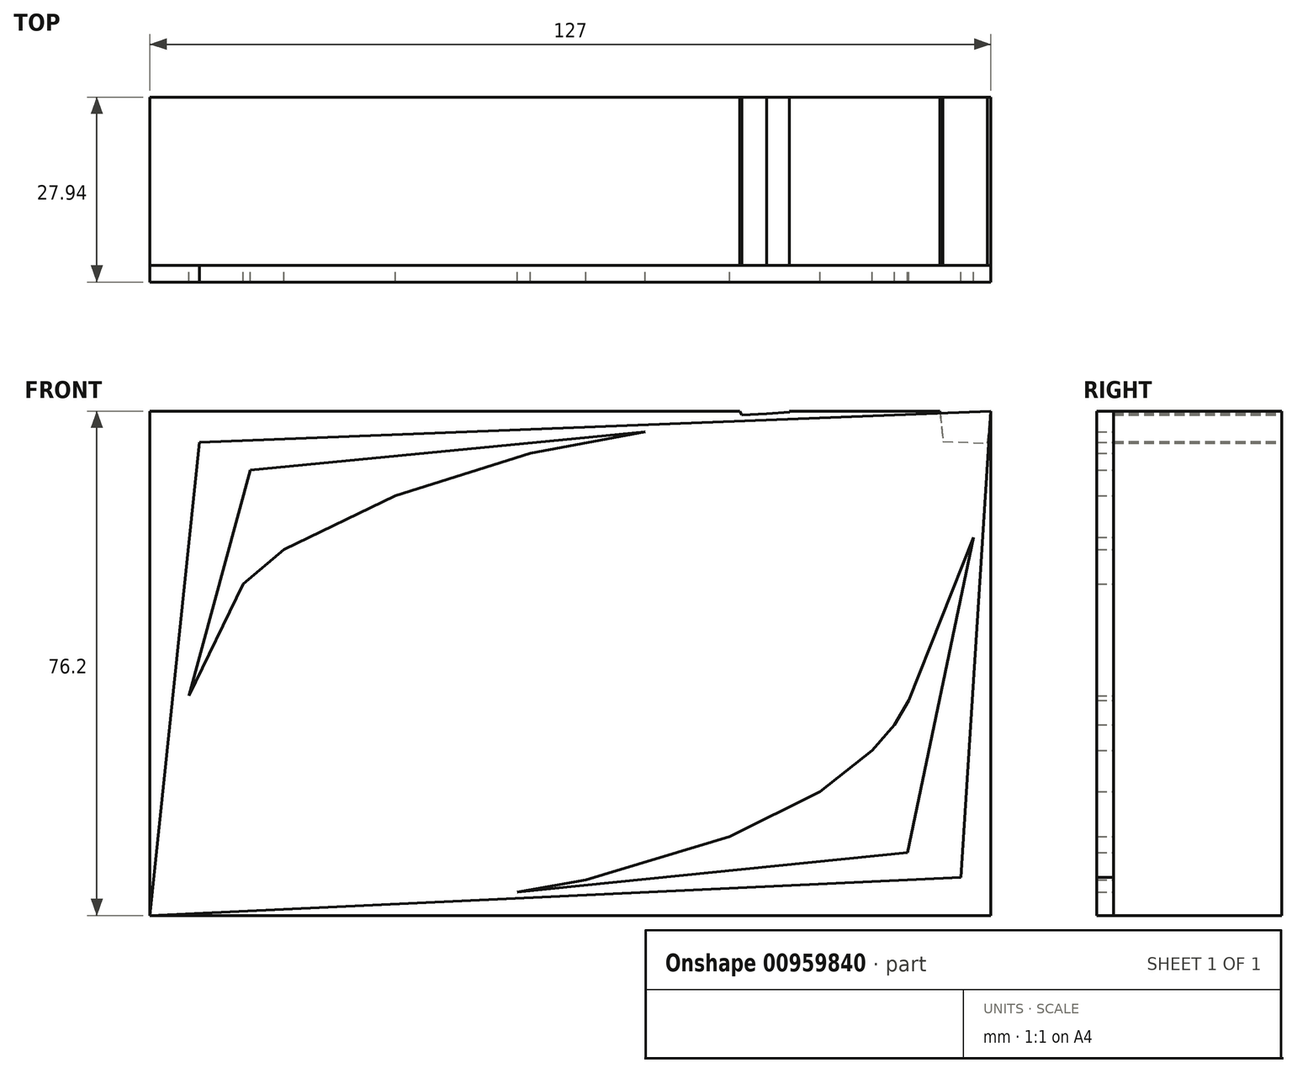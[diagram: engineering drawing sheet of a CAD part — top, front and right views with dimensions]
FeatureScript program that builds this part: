
annotation { "Feature Type Name" : "Feature", "Feature Type Description" : "" }
export const myFeature = defineFeature(function(context is Context, id is Id, definition is map)
    precondition{}
    {
        {
            var Q0;
            Q0=qCreatedBy(makeId("Front.planeOp"),FACE);
            var sketch = newSketch(context, id + "F0", { "sketchPlane" : qUnion([Q0])});
            skLineSegment(sketch, "E0.bottom", {"start": v(-63.5, -38.1) * mm, "end": v(63.5, -38.1) * mm});
            skLineSegment(sketch, "E0.top", {"start": v(-63.5, 38.1) * mm, "end": v(63.5, 38.1) * mm});
            skLineSegment(sketch, "E0.left", {"start": v(-63.5, -38.1) * mm, "end": v(-63.5, 38.1) * mm});
            skLineSegment(sketch, "E0.right", {"start": v(63.5, -38.1) * mm, "end": v(63.5, 38.1) * mm});
            skPoint(sketch, "E0.middle", {"position": v(0, 0) * mm});
            skLineSegment(sketch, "E1", {"start": v(-63.5, -38.1) * mm, "end": v(63.5, -30.09) * mm});
            skLineSegment(sketch, "E2", {"start": v(-48.57, -38.1) * mm, "end": v(63.5, -22.97) * mm});
            skLineSegment(sketch, "E3", {"start": v(-38.6, -38.1) * mm, "end": v(63.5, -16.2) * mm});
            skLineSegment(sketch, "E4", {"start": v(-28.65, -38.1) * mm, "end": v(63.5, -8.03) * mm});
            skLineSegment(sketch, "E5", {"start": v(-17.63, -38.1) * mm, "end": v(63.5, -2.7) * mm});
            skLineSegment(sketch, "E6", {"start": v(-6.25, -38.1) * mm, "end": v(63.5, 0) * mm});
            skLineSegment(sketch, "E7", {"start": v(4.78, -38.1) * mm, "end": v(63.5, 6.2) * mm});
            skLineSegment(sketch, "E8", {"start": v(14.74, -38.1) * mm, "end": v(63.5, 11.89) * mm});
            skLineSegment(sketch, "E9", {"start": v(22.91, -38.1) * mm, "end": v(63.5, 18.28) * mm});
            skLineSegment(sketch, "E10", {"start": v(28.6, -38.1) * mm, "end": v(63.5, 23.27) * mm});
            skLineSegment(sketch, "E11", {"start": v(33.59, -38.1) * mm, "end": v(63.5, 29.32) * mm});
            skLineSegment(sketch, "E12", {"start": v(42.12, -38.1) * mm, "end": v(63.5, 33.23) * mm});
            skLineSegment(sketch, "E13", {"start": v(49.59, -38.1) * mm, "end": v(63.5, 33.23) * mm});
            skLineSegment(sketch, "E14", {"start": v(55.63, -38.1) * mm, "end": v(63.5, 38.1) * mm});
            skLineSegment(sketch, "E15", {"start": v(63.5, -38.1) * mm, "end": v(-63.5, -29.2) * mm});
            skLineSegment(sketch, "E16", {"start": v(55.63, -38.1) * mm, "end": v(-63.5, -21.73) * mm});
            skLineSegment(sketch, "E17", {"start": v(42.12, -38.1) * mm, "end": v(-63.5, -15.34) * mm});
            skLineSegment(sketch, "E18", {"start": v(33.59, -38.1) * mm, "end": v(-63.5, -10.35) * mm});
            skLineSegment(sketch, "E19", {"start": v(22.91, -38.1) * mm, "end": v(-63.5, -4.3) * mm});
            skLineSegment(sketch, "E20", {"start": v(14.74, -38.1) * mm, "end": v(-63.5, 0) * mm});
            skLineSegment(sketch, "E21", {"start": v(4.78, -38.1) * mm, "end": v(-63.5, 4.94) * mm});
            skLineSegment(sketch, "E22", {"start": v(-6.25, -38.1) * mm, "end": v(-63.5, 9.2) * mm});
            skLineSegment(sketch, "E23", {"start": v(-17.63, -38.1) * mm, "end": v(-63.5, 14.2) * mm});
            skLineSegment(sketch, "E24", {"start": v(-28.65, -38.1) * mm, "end": v(-63.5, 22.38) * mm});
            skLineSegment(sketch, "E25", {"start": v(-38.6, -38.1) * mm, "end": v(-63.5, 29.84) * mm});
            skLineSegment(sketch, "E26", {"start": v(-48.57, -38.1) * mm, "end": v(-63.5, 33.39) * mm});
            skLineSegment(sketch, "E27", {"start": v(-57.13, -37.7) * mm, "end": v(-63.5, 38.1) * mm});
            skLineSegment(sketch, "E28", {"start": v(-63.5, 38.1) * mm, "end": v(63.5, 33.23) * mm});
            skLineSegment(sketch, "E29", {"start": v(-56.64, 37.84) * mm, "end": v(63.5, 29.32) * mm});
            skLineSegment(sketch, "E30", {"start": v(-49.83, 38.1) * mm, "end": v(63.5, 23.27) * mm});
            skLineSegment(sketch, "E31", {"start": v(-42, 38.1) * mm, "end": v(63.5, 18.28) * mm});
            skLineSegment(sketch, "E32", {"start": v(-33.47, 38.1) * mm, "end": v(63.5, 11.89) * mm});
            skLineSegment(sketch, "E33", {"start": v(-25.3, 38.1) * mm, "end": v(63.5, 6.2) * mm});
            skLineSegment(sketch, "E34", {"start": v(-17.11, 38.1) * mm, "end": v(63.5, 0) * mm});
            skLineSegment(sketch, "E35", {"start": v(-9.65, 38.1) * mm, "end": v(63.5, -2.7) * mm});
            skLineSegment(sketch, "E36", {"start": v(0, 38.1) * mm, "end": v(63.5, -8.03) * mm});
            skLineSegment(sketch, "E37", {"start": v(7.43, 38.1) * mm, "end": v(63.5, -16.2) * mm});
            skLineSegment(sketch, "E38", {"start": v(13.84, 38.1) * mm, "end": v(63.5, -22.97) * mm});
            skLineSegment(sketch, "E39", {"start": v(25.57, 38.1) * mm, "end": v(63.5, -30.09) * mm});
            skLineSegment(sketch, "E40", {"start": v(33.04, 38.1) * mm, "end": v(63.5, -33.99) * mm});
            skLineSegment(sketch, "E41", {"start": v(39.09, 38.1) * mm, "end": v(63.5, -30.09) * mm});
            skLineSegment(sketch, "E42", {"start": v(48.32, 38.1) * mm, "end": v(63.5, -33.99) * mm});
            skLineSegment(sketch, "E43", {"start": v(55.8, 38.1) * mm, "end": v(63.5, -38.1) * mm});
            skLineSegment(sketch, "E44", {"start": v(-63.5, -38.1) * mm, "end": v(-56.64, 37.84) * mm});
            skLineSegment(sketch, "E45", {"start": v(-63.5, -29.2) * mm, "end": v(-49.83, 38.1) * mm});
            skLineSegment(sketch, "E46", {"start": v(-63.5, -21.73) * mm, "end": v(-42, 38.1) * mm});
            skLineSegment(sketch, "E47", {"start": v(-63.5, -15.34) * mm, "end": v(-33.47, 38.1) * mm});
            skLineSegment(sketch, "E48", {"start": v(-63.5, -10.35) * mm, "end": v(-25.3, 38.1) * mm});
            skLineSegment(sketch, "E49", {"start": v(-63.5, -4.3) * mm, "end": v(-17.11, 38.1) * mm});
            skLineSegment(sketch, "E50", {"start": v(-63.5, 0) * mm, "end": v(-9.65, 38.1) * mm});
            skLineSegment(sketch, "E51", {"start": v(-63.5, 4.94) * mm, "end": v(0, 38.1) * mm});
            skLineSegment(sketch, "E52", {"start": v(-63.5, 9.2) * mm, "end": v(7.43, 38.1) * mm});
            skLineSegment(sketch, "E53", {"start": v(-63.5, 14.2) * mm, "end": v(13.84, 38.1) * mm});
            skLineSegment(sketch, "E54", {"start": v(-61.95, 19.7) * mm, "end": v(13.84, 38.1) * mm});
            skLineSegment(sketch, "E55", {"start": v(-63.5, 22.38) * mm, "end": v(25.57, 38.1) * mm});
            skLineSegment(sketch, "E56", {"start": v(-62.6, 27.38) * mm, "end": v(25.57, 38.1) * mm});
            skLineSegment(sketch, "E57", {"start": v(-63.5, 29.84) * mm, "end": v(34.8, 38.1) * mm});
            skLineSegment(sketch, "E58", {"start": v(-63.5, 33.39) * mm, "end": v(39.09, 38.1) * mm});
            skLineSegment(sketch, "E59", {"start": v(-63.5, 38.1) * mm, "end": v(59.36, 38.1) * mm});
            skSolve(sketch);
        }
        {
            var Q0;
            {var subQ0=sQuery(id+"F0.wireOp",EDGE,"E2");var subQ3=sQuery(id+"F0.wireOp",EDGE,"E25");var subQ5=makeQuery(id+"F0.imprint","INTERSECT",VERTEX,{"derivedFrom":[subQ0,subQ3]});Q0=makeQuery(id+"F0.imprint","IMPRINT",FACE,{"disambiguationData":[TD([[makeQuery(id+"F0.imprint","IMPRINT",EDGE,{"disambiguationData":[TD([[subQ5,1.0]])],"derivedFrom":subQ0}),-1.0]])]});}
            var Q1;
            {var subQ0=sQuery(id+"F0.wireOp",EDGE,"E3");var subQ3=sQuery(id+"F0.wireOp",EDGE,"E24");var subQ5=makeQuery(id+"F0.imprint","INTERSECT",VERTEX,{"derivedFrom":[subQ0,subQ3]});Q1=makeQuery(id+"F0.imprint","IMPRINT",FACE,{"disambiguationData":[TD([[makeQuery(id+"F0.imprint","IMPRINT",EDGE,{"disambiguationData":[TD([[subQ5,1.0]])],"derivedFrom":subQ0}),-1.0]])]});}
            var Q2;
            {var subQ0=sQuery(id+"F0.wireOp",EDGE,"E5");var subQ3=sQuery(id+"F0.wireOp",EDGE,"E22");var subQ5=makeQuery(id+"F0.imprint","INTERSECT",VERTEX,{"derivedFrom":[subQ0,subQ3]});Q2=makeQuery(id+"F0.imprint","IMPRINT",FACE,{"disambiguationData":[TD([[makeQuery(id+"F0.imprint","IMPRINT",EDGE,{"disambiguationData":[TD([[subQ5,1.0]])],"derivedFrom":subQ0}),-1.0]])]});}
            var Q3;
            {var subQ0=sQuery(id+"F0.wireOp",EDGE,"E6");var subQ3=sQuery(id+"F0.wireOp",EDGE,"E21");var subQ5=makeQuery(id+"F0.imprint","INTERSECT",VERTEX,{"derivedFrom":[subQ0,subQ3]});Q3=makeQuery(id+"F0.imprint","IMPRINT",FACE,{"disambiguationData":[TD([[makeQuery(id+"F0.imprint","IMPRINT",EDGE,{"disambiguationData":[TD([[subQ5,1.0]])],"derivedFrom":subQ0}),-1.0]])]});}
            var Q4;
            {var subQ0=sQuery(id+"F0.wireOp",EDGE,"E7");var subQ3=sQuery(id+"F0.wireOp",EDGE,"E20");var subQ5=makeQuery(id+"F0.imprint","INTERSECT",VERTEX,{"derivedFrom":[subQ0,subQ3]});Q4=makeQuery(id+"F0.imprint","IMPRINT",FACE,{"disambiguationData":[TD([[makeQuery(id+"F0.imprint","IMPRINT",EDGE,{"disambiguationData":[TD([[subQ5,1.0]])],"derivedFrom":subQ0}),-1.0]])]});}
            var Q5;
            {var subQ0=sQuery(id+"F0.wireOp",EDGE,"E8");var subQ3=sQuery(id+"F0.wireOp",EDGE,"E19");var subQ5=makeQuery(id+"F0.imprint","INTERSECT",VERTEX,{"derivedFrom":[subQ0,subQ3]});Q5=makeQuery(id+"F0.imprint","IMPRINT",FACE,{"disambiguationData":[TD([[makeQuery(id+"F0.imprint","IMPRINT",EDGE,{"disambiguationData":[TD([[subQ5,1.0]])],"derivedFrom":subQ0}),-1.0]])]});}
            var Q6;
            {var subQ0=sQuery(id+"F0.wireOp",EDGE,"E10");var subQ1=sQuery(id+"F0.wireOp",EDGE,"E0.bottom");var subQ2=makeQuery(id+"F0.imprint","INTERSECT",VERTEX,{"derivedFrom":[subQ1,subQ0]});Q6=makeQuery(id+"F0.imprint","IMPRINT",FACE,{"disambiguationData":[TD([[makeQuery(id+"F0.imprint","IMPRINT",EDGE,{"disambiguationData":[TD([[subQ2,-1.0]])],"derivedFrom":subQ0}),-1.0]])]});}
            var Q7;
            {var subQ0=sQuery(id+"F0.wireOp",EDGE,"E11");var subQ3=sQuery(id+"F0.wireOp",EDGE,"E17");var subQ5=makeQuery(id+"F0.imprint","INTERSECT",VERTEX,{"derivedFrom":[subQ0,subQ3]});Q7=makeQuery(id+"F0.imprint","IMPRINT",FACE,{"disambiguationData":[TD([[makeQuery(id+"F0.imprint","IMPRINT",EDGE,{"disambiguationData":[TD([[subQ5,1.0]])],"derivedFrom":subQ0}),-1.0]])]});}
            var Q8;
            {var subQ0=sQuery(id+"F0.wireOp",EDGE,"E13");var subQ1=sQuery(id+"F0.wireOp",EDGE,"E0.bottom");var subQ2=makeQuery(id+"F0.imprint","INTERSECT",VERTEX,{"derivedFrom":[subQ1,subQ0]});Q8=makeQuery(id+"F0.imprint","IMPRINT",FACE,{"disambiguationData":[TD([[makeQuery(id+"F0.imprint","IMPRINT",EDGE,{"disambiguationData":[TD([[subQ2,-1.0]])],"derivedFrom":subQ0}),-1.0]])]});}
            var Q9;
            {var subQ0=sQuery(id+"F0.wireOp",EDGE,"E15");var subQ3=sQuery(id+"F0.wireOp",EDGE,"E14");var subQ5=makeQuery(id+"F0.imprint","INTERSECT",VERTEX,{"derivedFrom":[subQ3,subQ0]});Q9=makeQuery(id+"F0.imprint","IMPRINT",FACE,{"disambiguationData":[TD([[makeQuery(id+"F0.imprint","IMPRINT",EDGE,{"disambiguationData":[TD([[subQ5,1.0]])],"derivedFrom":subQ3}),-1.0]])]});}
            var Q10;
            {var subQ0=sQuery(id+"F0.wireOp",EDGE,"E44");var subQ3=sQuery(id+"F0.wireOp",EDGE,"E15");var subQ5=makeQuery(id+"F0.imprint","INTERSECT",VERTEX,{"derivedFrom":[subQ3,subQ0]});Q10=makeQuery(id+"F0.imprint","IMPRINT",FACE,{"disambiguationData":[TD([[makeQuery(id+"F0.imprint","IMPRINT",EDGE,{"disambiguationData":[TD([[subQ5,-1.0]])],"derivedFrom":subQ3}),1.0]])]});}
            var Q11;
            {var subQ0=sQuery(id+"F0.wireOp",EDGE,"E47");var subQ3=sQuery(id+"F0.wireOp",EDGE,"E18");var subQ5=makeQuery(id+"F0.imprint","INTERSECT",VERTEX,{"derivedFrom":[subQ3,subQ0]});Q11=makeQuery(id+"F0.imprint","IMPRINT",FACE,{"disambiguationData":[TD([[makeQuery(id+"F0.imprint","IMPRINT",EDGE,{"disambiguationData":[TD([[subQ5,-1.0]])],"derivedFrom":subQ3}),1.0]])]});}
            var Q12;
            {var subQ0=sQuery(id+"F0.wireOp",EDGE,"E49");var subQ3=sQuery(id+"F0.wireOp",EDGE,"E20");var subQ5=makeQuery(id+"F0.imprint","INTERSECT",VERTEX,{"derivedFrom":[subQ3,subQ0]});Q12=makeQuery(id+"F0.imprint","IMPRINT",FACE,{"disambiguationData":[TD([[makeQuery(id+"F0.imprint","IMPRINT",EDGE,{"disambiguationData":[TD([[subQ5,-1.0]])],"derivedFrom":subQ3}),1.0]])]});}
            var Q13;
            {var subQ0=sQuery(id+"F0.wireOp",EDGE,"E27");var subQ3=sQuery(id+"F0.wireOp",EDGE,"E58");var subQ5=makeQuery(id+"F0.imprint","INTERSECT",VERTEX,{"derivedFrom":[subQ0,subQ3]});Q13=makeQuery(id+"F0.imprint","IMPRINT",FACE,{"disambiguationData":[TD([[makeQuery(id+"F0.imprint","IMPRINT",EDGE,{"disambiguationData":[TD([[subQ5,1.0]])],"derivedFrom":subQ3}),1.0]])]});}
            var Q14;
            {var subQ0=sQuery(id+"F0.wireOp",EDGE,"E43");var subQ3=sQuery(id+"F0.wireOp",EDGE,"E40");var subQ5=makeQuery(id+"F0.imprint","INTERSECT",VERTEX,{"derivedFrom":[subQ3,subQ0]});Q14=makeQuery(id+"F0.imprint","IMPRINT",FACE,{"disambiguationData":[TD([[makeQuery(id+"F0.imprint","IMPRINT",EDGE,{"disambiguationData":[TD([[subQ5,-1.0]])],"derivedFrom":subQ3}),-1.0]])]});}
            var Q15;
            {var subQ0=sQuery(id+"F0.wireOp",EDGE,"E35");var subQ3=sQuery(id+"F0.wireOp",EDGE,"E6");var subQ5=makeQuery(id+"F0.imprint","INTERSECT",VERTEX,{"derivedFrom":[subQ3,subQ0]});Q15=makeQuery(id+"F0.imprint","IMPRINT",FACE,{"disambiguationData":[TD([[makeQuery(id+"F0.imprint","IMPRINT",EDGE,{"disambiguationData":[TD([[subQ5,-1.0]])],"derivedFrom":subQ3}),-1.0]])]});}
            var Q16;
            {var subQ0=sQuery(id+"F0.wireOp",EDGE,"E29");var subQ3=sQuery(id+"F0.wireOp",EDGE,"E13");var subQ5=makeQuery(id+"F0.imprint","INTERSECT",VERTEX,{"derivedFrom":[subQ3,subQ0]});Q16=makeQuery(id+"F0.imprint","IMPRINT",FACE,{"disambiguationData":[TD([[makeQuery(id+"F0.imprint","IMPRINT",EDGE,{"disambiguationData":[TD([[subQ5,-1.0]])],"derivedFrom":subQ0}),1.0]])]});}
            var Q17;
            {var subQ0=sQuery(id+"F0.wireOp",EDGE,"E14");var subQ3=sQuery(id+"F0.wireOp",EDGE,"E28");var subQ5=makeQuery(id+"F0.imprint","INTERSECT",VERTEX,{"derivedFrom":[subQ0,subQ3]});Q17=makeQuery(id+"F0.imprint","IMPRINT",FACE,{"disambiguationData":[TD([[makeQuery(id+"F0.imprint","IMPRINT",EDGE,{"disambiguationData":[TD([[subQ5,-1.0]])],"derivedFrom":subQ0}),-1.0]])]});}
            var Q18;
            {var subQ1=sQuery(id+"F0.wireOp",EDGE,"E37");var subQ3=sQuery(id+"F0.wireOp",EDGE,"E54");var subQ4=makeQuery(id+"F0.imprint","INTERSECT",VERTEX,{"derivedFrom":[subQ1,subQ3]});Q18=makeQuery(id+"F0.imprint","IMPRINT",FACE,{"disambiguationData":[TD([[makeQuery(id+"F0.imprint","IMPRINT",EDGE,{"disambiguationData":[TD([[subQ4,1.0]])],"derivedFrom":subQ1}),1.0]])]});}
            var Q19;
            {var subQ0=sQuery(id+"F0.wireOp",EDGE,"E59");var subQ1=sQuery(id+"F0.wireOp",EDGE,"E40");var subQ2=makeQuery(id+"F0.imprint","INTERSECT",VERTEX,{"derivedFrom":[subQ1,subQ0]});Q19=makeQuery(id+"F0.imprint","IMPRINT",FACE,{"disambiguationData":[TD([[makeQuery(id+"F0.imprint","IMPRINT",EDGE,{"disambiguationData":[TD([[subQ2,-1.0]])],"derivedFrom":subQ1}),1.0]])]});}
            var Q20;
            {var subQ0=sQuery(id+"F0.wireOp",EDGE,"E1");var subQ5=makeQuery(id+"F0.imprint","INTERSECT",VERTEX,{"derivedFrom":[subQ0,sQuery(id+"F0.wireOp",EDGE,"E27")]});Q20=makeQuery(id+"F0.imprint","IMPRINT",FACE,{"disambiguationData":[TD([[makeQuery(id+"F0.imprint","IMPRINT",EDGE,{"disambiguationData":[TD([[subQ5,-1.0]])],"derivedFrom":subQ0}),-1.0]])]});}
            var Q21;
            {var subQ0=sQuery(id+"F0.wireOp",EDGE,"E4");var subQ5=sQuery(id+"F0.wireOp",EDGE,"E1");var subQ6=makeQuery(id+"F0.imprint","INTERSECT",VERTEX,{"derivedFrom":[subQ5,subQ0]});Q21=makeQuery(id+"F0.imprint","IMPRINT",FACE,{"disambiguationData":[TD([[makeQuery(id+"F0.imprint","IMPRINT",EDGE,{"disambiguationData":[TD([[subQ6,-1.0]])],"derivedFrom":subQ5}),-1.0]])]});}
            var Q22;
            {var subQ1=sQuery(id+"F0.wireOp",EDGE,"E0.bottom");var subQ3=sQuery(id+"F0.wireOp",EDGE,"E10");var subQ4=makeQuery(id+"F0.imprint","INTERSECT",VERTEX,{"derivedFrom":[subQ1,subQ3]});Q22=makeQuery(id+"F0.imprint","IMPRINT",FACE,{"disambiguationData":[TD([[makeQuery(id+"F0.imprint","IMPRINT",EDGE,{"disambiguationData":[TD([[subQ4,-1.0]])],"derivedFrom":subQ3}),1.0]])]});}
            var Q23;
            {var subQ7=sQuery(id+"F0.wireOp",EDGE,"E0.top");Q23=makeQuery(id+"F0.imprint","IMPRINT",FACE,{"disambiguationData":[TD([[makeQuery(id+"F0.imprint","IMPRINT",EDGE,{"derivedFrom":subQ7}),-1.0]])]});}
            var Q24;
            {var subQ3=sQuery(id+"F0.wireOp",EDGE,"E16");var subQ5=sQuery(id+"F0.wireOp",EDGE,"E44");var subQ6=makeQuery(id+"F0.imprint","INTERSECT",VERTEX,{"derivedFrom":[subQ3,subQ5]});Q24=makeQuery(id+"F0.imprint","IMPRINT",FACE,{"disambiguationData":[TD([[makeQuery(id+"F0.imprint","IMPRINT",EDGE,{"disambiguationData":[TD([[subQ6,1.0]])],"derivedFrom":subQ5}),1.0]])]});}
            var Q25;
            {var subQ3=sQuery(id+"F0.wireOp",EDGE,"E17");var subQ5=sQuery(id+"F0.wireOp",EDGE,"E44");var subQ6=makeQuery(id+"F0.imprint","INTERSECT",VERTEX,{"derivedFrom":[subQ3,subQ5]});Q25=makeQuery(id+"F0.imprint","IMPRINT",FACE,{"disambiguationData":[TD([[makeQuery(id+"F0.imprint","IMPRINT",EDGE,{"disambiguationData":[TD([[subQ6,1.0]])],"derivedFrom":subQ5}),1.0]])]});}
            var Q26;
            {var subQ3=sQuery(id+"F0.wireOp",EDGE,"E19");var subQ5=sQuery(id+"F0.wireOp",EDGE,"E44");var subQ6=makeQuery(id+"F0.imprint","INTERSECT",VERTEX,{"derivedFrom":[subQ3,subQ5]});Q26=makeQuery(id+"F0.imprint","IMPRINT",FACE,{"disambiguationData":[TD([[makeQuery(id+"F0.imprint","IMPRINT",EDGE,{"disambiguationData":[TD([[subQ6,1.0]])],"derivedFrom":subQ5}),1.0]])]});}
            var Q27;
            {var subQ3=sQuery(id+"F0.wireOp",EDGE,"E21");var subQ5=sQuery(id+"F0.wireOp",EDGE,"E27");var subQ6=makeQuery(id+"F0.imprint","INTERSECT",VERTEX,{"derivedFrom":[subQ3,subQ5]});Q27=makeQuery(id+"F0.imprint","IMPRINT",FACE,{"disambiguationData":[TD([[makeQuery(id+"F0.imprint","IMPRINT",EDGE,{"disambiguationData":[TD([[subQ6,1.0]])],"derivedFrom":subQ5}),1.0]])]});}
            var Q28;
            {var subQ3=sQuery(id+"F0.wireOp",EDGE,"E22");var subQ5=sQuery(id+"F0.wireOp",EDGE,"E27");var subQ6=makeQuery(id+"F0.imprint","INTERSECT",VERTEX,{"derivedFrom":[subQ3,subQ5]});Q28=makeQuery(id+"F0.imprint","IMPRINT",FACE,{"disambiguationData":[TD([[makeQuery(id+"F0.imprint","IMPRINT",EDGE,{"disambiguationData":[TD([[subQ6,1.0]])],"derivedFrom":subQ5}),1.0]])]});}
            var Q29;
            {var subQ3=sQuery(id+"F0.wireOp",EDGE,"E23");var subQ5=sQuery(id+"F0.wireOp",EDGE,"E27");var subQ6=makeQuery(id+"F0.imprint","INTERSECT",VERTEX,{"derivedFrom":[subQ3,subQ5]});Q29=makeQuery(id+"F0.imprint","IMPRINT",FACE,{"disambiguationData":[TD([[makeQuery(id+"F0.imprint","IMPRINT",EDGE,{"disambiguationData":[TD([[subQ6,1.0]])],"derivedFrom":subQ5}),1.0]])]});}
            var Q30;
            {var subQ0=sQuery(id+"F0.wireOp",EDGE,"E53");var subQ5=sQuery(id+"F0.wireOp",EDGE,"E27");var subQ7=makeQuery(id+"F0.imprint","INTERSECT",VERTEX,{"derivedFrom":[subQ5,subQ0]});Q30=makeQuery(id+"F0.imprint","IMPRINT",FACE,{"disambiguationData":[TD([[makeQuery(id+"F0.imprint","IMPRINT",EDGE,{"disambiguationData":[TD([[subQ7,-1.0]])],"derivedFrom":subQ5}),1.0]])]});}
            var Q31;
            {var subQ0=sQuery(id+"F0.wireOp",EDGE,"E55");var subQ5=sQuery(id+"F0.wireOp",EDGE,"E27");var subQ7=makeQuery(id+"F0.imprint","INTERSECT",VERTEX,{"derivedFrom":[subQ5,subQ0]});Q31=makeQuery(id+"F0.imprint","IMPRINT",FACE,{"disambiguationData":[TD([[makeQuery(id+"F0.imprint","IMPRINT",EDGE,{"disambiguationData":[TD([[subQ7,-1.0]])],"derivedFrom":subQ5}),1.0]])]});}
            var Q32;
            {var subQ3=sQuery(id+"F0.wireOp",EDGE,"E26");var subQ5=sQuery(id+"F0.wireOp",EDGE,"E27");var subQ6=makeQuery(id+"F0.imprint","INTERSECT",VERTEX,{"derivedFrom":[subQ3,subQ5]});Q32=makeQuery(id+"F0.imprint","IMPRINT",FACE,{"disambiguationData":[TD([[makeQuery(id+"F0.imprint","IMPRINT",EDGE,{"disambiguationData":[TD([[subQ6,1.0]])],"derivedFrom":subQ5}),1.0]])]});}
            var Q33;
            {var subQ0=sQuery(id+"F0.wireOp",EDGE,"E1");var subQ5=sQuery(id+"F0.wireOp",EDGE,"E43");var subQ6=makeQuery(id+"F0.imprint","INTERSECT",VERTEX,{"derivedFrom":[subQ0,subQ5]});Q33=makeQuery(id+"F0.imprint","IMPRINT",FACE,{"disambiguationData":[TD([[makeQuery(id+"F0.imprint","IMPRINT",EDGE,{"disambiguationData":[TD([[subQ6,-1.0]])],"derivedFrom":subQ5}),1.0]])]});}
            var Q34;
            {var subQ3=sQuery(id+"F0.wireOp",EDGE,"E2");var subQ5=sQuery(id+"F0.wireOp",EDGE,"E43");var subQ6=makeQuery(id+"F0.imprint","INTERSECT",VERTEX,{"derivedFrom":[subQ3,subQ5]});Q34=makeQuery(id+"F0.imprint","IMPRINT",FACE,{"disambiguationData":[TD([[makeQuery(id+"F0.imprint","IMPRINT",EDGE,{"disambiguationData":[TD([[subQ6,-1.0]])],"derivedFrom":subQ5}),1.0]])]});}
            var Q35;
            {var subQ3=sQuery(id+"F0.wireOp",EDGE,"E3");var subQ5=sQuery(id+"F0.wireOp",EDGE,"E43");var subQ6=makeQuery(id+"F0.imprint","INTERSECT",VERTEX,{"derivedFrom":[subQ3,subQ5]});Q35=makeQuery(id+"F0.imprint","IMPRINT",FACE,{"disambiguationData":[TD([[makeQuery(id+"F0.imprint","IMPRINT",EDGE,{"disambiguationData":[TD([[subQ6,-1.0]])],"derivedFrom":subQ5}),1.0]])]});}
            var Q36;
            {var subQ3=sQuery(id+"F0.wireOp",EDGE,"E4");var subQ5=sQuery(id+"F0.wireOp",EDGE,"E43");var subQ6=makeQuery(id+"F0.imprint","INTERSECT",VERTEX,{"derivedFrom":[subQ3,subQ5]});Q36=makeQuery(id+"F0.imprint","IMPRINT",FACE,{"disambiguationData":[TD([[makeQuery(id+"F0.imprint","IMPRINT",EDGE,{"disambiguationData":[TD([[subQ6,-1.0]])],"derivedFrom":subQ5}),1.0]])]});}
            var Q37;
            {var subQ3=sQuery(id+"F0.wireOp",EDGE,"E5");var subQ5=sQuery(id+"F0.wireOp",EDGE,"E43");var subQ6=makeQuery(id+"F0.imprint","INTERSECT",VERTEX,{"derivedFrom":[subQ3,subQ5]});Q37=makeQuery(id+"F0.imprint","IMPRINT",FACE,{"disambiguationData":[TD([[makeQuery(id+"F0.imprint","IMPRINT",EDGE,{"disambiguationData":[TD([[subQ6,-1.0]])],"derivedFrom":subQ5}),1.0]])]});}
            var Q38;
            {var subQ3=sQuery(id+"F0.wireOp",EDGE,"E7");var subQ5=sQuery(id+"F0.wireOp",EDGE,"E14");var subQ6=makeQuery(id+"F0.imprint","INTERSECT",VERTEX,{"derivedFrom":[subQ3,subQ5]});Q38=makeQuery(id+"F0.imprint","IMPRINT",FACE,{"disambiguationData":[TD([[makeQuery(id+"F0.imprint","IMPRINT",EDGE,{"disambiguationData":[TD([[subQ6,1.0]])],"derivedFrom":subQ5}),-1.0]])]});}
            var Q39;
            {var subQ3=sQuery(id+"F0.wireOp",EDGE,"E8");var subQ5=sQuery(id+"F0.wireOp",EDGE,"E14");var subQ6=makeQuery(id+"F0.imprint","INTERSECT",VERTEX,{"derivedFrom":[subQ3,subQ5]});Q39=makeQuery(id+"F0.imprint","IMPRINT",FACE,{"disambiguationData":[TD([[makeQuery(id+"F0.imprint","IMPRINT",EDGE,{"disambiguationData":[TD([[subQ6,1.0]])],"derivedFrom":subQ5}),-1.0]])]});}
            var Q40;
            {var subQ3=sQuery(id+"F0.wireOp",EDGE,"E9");var subQ5=sQuery(id+"F0.wireOp",EDGE,"E14");var subQ6=makeQuery(id+"F0.imprint","INTERSECT",VERTEX,{"derivedFrom":[subQ3,subQ5]});Q40=makeQuery(id+"F0.imprint","IMPRINT",FACE,{"disambiguationData":[TD([[makeQuery(id+"F0.imprint","IMPRINT",EDGE,{"disambiguationData":[TD([[subQ6,1.0]])],"derivedFrom":subQ5}),-1.0]])]});}
            var Q41;
            {var subQ3=sQuery(id+"F0.wireOp",EDGE,"E10");var subQ5=sQuery(id+"F0.wireOp",EDGE,"E14");var subQ6=makeQuery(id+"F0.imprint","INTERSECT",VERTEX,{"derivedFrom":[subQ3,subQ5]});Q41=makeQuery(id+"F0.imprint","IMPRINT",FACE,{"disambiguationData":[TD([[makeQuery(id+"F0.imprint","IMPRINT",EDGE,{"disambiguationData":[TD([[subQ6,1.0]])],"derivedFrom":subQ5}),-1.0]])]});}
            var Q42;
            {var subQ3=sQuery(id+"F0.wireOp",EDGE,"E11");var subQ5=sQuery(id+"F0.wireOp",EDGE,"E14");var subQ6=makeQuery(id+"F0.imprint","INTERSECT",VERTEX,{"derivedFrom":[subQ3,subQ5]});Q42=makeQuery(id+"F0.imprint","IMPRINT",FACE,{"disambiguationData":[TD([[makeQuery(id+"F0.imprint","IMPRINT",EDGE,{"disambiguationData":[TD([[subQ6,1.0]])],"derivedFrom":subQ5}),-1.0]])]});}
            var Q43;
            {var subQ1=sQuery(id+"F0.wireOp",EDGE,"E1");var subQ3=sQuery(id+"F0.wireOp",EDGE,"E43");var subQ4=makeQuery(id+"F0.imprint","INTERSECT",VERTEX,{"derivedFrom":[subQ1,subQ3]});Q43=makeQuery(id+"F0.imprint","IMPRINT",FACE,{"disambiguationData":[TD([[makeQuery(id+"F0.imprint","IMPRINT",EDGE,{"disambiguationData":[TD([[subQ4,1.0]])],"derivedFrom":subQ3}),1.0]])]});}
            var Q44;
            {var subQ1=sQuery(id+"F0.wireOp",EDGE,"E2");var subQ3=sQuery(id+"F0.wireOp",EDGE,"E43");var subQ4=makeQuery(id+"F0.imprint","INTERSECT",VERTEX,{"derivedFrom":[subQ1,subQ3]});Q44=makeQuery(id+"F0.imprint","IMPRINT",FACE,{"disambiguationData":[TD([[makeQuery(id+"F0.imprint","IMPRINT",EDGE,{"disambiguationData":[TD([[subQ4,1.0]])],"derivedFrom":subQ3}),1.0]])]});}
            var Q45;
            {var subQ1=sQuery(id+"F0.wireOp",EDGE,"E3");var subQ3=sQuery(id+"F0.wireOp",EDGE,"E43");var subQ4=makeQuery(id+"F0.imprint","INTERSECT",VERTEX,{"derivedFrom":[subQ1,subQ3]});Q45=makeQuery(id+"F0.imprint","IMPRINT",FACE,{"disambiguationData":[TD([[makeQuery(id+"F0.imprint","IMPRINT",EDGE,{"disambiguationData":[TD([[subQ4,1.0]])],"derivedFrom":subQ3}),1.0]])]});}
            var Q46;
            {var subQ1=sQuery(id+"F0.wireOp",EDGE,"E4");var subQ3=sQuery(id+"F0.wireOp",EDGE,"E43");var subQ4=makeQuery(id+"F0.imprint","INTERSECT",VERTEX,{"derivedFrom":[subQ1,subQ3]});Q46=makeQuery(id+"F0.imprint","IMPRINT",FACE,{"disambiguationData":[TD([[makeQuery(id+"F0.imprint","IMPRINT",EDGE,{"disambiguationData":[TD([[subQ4,1.0]])],"derivedFrom":subQ3}),1.0]])]});}
            var Q47;
            {var subQ1=sQuery(id+"F0.wireOp",EDGE,"E7");var subQ3=sQuery(id+"F0.wireOp",EDGE,"E14");var subQ4=makeQuery(id+"F0.imprint","INTERSECT",VERTEX,{"derivedFrom":[subQ1,subQ3]});Q47=makeQuery(id+"F0.imprint","IMPRINT",FACE,{"disambiguationData":[TD([[makeQuery(id+"F0.imprint","IMPRINT",EDGE,{"disambiguationData":[TD([[subQ4,-1.0]])],"derivedFrom":subQ3}),-1.0]])]});}
            var Q48;
            {var subQ1=sQuery(id+"F0.wireOp",EDGE,"E8");var subQ3=sQuery(id+"F0.wireOp",EDGE,"E14");var subQ4=makeQuery(id+"F0.imprint","INTERSECT",VERTEX,{"derivedFrom":[subQ1,subQ3]});Q48=makeQuery(id+"F0.imprint","IMPRINT",FACE,{"disambiguationData":[TD([[makeQuery(id+"F0.imprint","IMPRINT",EDGE,{"disambiguationData":[TD([[subQ4,-1.0]])],"derivedFrom":subQ3}),-1.0]])]});}
            var Q49;
            {var subQ1=sQuery(id+"F0.wireOp",EDGE,"E9");var subQ3=sQuery(id+"F0.wireOp",EDGE,"E14");var subQ4=makeQuery(id+"F0.imprint","INTERSECT",VERTEX,{"derivedFrom":[subQ1,subQ3]});Q49=makeQuery(id+"F0.imprint","IMPRINT",FACE,{"disambiguationData":[TD([[makeQuery(id+"F0.imprint","IMPRINT",EDGE,{"disambiguationData":[TD([[subQ4,-1.0]])],"derivedFrom":subQ3}),-1.0]])]});}
            var Q50;
            {var subQ1=sQuery(id+"F0.wireOp",EDGE,"E10");var subQ3=sQuery(id+"F0.wireOp",EDGE,"E14");var subQ4=makeQuery(id+"F0.imprint","INTERSECT",VERTEX,{"derivedFrom":[subQ1,subQ3]});Q50=makeQuery(id+"F0.imprint","IMPRINT",FACE,{"disambiguationData":[TD([[makeQuery(id+"F0.imprint","IMPRINT",EDGE,{"disambiguationData":[TD([[subQ4,-1.0]])],"derivedFrom":subQ3}),-1.0]])]});}
            var Q51;
            {var subQ1=sQuery(id+"F0.wireOp",EDGE,"E12");var subQ3=sQuery(id+"F0.wireOp",EDGE,"E14");var subQ4=makeQuery(id+"F0.imprint","INTERSECT",VERTEX,{"derivedFrom":[subQ1,subQ3]});Q51=makeQuery(id+"F0.imprint","IMPRINT",FACE,{"disambiguationData":[TD([[makeQuery(id+"F0.imprint","IMPRINT",EDGE,{"disambiguationData":[TD([[subQ4,-1.0]])],"derivedFrom":subQ3}),-1.0]])]});}
            var Q52;
            {var subQ1=sQuery(id+"F0.wireOp",EDGE,"E15");var subQ3=sQuery(id+"F0.wireOp",EDGE,"E44");var subQ4=makeQuery(id+"F0.imprint","INTERSECT",VERTEX,{"derivedFrom":[subQ1,subQ3]});Q52=makeQuery(id+"F0.imprint","IMPRINT",FACE,{"disambiguationData":[TD([[makeQuery(id+"F0.imprint","IMPRINT",EDGE,{"disambiguationData":[TD([[subQ4,-1.0]])],"derivedFrom":subQ3}),1.0]])]});}
            var Q53;
            {var subQ1=sQuery(id+"F0.wireOp",EDGE,"E16");var subQ3=sQuery(id+"F0.wireOp",EDGE,"E44");var subQ4=makeQuery(id+"F0.imprint","INTERSECT",VERTEX,{"derivedFrom":[subQ1,subQ3]});Q53=makeQuery(id+"F0.imprint","IMPRINT",FACE,{"disambiguationData":[TD([[makeQuery(id+"F0.imprint","IMPRINT",EDGE,{"disambiguationData":[TD([[subQ4,-1.0]])],"derivedFrom":subQ3}),1.0]])]});}
            var Q54;
            {var subQ1=sQuery(id+"F0.wireOp",EDGE,"E21");var subQ3=sQuery(id+"F0.wireOp",EDGE,"E27");var subQ4=makeQuery(id+"F0.imprint","INTERSECT",VERTEX,{"derivedFrom":[subQ1,subQ3]});Q54=makeQuery(id+"F0.imprint","IMPRINT",FACE,{"disambiguationData":[TD([[makeQuery(id+"F0.imprint","IMPRINT",EDGE,{"disambiguationData":[TD([[subQ4,-1.0]])],"derivedFrom":subQ3}),1.0]])]});}
            var Q55;
            {var subQ1=sQuery(id+"F0.wireOp",EDGE,"E22");var subQ3=sQuery(id+"F0.wireOp",EDGE,"E27");var subQ4=makeQuery(id+"F0.imprint","INTERSECT",VERTEX,{"derivedFrom":[subQ1,subQ3]});Q55=makeQuery(id+"F0.imprint","IMPRINT",FACE,{"disambiguationData":[TD([[makeQuery(id+"F0.imprint","IMPRINT",EDGE,{"disambiguationData":[TD([[subQ4,-1.0]])],"derivedFrom":subQ3}),1.0]])]});}
            var Q56;
            {var subQ1=sQuery(id+"F0.wireOp",EDGE,"E23");var subQ3=sQuery(id+"F0.wireOp",EDGE,"E27");var subQ4=makeQuery(id+"F0.imprint","INTERSECT",VERTEX,{"derivedFrom":[subQ1,subQ3]});Q56=makeQuery(id+"F0.imprint","IMPRINT",FACE,{"disambiguationData":[TD([[makeQuery(id+"F0.imprint","IMPRINT",EDGE,{"disambiguationData":[TD([[subQ4,-1.0]])],"derivedFrom":subQ3}),1.0]])]});}
            var Q57;
            {var subQ0=sQuery(id+"F0.wireOp",EDGE,"E55");var subQ3=sQuery(id+"F0.wireOp",EDGE,"E27");var subQ5=makeQuery(id+"F0.imprint","INTERSECT",VERTEX,{"derivedFrom":[subQ3,subQ0]});Q57=makeQuery(id+"F0.imprint","IMPRINT",FACE,{"disambiguationData":[TD([[makeQuery(id+"F0.imprint","IMPRINT",EDGE,{"disambiguationData":[TD([[subQ5,1.0]])],"derivedFrom":subQ3}),1.0]])]});}
            var Q58;
            {var subQ0=sQuery(id+"F0.wireOp",EDGE,"E57");var subQ3=sQuery(id+"F0.wireOp",EDGE,"E27");var subQ5=makeQuery(id+"F0.imprint","INTERSECT",VERTEX,{"derivedFrom":[subQ3,subQ0]});Q58=makeQuery(id+"F0.imprint","IMPRINT",FACE,{"disambiguationData":[TD([[makeQuery(id+"F0.imprint","IMPRINT",EDGE,{"disambiguationData":[TD([[subQ5,1.0]])],"derivedFrom":subQ3}),1.0]])]});}
            var Q59;
            {var subQ1=sQuery(id+"F0.wireOp",EDGE,"E26");var subQ3=sQuery(id+"F0.wireOp",EDGE,"E27");var subQ4=makeQuery(id+"F0.imprint","INTERSECT",VERTEX,{"derivedFrom":[subQ1,subQ3]});Q59=makeQuery(id+"F0.imprint","IMPRINT",FACE,{"disambiguationData":[TD([[makeQuery(id+"F0.imprint","IMPRINT",EDGE,{"disambiguationData":[TD([[subQ4,-1.0]])],"derivedFrom":subQ3}),1.0]])]});}
            var Q60;
            {var subQ1=sQuery(id+"F0.wireOp",EDGE,"E28");var subQ4=sQuery(id+"F0.wireOp",EDGE,"E45");var subQ5=makeQuery(id+"F0.imprint","INTERSECT",VERTEX,{"derivedFrom":[subQ1,subQ4]});Q60=makeQuery(id+"F0.imprint","IMPRINT",FACE,{"disambiguationData":[TD([[makeQuery(id+"F0.imprint","IMPRINT",EDGE,{"disambiguationData":[TD([[subQ5,1.0]])],"derivedFrom":subQ1}),1.0]])]});}
            var Q61;
            {var subQ0=sQuery(id+"F0.wireOp",EDGE,"E45");var subQ1=sQuery(id+"F0.wireOp",EDGE,"E28");var subQ2=makeQuery(id+"F0.imprint","INTERSECT",VERTEX,{"derivedFrom":[subQ1,subQ0]});Q61=makeQuery(id+"F0.imprint","IMPRINT",FACE,{"disambiguationData":[TD([[makeQuery(id+"F0.imprint","IMPRINT",EDGE,{"disambiguationData":[TD([[subQ2,-1.0]])],"derivedFrom":subQ1}),1.0]])]});}
            var Q62;
            {var subQ0=sQuery(id+"F0.wireOp",EDGE,"E30");var subQ1=sQuery(id+"F0.wireOp",EDGE,"E28");var subQ2=makeQuery(id+"F0.imprint","INTERSECT",VERTEX,{"derivedFrom":[subQ1,subQ0]});Q62=makeQuery(id+"F0.imprint","IMPRINT",FACE,{"disambiguationData":[TD([[makeQuery(id+"F0.imprint","IMPRINT",EDGE,{"disambiguationData":[TD([[subQ2,-1.0]])],"derivedFrom":subQ1}),1.0]])]});}
            var Q63;
            {var subQ0=sQuery(id+"F0.wireOp",EDGE,"E46");var subQ1=sQuery(id+"F0.wireOp",EDGE,"E28");var subQ2=makeQuery(id+"F0.imprint","INTERSECT",VERTEX,{"derivedFrom":[subQ1,subQ0]});Q63=makeQuery(id+"F0.imprint","IMPRINT",FACE,{"disambiguationData":[TD([[makeQuery(id+"F0.imprint","IMPRINT",EDGE,{"disambiguationData":[TD([[subQ2,-1.0]])],"derivedFrom":subQ1}),1.0]])]});}
            var Q64;
            {var subQ0=sQuery(id+"F0.wireOp",EDGE,"E31");var subQ1=sQuery(id+"F0.wireOp",EDGE,"E28");var subQ2=makeQuery(id+"F0.imprint","INTERSECT",VERTEX,{"derivedFrom":[subQ1,subQ0]});Q64=makeQuery(id+"F0.imprint","IMPRINT",FACE,{"disambiguationData":[TD([[makeQuery(id+"F0.imprint","IMPRINT",EDGE,{"disambiguationData":[TD([[subQ2,-1.0]])],"derivedFrom":subQ1}),1.0]])]});}
            var Q65;
            {var subQ0=sQuery(id+"F0.wireOp",EDGE,"E47");var subQ1=sQuery(id+"F0.wireOp",EDGE,"E28");var subQ2=makeQuery(id+"F0.imprint","INTERSECT",VERTEX,{"derivedFrom":[subQ1,subQ0]});Q65=makeQuery(id+"F0.imprint","IMPRINT",FACE,{"disambiguationData":[TD([[makeQuery(id+"F0.imprint","IMPRINT",EDGE,{"disambiguationData":[TD([[subQ2,-1.0]])],"derivedFrom":subQ1}),1.0]])]});}
            var Q66;
            {var subQ0=sQuery(id+"F0.wireOp",EDGE,"E32");var subQ1=sQuery(id+"F0.wireOp",EDGE,"E28");var subQ2=makeQuery(id+"F0.imprint","INTERSECT",VERTEX,{"derivedFrom":[subQ1,subQ0]});Q66=makeQuery(id+"F0.imprint","IMPRINT",FACE,{"disambiguationData":[TD([[makeQuery(id+"F0.imprint","IMPRINT",EDGE,{"disambiguationData":[TD([[subQ2,-1.0]])],"derivedFrom":subQ1}),1.0]])]});}
            var Q67;
            {var subQ0=sQuery(id+"F0.wireOp",EDGE,"E48");var subQ1=sQuery(id+"F0.wireOp",EDGE,"E28");var subQ2=makeQuery(id+"F0.imprint","INTERSECT",VERTEX,{"derivedFrom":[subQ1,subQ0]});Q67=makeQuery(id+"F0.imprint","IMPRINT",FACE,{"disambiguationData":[TD([[makeQuery(id+"F0.imprint","IMPRINT",EDGE,{"disambiguationData":[TD([[subQ2,-1.0]])],"derivedFrom":subQ1}),1.0]])]});}
            var Q68;
            {var subQ0=sQuery(id+"F0.wireOp",EDGE,"E33");var subQ1=sQuery(id+"F0.wireOp",EDGE,"E28");var subQ2=makeQuery(id+"F0.imprint","INTERSECT",VERTEX,{"derivedFrom":[subQ1,subQ0]});Q68=makeQuery(id+"F0.imprint","IMPRINT",FACE,{"disambiguationData":[TD([[makeQuery(id+"F0.imprint","IMPRINT",EDGE,{"disambiguationData":[TD([[subQ2,-1.0]])],"derivedFrom":subQ1}),1.0]])]});}
            var Q69;
            {var subQ0=sQuery(id+"F0.wireOp",EDGE,"E49");var subQ1=sQuery(id+"F0.wireOp",EDGE,"E28");var subQ2=makeQuery(id+"F0.imprint","INTERSECT",VERTEX,{"derivedFrom":[subQ1,subQ0]});Q69=makeQuery(id+"F0.imprint","IMPRINT",FACE,{"disambiguationData":[TD([[makeQuery(id+"F0.imprint","IMPRINT",EDGE,{"disambiguationData":[TD([[subQ2,-1.0]])],"derivedFrom":subQ1}),1.0]])]});}
            var Q70;
            {var subQ0=sQuery(id+"F0.wireOp",EDGE,"E34");var subQ1=sQuery(id+"F0.wireOp",EDGE,"E28");var subQ2=makeQuery(id+"F0.imprint","INTERSECT",VERTEX,{"derivedFrom":[subQ1,subQ0]});Q70=makeQuery(id+"F0.imprint","IMPRINT",FACE,{"disambiguationData":[TD([[makeQuery(id+"F0.imprint","IMPRINT",EDGE,{"disambiguationData":[TD([[subQ2,-1.0]])],"derivedFrom":subQ1}),1.0]])]});}
            var Q71;
            {var subQ0=sQuery(id+"F0.wireOp",EDGE,"E41");var subQ1=sQuery(id+"F0.wireOp",EDGE,"E28");var subQ2=makeQuery(id+"F0.imprint","INTERSECT",VERTEX,{"derivedFrom":[subQ1,subQ0]});Q71=makeQuery(id+"F0.imprint","IMPRINT",FACE,{"disambiguationData":[TD([[makeQuery(id+"F0.imprint","IMPRINT",EDGE,{"disambiguationData":[TD([[subQ2,-1.0]])],"derivedFrom":subQ1}),1.0]])]});}
            var Q72;
            {var subQ0=sQuery(id+"F0.wireOp",EDGE,"E42");var subQ1=sQuery(id+"F0.wireOp",EDGE,"E28");var subQ2=makeQuery(id+"F0.imprint","INTERSECT",VERTEX,{"derivedFrom":[subQ1,subQ0]});Q72=makeQuery(id+"F0.imprint","IMPRINT",FACE,{"disambiguationData":[TD([[makeQuery(id+"F0.imprint","IMPRINT",EDGE,{"disambiguationData":[TD([[subQ2,-1.0]])],"derivedFrom":subQ1}),1.0]])]});}
            var Q73;
            {var subQ1=sQuery(id+"F0.wireOp",EDGE,"E35");var subQ3=sQuery(id+"F0.wireOp",EDGE,"E58");var subQ4=makeQuery(id+"F0.imprint","INTERSECT",VERTEX,{"derivedFrom":[subQ1,subQ3]});Q73=makeQuery(id+"F0.imprint","IMPRINT",FACE,{"disambiguationData":[TD([[makeQuery(id+"F0.imprint","IMPRINT",EDGE,{"disambiguationData":[TD([[subQ4,-1.0]])],"derivedFrom":subQ3}),1.0]])]});}
            var Q74;
            {var subQ1=sQuery(id+"F0.wireOp",EDGE,"E36");var subQ3=sQuery(id+"F0.wireOp",EDGE,"E58");var subQ4=makeQuery(id+"F0.imprint","INTERSECT",VERTEX,{"derivedFrom":[subQ1,subQ3]});Q74=makeQuery(id+"F0.imprint","IMPRINT",FACE,{"disambiguationData":[TD([[makeQuery(id+"F0.imprint","IMPRINT",EDGE,{"disambiguationData":[TD([[subQ4,1.0]])],"derivedFrom":subQ3}),1.0]])]});}
            var Q75;
            {var subQ1=sQuery(id+"F0.wireOp",EDGE,"E36");var subQ3=sQuery(id+"F0.wireOp",EDGE,"E58");var subQ4=makeQuery(id+"F0.imprint","INTERSECT",VERTEX,{"derivedFrom":[subQ1,subQ3]});Q75=makeQuery(id+"F0.imprint","IMPRINT",FACE,{"disambiguationData":[TD([[makeQuery(id+"F0.imprint","IMPRINT",EDGE,{"disambiguationData":[TD([[subQ4,-1.0]])],"derivedFrom":subQ3}),1.0]])]});}
            var Q76;
            {var subQ1=sQuery(id+"F0.wireOp",EDGE,"E38");var subQ3=sQuery(id+"F0.wireOp",EDGE,"E58");var subQ4=makeQuery(id+"F0.imprint","INTERSECT",VERTEX,{"derivedFrom":[subQ1,subQ3]});Q76=makeQuery(id+"F0.imprint","IMPRINT",FACE,{"disambiguationData":[TD([[makeQuery(id+"F0.imprint","IMPRINT",EDGE,{"disambiguationData":[TD([[subQ4,1.0]])],"derivedFrom":subQ3}),1.0]])]});}
            var Q77;
            {var subQ1=sQuery(id+"F0.wireOp",EDGE,"E38");var subQ3=sQuery(id+"F0.wireOp",EDGE,"E58");var subQ4=makeQuery(id+"F0.imprint","INTERSECT",VERTEX,{"derivedFrom":[subQ1,subQ3]});Q77=makeQuery(id+"F0.imprint","IMPRINT",FACE,{"disambiguationData":[TD([[makeQuery(id+"F0.imprint","IMPRINT",EDGE,{"disambiguationData":[TD([[subQ4,-1.0]])],"derivedFrom":subQ3}),1.0]])]});}
            var Q78;
            {var subQ1=sQuery(id+"F0.wireOp",EDGE,"E39");var subQ3=sQuery(id+"F0.wireOp",EDGE,"E58");var subQ4=makeQuery(id+"F0.imprint","INTERSECT",VERTEX,{"derivedFrom":[subQ1,subQ3]});Q78=makeQuery(id+"F0.imprint","IMPRINT",FACE,{"disambiguationData":[TD([[makeQuery(id+"F0.imprint","IMPRINT",EDGE,{"disambiguationData":[TD([[subQ4,1.0]])],"derivedFrom":subQ3}),1.0]])]});}
            var Q79;
            {var subQ1=sQuery(id+"F0.wireOp",EDGE,"E39");var subQ3=sQuery(id+"F0.wireOp",EDGE,"E43");var subQ4=makeQuery(id+"F0.imprint","INTERSECT",VERTEX,{"derivedFrom":[subQ1,subQ3]});Q79=makeQuery(id+"F0.imprint","IMPRINT",FACE,{"disambiguationData":[TD([[makeQuery(id+"F0.imprint","IMPRINT",EDGE,{"disambiguationData":[TD([[subQ4,1.0]])],"derivedFrom":subQ3}),1.0]])]});}
            var Q80;
            {var subQ0=sQuery(id+"F0.wireOp",EDGE,"E57");var subQ1=sQuery(id+"F0.wireOp",EDGE,"E40");var subQ2=makeQuery(id+"F0.imprint","INTERSECT",VERTEX,{"derivedFrom":[subQ1,subQ0]});Q80=makeQuery(id+"F0.imprint","IMPRINT",FACE,{"disambiguationData":[TD([[makeQuery(id+"F0.imprint","IMPRINT",EDGE,{"disambiguationData":[TD([[subQ2,-1.0]])],"derivedFrom":subQ1}),1.0]])]});}
            var Q81;
            {var subQ1=sQuery(id+"F0.wireOp",EDGE,"E40");var subQ3=sQuery(id+"F0.wireOp",EDGE,"E43");var subQ4=makeQuery(id+"F0.imprint","INTERSECT",VERTEX,{"derivedFrom":[subQ1,subQ3]});Q81=makeQuery(id+"F0.imprint","IMPRINT",FACE,{"disambiguationData":[TD([[makeQuery(id+"F0.imprint","IMPRINT",EDGE,{"disambiguationData":[TD([[subQ4,1.0]])],"derivedFrom":subQ3}),1.0]])]});}
            var Q82;
            {var subQ1=sQuery(id+"F0.wireOp",EDGE,"E55");var subQ3=sQuery(id+"F0.wireOp",EDGE,"E58");var subQ4=makeQuery(id+"F0.imprint","INTERSECT",VERTEX,{"derivedFrom":[subQ1,subQ3]});Q82=makeQuery(id+"F0.imprint","IMPRINT",FACE,{"disambiguationData":[TD([[makeQuery(id+"F0.imprint","IMPRINT",EDGE,{"disambiguationData":[TD([[subQ4,1.0]])],"derivedFrom":subQ3}),1.0]])]});}
            var Q83;
            {var subQ5=sQuery(id+"F0.wireOp",EDGE,"E13");var subQ6=sQuery(id+"F0.wireOp",EDGE,"E0.bottom");var subQ7=makeQuery(id+"F0.imprint","INTERSECT",VERTEX,{"derivedFrom":[subQ6,subQ5]});Q83=makeQuery(id+"F0.imprint","IMPRINT",FACE,{"disambiguationData":[TD([[makeQuery(id+"F0.imprint","IMPRINT",EDGE,{"disambiguationData":[TD([[subQ7,-1.0]])],"derivedFrom":subQ5}),1.0]])]});}
            var Q84;
            {var subQ3=sQuery(id+"F0.wireOp",EDGE,"E27");var subQ5=sQuery(id+"F0.wireOp",EDGE,"E15");var subQ7=makeQuery(id+"F0.imprint","INTERSECT",VERTEX,{"derivedFrom":[subQ5,subQ3]});Q84=makeQuery(id+"F0.imprint","IMPRINT",FACE,{"disambiguationData":[TD([[makeQuery(id+"F0.imprint","IMPRINT",EDGE,{"disambiguationData":[TD([[subQ7,-1.0]])],"derivedFrom":subQ5}),1.0]])]});}
            var Q85;
            {var subQ0=sQuery(id+"F0.wireOp",EDGE,"E26");var subQ1=sQuery(id+"F0.wireOp",EDGE,"E1");var subQ2=makeQuery(id+"F0.imprint","INTERSECT",VERTEX,{"derivedFrom":[subQ1,subQ0]});Q85=makeQuery(id+"F0.imprint","IMPRINT",FACE,{"disambiguationData":[TD([[makeQuery(id+"F0.imprint","IMPRINT",EDGE,{"disambiguationData":[TD([[subQ2,-1.0]])],"derivedFrom":subQ1}),-1.0]])]});}
            var Q86;
            {var subQ0=sQuery(id+"F0.wireOp",EDGE,"E3");var subQ1=sQuery(id+"F0.wireOp",EDGE,"E1");var subQ2=makeQuery(id+"F0.imprint","INTERSECT",VERTEX,{"derivedFrom":[subQ1,subQ0]});Q86=makeQuery(id+"F0.imprint","IMPRINT",FACE,{"disambiguationData":[TD([[makeQuery(id+"F0.imprint","IMPRINT",EDGE,{"disambiguationData":[TD([[subQ2,-1.0]])],"derivedFrom":subQ1}),-1.0]])]});}
            var Q87;
            {var subQ0=sQuery(id+"F0.wireOp",EDGE,"E23");var subQ1=sQuery(id+"F0.wireOp",EDGE,"E1");var subQ2=makeQuery(id+"F0.imprint","INTERSECT",VERTEX,{"derivedFrom":[subQ1,subQ0]});Q87=makeQuery(id+"F0.imprint","IMPRINT",FACE,{"disambiguationData":[TD([[makeQuery(id+"F0.imprint","IMPRINT",EDGE,{"disambiguationData":[TD([[subQ2,-1.0]])],"derivedFrom":subQ1}),-1.0]])]});}
            var Q88;
            {var subQ3=sQuery(id+"F0.wireOp",EDGE,"E43");var subQ5=sQuery(id+"F0.wireOp",EDGE,"E6");var subQ6=makeQuery(id+"F0.imprint","INTERSECT",VERTEX,{"derivedFrom":[subQ5,subQ3]});Q88=makeQuery(id+"F0.imprint","IMPRINT",FACE,{"disambiguationData":[TD([[makeQuery(id+"F0.imprint","IMPRINT",EDGE,{"disambiguationData":[TD([[subQ6,-1.0]])],"derivedFrom":subQ5}),-1.0]])]});}
            var Q89;
            {var subQ0=sQuery(id+"F0.wireOp",EDGE,"E17");var subQ1=sQuery(id+"F0.wireOp",EDGE,"E11");var subQ2=makeQuery(id+"F0.imprint","INTERSECT",VERTEX,{"derivedFrom":[subQ1,subQ0]});Q89=makeQuery(id+"F0.imprint","IMPRINT",FACE,{"disambiguationData":[TD([[makeQuery(id+"F0.imprint","IMPRINT",EDGE,{"disambiguationData":[TD([[subQ2,-1.0]])],"derivedFrom":subQ1}),-1.0]])]});}
            var Q90;
            {var subQ3=sQuery(id+"F0.wireOp",EDGE,"E14");var subQ5=sQuery(id+"F0.wireOp",EDGE,"E13");var subQ6=makeQuery(id+"F0.imprint","INTERSECT",VERTEX,{"derivedFrom":[subQ5,subQ3]});Q90=makeQuery(id+"F0.imprint","IMPRINT",FACE,{"disambiguationData":[TD([[makeQuery(id+"F0.imprint","IMPRINT",EDGE,{"disambiguationData":[TD([[subQ6,-1.0]])],"derivedFrom":subQ5}),-1.0]])]});}
            var Q91;
            {var subQ1=sQuery(id+"F0.wireOp",EDGE,"E12");var subQ3=sQuery(id+"F0.wireOp",EDGE,"E14");var subQ4=makeQuery(id+"F0.imprint","INTERSECT",VERTEX,{"derivedFrom":[subQ1,subQ3]});Q91=makeQuery(id+"F0.imprint","IMPRINT",FACE,{"disambiguationData":[TD([[makeQuery(id+"F0.imprint","IMPRINT",EDGE,{"disambiguationData":[TD([[subQ4,1.0]])],"derivedFrom":subQ3}),-1.0]])]});}
            var Q92;
            {var subQ0=sQuery(id+"F0.wireOp",EDGE,"E16");var subQ1=sQuery(id+"F0.wireOp",EDGE,"E13");var subQ2=makeQuery(id+"F0.imprint","INTERSECT",VERTEX,{"derivedFrom":[subQ1,subQ0]});Q92=makeQuery(id+"F0.imprint","IMPRINT",FACE,{"disambiguationData":[TD([[makeQuery(id+"F0.imprint","IMPRINT",EDGE,{"disambiguationData":[TD([[subQ2,-1.0]])],"derivedFrom":subQ1}),-1.0]])]});}
            var Q93;
            {var subQ3=sQuery(id+"F0.wireOp",EDGE,"E44");var subQ5=sQuery(id+"F0.wireOp",EDGE,"E18");var subQ6=makeQuery(id+"F0.imprint","INTERSECT",VERTEX,{"derivedFrom":[subQ5,subQ3]});Q93=makeQuery(id+"F0.imprint","IMPRINT",FACE,{"disambiguationData":[TD([[makeQuery(id+"F0.imprint","IMPRINT",EDGE,{"disambiguationData":[TD([[subQ6,-1.0]])],"derivedFrom":subQ5}),1.0]])]});}
            var Q94;
            {var subQ3=sQuery(id+"F0.wireOp",EDGE,"E47");var subQ5=sQuery(id+"F0.wireOp",EDGE,"E44");var subQ6=makeQuery(id+"F0.imprint","INTERSECT",VERTEX,{"derivedFrom":[subQ5,subQ3]});Q94=makeQuery(id+"F0.imprint","IMPRINT",FACE,{"disambiguationData":[TD([[makeQuery(id+"F0.imprint","IMPRINT",EDGE,{"disambiguationData":[TD([[subQ6,-1.0]])],"derivedFrom":subQ5}),1.0]])]});}
            var Q95;
            {var subQ3=sQuery(id+"F0.wireOp",EDGE,"E44");var subQ5=sQuery(id+"F0.wireOp",EDGE,"E20");var subQ6=makeQuery(id+"F0.imprint","INTERSECT",VERTEX,{"derivedFrom":[subQ5,subQ3]});Q95=makeQuery(id+"F0.imprint","IMPRINT",FACE,{"disambiguationData":[TD([[makeQuery(id+"F0.imprint","IMPRINT",EDGE,{"disambiguationData":[TD([[subQ6,-1.0]])],"derivedFrom":subQ5}),1.0]])]});}
            var Q96;
            {var subQ3=sQuery(id+"F0.wireOp",EDGE,"E49");var subQ5=sQuery(id+"F0.wireOp",EDGE,"E27");var subQ6=makeQuery(id+"F0.imprint","INTERSECT",VERTEX,{"derivedFrom":[subQ5,subQ3]});Q96=makeQuery(id+"F0.imprint","IMPRINT",FACE,{"disambiguationData":[TD([[makeQuery(id+"F0.imprint","IMPRINT",EDGE,{"disambiguationData":[TD([[subQ6,-1.0]])],"derivedFrom":subQ5}),1.0]])]});}
            var Q97;
            {var subQ1=sQuery(id+"F0.wireOp",EDGE,"E27");var subQ3=sQuery(id+"F0.wireOp",EDGE,"E58");var subQ4=makeQuery(id+"F0.imprint","INTERSECT",VERTEX,{"derivedFrom":[subQ1,subQ3]});Q97=makeQuery(id+"F0.imprint","IMPRINT",FACE,{"disambiguationData":[TD([[makeQuery(id+"F0.imprint","IMPRINT",EDGE,{"disambiguationData":[TD([[subQ4,-1.0]])],"derivedFrom":subQ3}),1.0]])]});}
            var Q98;
            {var subQ0=sQuery(id+"F0.wireOp",EDGE,"E50");var subQ1=sQuery(id+"F0.wireOp",EDGE,"E28");var subQ2=makeQuery(id+"F0.imprint","INTERSECT",VERTEX,{"derivedFrom":[subQ1,subQ0]});Q98=makeQuery(id+"F0.imprint","IMPRINT",FACE,{"disambiguationData":[TD([[makeQuery(id+"F0.imprint","IMPRINT",EDGE,{"disambiguationData":[TD([[subQ2,-1.0]])],"derivedFrom":subQ1}),1.0]])]});}
            var Q99;
            {var subQ0=sQuery(id+"F0.wireOp",EDGE,"E40");var subQ1=sQuery(id+"F0.wireOp",EDGE,"E28");var subQ2=makeQuery(id+"F0.imprint","INTERSECT",VERTEX,{"derivedFrom":[subQ1,subQ0]});Q99=makeQuery(id+"F0.imprint","IMPRINT",FACE,{"disambiguationData":[TD([[makeQuery(id+"F0.imprint","IMPRINT",EDGE,{"disambiguationData":[TD([[subQ2,-1.0]])],"derivedFrom":subQ1}),1.0]])]});}
            var Q100;
            {var subQ1=sQuery(id+"F0.wireOp",EDGE,"E37");var subQ3=sQuery(id+"F0.wireOp",EDGE,"E54");var subQ4=makeQuery(id+"F0.imprint","INTERSECT",VERTEX,{"derivedFrom":[subQ1,subQ3]});Q100=makeQuery(id+"F0.imprint","IMPRINT",FACE,{"disambiguationData":[TD([[makeQuery(id+"F0.imprint","IMPRINT",EDGE,{"disambiguationData":[TD([[subQ4,1.0]])],"derivedFrom":subQ3}),1.0]])]});}
            var Q101;
            {var subQ0=sQuery(id+"F0.wireOp",EDGE,"E54");var subQ1=sQuery(id+"F0.wireOp",EDGE,"E37");var subQ2=makeQuery(id+"F0.imprint","INTERSECT",VERTEX,{"derivedFrom":[subQ1,subQ0]});Q101=makeQuery(id+"F0.imprint","IMPRINT",FACE,{"disambiguationData":[TD([[makeQuery(id+"F0.imprint","IMPRINT",EDGE,{"disambiguationData":[TD([[subQ2,-1.0]])],"derivedFrom":subQ1}),1.0]])]});}
            var Q102;
            {var subQ1=sQuery(id+"F0.wireOp",EDGE,"E40");var subQ7=sQuery(id+"F0.wireOp",EDGE,"E59");var subQ8=makeQuery(id+"F0.imprint","INTERSECT",VERTEX,{"derivedFrom":[subQ1,subQ7]});Q102=makeQuery(id+"F0.imprint","IMPRINT",FACE,{"disambiguationData":[TD([[makeQuery(id+"F0.imprint","IMPRINT",EDGE,{"disambiguationData":[TD([[subQ8,-1.0]])],"derivedFrom":subQ1}),-1.0]])]});}
            var Q103;
            {var subQ5=sQuery(id+"F0.wireOp",EDGE,"E2");var subQ6=sQuery(id+"F0.wireOp",EDGE,"E1");var subQ7=makeQuery(id+"F0.imprint","INTERSECT",VERTEX,{"derivedFrom":[subQ6,subQ5]});Q103=makeQuery(id+"F0.imprint","IMPRINT",FACE,{"disambiguationData":[TD([[makeQuery(id+"F0.imprint","IMPRINT",EDGE,{"disambiguationData":[TD([[subQ7,-1.0]])],"derivedFrom":subQ6}),-1.0]])]});}
            var Q104;
            {var subQ1=sQuery(id+"F0.wireOp",EDGE,"E1");var subQ5=sQuery(id+"F0.wireOp",EDGE,"E5");var subQ6=makeQuery(id+"F0.imprint","INTERSECT",VERTEX,{"derivedFrom":[subQ1,subQ5]});Q104=makeQuery(id+"F0.imprint","IMPRINT",FACE,{"disambiguationData":[TD([[makeQuery(id+"F0.imprint","IMPRINT",EDGE,{"disambiguationData":[TD([[subQ6,-1.0]])],"derivedFrom":subQ1}),-1.0]])]});}
            var Q105;
            {var subQ1=sQuery(id+"F0.wireOp",EDGE,"E1");var subQ7=sQuery(id+"F0.wireOp",EDGE,"E14");var subQ9=makeQuery(id+"F0.imprint","INTERSECT",VERTEX,{"derivedFrom":[subQ1,subQ7]});Q105=makeQuery(id+"F0.imprint","IMPRINT",FACE,{"disambiguationData":[TD([[makeQuery(id+"F0.imprint","IMPRINT",EDGE,{"disambiguationData":[TD([[subQ9,-1.0]])],"derivedFrom":subQ1}),-1.0]])]});}
            var Q106;
            {var subQ3=sQuery(id+"F0.wireOp",EDGE,"E14");var subQ5=sQuery(id+"F0.wireOp",EDGE,"E43");var subQ6=makeQuery(id+"F0.imprint","INTERSECT",VERTEX,{"derivedFrom":[subQ3,subQ5]});Q106=makeQuery(id+"F0.imprint","IMPRINT",FACE,{"disambiguationData":[TD([[makeQuery(id+"F0.imprint","IMPRINT",EDGE,{"disambiguationData":[TD([[subQ6,-1.0]])],"derivedFrom":subQ3}),-1.0]])]});}
            var Q107;
            {var subQ5=sQuery(id+"F0.wireOp",EDGE,"E7");var subQ7=sQuery(id+"F0.wireOp",EDGE,"E20");var subQ8=makeQuery(id+"F0.imprint","INTERSECT",VERTEX,{"derivedFrom":[subQ5,subQ7]});Q107=makeQuery(id+"F0.imprint","IMPRINT",FACE,{"disambiguationData":[TD([[makeQuery(id+"F0.imprint","IMPRINT",EDGE,{"disambiguationData":[TD([[subQ8,-1.0]])],"derivedFrom":subQ5}),-1.0]])]});}
            var Q108;
            {var subQ5=sQuery(id+"F0.wireOp",EDGE,"E19");var subQ6=sQuery(id+"F0.wireOp",EDGE,"E8");var subQ7=makeQuery(id+"F0.imprint","INTERSECT",VERTEX,{"derivedFrom":[subQ6,subQ5]});Q108=makeQuery(id+"F0.imprint","IMPRINT",FACE,{"disambiguationData":[TD([[makeQuery(id+"F0.imprint","IMPRINT",EDGE,{"disambiguationData":[TD([[subQ7,-1.0]])],"derivedFrom":subQ6}),-1.0]])]});}
            var Q109;
            {var subQ5=sQuery(id+"F0.wireOp",EDGE,"E18");var subQ6=sQuery(id+"F0.wireOp",EDGE,"E10");var subQ7=makeQuery(id+"F0.imprint","INTERSECT",VERTEX,{"derivedFrom":[subQ6,subQ5]});Q109=makeQuery(id+"F0.imprint","IMPRINT",FACE,{"disambiguationData":[TD([[makeQuery(id+"F0.imprint","IMPRINT",EDGE,{"disambiguationData":[TD([[subQ7,-1.0]])],"derivedFrom":subQ6}),-1.0]])]});}
            var Q110;
            {var subQ6=sQuery(id+"F0.wireOp",EDGE,"E1");var subQ9=sQuery(id+"F0.wireOp",EDGE,"E6");var subQ10=makeQuery(id+"F0.imprint","INTERSECT",VERTEX,{"derivedFrom":[subQ6,subQ9]});Q110=makeQuery(id+"F0.imprint","IMPRINT",FACE,{"disambiguationData":[TD([[makeQuery(id+"F0.imprint","IMPRINT",EDGE,{"disambiguationData":[TD([[subQ10,-1.0]])],"derivedFrom":subQ6}),-1.0]])]});}
            var Q111;
            {var subQ1=sQuery(id+"F0.wireOp",EDGE,"E1");var subQ7=sQuery(id+"F0.wireOp",EDGE,"E17");var subQ9=makeQuery(id+"F0.imprint","INTERSECT",VERTEX,{"derivedFrom":[subQ1,subQ7]});Q111=makeQuery(id+"F0.imprint","IMPRINT",FACE,{"disambiguationData":[TD([[makeQuery(id+"F0.imprint","IMPRINT",EDGE,{"disambiguationData":[TD([[subQ9,-1.0]])],"derivedFrom":subQ1}),1.0]])]});}
            var Q112;
            {var subQ0=sQuery(id+"F0.wireOp",EDGE,"E40");var subQ1=sQuery(id+"F0.wireOp",EDGE,"E33");var subQ2=makeQuery(id+"F0.imprint","INTERSECT",VERTEX,{"derivedFrom":[subQ1,subQ0]});Q112=makeQuery(id+"F0.imprint","IMPRINT",FACE,{"disambiguationData":[TD([[makeQuery(id+"F0.imprint","IMPRINT",EDGE,{"disambiguationData":[TD([[subQ2,-1.0]])],"derivedFrom":subQ1}),-1.0]])]});}
            var Q113;
            {var subQ0=sQuery(id+"F0.wireOp",EDGE,"E50");var subQ1=sQuery(id+"F0.wireOp",EDGE,"E29");var subQ2=makeQuery(id+"F0.imprint","INTERSECT",VERTEX,{"derivedFrom":[subQ1,subQ0]});Q113=makeQuery(id+"F0.imprint","IMPRINT",FACE,{"disambiguationData":[TD([[makeQuery(id+"F0.imprint","IMPRINT",EDGE,{"disambiguationData":[TD([[subQ2,-1.0]])],"derivedFrom":subQ1}),1.0]])]});}
            var Q114;
            {var subQ0=sQuery(id+"F0.wireOp",EDGE,"E39");var subQ1=sQuery(id+"F0.wireOp",EDGE,"E35");var subQ2=makeQuery(id+"F0.imprint","INTERSECT",VERTEX,{"derivedFrom":[subQ1,subQ0]});Q114=makeQuery(id+"F0.imprint","IMPRINT",FACE,{"disambiguationData":[TD([[makeQuery(id+"F0.imprint","IMPRINT",EDGE,{"disambiguationData":[TD([[subQ2,-1.0]])],"derivedFrom":subQ1}),-1.0]])]});}
            var Q115;
            {var subQ0=sQuery(id+"F0.wireOp",EDGE,"E55");var subQ1=sQuery(id+"F0.wireOp",EDGE,"E48");var subQ2=makeQuery(id+"F0.imprint","INTERSECT",VERTEX,{"derivedFrom":[subQ1,subQ0]});Q115=makeQuery(id+"F0.imprint","IMPRINT",FACE,{"disambiguationData":[TD([[makeQuery(id+"F0.imprint","IMPRINT",EDGE,{"disambiguationData":[TD([[subQ2,-1.0]])],"derivedFrom":subQ1}),-1.0]])]});}
            var Q116;
            {var subQ0=sQuery(id+"F0.wireOp",EDGE,"E42");var subQ1=sQuery(id+"F0.wireOp",EDGE,"E7");var subQ2=makeQuery(id+"F0.imprint","INTERSECT",VERTEX,{"derivedFrom":[subQ1,subQ0]});Q116=makeQuery(id+"F0.imprint","IMPRINT",FACE,{"disambiguationData":[TD([[makeQuery(id+"F0.imprint","IMPRINT",EDGE,{"disambiguationData":[TD([[subQ2,-1.0]])],"derivedFrom":subQ1}),-1.0]])]});}
            var Q117;
            {var subQ0=sQuery(id+"F0.wireOp",EDGE,"E39");var subQ1=sQuery(id+"F0.wireOp",EDGE,"E2");var subQ2=makeQuery(id+"F0.imprint","INTERSECT",VERTEX,{"derivedFrom":[subQ1,subQ0]});Q117=makeQuery(id+"F0.imprint","IMPRINT",FACE,{"disambiguationData":[TD([[makeQuery(id+"F0.imprint","IMPRINT",EDGE,{"disambiguationData":[TD([[subQ2,-1.0]])],"derivedFrom":subQ1}),-1.0]])]});}
            var Q118;
            {var subQ0=sQuery(id+"F0.wireOp",EDGE,"E12");var subQ1=sQuery(id+"F0.wireOp",EDGE,"E1");var subQ2=makeQuery(id+"F0.imprint","INTERSECT",VERTEX,{"derivedFrom":[subQ1,subQ0]});Q118=makeQuery(id+"F0.imprint","IMPRINT",FACE,{"disambiguationData":[TD([[makeQuery(id+"F0.imprint","IMPRINT",EDGE,{"disambiguationData":[TD([[subQ2,-1.0]])],"derivedFrom":subQ1}),1.0]])]});}
            var Q119;
            {var subQ0=sQuery(id+"F0.wireOp",EDGE,"E54");var subQ1=sQuery(id+"F0.wireOp",EDGE,"E50");var subQ2=makeQuery(id+"F0.imprint","INTERSECT",VERTEX,{"derivedFrom":[subQ1,subQ0]});Q119=makeQuery(id+"F0.imprint","IMPRINT",FACE,{"disambiguationData":[TD([[makeQuery(id+"F0.imprint","IMPRINT",EDGE,{"disambiguationData":[TD([[subQ2,-1.0]])],"derivedFrom":subQ1}),-1.0]])]});}
            var Q120;
            {var subQ0=sQuery(id+"F0.wireOp",EDGE,"E56");var subQ1=sQuery(id+"F0.wireOp",EDGE,"E48");var subQ2=makeQuery(id+"F0.imprint","INTERSECT",VERTEX,{"derivedFrom":[subQ1,subQ0]});Q120=makeQuery(id+"F0.imprint","IMPRINT",FACE,{"disambiguationData":[TD([[makeQuery(id+"F0.imprint","IMPRINT",EDGE,{"disambiguationData":[TD([[subQ2,-1.0]])],"derivedFrom":subQ1}),-1.0]])]});}
            var Q121;
            {var subQ1=sQuery(id+"F0.wireOp",EDGE,"E22");var subQ5=sQuery(id+"F0.wireOp",EDGE,"E24");var subQ6=makeQuery(id+"F0.imprint","INTERSECT",VERTEX,{"derivedFrom":[subQ1,subQ5]});Q121=makeQuery(id+"F0.imprint","IMPRINT",FACE,{"disambiguationData":[TD([[makeQuery(id+"F0.imprint","IMPRINT",EDGE,{"disambiguationData":[TD([[subQ6,-1.0]])],"derivedFrom":subQ1}),-1.0]])]});}
            var Q122;
            {var subQ1=sQuery(id+"F0.wireOp",EDGE,"E4");var subQ5=sQuery(id+"F0.wireOp",EDGE,"E42");var subQ6=makeQuery(id+"F0.imprint","INTERSECT",VERTEX,{"derivedFrom":[subQ1,subQ5]});Q122=makeQuery(id+"F0.imprint","IMPRINT",FACE,{"disambiguationData":[TD([[makeQuery(id+"F0.imprint","IMPRINT",EDGE,{"disambiguationData":[TD([[subQ6,-1.0]])],"derivedFrom":subQ1}),1.0]])]});}
            var Q123;
            {var subQ0=sQuery(id+"F0.wireOp",EDGE,"E35");var subQ1=sQuery(id+"F0.wireOp",EDGE,"E30");var subQ2=makeQuery(id+"F0.imprint","INTERSECT",VERTEX,{"derivedFrom":[subQ1,subQ0]});Q123=makeQuery(id+"F0.imprint","IMPRINT",FACE,{"disambiguationData":[TD([[makeQuery(id+"F0.imprint","IMPRINT",EDGE,{"disambiguationData":[TD([[subQ2,-1.0]])],"derivedFrom":subQ1}),-1.0]])]});}
            var Q124;
            {var subQ0=sQuery(id+"F0.wireOp",EDGE,"E19");var subQ1=sQuery(id+"F0.wireOp",EDGE,"E18");var subQ2=makeQuery(id+"F0.imprint","INTERSECT",VERTEX,{"derivedFrom":[subQ1,subQ0]});Q124=makeQuery(id+"F0.imprint","IMPRINT",FACE,{"disambiguationData":[TD([[makeQuery(id+"F0.imprint","IMPRINT",EDGE,{"disambiguationData":[TD([[subQ2,-1.0]])],"derivedFrom":subQ1}),-1.0]])]});}
            var Q125;
            {var subQ0=sQuery(id+"F0.wireOp",EDGE,"E21");var subQ1=sQuery(id+"F0.wireOp",EDGE,"E4");var subQ2=makeQuery(id+"F0.imprint","INTERSECT",VERTEX,{"derivedFrom":[subQ1,subQ0]});Q125=makeQuery(id+"F0.imprint","IMPRINT",FACE,{"disambiguationData":[TD([[makeQuery(id+"F0.imprint","IMPRINT",EDGE,{"disambiguationData":[TD([[subQ2,-1.0]])],"derivedFrom":subQ1}),1.0]])]});}
            var Q126;
            {var subQ0=sQuery(id+"F0.wireOp",EDGE,"E15");var subQ1=sQuery(id+"F0.wireOp",EDGE,"E5");var subQ2=makeQuery(id+"F0.imprint","INTERSECT",VERTEX,{"derivedFrom":[subQ1,subQ0]});Q126=makeQuery(id+"F0.imprint","IMPRINT",FACE,{"disambiguationData":[TD([[makeQuery(id+"F0.imprint","IMPRINT",EDGE,{"disambiguationData":[TD([[subQ2,-1.0]])],"derivedFrom":subQ1}),-1.0]])]});}
            var Q127;
            {var subQ1=sQuery(id+"F0.wireOp",EDGE,"E1");var subQ7=sQuery(id+"F0.wireOp",EDGE,"E20");var subQ9=makeQuery(id+"F0.imprint","INTERSECT",VERTEX,{"derivedFrom":[subQ1,subQ7]});Q127=makeQuery(id+"F0.imprint","IMPRINT",FACE,{"disambiguationData":[TD([[makeQuery(id+"F0.imprint","IMPRINT",EDGE,{"disambiguationData":[TD([[subQ9,-1.0]])],"derivedFrom":subQ1}),-1.0]])]});}
            var Q128;
            {var subQ0=sQuery(id+"F0.wireOp",EDGE,"E21");var subQ1=sQuery(id+"F0.wireOp",EDGE,"E19");var subQ2=makeQuery(id+"F0.imprint","INTERSECT",VERTEX,{"derivedFrom":[subQ1,subQ0]});Q128=makeQuery(id+"F0.imprint","IMPRINT",FACE,{"disambiguationData":[TD([[makeQuery(id+"F0.imprint","IMPRINT",EDGE,{"disambiguationData":[TD([[subQ2,-1.0]])],"derivedFrom":subQ1}),-1.0]])]});}
            var Q129;
            {var subQ0=sQuery(id+"F0.wireOp",EDGE,"E8");var subQ1=sQuery(id+"F0.wireOp",EDGE,"E1");var subQ2=makeQuery(id+"F0.imprint","INTERSECT",VERTEX,{"derivedFrom":[subQ1,subQ0]});Q129=makeQuery(id+"F0.imprint","IMPRINT",FACE,{"disambiguationData":[TD([[makeQuery(id+"F0.imprint","IMPRINT",EDGE,{"disambiguationData":[TD([[subQ2,-1.0]])],"derivedFrom":subQ1}),-1.0]])]});}
            var Q130;
            {var subQ0=sQuery(id+"F0.wireOp",EDGE,"E39");var subQ1=sQuery(id+"F0.wireOp",EDGE,"E4");var subQ2=makeQuery(id+"F0.imprint","INTERSECT",VERTEX,{"derivedFrom":[subQ1,subQ0]});Q130=makeQuery(id+"F0.imprint","IMPRINT",FACE,{"disambiguationData":[TD([[makeQuery(id+"F0.imprint","IMPRINT",EDGE,{"disambiguationData":[TD([[subQ2,-1.0]])],"derivedFrom":subQ1}),-1.0]])]});}
            var Q131;
            {var subQ0=sQuery(id+"F0.wireOp",EDGE,"E40");var subQ1=sQuery(id+"F0.wireOp",EDGE,"E3");var subQ2=makeQuery(id+"F0.imprint","INTERSECT",VERTEX,{"derivedFrom":[subQ1,subQ0]});Q131=makeQuery(id+"F0.imprint","IMPRINT",FACE,{"disambiguationData":[TD([[makeQuery(id+"F0.imprint","IMPRINT",EDGE,{"disambiguationData":[TD([[subQ2,-1.0]])],"derivedFrom":subQ1}),-1.0]])]});}
            var Q132;
            {var subQ0=sQuery(id+"F0.wireOp",EDGE,"E12");var subQ1=sQuery(id+"F0.wireOp",EDGE,"E4");var subQ2=makeQuery(id+"F0.imprint","INTERSECT",VERTEX,{"derivedFrom":[subQ1,subQ0]});Q132=makeQuery(id+"F0.imprint","IMPRINT",FACE,{"disambiguationData":[TD([[makeQuery(id+"F0.imprint","IMPRINT",EDGE,{"disambiguationData":[TD([[subQ2,-1.0]])],"derivedFrom":subQ1}),1.0]])]});}
            var Q133;
            {var subQ0=sQuery(id+"F0.wireOp",EDGE,"E4");var subQ1=sQuery(id+"F0.wireOp",EDGE,"E2");var subQ2=makeQuery(id+"F0.imprint","INTERSECT",VERTEX,{"derivedFrom":[subQ1,subQ0]});Q133=makeQuery(id+"F0.imprint","IMPRINT",FACE,{"disambiguationData":[TD([[makeQuery(id+"F0.imprint","IMPRINT",EDGE,{"disambiguationData":[TD([[subQ2,-1.0]])],"derivedFrom":subQ1}),1.0]])]});}
            var Q134;
            {var subQ1=sQuery(id+"F0.wireOp",EDGE,"E34");var subQ7=sQuery(id+"F0.wireOp",EDGE,"E30");var subQ9=makeQuery(id+"F0.imprint","INTERSECT",VERTEX,{"derivedFrom":[subQ7,subQ1]});Q134=makeQuery(id+"F0.imprint","IMPRINT",FACE,{"disambiguationData":[TD([[makeQuery(id+"F0.imprint","IMPRINT",EDGE,{"disambiguationData":[TD([[subQ9,-1.0]])],"derivedFrom":subQ7}),1.0]])]});}
            var Q135;
            {var subQ0=sQuery(id+"F0.wireOp",EDGE,"E38");var subQ1=sQuery(id+"F0.wireOp",EDGE,"E33");var subQ2=makeQuery(id+"F0.imprint","INTERSECT",VERTEX,{"derivedFrom":[subQ1,subQ0]});Q135=makeQuery(id+"F0.imprint","IMPRINT",FACE,{"disambiguationData":[TD([[makeQuery(id+"F0.imprint","IMPRINT",EDGE,{"disambiguationData":[TD([[subQ2,-1.0]])],"derivedFrom":subQ1}),-1.0]])]});}
            var Q136;
            {var subQ5=sQuery(id+"F0.wireOp",EDGE,"E16");var subQ6=sQuery(id+"F0.wireOp",EDGE,"E4");var subQ7=makeQuery(id+"F0.imprint","INTERSECT",VERTEX,{"derivedFrom":[subQ6,subQ5]});Q136=makeQuery(id+"F0.imprint","IMPRINT",FACE,{"disambiguationData":[TD([[makeQuery(id+"F0.imprint","IMPRINT",EDGE,{"disambiguationData":[TD([[subQ7,-1.0]])],"derivedFrom":subQ6}),1.0]])]});}
            var Q137;
            {var subQ0=sQuery(id+"F0.wireOp",EDGE,"E25");var subQ1=sQuery(id+"F0.wireOp",EDGE,"E17");var subQ2=makeQuery(id+"F0.imprint","INTERSECT",VERTEX,{"derivedFrom":[subQ1,subQ0]});Q137=makeQuery(id+"F0.imprint","IMPRINT",FACE,{"disambiguationData":[TD([[makeQuery(id+"F0.imprint","IMPRINT",EDGE,{"disambiguationData":[TD([[subQ2,-1.0]])],"derivedFrom":subQ1}),-1.0]])]});}
            var Q138;
            {var subQ0=sQuery(id+"F0.wireOp",EDGE,"E14");var subQ1=sQuery(id+"F0.wireOp",EDGE,"E5");var subQ2=makeQuery(id+"F0.imprint","INTERSECT",VERTEX,{"derivedFrom":[subQ1,subQ0]});Q138=makeQuery(id+"F0.imprint","IMPRINT",FACE,{"disambiguationData":[TD([[makeQuery(id+"F0.imprint","IMPRINT",EDGE,{"disambiguationData":[TD([[subQ2,-1.0]])],"derivedFrom":subQ1}),-1.0]])]});}
            var Q139;
            {var subQ0=sQuery(id+"F0.wireOp",EDGE,"E10");var subQ1=sQuery(id+"F0.wireOp",EDGE,"E3");var subQ2=makeQuery(id+"F0.imprint","INTERSECT",VERTEX,{"derivedFrom":[subQ1,subQ0]});Q139=makeQuery(id+"F0.imprint","IMPRINT",FACE,{"disambiguationData":[TD([[makeQuery(id+"F0.imprint","IMPRINT",EDGE,{"disambiguationData":[TD([[subQ2,-1.0]])],"derivedFrom":subQ1}),1.0]])]});}
            var Q140;
            {var subQ0=sQuery(id+"F0.wireOp",EDGE,"E15");var subQ1=sQuery(id+"F0.wireOp",EDGE,"E1");var subQ2=makeQuery(id+"F0.imprint","INTERSECT",VERTEX,{"derivedFrom":[subQ1,subQ0]});Q140=makeQuery(id+"F0.imprint","IMPRINT",FACE,{"disambiguationData":[TD([[makeQuery(id+"F0.imprint","IMPRINT",EDGE,{"disambiguationData":[TD([[subQ2,-1.0]])],"derivedFrom":subQ1}),1.0]])]});}
            var Q141;
            {var subQ0=sQuery(id+"F0.wireOp",EDGE,"E20");var subQ1=sQuery(id+"F0.wireOp",EDGE,"E1");var subQ2=makeQuery(id+"F0.imprint","INTERSECT",VERTEX,{"derivedFrom":[subQ1,subQ0]});Q141=makeQuery(id+"F0.imprint","IMPRINT",FACE,{"disambiguationData":[TD([[makeQuery(id+"F0.imprint","IMPRINT",EDGE,{"disambiguationData":[TD([[subQ2,-1.0]])],"derivedFrom":subQ1}),1.0]])]});}
            var Q142;
            {var subQ0=sQuery(id+"F0.wireOp",EDGE,"E17");var subQ1=sQuery(id+"F0.wireOp",EDGE,"E1");var subQ2=makeQuery(id+"F0.imprint","INTERSECT",VERTEX,{"derivedFrom":[subQ1,subQ0]});Q142=makeQuery(id+"F0.imprint","IMPRINT",FACE,{"disambiguationData":[TD([[makeQuery(id+"F0.imprint","IMPRINT",EDGE,{"disambiguationData":[TD([[subQ2,-1.0]])],"derivedFrom":subQ1}),-1.0]])]});}
            var Q143;
            {var subQ0=sQuery(id+"F0.wireOp",EDGE,"E21");var subQ1=sQuery(id+"F0.wireOp",EDGE,"E20");var subQ2=makeQuery(id+"F0.imprint","INTERSECT",VERTEX,{"derivedFrom":[subQ1,subQ0]});Q143=makeQuery(id+"F0.imprint","IMPRINT",FACE,{"disambiguationData":[TD([[makeQuery(id+"F0.imprint","IMPRINT",EDGE,{"disambiguationData":[TD([[subQ2,-1.0]])],"derivedFrom":subQ1}),-1.0]])]});}
            var Q144;
            {var subQ0=sQuery(id+"F0.wireOp",EDGE,"E9");var subQ1=sQuery(id+"F0.wireOp",EDGE,"E1");var subQ2=makeQuery(id+"F0.imprint","INTERSECT",VERTEX,{"derivedFrom":[subQ1,subQ0]});Q144=makeQuery(id+"F0.imprint","IMPRINT",FACE,{"disambiguationData":[TD([[makeQuery(id+"F0.imprint","IMPRINT",EDGE,{"disambiguationData":[TD([[subQ2,-1.0]])],"derivedFrom":subQ1}),1.0]])]});}
            var Q145;
            {var subQ5=sQuery(id+"F0.wireOp",EDGE,"E31");var subQ7=sQuery(id+"F0.wireOp",EDGE,"E56");var subQ8=makeQuery(id+"F0.imprint","INTERSECT",VERTEX,{"derivedFrom":[subQ5,subQ7]});Q145=makeQuery(id+"F0.imprint","IMPRINT",FACE,{"disambiguationData":[TD([[makeQuery(id+"F0.imprint","IMPRINT",EDGE,{"disambiguationData":[TD([[subQ8,-1.0]])],"derivedFrom":subQ5}),-1.0]])]});}
            var Q146;
            {var subQ0=sQuery(id+"F0.wireOp",EDGE,"E11");var subQ1=sQuery(id+"F0.wireOp",EDGE,"E4");var subQ2=makeQuery(id+"F0.imprint","INTERSECT",VERTEX,{"derivedFrom":[subQ1,subQ0]});Q146=makeQuery(id+"F0.imprint","IMPRINT",FACE,{"disambiguationData":[TD([[makeQuery(id+"F0.imprint","IMPRINT",EDGE,{"disambiguationData":[TD([[subQ2,-1.0]])],"derivedFrom":subQ1}),1.0]])]});}
            var Q147;
            {var subQ0=sQuery(id+"F0.wireOp",EDGE,"E55");var subQ1=sQuery(id+"F0.wireOp",EDGE,"E51");var subQ2=makeQuery(id+"F0.imprint","INTERSECT",VERTEX,{"derivedFrom":[subQ1,subQ0]});Q147=makeQuery(id+"F0.imprint","IMPRINT",FACE,{"disambiguationData":[TD([[makeQuery(id+"F0.imprint","IMPRINT",EDGE,{"disambiguationData":[TD([[subQ2,-1.0]])],"derivedFrom":subQ1}),1.0]])]});}
            var Q148;
            {var subQ0=sQuery(id+"F0.wireOp",EDGE,"E23");var subQ1=sQuery(id+"F0.wireOp",EDGE,"E16");var subQ2=makeQuery(id+"F0.imprint","INTERSECT",VERTEX,{"derivedFrom":[subQ1,subQ0]});Q148=makeQuery(id+"F0.imprint","IMPRINT",FACE,{"disambiguationData":[TD([[makeQuery(id+"F0.imprint","IMPRINT",EDGE,{"disambiguationData":[TD([[subQ2,-1.0]])],"derivedFrom":subQ1}),-1.0]])]});}
            var Q149;
            {var subQ0=sQuery(id+"F0.wireOp",EDGE,"E35");var subQ1=sQuery(id+"F0.wireOp",EDGE,"E31");var subQ2=makeQuery(id+"F0.imprint","INTERSECT",VERTEX,{"derivedFrom":[subQ1,subQ0]});Q149=makeQuery(id+"F0.imprint","IMPRINT",FACE,{"disambiguationData":[TD([[makeQuery(id+"F0.imprint","IMPRINT",EDGE,{"disambiguationData":[TD([[subQ2,-1.0]])],"derivedFrom":subQ1}),-1.0]])]});}
            var Q150;
            {var subQ1=sQuery(id+"F0.wireOp",EDGE,"E29");var subQ7=sQuery(id+"F0.wireOp",EDGE,"E55");var subQ9=makeQuery(id+"F0.imprint","INTERSECT",VERTEX,{"derivedFrom":[subQ1,subQ7]});Q150=makeQuery(id+"F0.imprint","IMPRINT",FACE,{"disambiguationData":[TD([[makeQuery(id+"F0.imprint","IMPRINT",EDGE,{"disambiguationData":[TD([[subQ9,-1.0]])],"derivedFrom":subQ1}),-1.0]])]});}
            var Q151;
            {var subQ0=sQuery(id+"F0.wireOp",EDGE,"E37");var subQ1=sQuery(id+"F0.wireOp",EDGE,"E6");var subQ2=makeQuery(id+"F0.imprint","INTERSECT",VERTEX,{"derivedFrom":[subQ1,subQ0]});Q151=makeQuery(id+"F0.imprint","IMPRINT",FACE,{"disambiguationData":[TD([[makeQuery(id+"F0.imprint","IMPRINT",EDGE,{"disambiguationData":[TD([[subQ2,-1.0]])],"derivedFrom":subQ1}),1.0]])]});}
            var Q152;
            {var subQ0=sQuery(id+"F0.wireOp",EDGE,"E52");var subQ1=sQuery(id+"F0.wireOp",EDGE,"E48");var subQ2=makeQuery(id+"F0.imprint","INTERSECT",VERTEX,{"derivedFrom":[subQ1,subQ0]});Q152=makeQuery(id+"F0.imprint","IMPRINT",FACE,{"disambiguationData":[TD([[makeQuery(id+"F0.imprint","IMPRINT",EDGE,{"disambiguationData":[TD([[subQ2,-1.0]])],"derivedFrom":subQ1}),-1.0]])]});}
            var Q153;
            {var subQ5=sQuery(id+"F0.wireOp",EDGE,"E4");var subQ9=sQuery(id+"F0.wireOp",EDGE,"E38");var subQ10=makeQuery(id+"F0.imprint","INTERSECT",VERTEX,{"derivedFrom":[subQ5,subQ9]});Q153=makeQuery(id+"F0.imprint","IMPRINT",FACE,{"disambiguationData":[TD([[makeQuery(id+"F0.imprint","IMPRINT",EDGE,{"disambiguationData":[TD([[subQ10,-1.0]])],"derivedFrom":subQ5}),1.0]])]});}
            var Q154;
            {var subQ0=sQuery(id+"F0.wireOp",EDGE,"E24");var subQ1=sQuery(id+"F0.wireOp",EDGE,"E20");var subQ2=makeQuery(id+"F0.imprint","INTERSECT",VERTEX,{"derivedFrom":[subQ1,subQ0]});Q154=makeQuery(id+"F0.imprint","IMPRINT",FACE,{"disambiguationData":[TD([[makeQuery(id+"F0.imprint","IMPRINT",EDGE,{"disambiguationData":[TD([[subQ2,-1.0]])],"derivedFrom":subQ1}),-1.0]])]});}
            var Q155;
            {var subQ0=sQuery(id+"F0.wireOp",EDGE,"E50");var subQ1=sQuery(id+"F0.wireOp",EDGE,"E47");var subQ2=makeQuery(id+"F0.imprint","INTERSECT",VERTEX,{"derivedFrom":[subQ1,subQ0]});Q155=makeQuery(id+"F0.imprint","IMPRINT",FACE,{"disambiguationData":[TD([[makeQuery(id+"F0.imprint","IMPRINT",EDGE,{"disambiguationData":[TD([[subQ2,-1.0]])],"derivedFrom":subQ1}),-1.0]])]});}
            var Q156;
            {var subQ0=sQuery(id+"F0.wireOp",EDGE,"E47");var subQ1=sQuery(id+"F0.wireOp",EDGE,"E30");var subQ2=makeQuery(id+"F0.imprint","INTERSECT",VERTEX,{"derivedFrom":[subQ1,subQ0]});Q156=makeQuery(id+"F0.imprint","IMPRINT",FACE,{"disambiguationData":[TD([[makeQuery(id+"F0.imprint","IMPRINT",EDGE,{"disambiguationData":[TD([[subQ2,-1.0]])],"derivedFrom":subQ1}),-1.0]])]});}
            var Q157;
            {var subQ0=sQuery(id+"F0.wireOp",EDGE,"E37");var subQ1=sQuery(id+"F0.wireOp",EDGE,"E4");var subQ2=makeQuery(id+"F0.imprint","INTERSECT",VERTEX,{"derivedFrom":[subQ1,subQ0]});Q157=makeQuery(id+"F0.imprint","IMPRINT",FACE,{"disambiguationData":[TD([[makeQuery(id+"F0.imprint","IMPRINT",EDGE,{"disambiguationData":[TD([[subQ2,-1.0]])],"derivedFrom":subQ1}),-1.0]])]});}
            var Q158;
            {var subQ0=sQuery(id+"F0.wireOp",EDGE,"E54");var subQ1=sQuery(id+"F0.wireOp",EDGE,"E48");var subQ2=makeQuery(id+"F0.imprint","INTERSECT",VERTEX,{"derivedFrom":[subQ1,subQ0]});Q158=makeQuery(id+"F0.imprint","IMPRINT",FACE,{"disambiguationData":[TD([[makeQuery(id+"F0.imprint","IMPRINT",EDGE,{"disambiguationData":[TD([[subQ2,-1.0]])],"derivedFrom":subQ1}),-1.0]])]});}
            var Q159;
            {var subQ6=sQuery(id+"F0.wireOp",EDGE,"E2");var subQ9=sQuery(id+"F0.wireOp",EDGE,"E21");var subQ11=makeQuery(id+"F0.imprint","INTERSECT",VERTEX,{"derivedFrom":[subQ6,subQ9]});Q159=makeQuery(id+"F0.imprint","IMPRINT",FACE,{"disambiguationData":[TD([[makeQuery(id+"F0.imprint","IMPRINT",EDGE,{"disambiguationData":[TD([[subQ11,-1.0]])],"derivedFrom":subQ6}),1.0]])]});}
            var Q160;
            {var subQ0=sQuery(id+"F0.wireOp",EDGE,"E52");var subQ1=sQuery(id+"F0.wireOp",EDGE,"E47");var subQ2=makeQuery(id+"F0.imprint","INTERSECT",VERTEX,{"derivedFrom":[subQ1,subQ0]});Q160=makeQuery(id+"F0.imprint","IMPRINT",FACE,{"disambiguationData":[TD([[makeQuery(id+"F0.imprint","IMPRINT",EDGE,{"disambiguationData":[TD([[subQ2,-1.0]])],"derivedFrom":subQ1}),-1.0]])]});}
            var Q161;
            {var subQ0=sQuery(id+"F0.wireOp",EDGE,"E40");var subQ1=sQuery(id+"F0.wireOp",EDGE,"E32");var subQ2=makeQuery(id+"F0.imprint","INTERSECT",VERTEX,{"derivedFrom":[subQ1,subQ0]});Q161=makeQuery(id+"F0.imprint","IMPRINT",FACE,{"disambiguationData":[TD([[makeQuery(id+"F0.imprint","IMPRINT",EDGE,{"disambiguationData":[TD([[subQ2,-1.0]])],"derivedFrom":subQ1}),-1.0]])]});}
            var Q162;
            {var subQ1=sQuery(id+"F0.wireOp",EDGE,"E2");var subQ5=sQuery(id+"F0.wireOp",EDGE,"E13");var subQ6=makeQuery(id+"F0.imprint","INTERSECT",VERTEX,{"derivedFrom":[subQ1,subQ5]});Q162=makeQuery(id+"F0.imprint","IMPRINT",FACE,{"disambiguationData":[TD([[makeQuery(id+"F0.imprint","IMPRINT",EDGE,{"disambiguationData":[TD([[subQ6,-1.0]])],"derivedFrom":subQ1}),1.0]])]});}
            var Q163;
            {var subQ0=sQuery(id+"F0.wireOp",EDGE,"E42");var subQ1=sQuery(id+"F0.wireOp",EDGE,"E10");var subQ2=makeQuery(id+"F0.imprint","INTERSECT",VERTEX,{"derivedFrom":[subQ1,subQ0]});Q163=makeQuery(id+"F0.imprint","IMPRINT",FACE,{"disambiguationData":[TD([[makeQuery(id+"F0.imprint","IMPRINT",EDGE,{"disambiguationData":[TD([[subQ2,-1.0]])],"derivedFrom":subQ1}),1.0]])]});}
            var Q164;
            {var subQ7=sQuery(id+"F0.wireOp",EDGE,"E5");var subQ8=sQuery(id+"F0.wireOp",EDGE,"E2");var subQ9=makeQuery(id+"F0.imprint","INTERSECT",VERTEX,{"derivedFrom":[subQ8,subQ7]});Q164=makeQuery(id+"F0.imprint","IMPRINT",FACE,{"disambiguationData":[TD([[makeQuery(id+"F0.imprint","IMPRINT",EDGE,{"disambiguationData":[TD([[subQ9,-1.0]])],"derivedFrom":subQ8}),-1.0]])]});}
            var Q165;
            {var subQ0=sQuery(id+"F0.wireOp",EDGE,"E22");var subQ1=sQuery(id+"F0.wireOp",EDGE,"E20");var subQ2=makeQuery(id+"F0.imprint","INTERSECT",VERTEX,{"derivedFrom":[subQ1,subQ0]});Q165=makeQuery(id+"F0.imprint","IMPRINT",FACE,{"disambiguationData":[TD([[makeQuery(id+"F0.imprint","IMPRINT",EDGE,{"disambiguationData":[TD([[subQ2,-1.0]])],"derivedFrom":subQ1}),-1.0]])]});}
            var Q166;
            {var subQ0=sQuery(id+"F0.wireOp",EDGE,"E10");var subQ1=sQuery(id+"F0.wireOp",EDGE,"E1");var subQ2=makeQuery(id+"F0.imprint","INTERSECT",VERTEX,{"derivedFrom":[subQ1,subQ0]});Q166=makeQuery(id+"F0.imprint","IMPRINT",FACE,{"disambiguationData":[TD([[makeQuery(id+"F0.imprint","IMPRINT",EDGE,{"disambiguationData":[TD([[subQ2,-1.0]])],"derivedFrom":subQ1}),1.0]])]});}
            var Q167;
            {var subQ0=sQuery(id+"F0.wireOp",EDGE,"E23");var subQ1=sQuery(id+"F0.wireOp",EDGE,"E22");var subQ2=makeQuery(id+"F0.imprint","INTERSECT",VERTEX,{"derivedFrom":[subQ1,subQ0]});Q167=makeQuery(id+"F0.imprint","IMPRINT",FACE,{"disambiguationData":[TD([[makeQuery(id+"F0.imprint","IMPRINT",EDGE,{"disambiguationData":[TD([[subQ2,-1.0]])],"derivedFrom":subQ1}),-1.0]])]});}
            var Q168;
            {var subQ0=sQuery(id+"F0.wireOp",EDGE,"E24");var subQ1=sQuery(id+"F0.wireOp",EDGE,"E21");var subQ2=makeQuery(id+"F0.imprint","INTERSECT",VERTEX,{"derivedFrom":[subQ1,subQ0]});Q168=makeQuery(id+"F0.imprint","IMPRINT",FACE,{"disambiguationData":[TD([[makeQuery(id+"F0.imprint","IMPRINT",EDGE,{"disambiguationData":[TD([[subQ2,-1.0]])],"derivedFrom":subQ1}),-1.0]])]});}
            var Q169;
            {var subQ7=sQuery(id+"F0.wireOp",EDGE,"E1");var subQ9=sQuery(id+"F0.wireOp",EDGE,"E7");var subQ10=makeQuery(id+"F0.imprint","INTERSECT",VERTEX,{"derivedFrom":[subQ7,subQ9]});Q169=makeQuery(id+"F0.imprint","IMPRINT",FACE,{"disambiguationData":[TD([[makeQuery(id+"F0.imprint","IMPRINT",EDGE,{"disambiguationData":[TD([[subQ10,-1.0]])],"derivedFrom":subQ7}),-1.0]])]});}
            var Q170;
            {var subQ0=sQuery(id+"F0.wireOp",EDGE,"E49");var subQ1=sQuery(id+"F0.wireOp",EDGE,"E31");var subQ2=makeQuery(id+"F0.imprint","INTERSECT",VERTEX,{"derivedFrom":[subQ1,subQ0]});Q170=makeQuery(id+"F0.imprint","IMPRINT",FACE,{"disambiguationData":[TD([[makeQuery(id+"F0.imprint","IMPRINT",EDGE,{"disambiguationData":[TD([[subQ2,-1.0]])],"derivedFrom":subQ1}),-1.0]])]});}
            var Q171;
            {var subQ0=sQuery(id+"F0.wireOp",EDGE,"E41");var subQ1=sQuery(id+"F0.wireOp",EDGE,"E9");var subQ2=makeQuery(id+"F0.imprint","INTERSECT",VERTEX,{"derivedFrom":[subQ1,subQ0]});Q171=makeQuery(id+"F0.imprint","IMPRINT",FACE,{"disambiguationData":[TD([[makeQuery(id+"F0.imprint","IMPRINT",EDGE,{"disambiguationData":[TD([[subQ2,-1.0]])],"derivedFrom":subQ1}),1.0]])]});}
            var Q172;
            {var subQ0=sQuery(id+"F0.wireOp",EDGE,"E12");var subQ1=sQuery(id+"F0.wireOp",EDGE,"E2");var subQ2=makeQuery(id+"F0.imprint","INTERSECT",VERTEX,{"derivedFrom":[subQ1,subQ0]});Q172=makeQuery(id+"F0.imprint","IMPRINT",FACE,{"disambiguationData":[TD([[makeQuery(id+"F0.imprint","IMPRINT",EDGE,{"disambiguationData":[TD([[subQ2,-1.0]])],"derivedFrom":subQ1}),1.0]])]});}
            var Q173;
            {var subQ0=sQuery(id+"F0.wireOp",EDGE,"E19");var subQ1=sQuery(id+"F0.wireOp",EDGE,"E8");var subQ2=makeQuery(id+"F0.imprint","INTERSECT",VERTEX,{"derivedFrom":[subQ1,subQ0]});Q173=makeQuery(id+"F0.imprint","IMPRINT",FACE,{"disambiguationData":[TD([[makeQuery(id+"F0.imprint","IMPRINT",EDGE,{"disambiguationData":[TD([[subQ2,-1.0]])],"derivedFrom":subQ1}),1.0]])]});}
            var Q174;
            {var subQ5=sQuery(id+"F0.wireOp",EDGE,"E3");var subQ7=sQuery(id+"F0.wireOp",EDGE,"E40");var subQ9=makeQuery(id+"F0.imprint","INTERSECT",VERTEX,{"derivedFrom":[subQ5,subQ7]});Q174=makeQuery(id+"F0.imprint","IMPRINT",FACE,{"disambiguationData":[TD([[makeQuery(id+"F0.imprint","IMPRINT",EDGE,{"disambiguationData":[TD([[subQ9,-1.0]])],"derivedFrom":subQ5}),1.0]])]});}
            var Q175;
            {var subQ0=sQuery(id+"F0.wireOp",EDGE,"E53");var subQ1=sQuery(id+"F0.wireOp",EDGE,"E48");var subQ2=makeQuery(id+"F0.imprint","INTERSECT",VERTEX,{"derivedFrom":[subQ1,subQ0]});Q175=makeQuery(id+"F0.imprint","IMPRINT",FACE,{"disambiguationData":[TD([[makeQuery(id+"F0.imprint","IMPRINT",EDGE,{"disambiguationData":[TD([[subQ2,-1.0]])],"derivedFrom":subQ1}),-1.0]])]});}
            var Q176;
            {var subQ0=sQuery(id+"F0.wireOp",EDGE,"E32");var subQ1=sQuery(id+"F0.wireOp",EDGE,"E10");var subQ2=makeQuery(id+"F0.imprint","INTERSECT",VERTEX,{"derivedFrom":[subQ1,subQ0]});Q176=makeQuery(id+"F0.imprint","IMPRINT",FACE,{"disambiguationData":[TD([[makeQuery(id+"F0.imprint","IMPRINT",EDGE,{"disambiguationData":[TD([[subQ2,-1.0]])],"derivedFrom":subQ1}),1.0]])]});}
            var Q177;
            {var subQ0=sQuery(id+"F0.wireOp",EDGE,"E24");var subQ1=sQuery(id+"F0.wireOp",EDGE,"E17");var subQ2=makeQuery(id+"F0.imprint","INTERSECT",VERTEX,{"derivedFrom":[subQ1,subQ0]});Q177=makeQuery(id+"F0.imprint","IMPRINT",FACE,{"disambiguationData":[TD([[makeQuery(id+"F0.imprint","IMPRINT",EDGE,{"disambiguationData":[TD([[subQ2,-1.0]])],"derivedFrom":subQ1}),-1.0]])]});}
            var Q178;
            {var subQ0=sQuery(id+"F0.wireOp",EDGE,"E14");var subQ1=sQuery(id+"F0.wireOp",EDGE,"E1");var subQ2=makeQuery(id+"F0.imprint","INTERSECT",VERTEX,{"derivedFrom":[subQ1,subQ0]});Q178=makeQuery(id+"F0.imprint","IMPRINT",FACE,{"disambiguationData":[TD([[makeQuery(id+"F0.imprint","IMPRINT",EDGE,{"disambiguationData":[TD([[subQ2,-1.0]])],"derivedFrom":subQ1}),1.0]])]});}
            var Q179;
            {var subQ1=sQuery(id+"F0.wireOp",EDGE,"E2");var subQ9=sQuery(id+"F0.wireOp",EDGE,"E19");var subQ11=makeQuery(id+"F0.imprint","INTERSECT",VERTEX,{"derivedFrom":[subQ1,subQ9]});Q179=makeQuery(id+"F0.imprint","IMPRINT",FACE,{"disambiguationData":[TD([[makeQuery(id+"F0.imprint","IMPRINT",EDGE,{"disambiguationData":[TD([[subQ11,-1.0]])],"derivedFrom":subQ1}),-1.0]])]});}
            var Q180;
            {var subQ0=sQuery(id+"F0.wireOp",EDGE,"E23");var subQ1=sQuery(id+"F0.wireOp",EDGE,"E20");var subQ2=makeQuery(id+"F0.imprint","INTERSECT",VERTEX,{"derivedFrom":[subQ1,subQ0]});Q180=makeQuery(id+"F0.imprint","IMPRINT",FACE,{"disambiguationData":[TD([[makeQuery(id+"F0.imprint","IMPRINT",EDGE,{"disambiguationData":[TD([[subQ2,-1.0]])],"derivedFrom":subQ1}),-1.0]])]});}
            var Q181;
            {var subQ0=sQuery(id+"F0.wireOp",EDGE,"E21");var subQ1=sQuery(id+"F0.wireOp",EDGE,"E17");var subQ2=makeQuery(id+"F0.imprint","INTERSECT",VERTEX,{"derivedFrom":[subQ1,subQ0]});Q181=makeQuery(id+"F0.imprint","IMPRINT",FACE,{"disambiguationData":[TD([[makeQuery(id+"F0.imprint","IMPRINT",EDGE,{"disambiguationData":[TD([[subQ2,-1.0]])],"derivedFrom":subQ1}),-1.0]])]});}
            var Q182;
            {var subQ0=sQuery(id+"F0.wireOp",EDGE,"E49");var subQ1=sQuery(id+"F0.wireOp",EDGE,"E48");var subQ2=makeQuery(id+"F0.imprint","INTERSECT",VERTEX,{"derivedFrom":[subQ1,subQ0]});Q182=makeQuery(id+"F0.imprint","IMPRINT",FACE,{"disambiguationData":[TD([[makeQuery(id+"F0.imprint","IMPRINT",EDGE,{"disambiguationData":[TD([[subQ2,-1.0]])],"derivedFrom":subQ1}),-1.0]])]});}
            var Q183;
            {var subQ5=sQuery(id+"F0.wireOp",EDGE,"E3");var subQ7=sQuery(id+"F0.wireOp",EDGE,"E41");var subQ8=makeQuery(id+"F0.imprint","INTERSECT",VERTEX,{"derivedFrom":[subQ5,subQ7]});Q183=makeQuery(id+"F0.imprint","IMPRINT",FACE,{"disambiguationData":[TD([[makeQuery(id+"F0.imprint","IMPRINT",EDGE,{"disambiguationData":[TD([[subQ8,-1.0]])],"derivedFrom":subQ5}),1.0]])]});}
            var Q184;
            {var subQ0=sQuery(id+"F0.wireOp",EDGE,"E52");var subQ1=sQuery(id+"F0.wireOp",EDGE,"E51");var subQ2=makeQuery(id+"F0.imprint","INTERSECT",VERTEX,{"derivedFrom":[subQ1,subQ0]});Q184=makeQuery(id+"F0.imprint","IMPRINT",FACE,{"disambiguationData":[TD([[makeQuery(id+"F0.imprint","IMPRINT",EDGE,{"disambiguationData":[TD([[subQ2,-1.0]])],"derivedFrom":subQ1}),-1.0]])]});}
            var Q185;
            {var subQ0=sQuery(id+"F0.wireOp",EDGE,"E10");var subQ1=sQuery(id+"F0.wireOp",EDGE,"E2");var subQ2=makeQuery(id+"F0.imprint","INTERSECT",VERTEX,{"derivedFrom":[subQ1,subQ0]});Q185=makeQuery(id+"F0.imprint","IMPRINT",FACE,{"disambiguationData":[TD([[makeQuery(id+"F0.imprint","IMPRINT",EDGE,{"disambiguationData":[TD([[subQ2,-1.0]])],"derivedFrom":subQ1}),1.0]])]});}
            var Q186;
            {var subQ0=sQuery(id+"F0.wireOp",EDGE,"E34");var subQ1=sQuery(id+"F0.wireOp",EDGE,"E9");var subQ2=makeQuery(id+"F0.imprint","INTERSECT",VERTEX,{"derivedFrom":[subQ1,subQ0]});Q186=makeQuery(id+"F0.imprint","IMPRINT",FACE,{"disambiguationData":[TD([[makeQuery(id+"F0.imprint","IMPRINT",EDGE,{"disambiguationData":[TD([[subQ2,-1.0]])],"derivedFrom":subQ1}),1.0]])]});}
            var Q187;
            {var subQ1=sQuery(id+"F0.wireOp",EDGE,"E30");var subQ7=sQuery(id+"F0.wireOp",EDGE,"E31");var subQ8=makeQuery(id+"F0.imprint","INTERSECT",VERTEX,{"derivedFrom":[subQ1,subQ7]});Q187=makeQuery(id+"F0.imprint","IMPRINT",FACE,{"disambiguationData":[TD([[makeQuery(id+"F0.imprint","IMPRINT",EDGE,{"disambiguationData":[TD([[subQ8,-1.0]])],"derivedFrom":subQ1}),1.0]])]});}
            var Q188;
            {var subQ0=sQuery(id+"F0.wireOp",EDGE,"E20");var subQ1=sQuery(id+"F0.wireOp",EDGE,"E18");var subQ2=makeQuery(id+"F0.imprint","INTERSECT",VERTEX,{"derivedFrom":[subQ1,subQ0]});Q188=makeQuery(id+"F0.imprint","IMPRINT",FACE,{"disambiguationData":[TD([[makeQuery(id+"F0.imprint","IMPRINT",EDGE,{"disambiguationData":[TD([[subQ2,-1.0]])],"derivedFrom":subQ1}),-1.0]])]});}
            var Q189;
            {var subQ0=sQuery(id+"F0.wireOp",EDGE,"E13");var subQ1=sQuery(id+"F0.wireOp",EDGE,"E1");var subQ2=makeQuery(id+"F0.imprint","INTERSECT",VERTEX,{"derivedFrom":[subQ1,subQ0]});Q189=makeQuery(id+"F0.imprint","IMPRINT",FACE,{"disambiguationData":[TD([[makeQuery(id+"F0.imprint","IMPRINT",EDGE,{"disambiguationData":[TD([[subQ2,-1.0]])],"derivedFrom":subQ1}),1.0]])]});}
            var Q190;
            {var subQ1=sQuery(id+"F0.wireOp",EDGE,"E3");var subQ7=sQuery(id+"F0.wireOp",EDGE,"E20");var subQ9=makeQuery(id+"F0.imprint","INTERSECT",VERTEX,{"derivedFrom":[subQ1,subQ7]});Q190=makeQuery(id+"F0.imprint","IMPRINT",FACE,{"disambiguationData":[TD([[makeQuery(id+"F0.imprint","IMPRINT",EDGE,{"disambiguationData":[TD([[subQ9,-1.0]])],"derivedFrom":subQ1}),-1.0]])]});}
            var Q191;
            {var subQ0=sQuery(id+"F0.wireOp",EDGE,"E34");var subQ1=sQuery(id+"F0.wireOp",EDGE,"E7");var subQ2=makeQuery(id+"F0.imprint","INTERSECT",VERTEX,{"derivedFrom":[subQ1,subQ0]});Q191=makeQuery(id+"F0.imprint","IMPRINT",FACE,{"disambiguationData":[TD([[makeQuery(id+"F0.imprint","IMPRINT",EDGE,{"disambiguationData":[TD([[subQ2,-1.0]])],"derivedFrom":subQ1}),1.0]])]});}
            var Q192;
            {var subQ0=sQuery(id+"F0.wireOp",EDGE,"E41");var subQ1=sQuery(id+"F0.wireOp",EDGE,"E32");var subQ2=makeQuery(id+"F0.imprint","INTERSECT",VERTEX,{"derivedFrom":[subQ1,subQ0]});Q192=makeQuery(id+"F0.imprint","IMPRINT",FACE,{"disambiguationData":[TD([[makeQuery(id+"F0.imprint","IMPRINT",EDGE,{"disambiguationData":[TD([[subQ2,-1.0]])],"derivedFrom":subQ1}),-1.0]])]});}
            var Q193;
            {var subQ0=sQuery(id+"F0.wireOp",EDGE,"E42");var subQ1=sQuery(id+"F0.wireOp",EDGE,"E9");var subQ2=makeQuery(id+"F0.imprint","INTERSECT",VERTEX,{"derivedFrom":[subQ1,subQ0]});Q193=makeQuery(id+"F0.imprint","IMPRINT",FACE,{"disambiguationData":[TD([[makeQuery(id+"F0.imprint","IMPRINT",EDGE,{"disambiguationData":[TD([[subQ2,-1.0]])],"derivedFrom":subQ1}),-1.0]])]});}
            var Q194;
            {var subQ0=sQuery(id+"F0.wireOp",EDGE,"E15");var subQ1=sQuery(id+"F0.wireOp",EDGE,"E11");var subQ2=makeQuery(id+"F0.imprint","INTERSECT",VERTEX,{"derivedFrom":[subQ1,subQ0]});Q194=makeQuery(id+"F0.imprint","IMPRINT",FACE,{"disambiguationData":[TD([[makeQuery(id+"F0.imprint","IMPRINT",EDGE,{"disambiguationData":[TD([[subQ2,-1.0]])],"derivedFrom":subQ1}),-1.0]])]});}
            var Q195;
            {var subQ0=sQuery(id+"F0.wireOp",EDGE,"E38");var subQ1=sQuery(id+"F0.wireOp",EDGE,"E32");var subQ2=makeQuery(id+"F0.imprint","INTERSECT",VERTEX,{"derivedFrom":[subQ1,subQ0]});Q195=makeQuery(id+"F0.imprint","IMPRINT",FACE,{"disambiguationData":[TD([[makeQuery(id+"F0.imprint","IMPRINT",EDGE,{"disambiguationData":[TD([[subQ2,-1.0]])],"derivedFrom":subQ1}),-1.0]])]});}
            var Q196;
            {var subQ0=sQuery(id+"F0.wireOp",EDGE,"E24");var subQ1=sQuery(id+"F0.wireOp",EDGE,"E18");var subQ2=makeQuery(id+"F0.imprint","INTERSECT",VERTEX,{"derivedFrom":[subQ1,subQ0]});Q196=makeQuery(id+"F0.imprint","IMPRINT",FACE,{"disambiguationData":[TD([[makeQuery(id+"F0.imprint","IMPRINT",EDGE,{"disambiguationData":[TD([[subQ2,-1.0]])],"derivedFrom":subQ1}),-1.0]])]});}
            var Q197;
            {var subQ0=sQuery(id+"F0.wireOp",EDGE,"E23");var subQ1=sQuery(id+"F0.wireOp",EDGE,"E17");var subQ2=makeQuery(id+"F0.imprint","INTERSECT",VERTEX,{"derivedFrom":[subQ1,subQ0]});Q197=makeQuery(id+"F0.imprint","IMPRINT",FACE,{"disambiguationData":[TD([[makeQuery(id+"F0.imprint","IMPRINT",EDGE,{"disambiguationData":[TD([[subQ2,-1.0]])],"derivedFrom":subQ1}),-1.0]])]});}
            var Q198;
            {var subQ0=sQuery(id+"F0.wireOp",EDGE,"E48");var subQ1=sQuery(id+"F0.wireOp",EDGE,"E24");var subQ2=makeQuery(id+"F0.imprint","INTERSECT",VERTEX,{"derivedFrom":[subQ1,subQ0]});Q198=makeQuery(id+"F0.imprint","IMPRINT",FACE,{"disambiguationData":[TD([[makeQuery(id+"F0.imprint","IMPRINT",EDGE,{"disambiguationData":[TD([[subQ2,-1.0]])],"derivedFrom":subQ1}),-1.0]])]});}
            var Q199;
            {var subQ0=sQuery(id+"F0.wireOp",EDGE,"E5");var subQ1=sQuery(id+"F0.wireOp",EDGE,"E1");var subQ2=makeQuery(id+"F0.imprint","INTERSECT",VERTEX,{"derivedFrom":[subQ1,subQ0]});Q199=makeQuery(id+"F0.imprint","IMPRINT",FACE,{"disambiguationData":[TD([[makeQuery(id+"F0.imprint","IMPRINT",EDGE,{"disambiguationData":[TD([[subQ2,-1.0]])],"derivedFrom":subQ1}),1.0]])]});}
            var Q200;
            {var subQ0=sQuery(id+"F0.wireOp",EDGE,"E36");var subQ1=sQuery(id+"F0.wireOp",EDGE,"E32");var subQ2=makeQuery(id+"F0.imprint","INTERSECT",VERTEX,{"derivedFrom":[subQ1,subQ0]});Q200=makeQuery(id+"F0.imprint","IMPRINT",FACE,{"disambiguationData":[TD([[makeQuery(id+"F0.imprint","IMPRINT",EDGE,{"disambiguationData":[TD([[subQ2,-1.0]])],"derivedFrom":subQ1}),-1.0]])]});}
            var Q201;
            {var subQ0=sQuery(id+"F0.wireOp",EDGE,"E58");var subQ1=sQuery(id+"F0.wireOp",EDGE,"E30");var subQ2=makeQuery(id+"F0.imprint","INTERSECT",VERTEX,{"derivedFrom":[subQ1,subQ0]});Q201=makeQuery(id+"F0.imprint","IMPRINT",FACE,{"disambiguationData":[TD([[makeQuery(id+"F0.imprint","IMPRINT",EDGE,{"disambiguationData":[TD([[subQ2,-1.0]])],"derivedFrom":subQ1}),1.0]])]});}
            var Q202;
            {var subQ0=sQuery(id+"F0.wireOp",EDGE,"E15");var subQ1=sQuery(id+"F0.wireOp",EDGE,"E3");var subQ2=makeQuery(id+"F0.imprint","INTERSECT",VERTEX,{"derivedFrom":[subQ1,subQ0]});Q202=makeQuery(id+"F0.imprint","IMPRINT",FACE,{"disambiguationData":[TD([[makeQuery(id+"F0.imprint","IMPRINT",EDGE,{"disambiguationData":[TD([[subQ2,-1.0]])],"derivedFrom":subQ1}),-1.0]])]});}
            var Q203;
            {var subQ0=sQuery(id+"F0.wireOp",EDGE,"E39");var subQ1=sQuery(id+"F0.wireOp",EDGE,"E32");var subQ2=makeQuery(id+"F0.imprint","INTERSECT",VERTEX,{"derivedFrom":[subQ1,subQ0]});Q203=makeQuery(id+"F0.imprint","IMPRINT",FACE,{"disambiguationData":[TD([[makeQuery(id+"F0.imprint","IMPRINT",EDGE,{"disambiguationData":[TD([[subQ2,-1.0]])],"derivedFrom":subQ1}),-1.0]])]});}
            var Q204;
            {var subQ0=sQuery(id+"F0.wireOp",EDGE,"E41");var subQ1=sQuery(id+"F0.wireOp",EDGE,"E2");var subQ2=makeQuery(id+"F0.imprint","INTERSECT",VERTEX,{"derivedFrom":[subQ1,subQ0]});Q204=makeQuery(id+"F0.imprint","IMPRINT",FACE,{"disambiguationData":[TD([[makeQuery(id+"F0.imprint","IMPRINT",EDGE,{"disambiguationData":[TD([[subQ2,-1.0]])],"derivedFrom":subQ1}),1.0]])]});}
            var Q205;
            {var subQ1=sQuery(id+"F0.wireOp",EDGE,"E3");var subQ7=sQuery(id+"F0.wireOp",EDGE,"E15");var subQ8=makeQuery(id+"F0.imprint","INTERSECT",VERTEX,{"derivedFrom":[subQ1,subQ7]});Q205=makeQuery(id+"F0.imprint","IMPRINT",FACE,{"disambiguationData":[TD([[makeQuery(id+"F0.imprint","IMPRINT",EDGE,{"disambiguationData":[TD([[subQ8,-1.0]])],"derivedFrom":subQ1}),1.0]])]});}
            var Q206;
            {var subQ1=sQuery(id+"F0.wireOp",EDGE,"E31");var subQ7=sQuery(id+"F0.wireOp",EDGE,"E57");var subQ9=makeQuery(id+"F0.imprint","INTERSECT",VERTEX,{"derivedFrom":[subQ1,subQ7]});Q206=makeQuery(id+"F0.imprint","IMPRINT",FACE,{"disambiguationData":[TD([[makeQuery(id+"F0.imprint","IMPRINT",EDGE,{"disambiguationData":[TD([[subQ9,-1.0]])],"derivedFrom":subQ1}),-1.0]])]});}
            var Q207;
            {var subQ0=sQuery(id+"F0.wireOp",EDGE,"E18");var subQ1=sQuery(id+"F0.wireOp",EDGE,"E2");var subQ2=makeQuery(id+"F0.imprint","INTERSECT",VERTEX,{"derivedFrom":[subQ1,subQ0]});Q207=makeQuery(id+"F0.imprint","IMPRINT",FACE,{"disambiguationData":[TD([[makeQuery(id+"F0.imprint","IMPRINT",EDGE,{"disambiguationData":[TD([[subQ2,-1.0]])],"derivedFrom":subQ1}),1.0]])]});}
            var Q208;
            {var subQ0=sQuery(id+"F0.wireOp",EDGE,"E21");var subQ1=sQuery(id+"F0.wireOp",EDGE,"E3");var subQ2=makeQuery(id+"F0.imprint","INTERSECT",VERTEX,{"derivedFrom":[subQ1,subQ0]});Q208=makeQuery(id+"F0.imprint","IMPRINT",FACE,{"disambiguationData":[TD([[makeQuery(id+"F0.imprint","IMPRINT",EDGE,{"disambiguationData":[TD([[subQ2,-1.0]])],"derivedFrom":subQ1}),1.0]])]});}
            var Q209;
            {var subQ0=sQuery(id+"F0.wireOp",EDGE,"E14");var subQ1=sQuery(id+"F0.wireOp",EDGE,"E6");var subQ2=makeQuery(id+"F0.imprint","INTERSECT",VERTEX,{"derivedFrom":[subQ1,subQ0]});Q209=makeQuery(id+"F0.imprint","IMPRINT",FACE,{"disambiguationData":[TD([[makeQuery(id+"F0.imprint","IMPRINT",EDGE,{"disambiguationData":[TD([[subQ2,-1.0]])],"derivedFrom":subQ1}),1.0]])]});}
            var Q210;
            {var subQ0=sQuery(id+"F0.wireOp",EDGE,"E52");var subQ1=sQuery(id+"F0.wireOp",EDGE,"E49");var subQ2=makeQuery(id+"F0.imprint","INTERSECT",VERTEX,{"derivedFrom":[subQ1,subQ0]});Q210=makeQuery(id+"F0.imprint","IMPRINT",FACE,{"disambiguationData":[TD([[makeQuery(id+"F0.imprint","IMPRINT",EDGE,{"disambiguationData":[TD([[subQ2,-1.0]])],"derivedFrom":subQ1}),-1.0]])]});}
            var Q211;
            {var subQ0=sQuery(id+"F0.wireOp",EDGE,"E51");var subQ1=sQuery(id+"F0.wireOp",EDGE,"E29");var subQ2=makeQuery(id+"F0.imprint","INTERSECT",VERTEX,{"derivedFrom":[subQ1,subQ0]});Q211=makeQuery(id+"F0.imprint","IMPRINT",FACE,{"disambiguationData":[TD([[makeQuery(id+"F0.imprint","IMPRINT",EDGE,{"disambiguationData":[TD([[subQ2,-1.0]])],"derivedFrom":subQ1}),-1.0]])]});}
            var Q212;
            {var subQ0=sQuery(id+"F0.wireOp",EDGE,"E54");var subQ1=sQuery(id+"F0.wireOp",EDGE,"E49");var subQ2=makeQuery(id+"F0.imprint","INTERSECT",VERTEX,{"derivedFrom":[subQ1,subQ0]});Q212=makeQuery(id+"F0.imprint","IMPRINT",FACE,{"disambiguationData":[TD([[makeQuery(id+"F0.imprint","IMPRINT",EDGE,{"disambiguationData":[TD([[subQ2,-1.0]])],"derivedFrom":subQ1}),-1.0]])]});}
            var Q213;
            {var subQ0=sQuery(id+"F0.wireOp",EDGE,"E23");var subQ1=sQuery(id+"F0.wireOp",EDGE,"E18");var subQ2=makeQuery(id+"F0.imprint","INTERSECT",VERTEX,{"derivedFrom":[subQ1,subQ0]});Q213=makeQuery(id+"F0.imprint","IMPRINT",FACE,{"disambiguationData":[TD([[makeQuery(id+"F0.imprint","IMPRINT",EDGE,{"disambiguationData":[TD([[subQ2,-1.0]])],"derivedFrom":subQ1}),-1.0]])]});}
            var Q214;
            {var subQ0=sQuery(id+"F0.wireOp",EDGE,"E7");var subQ1=sQuery(id+"F0.wireOp",EDGE,"E3");var subQ2=makeQuery(id+"F0.imprint","INTERSECT",VERTEX,{"derivedFrom":[subQ1,subQ0]});Q214=makeQuery(id+"F0.imprint","IMPRINT",FACE,{"disambiguationData":[TD([[makeQuery(id+"F0.imprint","IMPRINT",EDGE,{"disambiguationData":[TD([[subQ2,-1.0]])],"derivedFrom":subQ1}),1.0]])]});}
            var Q215;
            {var subQ1=sQuery(id+"F0.wireOp",EDGE,"E3");var subQ5=sQuery(id+"F0.wireOp",EDGE,"E12");var subQ6=makeQuery(id+"F0.imprint","INTERSECT",VERTEX,{"derivedFrom":[subQ1,subQ5]});Q215=makeQuery(id+"F0.imprint","IMPRINT",FACE,{"disambiguationData":[TD([[makeQuery(id+"F0.imprint","IMPRINT",EDGE,{"disambiguationData":[TD([[subQ6,-1.0]])],"derivedFrom":subQ1}),1.0]])]});}
            var Q216;
            {var subQ0=sQuery(id+"F0.wireOp",EDGE,"E34");var subQ1=sQuery(id+"F0.wireOp",EDGE,"E30");var subQ2=makeQuery(id+"F0.imprint","INTERSECT",VERTEX,{"derivedFrom":[subQ1,subQ0]});Q216=makeQuery(id+"F0.imprint","IMPRINT",FACE,{"disambiguationData":[TD([[makeQuery(id+"F0.imprint","IMPRINT",EDGE,{"disambiguationData":[TD([[subQ2,-1.0]])],"derivedFrom":subQ1}),-1.0]])]});}
            var Q217;
            {var subQ0=sQuery(id+"F0.wireOp",EDGE,"E40");var subQ1=sQuery(id+"F0.wireOp",EDGE,"E4");var subQ2=makeQuery(id+"F0.imprint","INTERSECT",VERTEX,{"derivedFrom":[subQ1,subQ0]});Q217=makeQuery(id+"F0.imprint","IMPRINT",FACE,{"disambiguationData":[TD([[makeQuery(id+"F0.imprint","IMPRINT",EDGE,{"disambiguationData":[TD([[subQ2,-1.0]])],"derivedFrom":subQ1}),-1.0]])]});}
            var Q218;
            {var subQ0=sQuery(id+"F0.wireOp",EDGE,"E8");var subQ1=sQuery(id+"F0.wireOp",EDGE,"E1");var subQ2=makeQuery(id+"F0.imprint","INTERSECT",VERTEX,{"derivedFrom":[subQ1,subQ0]});Q218=makeQuery(id+"F0.imprint","IMPRINT",FACE,{"disambiguationData":[TD([[makeQuery(id+"F0.imprint","IMPRINT",EDGE,{"disambiguationData":[TD([[subQ2,-1.0]])],"derivedFrom":subQ1}),1.0]])]});}
            var Q219;
            {var subQ0=sQuery(id+"F0.wireOp",EDGE,"E22");var subQ1=sQuery(id+"F0.wireOp",EDGE,"E3");var subQ2=makeQuery(id+"F0.imprint","INTERSECT",VERTEX,{"derivedFrom":[subQ1,subQ0]});Q219=makeQuery(id+"F0.imprint","IMPRINT",FACE,{"disambiguationData":[TD([[makeQuery(id+"F0.imprint","IMPRINT",EDGE,{"disambiguationData":[TD([[subQ2,-1.0]])],"derivedFrom":subQ1}),-1.0]])]});}
            var Q220;
            {var subQ0=sQuery(id+"F0.wireOp",EDGE,"E33");var subQ1=sQuery(id+"F0.wireOp",EDGE,"E11");var subQ2=makeQuery(id+"F0.imprint","INTERSECT",VERTEX,{"derivedFrom":[subQ1,subQ0]});Q220=makeQuery(id+"F0.imprint","IMPRINT",FACE,{"disambiguationData":[TD([[makeQuery(id+"F0.imprint","IMPRINT",EDGE,{"disambiguationData":[TD([[subQ2,-1.0]])],"derivedFrom":subQ1}),1.0]])]});}
            var Q221;
            {var subQ0=sQuery(id+"F0.wireOp",EDGE,"E34");var subQ1=sQuery(id+"F0.wireOp",EDGE,"E9");var subQ2=makeQuery(id+"F0.imprint","INTERSECT",VERTEX,{"derivedFrom":[subQ1,subQ0]});Q221=makeQuery(id+"F0.imprint","IMPRINT",FACE,{"disambiguationData":[TD([[makeQuery(id+"F0.imprint","IMPRINT",EDGE,{"disambiguationData":[TD([[subQ2,-1.0]])],"derivedFrom":subQ1}),-1.0]])]});}
            var Q222;
            {var subQ0=sQuery(id+"F0.wireOp",EDGE,"E53");var subQ1=sQuery(id+"F0.wireOp",EDGE,"E49");var subQ2=makeQuery(id+"F0.imprint","INTERSECT",VERTEX,{"derivedFrom":[subQ1,subQ0]});Q222=makeQuery(id+"F0.imprint","IMPRINT",FACE,{"disambiguationData":[TD([[makeQuery(id+"F0.imprint","IMPRINT",EDGE,{"disambiguationData":[TD([[subQ2,-1.0]])],"derivedFrom":subQ1}),-1.0]])]});}
            var Q223;
            {var subQ7=sQuery(id+"F0.wireOp",EDGE,"E36");var subQ8=sQuery(id+"F0.wireOp",EDGE,"E6");var subQ9=makeQuery(id+"F0.imprint","INTERSECT",VERTEX,{"derivedFrom":[subQ8,subQ7]});Q223=makeQuery(id+"F0.imprint","IMPRINT",FACE,{"disambiguationData":[TD([[makeQuery(id+"F0.imprint","IMPRINT",EDGE,{"disambiguationData":[TD([[subQ9,-1.0]])],"derivedFrom":subQ8}),1.0]])]});}
            var Q224;
            {var subQ0=sQuery(id+"F0.wireOp",EDGE,"E11");var subQ1=sQuery(id+"F0.wireOp",EDGE,"E2");var subQ2=makeQuery(id+"F0.imprint","INTERSECT",VERTEX,{"derivedFrom":[subQ1,subQ0]});Q224=makeQuery(id+"F0.imprint","IMPRINT",FACE,{"disambiguationData":[TD([[makeQuery(id+"F0.imprint","IMPRINT",EDGE,{"disambiguationData":[TD([[subQ2,-1.0]])],"derivedFrom":subQ1}),1.0]])]});}
            var Q225;
            {var subQ0=sQuery(id+"F0.wireOp",EDGE,"E54");var subQ1=sQuery(id+"F0.wireOp",EDGE,"E47");var subQ2=makeQuery(id+"F0.imprint","INTERSECT",VERTEX,{"derivedFrom":[subQ1,subQ0]});Q225=makeQuery(id+"F0.imprint","IMPRINT",FACE,{"disambiguationData":[TD([[makeQuery(id+"F0.imprint","IMPRINT",EDGE,{"disambiguationData":[TD([[subQ2,-1.0]])],"derivedFrom":subQ1}),-1.0]])]});}
            var Q226;
            {var subQ1=sQuery(id+"F0.wireOp",EDGE,"E6");var subQ7=sQuery(id+"F0.wireOp",EDGE,"E41");var subQ9=makeQuery(id+"F0.imprint","INTERSECT",VERTEX,{"derivedFrom":[subQ1,subQ7]});Q226=makeQuery(id+"F0.imprint","IMPRINT",FACE,{"disambiguationData":[TD([[makeQuery(id+"F0.imprint","IMPRINT",EDGE,{"disambiguationData":[TD([[subQ9,-1.0]])],"derivedFrom":subQ1}),1.0]])]});}
            var Q227;
            {var subQ39=sQuery(id+"F0.wireOp",EDGE,"E4");var subQ42=sQuery(id+"F0.wireOp",EDGE,"E18");var subQ43=makeQuery(id+"F0.imprint","INTERSECT",VERTEX,{"derivedFrom":[subQ39,subQ42]});Q227=makeQuery(id+"F0.imprint","IMPRINT",FACE,{"disambiguationData":[TD([[makeQuery(id+"F0.imprint","IMPRINT",EDGE,{"disambiguationData":[TD([[subQ43,-1.0]])],"derivedFrom":subQ39}),1.0]])]});}
            var Q228;
            {var subQ0=sQuery(id+"F0.wireOp",EDGE,"E22");var subQ1=sQuery(id+"F0.wireOp",EDGE,"E1");var subQ2=makeQuery(id+"F0.imprint","INTERSECT",VERTEX,{"derivedFrom":[subQ1,subQ0]});Q228=makeQuery(id+"F0.imprint","IMPRINT",FACE,{"disambiguationData":[TD([[makeQuery(id+"F0.imprint","IMPRINT",EDGE,{"disambiguationData":[TD([[subQ2,-1.0]])],"derivedFrom":subQ1}),-1.0]])]});}
            var Q229;
            {var subQ7=sQuery(id+"F0.wireOp",EDGE,"E36");var subQ9=sQuery(id+"F0.wireOp",EDGE,"E7");var subQ10=makeQuery(id+"F0.imprint","INTERSECT",VERTEX,{"derivedFrom":[subQ9,subQ7]});Q229=makeQuery(id+"F0.imprint","IMPRINT",FACE,{"disambiguationData":[TD([[makeQuery(id+"F0.imprint","IMPRINT",EDGE,{"disambiguationData":[TD([[subQ10,-1.0]])],"derivedFrom":subQ9}),1.0]])]});}
            var Q230;
            {var subQ0=sQuery(id+"F0.wireOp",EDGE,"E22");var subQ1=sQuery(id+"F0.wireOp",EDGE,"E21");var subQ2=makeQuery(id+"F0.imprint","INTERSECT",VERTEX,{"derivedFrom":[subQ1,subQ0]});Q230=makeQuery(id+"F0.imprint","IMPRINT",FACE,{"disambiguationData":[TD([[makeQuery(id+"F0.imprint","IMPRINT",EDGE,{"disambiguationData":[TD([[subQ2,-1.0]])],"derivedFrom":subQ1}),-1.0]])]});}
            var Q231;
            {var subQ0=sQuery(id+"F0.wireOp",EDGE,"E33");var subQ1=sQuery(id+"F0.wireOp",EDGE,"E10");var subQ2=makeQuery(id+"F0.imprint","INTERSECT",VERTEX,{"derivedFrom":[subQ1,subQ0]});Q231=makeQuery(id+"F0.imprint","IMPRINT",FACE,{"disambiguationData":[TD([[makeQuery(id+"F0.imprint","IMPRINT",EDGE,{"disambiguationData":[TD([[subQ2,-1.0]])],"derivedFrom":subQ1}),-1.0]])]});}
            var Q232;
            {var subQ5=sQuery(id+"F0.wireOp",EDGE,"E22");var subQ7=sQuery(id+"F0.wireOp",EDGE,"E3");var subQ9=makeQuery(id+"F0.imprint","INTERSECT",VERTEX,{"derivedFrom":[subQ7,subQ5]});Q232=makeQuery(id+"F0.imprint","IMPRINT",FACE,{"disambiguationData":[TD([[makeQuery(id+"F0.imprint","IMPRINT",EDGE,{"disambiguationData":[TD([[subQ9,-1.0]])],"derivedFrom":subQ7}),1.0]])]});}
            var Q233;
            {var subQ0=sQuery(id+"F0.wireOp",EDGE,"E22");var subQ1=sQuery(id+"F0.wireOp",EDGE,"E16");var subQ2=makeQuery(id+"F0.imprint","INTERSECT",VERTEX,{"derivedFrom":[subQ1,subQ0]});Q233=makeQuery(id+"F0.imprint","IMPRINT",FACE,{"disambiguationData":[TD([[makeQuery(id+"F0.imprint","IMPRINT",EDGE,{"disambiguationData":[TD([[subQ2,-1.0]])],"derivedFrom":subQ1}),-1.0]])]});}
            var Q234;
            {var subQ0=sQuery(id+"F0.wireOp",EDGE,"E7");var subQ1=sQuery(id+"F0.wireOp",EDGE,"E2");var subQ2=makeQuery(id+"F0.imprint","INTERSECT",VERTEX,{"derivedFrom":[subQ1,subQ0]});Q234=makeQuery(id+"F0.imprint","IMPRINT",FACE,{"disambiguationData":[TD([[makeQuery(id+"F0.imprint","IMPRINT",EDGE,{"disambiguationData":[TD([[subQ2,-1.0]])],"derivedFrom":subQ1}),1.0]])]});}
            var Q235;
            {var subQ0=sQuery(id+"F0.wireOp",EDGE,"E25");var subQ1=sQuery(id+"F0.wireOp",EDGE,"E18");var subQ2=makeQuery(id+"F0.imprint","INTERSECT",VERTEX,{"derivedFrom":[subQ1,subQ0]});Q235=makeQuery(id+"F0.imprint","IMPRINT",FACE,{"disambiguationData":[TD([[makeQuery(id+"F0.imprint","IMPRINT",EDGE,{"disambiguationData":[TD([[subQ2,-1.0]])],"derivedFrom":subQ1}),-1.0]])]});}
            var Q236;
            {var subQ0=sQuery(id+"F0.wireOp",EDGE,"E50");var subQ1=sQuery(id+"F0.wireOp",EDGE,"E49");var subQ2=makeQuery(id+"F0.imprint","INTERSECT",VERTEX,{"derivedFrom":[subQ1,subQ0]});Q236=makeQuery(id+"F0.imprint","IMPRINT",FACE,{"disambiguationData":[TD([[makeQuery(id+"F0.imprint","IMPRINT",EDGE,{"disambiguationData":[TD([[subQ2,-1.0]])],"derivedFrom":subQ1}),-1.0]])]});}
            var Q237;
            {var subQ0=sQuery(id+"F0.wireOp",EDGE,"E22");var subQ1=sQuery(id+"F0.wireOp",EDGE,"E18");var subQ2=makeQuery(id+"F0.imprint","INTERSECT",VERTEX,{"derivedFrom":[subQ1,subQ0]});Q237=makeQuery(id+"F0.imprint","IMPRINT",FACE,{"disambiguationData":[TD([[makeQuery(id+"F0.imprint","IMPRINT",EDGE,{"disambiguationData":[TD([[subQ2,-1.0]])],"derivedFrom":subQ1}),-1.0]])]});}
            var Q238;
            {var subQ0=sQuery(id+"F0.wireOp",EDGE,"E21");var subQ1=sQuery(id+"F0.wireOp",EDGE,"E16");var subQ2=makeQuery(id+"F0.imprint","INTERSECT",VERTEX,{"derivedFrom":[subQ1,subQ0]});Q238=makeQuery(id+"F0.imprint","IMPRINT",FACE,{"disambiguationData":[TD([[makeQuery(id+"F0.imprint","IMPRINT",EDGE,{"disambiguationData":[TD([[subQ2,-1.0]])],"derivedFrom":subQ1}),-1.0]])]});}
            var Q239;
            {var subQ0=sQuery(id+"F0.wireOp",EDGE,"E32");var subQ1=sQuery(id+"F0.wireOp",EDGE,"E9");var subQ2=makeQuery(id+"F0.imprint","INTERSECT",VERTEX,{"derivedFrom":[subQ1,subQ0]});Q239=makeQuery(id+"F0.imprint","IMPRINT",FACE,{"disambiguationData":[TD([[makeQuery(id+"F0.imprint","IMPRINT",EDGE,{"disambiguationData":[TD([[subQ2,-1.0]])],"derivedFrom":subQ1}),-1.0]])]});}
            var Q240;
            {var subQ0=sQuery(id+"F0.wireOp",EDGE,"E19");var subQ1=sQuery(id+"F0.wireOp",EDGE,"E2");var subQ2=makeQuery(id+"F0.imprint","INTERSECT",VERTEX,{"derivedFrom":[subQ1,subQ0]});Q240=makeQuery(id+"F0.imprint","IMPRINT",FACE,{"disambiguationData":[TD([[makeQuery(id+"F0.imprint","IMPRINT",EDGE,{"disambiguationData":[TD([[subQ2,-1.0]])],"derivedFrom":subQ1}),1.0]])]});}
            var Q241;
            {var subQ0=sQuery(id+"F0.wireOp",EDGE,"E9");var subQ1=sQuery(id+"F0.wireOp",EDGE,"E4");var subQ2=makeQuery(id+"F0.imprint","INTERSECT",VERTEX,{"derivedFrom":[subQ1,subQ0]});Q241=makeQuery(id+"F0.imprint","IMPRINT",FACE,{"disambiguationData":[TD([[makeQuery(id+"F0.imprint","IMPRINT",EDGE,{"disambiguationData":[TD([[subQ2,-1.0]])],"derivedFrom":subQ1}),1.0]])]});}
            var Q242;
            {var subQ0=sQuery(id+"F0.wireOp",EDGE,"E35");var subQ1=sQuery(id+"F0.wireOp",EDGE,"E28");var subQ2=makeQuery(id+"F0.imprint","INTERSECT",VERTEX,{"derivedFrom":[subQ1,subQ0]});Q242=makeQuery(id+"F0.imprint","IMPRINT",FACE,{"disambiguationData":[TD([[makeQuery(id+"F0.imprint","IMPRINT",EDGE,{"disambiguationData":[TD([[subQ2,-1.0]])],"derivedFrom":subQ1}),1.0]])]});}
            var Q243;
            {var subQ0=sQuery(id+"F0.wireOp",EDGE,"E8");var subQ1=sQuery(id+"F0.wireOp",EDGE,"E3");var subQ2=makeQuery(id+"F0.imprint","INTERSECT",VERTEX,{"derivedFrom":[subQ1,subQ0]});Q243=makeQuery(id+"F0.imprint","IMPRINT",FACE,{"disambiguationData":[TD([[makeQuery(id+"F0.imprint","IMPRINT",EDGE,{"disambiguationData":[TD([[subQ2,-1.0]])],"derivedFrom":subQ1}),1.0]])]});}
            var Q244;
            {var subQ0=sQuery(id+"F0.wireOp",EDGE,"E15");var subQ1=sQuery(id+"F0.wireOp",EDGE,"E1");var subQ2=makeQuery(id+"F0.imprint","INTERSECT",VERTEX,{"derivedFrom":[subQ1,subQ0]});Q244=makeQuery(id+"F0.imprint","IMPRINT",FACE,{"disambiguationData":[TD([[makeQuery(id+"F0.imprint","IMPRINT",EDGE,{"disambiguationData":[TD([[subQ2,-1.0]])],"derivedFrom":subQ1}),-1.0]])]});}
            var Q245;
            {var subQ0=sQuery(id+"F0.wireOp",EDGE,"E55");var subQ1=sQuery(id+"F0.wireOp",EDGE,"E47");var subQ2=makeQuery(id+"F0.imprint","INTERSECT",VERTEX,{"derivedFrom":[subQ1,subQ0]});Q245=makeQuery(id+"F0.imprint","IMPRINT",FACE,{"disambiguationData":[TD([[makeQuery(id+"F0.imprint","IMPRINT",EDGE,{"disambiguationData":[TD([[subQ2,-1.0]])],"derivedFrom":subQ1}),-1.0]])]});}
            var Q246;
            {var subQ1=sQuery(id+"F0.wireOp",EDGE,"E14");var subQ7=sQuery(id+"F0.wireOp",EDGE,"E4");var subQ8=makeQuery(id+"F0.imprint","INTERSECT",VERTEX,{"derivedFrom":[subQ7,subQ1]});Q246=makeQuery(id+"F0.imprint","IMPRINT",FACE,{"disambiguationData":[TD([[makeQuery(id+"F0.imprint","IMPRINT",EDGE,{"disambiguationData":[TD([[subQ8,-1.0]])],"derivedFrom":subQ7}),-1.0]])]});}
            var Q247;
            {var subQ0=sQuery(id+"F0.wireOp",EDGE,"E51");var subQ1=sQuery(id+"F0.wireOp",EDGE,"E47");var subQ2=makeQuery(id+"F0.imprint","INTERSECT",VERTEX,{"derivedFrom":[subQ1,subQ0]});Q247=makeQuery(id+"F0.imprint","IMPRINT",FACE,{"disambiguationData":[TD([[makeQuery(id+"F0.imprint","IMPRINT",EDGE,{"disambiguationData":[TD([[subQ2,-1.0]])],"derivedFrom":subQ1}),-1.0]])]});}
            var Q248;
            {var subQ0=sQuery(id+"F0.wireOp",EDGE,"E47");var subQ1=sQuery(id+"F0.wireOp",EDGE,"E29");var subQ2=makeQuery(id+"F0.imprint","INTERSECT",VERTEX,{"derivedFrom":[subQ1,subQ0]});Q248=makeQuery(id+"F0.imprint","IMPRINT",FACE,{"disambiguationData":[TD([[makeQuery(id+"F0.imprint","IMPRINT",EDGE,{"disambiguationData":[TD([[subQ2,-1.0]])],"derivedFrom":subQ1}),-1.0]])]});}
            var Q249;
            {var subQ0=sQuery(id+"F0.wireOp",EDGE,"E51");var subQ1=sQuery(id+"F0.wireOp",EDGE,"E50");var subQ2=makeQuery(id+"F0.imprint","INTERSECT",VERTEX,{"derivedFrom":[subQ1,subQ0]});Q249=makeQuery(id+"F0.imprint","IMPRINT",FACE,{"disambiguationData":[TD([[makeQuery(id+"F0.imprint","IMPRINT",EDGE,{"disambiguationData":[TD([[subQ2,-1.0]])],"derivedFrom":subQ1}),-1.0]])]});}
            var Q250;
            {var subQ0=sQuery(id+"F0.wireOp",EDGE,"E24");var subQ1=sQuery(id+"F0.wireOp",EDGE,"E16");var subQ2=makeQuery(id+"F0.imprint","INTERSECT",VERTEX,{"derivedFrom":[subQ1,subQ0]});Q250=makeQuery(id+"F0.imprint","IMPRINT",FACE,{"disambiguationData":[TD([[makeQuery(id+"F0.imprint","IMPRINT",EDGE,{"disambiguationData":[TD([[subQ2,-1.0]])],"derivedFrom":subQ1}),-1.0]])]});}
            var Q251;
            {var subQ1=sQuery(id+"F0.wireOp",EDGE,"E29");var subQ7=sQuery(id+"F0.wireOp",EDGE,"E56");var subQ9=makeQuery(id+"F0.imprint","INTERSECT",VERTEX,{"derivedFrom":[subQ1,subQ7]});Q251=makeQuery(id+"F0.imprint","IMPRINT",FACE,{"disambiguationData":[TD([[makeQuery(id+"F0.imprint","IMPRINT",EDGE,{"disambiguationData":[TD([[subQ9,-1.0]])],"derivedFrom":subQ1}),-1.0]])]});}
            var Q252;
            {var subQ0=sQuery(id+"F0.wireOp",EDGE,"E21");var subQ1=sQuery(id+"F0.wireOp",EDGE,"E18");var subQ2=makeQuery(id+"F0.imprint","INTERSECT",VERTEX,{"derivedFrom":[subQ1,subQ0]});Q252=makeQuery(id+"F0.imprint","IMPRINT",FACE,{"disambiguationData":[TD([[makeQuery(id+"F0.imprint","IMPRINT",EDGE,{"disambiguationData":[TD([[subQ2,-1.0]])],"derivedFrom":subQ1}),-1.0]])]});}
            var Q253;
            {var subQ0=sQuery(id+"F0.wireOp",EDGE,"E51");var subQ1=sQuery(id+"F0.wireOp",EDGE,"E48");var subQ2=makeQuery(id+"F0.imprint","INTERSECT",VERTEX,{"derivedFrom":[subQ1,subQ0]});Q253=makeQuery(id+"F0.imprint","IMPRINT",FACE,{"disambiguationData":[TD([[makeQuery(id+"F0.imprint","IMPRINT",EDGE,{"disambiguationData":[TD([[subQ2,-1.0]])],"derivedFrom":subQ1}),-1.0]])]});}
            var Q254;
            {var subQ0=sQuery(id+"F0.wireOp",EDGE,"E22");var subQ1=sQuery(id+"F0.wireOp",EDGE,"E17");var subQ2=makeQuery(id+"F0.imprint","INTERSECT",VERTEX,{"derivedFrom":[subQ1,subQ0]});Q254=makeQuery(id+"F0.imprint","IMPRINT",FACE,{"disambiguationData":[TD([[makeQuery(id+"F0.imprint","IMPRINT",EDGE,{"disambiguationData":[TD([[subQ2,-1.0]])],"derivedFrom":subQ1}),-1.0]])]});}
            var Q255;
            {var subQ0=sQuery(id+"F0.wireOp",EDGE,"E42");var subQ1=sQuery(id+"F0.wireOp",EDGE,"E5");var subQ2=makeQuery(id+"F0.imprint","INTERSECT",VERTEX,{"derivedFrom":[subQ1,subQ0]});Q255=makeQuery(id+"F0.imprint","IMPRINT",FACE,{"disambiguationData":[TD([[makeQuery(id+"F0.imprint","IMPRINT",EDGE,{"disambiguationData":[TD([[subQ2,-1.0]])],"derivedFrom":subQ1}),1.0]])]});}
            var Q256;
            {var subQ0=sQuery(id+"F0.wireOp",EDGE,"E53");var subQ1=sQuery(id+"F0.wireOp",EDGE,"E50");var subQ2=makeQuery(id+"F0.imprint","INTERSECT",VERTEX,{"derivedFrom":[subQ1,subQ0]});Q256=makeQuery(id+"F0.imprint","IMPRINT",FACE,{"disambiguationData":[TD([[makeQuery(id+"F0.imprint","IMPRINT",EDGE,{"disambiguationData":[TD([[subQ2,-1.0]])],"derivedFrom":subQ1}),-1.0]])]});}
            var Q257;
            {var subQ0=sQuery(id+"F0.wireOp",EDGE,"E22");var subQ1=sQuery(id+"F0.wireOp",EDGE,"E2");var subQ2=makeQuery(id+"F0.imprint","INTERSECT",VERTEX,{"derivedFrom":[subQ1,subQ0]});Q257=makeQuery(id+"F0.imprint","IMPRINT",FACE,{"disambiguationData":[TD([[makeQuery(id+"F0.imprint","IMPRINT",EDGE,{"disambiguationData":[TD([[subQ2,-1.0]])],"derivedFrom":subQ1}),1.0]])]});}
            var Q258;
            {var subQ0=sQuery(id+"F0.wireOp",EDGE,"E42");var subQ1=sQuery(id+"F0.wireOp",EDGE,"E2");var subQ2=makeQuery(id+"F0.imprint","INTERSECT",VERTEX,{"derivedFrom":[subQ1,subQ0]});Q258=makeQuery(id+"F0.imprint","IMPRINT",FACE,{"disambiguationData":[TD([[makeQuery(id+"F0.imprint","IMPRINT",EDGE,{"disambiguationData":[TD([[subQ2,-1.0]])],"derivedFrom":subQ1}),1.0]])]});}
            var Q259;
            {var subQ0=sQuery(id+"F0.wireOp",EDGE,"E11");var subQ1=sQuery(id+"F0.wireOp",EDGE,"E6");var subQ2=makeQuery(id+"F0.imprint","INTERSECT",VERTEX,{"derivedFrom":[subQ1,subQ0]});Q259=makeQuery(id+"F0.imprint","IMPRINT",FACE,{"disambiguationData":[TD([[makeQuery(id+"F0.imprint","IMPRINT",EDGE,{"disambiguationData":[TD([[subQ2,-1.0]])],"derivedFrom":subQ1}),1.0]])]});}
            var Q260;
            {var subQ0=sQuery(id+"F0.wireOp",EDGE,"E18");var subQ1=sQuery(id+"F0.wireOp",EDGE,"E6");var subQ2=makeQuery(id+"F0.imprint","INTERSECT",VERTEX,{"derivedFrom":[subQ1,subQ0]});Q260=makeQuery(id+"F0.imprint","IMPRINT",FACE,{"disambiguationData":[TD([[makeQuery(id+"F0.imprint","IMPRINT",EDGE,{"disambiguationData":[TD([[subQ2,-1.0]])],"derivedFrom":subQ1}),-1.0]])]});}
            var Q261;
            {var subQ0=sQuery(id+"F0.wireOp",EDGE,"E15");var subQ1=sQuery(id+"F0.wireOp",EDGE,"E8");var subQ2=makeQuery(id+"F0.imprint","INTERSECT",VERTEX,{"derivedFrom":[subQ1,subQ0]});Q261=makeQuery(id+"F0.imprint","IMPRINT",FACE,{"disambiguationData":[TD([[makeQuery(id+"F0.imprint","IMPRINT",EDGE,{"disambiguationData":[TD([[subQ2,-1.0]])],"derivedFrom":subQ1}),-1.0]])]});}
            var Q262;
            {var subQ0=sQuery(id+"F0.wireOp",EDGE,"E13");var subQ1=sQuery(id+"F0.wireOp",EDGE,"E4");var subQ2=makeQuery(id+"F0.imprint","INTERSECT",VERTEX,{"derivedFrom":[subQ1,subQ0]});Q262=makeQuery(id+"F0.imprint","IMPRINT",FACE,{"disambiguationData":[TD([[makeQuery(id+"F0.imprint","IMPRINT",EDGE,{"disambiguationData":[TD([[subQ2,-1.0]])],"derivedFrom":subQ1}),1.0]])]});}
            var Q263;
            {var subQ0=sQuery(id+"F0.wireOp",EDGE,"E52");var subQ1=sQuery(id+"F0.wireOp",EDGE,"E29");var subQ2=makeQuery(id+"F0.imprint","INTERSECT",VERTEX,{"derivedFrom":[subQ1,subQ0]});Q263=makeQuery(id+"F0.imprint","IMPRINT",FACE,{"disambiguationData":[TD([[makeQuery(id+"F0.imprint","IMPRINT",EDGE,{"disambiguationData":[TD([[subQ2,-1.0]])],"derivedFrom":subQ1}),-1.0]])]});}
            var Q264;
            {var subQ0=sQuery(id+"F0.wireOp",EDGE,"E36");var subQ1=sQuery(id+"F0.wireOp",EDGE,"E8");var subQ2=makeQuery(id+"F0.imprint","INTERSECT",VERTEX,{"derivedFrom":[subQ1,subQ0]});Q264=makeQuery(id+"F0.imprint","IMPRINT",FACE,{"disambiguationData":[TD([[makeQuery(id+"F0.imprint","IMPRINT",EDGE,{"disambiguationData":[TD([[subQ2,-1.0]])],"derivedFrom":subQ1}),1.0]])]});}
            var Q265;
            {var subQ0=sQuery(id+"F0.wireOp",EDGE,"E13");var subQ1=sQuery(id+"F0.wireOp",EDGE,"E3");var subQ2=makeQuery(id+"F0.imprint","INTERSECT",VERTEX,{"derivedFrom":[subQ1,subQ0]});Q265=makeQuery(id+"F0.imprint","IMPRINT",FACE,{"disambiguationData":[TD([[makeQuery(id+"F0.imprint","IMPRINT",EDGE,{"disambiguationData":[TD([[subQ2,-1.0]])],"derivedFrom":subQ1}),1.0]])]});}
            var Q266;
            {var subQ0=sQuery(id+"F0.wireOp",EDGE,"E33");var subQ1=sQuery(id+"F0.wireOp",EDGE,"E29");var subQ2=makeQuery(id+"F0.imprint","INTERSECT",VERTEX,{"derivedFrom":[subQ1,subQ0]});Q266=makeQuery(id+"F0.imprint","IMPRINT",FACE,{"disambiguationData":[TD([[makeQuery(id+"F0.imprint","IMPRINT",EDGE,{"disambiguationData":[TD([[subQ2,-1.0]])],"derivedFrom":subQ1}),1.0]])]});}
            var Q267;
            {var subQ1=sQuery(id+"F0.wireOp",EDGE,"E3");var subQ7=sQuery(id+"F0.wireOp",EDGE,"E18");var subQ9=makeQuery(id+"F0.imprint","INTERSECT",VERTEX,{"derivedFrom":[subQ1,subQ7]});Q267=makeQuery(id+"F0.imprint","IMPRINT",FACE,{"disambiguationData":[TD([[makeQuery(id+"F0.imprint","IMPRINT",EDGE,{"disambiguationData":[TD([[subQ9,-1.0]])],"derivedFrom":subQ1}),1.0]])]});}
            var Q268;
            {var subQ0=sQuery(id+"F0.wireOp",EDGE,"E33");var subQ1=sQuery(id+"F0.wireOp",EDGE,"E9");var subQ2=makeQuery(id+"F0.imprint","INTERSECT",VERTEX,{"derivedFrom":[subQ1,subQ0]});Q268=makeQuery(id+"F0.imprint","IMPRINT",FACE,{"disambiguationData":[TD([[makeQuery(id+"F0.imprint","IMPRINT",EDGE,{"disambiguationData":[TD([[subQ2,-1.0]])],"derivedFrom":subQ1}),-1.0]])]});}
            var Q269;
            {var subQ0=sQuery(id+"F0.wireOp",EDGE,"E40");var subQ1=sQuery(id+"F0.wireOp",EDGE,"E1");var subQ2=makeQuery(id+"F0.imprint","INTERSECT",VERTEX,{"derivedFrom":[subQ1,subQ0]});Q269=makeQuery(id+"F0.imprint","IMPRINT",FACE,{"disambiguationData":[TD([[makeQuery(id+"F0.imprint","IMPRINT",EDGE,{"disambiguationData":[TD([[subQ2,-1.0]])],"derivedFrom":subQ1}),1.0]])]});}
            var Q270;
            {var subQ0=sQuery(id+"F0.wireOp",EDGE,"E20");var subQ1=sQuery(id+"F0.wireOp",EDGE,"E2");var subQ2=makeQuery(id+"F0.imprint","INTERSECT",VERTEX,{"derivedFrom":[subQ1,subQ0]});Q270=makeQuery(id+"F0.imprint","IMPRINT",FACE,{"disambiguationData":[TD([[makeQuery(id+"F0.imprint","IMPRINT",EDGE,{"disambiguationData":[TD([[subQ2,-1.0]])],"derivedFrom":subQ1}),1.0]])]});}
            var Q271;
            {var subQ0=sQuery(id+"F0.wireOp",EDGE,"E9");var subQ1=sQuery(id+"F0.wireOp",EDGE,"E1");var subQ2=makeQuery(id+"F0.imprint","INTERSECT",VERTEX,{"derivedFrom":[subQ1,subQ0]});Q271=makeQuery(id+"F0.imprint","IMPRINT",FACE,{"disambiguationData":[TD([[makeQuery(id+"F0.imprint","IMPRINT",EDGE,{"disambiguationData":[TD([[subQ2,-1.0]])],"derivedFrom":subQ1}),-1.0]])]});}
            var Q272;
            {var subQ0=sQuery(id+"F0.wireOp",EDGE,"E49");var subQ1=sQuery(id+"F0.wireOp",EDGE,"E47");var subQ2=makeQuery(id+"F0.imprint","INTERSECT",VERTEX,{"derivedFrom":[subQ1,subQ0]});Q272=makeQuery(id+"F0.imprint","IMPRINT",FACE,{"disambiguationData":[TD([[makeQuery(id+"F0.imprint","IMPRINT",EDGE,{"disambiguationData":[TD([[subQ2,-1.0]])],"derivedFrom":subQ1}),-1.0]])]});}
            var Q273;
            {var subQ0=sQuery(id+"F0.wireOp",EDGE,"E30");var subQ1=sQuery(id+"F0.wireOp",EDGE,"E29");var subQ2=makeQuery(id+"F0.imprint","INTERSECT",VERTEX,{"derivedFrom":[subQ1,subQ0]});Q273=makeQuery(id+"F0.imprint","IMPRINT",FACE,{"disambiguationData":[TD([[makeQuery(id+"F0.imprint","IMPRINT",EDGE,{"disambiguationData":[TD([[subQ2,-1.0]])],"derivedFrom":subQ1}),-1.0]])]});}
            var Q274;
            {var subQ0=sQuery(id+"F0.wireOp",EDGE,"E56");var subQ1=sQuery(id+"F0.wireOp",EDGE,"E47");var subQ2=makeQuery(id+"F0.imprint","INTERSECT",VERTEX,{"derivedFrom":[subQ1,subQ0]});Q274=makeQuery(id+"F0.imprint","IMPRINT",FACE,{"disambiguationData":[TD([[makeQuery(id+"F0.imprint","IMPRINT",EDGE,{"disambiguationData":[TD([[subQ2,-1.0]])],"derivedFrom":subQ1}),-1.0]])]});}
            var Q275;
            {var subQ0=sQuery(id+"F0.wireOp",EDGE,"E36");var subQ1=sQuery(id+"F0.wireOp",EDGE,"E7");var subQ2=makeQuery(id+"F0.imprint","INTERSECT",VERTEX,{"derivedFrom":[subQ1,subQ0]});Q275=makeQuery(id+"F0.imprint","IMPRINT",FACE,{"disambiguationData":[TD([[makeQuery(id+"F0.imprint","IMPRINT",EDGE,{"disambiguationData":[TD([[subQ2,-1.0]])],"derivedFrom":subQ1}),-1.0]])]});}
            var Q276;
            {var subQ0=sQuery(id+"F0.wireOp",EDGE,"E6");var subQ1=sQuery(id+"F0.wireOp",EDGE,"E3");var subQ2=makeQuery(id+"F0.imprint","INTERSECT",VERTEX,{"derivedFrom":[subQ1,subQ0]});Q276=makeQuery(id+"F0.imprint","IMPRINT",FACE,{"disambiguationData":[TD([[makeQuery(id+"F0.imprint","IMPRINT",EDGE,{"disambiguationData":[TD([[subQ2,-1.0]])],"derivedFrom":subQ1}),1.0]])]});}
            var Q277;
            {var subQ0=sQuery(id+"F0.wireOp",EDGE,"E9");var subQ1=sQuery(id+"F0.wireOp",EDGE,"E2");var subQ2=makeQuery(id+"F0.imprint","INTERSECT",VERTEX,{"derivedFrom":[subQ1,subQ0]});Q277=makeQuery(id+"F0.imprint","IMPRINT",FACE,{"disambiguationData":[TD([[makeQuery(id+"F0.imprint","IMPRINT",EDGE,{"disambiguationData":[TD([[subQ2,-1.0]])],"derivedFrom":subQ1}),1.0]])]});}
            var Q278;
            {var subQ0=sQuery(id+"F0.wireOp",EDGE,"E37");var subQ1=sQuery(id+"F0.wireOp",EDGE,"E32");var subQ2=makeQuery(id+"F0.imprint","INTERSECT",VERTEX,{"derivedFrom":[subQ1,subQ0]});Q278=makeQuery(id+"F0.imprint","IMPRINT",FACE,{"disambiguationData":[TD([[makeQuery(id+"F0.imprint","IMPRINT",EDGE,{"disambiguationData":[TD([[subQ2,-1.0]])],"derivedFrom":subQ1}),-1.0]])]});}
            var Q279;
            {var subQ0=sQuery(id+"F0.wireOp",EDGE,"E38");var subQ1=sQuery(id+"F0.wireOp",EDGE,"E5");var subQ2=makeQuery(id+"F0.imprint","INTERSECT",VERTEX,{"derivedFrom":[subQ1,subQ0]});Q279=makeQuery(id+"F0.imprint","IMPRINT",FACE,{"disambiguationData":[TD([[makeQuery(id+"F0.imprint","IMPRINT",EDGE,{"disambiguationData":[TD([[subQ2,-1.0]])],"derivedFrom":subQ1}),-1.0]])]});}
            var Q280;
            {var subQ0=sQuery(id+"F0.wireOp",EDGE,"E57");var subQ1=sQuery(id+"F0.wireOp",EDGE,"E33");var subQ2=makeQuery(id+"F0.imprint","INTERSECT",VERTEX,{"derivedFrom":[subQ1,subQ0]});Q280=makeQuery(id+"F0.imprint","IMPRINT",FACE,{"disambiguationData":[TD([[makeQuery(id+"F0.imprint","IMPRINT",EDGE,{"disambiguationData":[TD([[subQ2,-1.0]])],"derivedFrom":subQ1}),1.0]])]});}
            var Q281;
            {var subQ0=sQuery(id+"F0.wireOp",EDGE,"E37");var subQ1=sQuery(id+"F0.wireOp",EDGE,"E5");var subQ2=makeQuery(id+"F0.imprint","INTERSECT",VERTEX,{"derivedFrom":[subQ1,subQ0]});Q281=makeQuery(id+"F0.imprint","IMPRINT",FACE,{"disambiguationData":[TD([[makeQuery(id+"F0.imprint","IMPRINT",EDGE,{"disambiguationData":[TD([[subQ2,-1.0]])],"derivedFrom":subQ1}),-1.0]])]});}
            var Q282;
            {var subQ0=sQuery(id+"F0.wireOp",EDGE,"E20");var subQ1=sQuery(id+"F0.wireOp",EDGE,"E3");var subQ2=makeQuery(id+"F0.imprint","INTERSECT",VERTEX,{"derivedFrom":[subQ1,subQ0]});Q282=makeQuery(id+"F0.imprint","IMPRINT",FACE,{"disambiguationData":[TD([[makeQuery(id+"F0.imprint","IMPRINT",EDGE,{"disambiguationData":[TD([[subQ2,-1.0]])],"derivedFrom":subQ1}),1.0]])]});}
            var Q283;
            {var subQ0=sQuery(id+"F0.wireOp",EDGE,"E52");var subQ1=sQuery(id+"F0.wireOp",EDGE,"E50");var subQ2=makeQuery(id+"F0.imprint","INTERSECT",VERTEX,{"derivedFrom":[subQ1,subQ0]});Q283=makeQuery(id+"F0.imprint","IMPRINT",FACE,{"disambiguationData":[TD([[makeQuery(id+"F0.imprint","IMPRINT",EDGE,{"disambiguationData":[TD([[subQ2,-1.0]])],"derivedFrom":subQ1}),-1.0]])]});}
            var Q284;
            {var subQ0=sQuery(id+"F0.wireOp",EDGE,"E16");var subQ1=sQuery(id+"F0.wireOp",EDGE,"E2");var subQ2=makeQuery(id+"F0.imprint","INTERSECT",VERTEX,{"derivedFrom":[subQ1,subQ0]});Q284=makeQuery(id+"F0.imprint","IMPRINT",FACE,{"disambiguationData":[TD([[makeQuery(id+"F0.imprint","IMPRINT",EDGE,{"disambiguationData":[TD([[subQ2,-1.0]])],"derivedFrom":subQ1}),1.0]])]});}
            var Q285;
            {var subQ0=sQuery(id+"F0.wireOp",EDGE,"E11");var subQ1=sQuery(id+"F0.wireOp",EDGE,"E3");var subQ2=makeQuery(id+"F0.imprint","INTERSECT",VERTEX,{"derivedFrom":[subQ1,subQ0]});Q285=makeQuery(id+"F0.imprint","IMPRINT",FACE,{"disambiguationData":[TD([[makeQuery(id+"F0.imprint","IMPRINT",EDGE,{"disambiguationData":[TD([[subQ2,-1.0]])],"derivedFrom":subQ1}),1.0]])]});}
            var Q286;
            {var subQ0=sQuery(id+"F0.wireOp",EDGE,"E23");var subQ1=sQuery(id+"F0.wireOp",EDGE,"E19");var subQ2=makeQuery(id+"F0.imprint","INTERSECT",VERTEX,{"derivedFrom":[subQ1,subQ0]});Q286=makeQuery(id+"F0.imprint","IMPRINT",FACE,{"disambiguationData":[TD([[makeQuery(id+"F0.imprint","IMPRINT",EDGE,{"disambiguationData":[TD([[subQ2,-1.0]])],"derivedFrom":subQ1}),-1.0]])]});}
            var Q287;
            {var subQ0=sQuery(id+"F0.wireOp",EDGE,"E13");var subQ1=sQuery(id+"F0.wireOp",EDGE,"E1");var subQ2=makeQuery(id+"F0.imprint","INTERSECT",VERTEX,{"derivedFrom":[subQ1,subQ0]});Q287=makeQuery(id+"F0.imprint","IMPRINT",FACE,{"disambiguationData":[TD([[makeQuery(id+"F0.imprint","IMPRINT",EDGE,{"disambiguationData":[TD([[subQ2,-1.0]])],"derivedFrom":subQ1}),-1.0]])]});}
            var Q288;
            {var subQ0=sQuery(id+"F0.wireOp",EDGE,"E14");var subQ1=sQuery(id+"F0.wireOp",EDGE,"E4");var subQ2=makeQuery(id+"F0.imprint","INTERSECT",VERTEX,{"derivedFrom":[subQ1,subQ0]});Q288=makeQuery(id+"F0.imprint","IMPRINT",FACE,{"disambiguationData":[TD([[makeQuery(id+"F0.imprint","IMPRINT",EDGE,{"disambiguationData":[TD([[subQ2,-1.0]])],"derivedFrom":subQ1}),1.0]])]});}
            var Q289;
            {var subQ0=sQuery(id+"F0.wireOp",EDGE,"E20");var subQ1=sQuery(id+"F0.wireOp",EDGE,"E17");var subQ2=makeQuery(id+"F0.imprint","INTERSECT",VERTEX,{"derivedFrom":[subQ1,subQ0]});Q289=makeQuery(id+"F0.imprint","IMPRINT",FACE,{"disambiguationData":[TD([[makeQuery(id+"F0.imprint","IMPRINT",EDGE,{"disambiguationData":[TD([[subQ2,-1.0]])],"derivedFrom":subQ1}),-1.0]])]});}
            var Q290;
            {var subQ0=sQuery(id+"F0.wireOp",EDGE,"E17");var subQ1=sQuery(id+"F0.wireOp",EDGE,"E2");var subQ2=makeQuery(id+"F0.imprint","INTERSECT",VERTEX,{"derivedFrom":[subQ1,subQ0]});Q290=makeQuery(id+"F0.imprint","IMPRINT",FACE,{"disambiguationData":[TD([[makeQuery(id+"F0.imprint","IMPRINT",EDGE,{"disambiguationData":[TD([[subQ2,-1.0]])],"derivedFrom":subQ1}),1.0]])]});}
            var Q291;
            {var subQ0=sQuery(id+"F0.wireOp",EDGE,"E31");var subQ1=sQuery(id+"F0.wireOp",EDGE,"E28");var subQ2=makeQuery(id+"F0.imprint","INTERSECT",VERTEX,{"derivedFrom":[subQ1,subQ0]});Q291=makeQuery(id+"F0.imprint","IMPRINT",FACE,{"disambiguationData":[TD([[makeQuery(id+"F0.imprint","IMPRINT",EDGE,{"disambiguationData":[TD([[subQ2,-1.0]])],"derivedFrom":subQ1}),-1.0]])]});}
            var Q292;
            {var subQ0=sQuery(id+"F0.wireOp",EDGE,"E21");var subQ1=sQuery(id+"F0.wireOp",EDGE,"E1");var subQ2=makeQuery(id+"F0.imprint","INTERSECT",VERTEX,{"derivedFrom":[subQ1,subQ0]});Q292=makeQuery(id+"F0.imprint","IMPRINT",FACE,{"disambiguationData":[TD([[makeQuery(id+"F0.imprint","IMPRINT",EDGE,{"disambiguationData":[TD([[subQ2,-1.0]])],"derivedFrom":subQ1}),1.0]])]});}
            var Q293;
            {var subQ0=sQuery(id+"F0.wireOp",EDGE,"E5");var subQ1=sQuery(id+"F0.wireOp",EDGE,"E4");var subQ2=makeQuery(id+"F0.imprint","INTERSECT",VERTEX,{"derivedFrom":[subQ1,subQ0]});Q293=makeQuery(id+"F0.imprint","IMPRINT",FACE,{"disambiguationData":[TD([[makeQuery(id+"F0.imprint","IMPRINT",EDGE,{"disambiguationData":[TD([[subQ2,-1.0]])],"derivedFrom":subQ1}),1.0]])]});}
            var Q294;
            {var subQ1=sQuery(id+"F0.wireOp",EDGE,"E29");var subQ5=sQuery(id+"F0.wireOp",EDGE,"E50");var subQ6=makeQuery(id+"F0.imprint","INTERSECT",VERTEX,{"derivedFrom":[subQ1,subQ5]});Q294=makeQuery(id+"F0.imprint","IMPRINT",FACE,{"disambiguationData":[TD([[makeQuery(id+"F0.imprint","IMPRINT",EDGE,{"disambiguationData":[TD([[subQ6,-1.0]])],"derivedFrom":subQ1}),-1.0]])]});}
            var Q295;
            {var subQ0=sQuery(id+"F0.wireOp",EDGE,"E5");var subQ1=sQuery(id+"F0.wireOp",EDGE,"E2");var subQ2=makeQuery(id+"F0.imprint","INTERSECT",VERTEX,{"derivedFrom":[subQ1,subQ0]});Q295=makeQuery(id+"F0.imprint","IMPRINT",FACE,{"disambiguationData":[TD([[makeQuery(id+"F0.imprint","IMPRINT",EDGE,{"disambiguationData":[TD([[subQ2,-1.0]])],"derivedFrom":subQ1}),1.0]])]});}
            var Q296;
            {var subQ0=sQuery(id+"F0.wireOp",EDGE,"E16");var subQ1=sQuery(id+"F0.wireOp",EDGE,"E6");var subQ2=makeQuery(id+"F0.imprint","INTERSECT",VERTEX,{"derivedFrom":[subQ1,subQ0]});Q296=makeQuery(id+"F0.imprint","IMPRINT",FACE,{"disambiguationData":[TD([[makeQuery(id+"F0.imprint","IMPRINT",EDGE,{"disambiguationData":[TD([[subQ2,-1.0]])],"derivedFrom":subQ1}),-1.0]])]});}
            var Q297;
            {var subQ0=sQuery(id+"F0.wireOp",EDGE,"E8");var subQ1=sQuery(id+"F0.wireOp",EDGE,"E7");var subQ2=makeQuery(id+"F0.imprint","INTERSECT",VERTEX,{"derivedFrom":[subQ1,subQ0]});Q297=makeQuery(id+"F0.imprint","IMPRINT",FACE,{"disambiguationData":[TD([[makeQuery(id+"F0.imprint","IMPRINT",EDGE,{"disambiguationData":[TD([[subQ2,-1.0]])],"derivedFrom":subQ1}),1.0]])]});}
            var Q298;
            {var subQ0=sQuery(id+"F0.wireOp",EDGE,"E40");var subQ1=sQuery(id+"F0.wireOp",EDGE,"E7");var subQ2=makeQuery(id+"F0.imprint","INTERSECT",VERTEX,{"derivedFrom":[subQ1,subQ0]});Q298=makeQuery(id+"F0.imprint","IMPRINT",FACE,{"disambiguationData":[TD([[makeQuery(id+"F0.imprint","IMPRINT",EDGE,{"disambiguationData":[TD([[subQ2,-1.0]])],"derivedFrom":subQ1}),-1.0]])]});}
            var Q299;
            {var subQ0=sQuery(id+"F0.wireOp",EDGE,"E15");var subQ1=sQuery(id+"F0.wireOp",EDGE,"E7");var subQ2=makeQuery(id+"F0.imprint","INTERSECT",VERTEX,{"derivedFrom":[subQ1,subQ0]});Q299=makeQuery(id+"F0.imprint","IMPRINT",FACE,{"disambiguationData":[TD([[makeQuery(id+"F0.imprint","IMPRINT",EDGE,{"disambiguationData":[TD([[subQ2,-1.0]])],"derivedFrom":subQ1}),-1.0]])]});}
            var Q300;
            {var subQ0=sQuery(id+"F0.wireOp",EDGE,"E9");var subQ1=sQuery(id+"F0.wireOp",EDGE,"E3");var subQ2=makeQuery(id+"F0.imprint","INTERSECT",VERTEX,{"derivedFrom":[subQ1,subQ0]});Q300=makeQuery(id+"F0.imprint","IMPRINT",FACE,{"disambiguationData":[TD([[makeQuery(id+"F0.imprint","IMPRINT",EDGE,{"disambiguationData":[TD([[subQ2,-1.0]])],"derivedFrom":subQ1}),1.0]])]});}
            var Q301;
            {var subQ0=sQuery(id+"F0.wireOp",EDGE,"E38");var subQ1=sQuery(id+"F0.wireOp",EDGE,"E36");var subQ2=makeQuery(id+"F0.imprint","INTERSECT",VERTEX,{"derivedFrom":[subQ1,subQ0]});Q301=makeQuery(id+"F0.imprint","IMPRINT",FACE,{"disambiguationData":[TD([[makeQuery(id+"F0.imprint","IMPRINT",EDGE,{"disambiguationData":[TD([[subQ2,-1.0]])],"derivedFrom":subQ1}),-1.0]])]});}
            var Q302;
            {var subQ0=sQuery(id+"F0.wireOp",EDGE,"E55");var subQ1=sQuery(id+"F0.wireOp",EDGE,"E49");var subQ2=makeQuery(id+"F0.imprint","INTERSECT",VERTEX,{"derivedFrom":[subQ1,subQ0]});Q302=makeQuery(id+"F0.imprint","IMPRINT",FACE,{"disambiguationData":[TD([[makeQuery(id+"F0.imprint","IMPRINT",EDGE,{"disambiguationData":[TD([[subQ2,-1.0]])],"derivedFrom":subQ1}),-1.0]])]});}
            var Q303;
            {var subQ0=sQuery(id+"F0.wireOp",EDGE,"E41");var subQ1=sQuery(id+"F0.wireOp",EDGE,"E4");var subQ2=makeQuery(id+"F0.imprint","INTERSECT",VERTEX,{"derivedFrom":[subQ1,subQ0]});Q303=makeQuery(id+"F0.imprint","IMPRINT",FACE,{"disambiguationData":[TD([[makeQuery(id+"F0.imprint","IMPRINT",EDGE,{"disambiguationData":[TD([[subQ2,-1.0]])],"derivedFrom":subQ1}),-1.0]])]});}
            var Q304;
            {var subQ0=sQuery(id+"F0.wireOp",EDGE,"E38");var subQ1=sQuery(id+"F0.wireOp",EDGE,"E3");var subQ2=makeQuery(id+"F0.imprint","INTERSECT",VERTEX,{"derivedFrom":[subQ1,subQ0]});Q304=makeQuery(id+"F0.imprint","IMPRINT",FACE,{"disambiguationData":[TD([[makeQuery(id+"F0.imprint","IMPRINT",EDGE,{"disambiguationData":[TD([[subQ2,-1.0]])],"derivedFrom":subQ1}),1.0]])]});}
            var Q305;
            {var subQ0=sQuery(id+"F0.wireOp",EDGE,"E40");var subQ1=sQuery(id+"F0.wireOp",EDGE,"E9");var subQ2=makeQuery(id+"F0.imprint","INTERSECT",VERTEX,{"derivedFrom":[subQ1,subQ0]});Q305=makeQuery(id+"F0.imprint","IMPRINT",FACE,{"disambiguationData":[TD([[makeQuery(id+"F0.imprint","IMPRINT",EDGE,{"disambiguationData":[TD([[subQ2,-1.0]])],"derivedFrom":subQ1}),1.0]])]});}
            var Q306;
            {var subQ0=sQuery(id+"F0.wireOp",EDGE,"E11");var subQ1=sQuery(id+"F0.wireOp",EDGE,"E1");var subQ2=makeQuery(id+"F0.imprint","INTERSECT",VERTEX,{"derivedFrom":[subQ1,subQ0]});Q306=makeQuery(id+"F0.imprint","IMPRINT",FACE,{"disambiguationData":[TD([[makeQuery(id+"F0.imprint","IMPRINT",EDGE,{"disambiguationData":[TD([[subQ2,-1.0]])],"derivedFrom":subQ1}),-1.0]])]});}
            var Q307;
            {var subQ5=sQuery(id+"F0.wireOp",EDGE,"E1");var subQ7=sQuery(id+"F0.wireOp",EDGE,"E19");var subQ9=makeQuery(id+"F0.imprint","INTERSECT",VERTEX,{"derivedFrom":[subQ5,subQ7]});Q307=makeQuery(id+"F0.imprint","IMPRINT",FACE,{"disambiguationData":[TD([[makeQuery(id+"F0.imprint","IMPRINT",EDGE,{"disambiguationData":[TD([[subQ9,-1.0]])],"derivedFrom":subQ5}),1.0]])]});}
            var Q308;
            {var subQ0=sQuery(id+"F0.wireOp",EDGE,"E11");var subQ1=sQuery(id+"F0.wireOp",EDGE,"E8");var subQ2=makeQuery(id+"F0.imprint","INTERSECT",VERTEX,{"derivedFrom":[subQ1,subQ0]});Q308=makeQuery(id+"F0.imprint","IMPRINT",FACE,{"disambiguationData":[TD([[makeQuery(id+"F0.imprint","IMPRINT",EDGE,{"disambiguationData":[TD([[subQ2,-1.0]])],"derivedFrom":subQ1}),1.0]])]});}
            var Q309;
            {var subQ0=sQuery(id+"F0.wireOp",EDGE,"E34");var subQ1=sQuery(id+"F0.wireOp",EDGE,"E10");var subQ2=makeQuery(id+"F0.imprint","INTERSECT",VERTEX,{"derivedFrom":[subQ1,subQ0]});Q309=makeQuery(id+"F0.imprint","IMPRINT",FACE,{"disambiguationData":[TD([[makeQuery(id+"F0.imprint","IMPRINT",EDGE,{"disambiguationData":[TD([[subQ2,-1.0]])],"derivedFrom":subQ1}),1.0]])]});}
            var Q310;
            {var subQ0=sQuery(id+"F0.wireOp",EDGE,"E52");var subQ1=sQuery(id+"F0.wireOp",EDGE,"E32");var subQ2=makeQuery(id+"F0.imprint","INTERSECT",VERTEX,{"derivedFrom":[subQ1,subQ0]});Q310=makeQuery(id+"F0.imprint","IMPRINT",FACE,{"disambiguationData":[TD([[makeQuery(id+"F0.imprint","IMPRINT",EDGE,{"disambiguationData":[TD([[subQ2,-1.0]])],"derivedFrom":subQ1}),-1.0]])]});}
            var Q311;
            {var subQ0=sQuery(id+"F0.wireOp",EDGE,"E57");var subQ1=sQuery(id+"F0.wireOp",EDGE,"E47");var subQ2=makeQuery(id+"F0.imprint","INTERSECT",VERTEX,{"derivedFrom":[subQ1,subQ0]});Q311=makeQuery(id+"F0.imprint","IMPRINT",FACE,{"disambiguationData":[TD([[makeQuery(id+"F0.imprint","IMPRINT",EDGE,{"disambiguationData":[TD([[subQ2,-1.0]])],"derivedFrom":subQ1}),-1.0]])]});}
            var Q312;
            {var subQ0=sQuery(id+"F0.wireOp",EDGE,"E36");var subQ1=sQuery(id+"F0.wireOp",EDGE,"E10");var subQ2=makeQuery(id+"F0.imprint","INTERSECT",VERTEX,{"derivedFrom":[subQ1,subQ0]});Q312=makeQuery(id+"F0.imprint","IMPRINT",FACE,{"disambiguationData":[TD([[makeQuery(id+"F0.imprint","IMPRINT",EDGE,{"disambiguationData":[TD([[subQ2,-1.0]])],"derivedFrom":subQ1}),1.0]])]});}
            var Q313;
            {var subQ5=sQuery(id+"F0.wireOp",EDGE,"E1");var subQ7=sQuery(id+"F0.wireOp",EDGE,"E12");var subQ8=makeQuery(id+"F0.imprint","INTERSECT",VERTEX,{"derivedFrom":[subQ5,subQ7]});Q313=makeQuery(id+"F0.imprint","IMPRINT",FACE,{"disambiguationData":[TD([[makeQuery(id+"F0.imprint","IMPRINT",EDGE,{"disambiguationData":[TD([[subQ8,-1.0]])],"derivedFrom":subQ5}),-1.0]])]});}
            var Q314;
            {var subQ0=sQuery(id+"F0.wireOp",EDGE,"E38");var subQ1=sQuery(id+"F0.wireOp",EDGE,"E9");var subQ2=makeQuery(id+"F0.imprint","INTERSECT",VERTEX,{"derivedFrom":[subQ1,subQ0]});Q314=makeQuery(id+"F0.imprint","IMPRINT",FACE,{"disambiguationData":[TD([[makeQuery(id+"F0.imprint","IMPRINT",EDGE,{"disambiguationData":[TD([[subQ2,-1.0]])],"derivedFrom":subQ1}),1.0]])]});}
            var Q315;
            {var subQ1=sQuery(id+"F0.wireOp",EDGE,"E32");var subQ7=sQuery(id+"F0.wireOp",EDGE,"E55");var subQ9=makeQuery(id+"F0.imprint","INTERSECT",VERTEX,{"derivedFrom":[subQ1,subQ7]});Q315=makeQuery(id+"F0.imprint","IMPRINT",FACE,{"disambiguationData":[TD([[makeQuery(id+"F0.imprint","IMPRINT",EDGE,{"disambiguationData":[TD([[subQ9,-1.0]])],"derivedFrom":subQ1}),-1.0]])]});}
            var Q316;
            {var subQ6=sQuery(id+"F0.wireOp",EDGE,"E6");var subQ9=sQuery(id+"F0.wireOp",EDGE,"E39");var subQ11=makeQuery(id+"F0.imprint","INTERSECT",VERTEX,{"derivedFrom":[subQ6,subQ9]});Q316=makeQuery(id+"F0.imprint","IMPRINT",FACE,{"disambiguationData":[TD([[makeQuery(id+"F0.imprint","IMPRINT",EDGE,{"disambiguationData":[TD([[subQ11,-1.0]])],"derivedFrom":subQ6}),1.0]])]});}
            var Q317;
            {var subQ0=sQuery(id+"F0.wireOp",EDGE,"E7");var subQ1=sQuery(id+"F0.wireOp",EDGE,"E1");var subQ2=makeQuery(id+"F0.imprint","INTERSECT",VERTEX,{"derivedFrom":[subQ1,subQ0]});Q317=makeQuery(id+"F0.imprint","IMPRINT",FACE,{"disambiguationData":[TD([[makeQuery(id+"F0.imprint","IMPRINT",EDGE,{"disambiguationData":[TD([[subQ2,-1.0]])],"derivedFrom":subQ1}),1.0]])]});}
            var Q318;
            {var subQ0=sQuery(id+"F0.wireOp",EDGE,"E42");var subQ1=sQuery(id+"F0.wireOp",EDGE,"E3");var subQ2=makeQuery(id+"F0.imprint","INTERSECT",VERTEX,{"derivedFrom":[subQ1,subQ0]});Q318=makeQuery(id+"F0.imprint","IMPRINT",FACE,{"disambiguationData":[TD([[makeQuery(id+"F0.imprint","IMPRINT",EDGE,{"disambiguationData":[TD([[subQ2,-1.0]])],"derivedFrom":subQ1}),1.0]])]});}
            var Q319;
            {var subQ0=sQuery(id+"F0.wireOp",EDGE,"E11");var subQ1=sQuery(id+"F0.wireOp",EDGE,"E1");var subQ2=makeQuery(id+"F0.imprint","INTERSECT",VERTEX,{"derivedFrom":[subQ1,subQ0]});Q319=makeQuery(id+"F0.imprint","IMPRINT",FACE,{"disambiguationData":[TD([[makeQuery(id+"F0.imprint","IMPRINT",EDGE,{"disambiguationData":[TD([[subQ2,-1.0]])],"derivedFrom":subQ1}),1.0]])]});}
            var Q320;
            {var subQ0=sQuery(id+"F0.wireOp",EDGE,"E19");var subQ1=sQuery(id+"F0.wireOp",EDGE,"E17");var subQ2=makeQuery(id+"F0.imprint","INTERSECT",VERTEX,{"derivedFrom":[subQ1,subQ0]});Q320=makeQuery(id+"F0.imprint","IMPRINT",FACE,{"disambiguationData":[TD([[makeQuery(id+"F0.imprint","IMPRINT",EDGE,{"disambiguationData":[TD([[subQ2,-1.0]])],"derivedFrom":subQ1}),-1.0]])]});}
            var Q321;
            {var subQ0=sQuery(id+"F0.wireOp",EDGE,"E41");var subQ1=sQuery(id+"F0.wireOp",EDGE,"E5");var subQ2=makeQuery(id+"F0.imprint","INTERSECT",VERTEX,{"derivedFrom":[subQ1,subQ0]});Q321=makeQuery(id+"F0.imprint","IMPRINT",FACE,{"disambiguationData":[TD([[makeQuery(id+"F0.imprint","IMPRINT",EDGE,{"disambiguationData":[TD([[subQ2,-1.0]])],"derivedFrom":subQ1}),1.0]])]});}
            var Q322;
            {var subQ0=sQuery(id+"F0.wireOp",EDGE,"E20");var subQ1=sQuery(id+"F0.wireOp",EDGE,"E4");var subQ2=makeQuery(id+"F0.imprint","INTERSECT",VERTEX,{"derivedFrom":[subQ1,subQ0]});Q322=makeQuery(id+"F0.imprint","IMPRINT",FACE,{"disambiguationData":[TD([[makeQuery(id+"F0.imprint","IMPRINT",EDGE,{"disambiguationData":[TD([[subQ2,-1.0]])],"derivedFrom":subQ1}),1.0]])]});}
            var Q323;
            {var subQ0=sQuery(id+"F0.wireOp",EDGE,"E37");var subQ1=sQuery(id+"F0.wireOp",EDGE,"E9");var subQ2=makeQuery(id+"F0.imprint","INTERSECT",VERTEX,{"derivedFrom":[subQ1,subQ0]});Q323=makeQuery(id+"F0.imprint","IMPRINT",FACE,{"disambiguationData":[TD([[makeQuery(id+"F0.imprint","IMPRINT",EDGE,{"disambiguationData":[TD([[subQ2,-1.0]])],"derivedFrom":subQ1}),1.0]])]});}
            var Q324;
            {var subQ1=sQuery(id+"F0.wireOp",EDGE,"E7");var subQ5=sQuery(id+"F0.wireOp",EDGE,"E43");var subQ6=makeQuery(id+"F0.imprint","INTERSECT",VERTEX,{"derivedFrom":[subQ1,subQ5]});Q324=makeQuery(id+"F0.imprint","IMPRINT",FACE,{"disambiguationData":[TD([[makeQuery(id+"F0.imprint","IMPRINT",EDGE,{"disambiguationData":[TD([[subQ6,-1.0]])],"derivedFrom":subQ1}),1.0]])]});}
            var Q325;
            {var subQ0=sQuery(id+"F0.wireOp",EDGE,"E34");var subQ1=sQuery(id+"F0.wireOp",EDGE,"E31");var subQ2=makeQuery(id+"F0.imprint","INTERSECT",VERTEX,{"derivedFrom":[subQ1,subQ0]});Q325=makeQuery(id+"F0.imprint","IMPRINT",FACE,{"disambiguationData":[TD([[makeQuery(id+"F0.imprint","IMPRINT",EDGE,{"disambiguationData":[TD([[subQ2,-1.0]])],"derivedFrom":subQ1}),-1.0]])]});}
            var Q326;
            {var subQ0=sQuery(id+"F0.wireOp",EDGE,"E10");var subQ1=sQuery(id+"F0.wireOp",EDGE,"E1");var subQ2=makeQuery(id+"F0.imprint","INTERSECT",VERTEX,{"derivedFrom":[subQ1,subQ0]});Q326=makeQuery(id+"F0.imprint","IMPRINT",FACE,{"disambiguationData":[TD([[makeQuery(id+"F0.imprint","IMPRINT",EDGE,{"disambiguationData":[TD([[subQ2,-1.0]])],"derivedFrom":subQ1}),-1.0]])]});}
            var Q327;
            {var subQ0=sQuery(id+"F0.wireOp",EDGE,"E36");var subQ1=sQuery(id+"F0.wireOp",EDGE,"E30");var subQ2=makeQuery(id+"F0.imprint","INTERSECT",VERTEX,{"derivedFrom":[subQ1,subQ0]});Q327=makeQuery(id+"F0.imprint","IMPRINT",FACE,{"disambiguationData":[TD([[makeQuery(id+"F0.imprint","IMPRINT",EDGE,{"disambiguationData":[TD([[subQ2,-1.0]])],"derivedFrom":subQ1}),-1.0]])]});}
            var Q328;
            {var subQ0=sQuery(id+"F0.wireOp",EDGE,"E36");var subQ1=sQuery(id+"F0.wireOp",EDGE,"E31");var subQ2=makeQuery(id+"F0.imprint","INTERSECT",VERTEX,{"derivedFrom":[subQ1,subQ0]});Q328=makeQuery(id+"F0.imprint","IMPRINT",FACE,{"disambiguationData":[TD([[makeQuery(id+"F0.imprint","IMPRINT",EDGE,{"disambiguationData":[TD([[subQ2,-1.0]])],"derivedFrom":subQ1}),-1.0]])]});}
            var Q329;
            {var subQ0=sQuery(id+"F0.wireOp",EDGE,"E18");var subQ1=sQuery(id+"F0.wireOp",EDGE,"E9");var subQ2=makeQuery(id+"F0.imprint","INTERSECT",VERTEX,{"derivedFrom":[subQ1,subQ0]});Q329=makeQuery(id+"F0.imprint","IMPRINT",FACE,{"disambiguationData":[TD([[makeQuery(id+"F0.imprint","IMPRINT",EDGE,{"disambiguationData":[TD([[subQ2,-1.0]])],"derivedFrom":subQ1}),-1.0]])]});}
            var Q330;
            {var subQ0=sQuery(id+"F0.wireOp",EDGE,"E15");var subQ1=sQuery(id+"F0.wireOp",EDGE,"E10");var subQ2=makeQuery(id+"F0.imprint","INTERSECT",VERTEX,{"derivedFrom":[subQ1,subQ0]});Q330=makeQuery(id+"F0.imprint","IMPRINT",FACE,{"disambiguationData":[TD([[makeQuery(id+"F0.imprint","IMPRINT",EDGE,{"disambiguationData":[TD([[subQ2,-1.0]])],"derivedFrom":subQ1}),-1.0]])]});}
            var Q331;
            {var subQ3=sQuery(id+"F0.wireOp",EDGE,"E18");var subQ7=sQuery(id+"F0.wireOp",EDGE,"E8");var subQ9=makeQuery(id+"F0.imprint","INTERSECT",VERTEX,{"derivedFrom":[subQ7,subQ3]});Q331=makeQuery(id+"F0.imprint","IMPRINT",FACE,{"disambiguationData":[TD([[makeQuery(id+"F0.imprint","IMPRINT",EDGE,{"disambiguationData":[TD([[subQ9,-1.0]])],"derivedFrom":subQ7}),-1.0]])]});}
            var Q332;
            {var subQ7=sQuery(id+"F0.wireOp",EDGE,"E58");var subQ9=sQuery(id+"F0.wireOp",EDGE,"E30");var subQ11=makeQuery(id+"F0.imprint","INTERSECT",VERTEX,{"derivedFrom":[subQ9,subQ7]});Q332=makeQuery(id+"F0.imprint","IMPRINT",FACE,{"disambiguationData":[TD([[makeQuery(id+"F0.imprint","IMPRINT",EDGE,{"disambiguationData":[TD([[subQ11,-1.0]])],"derivedFrom":subQ9}),-1.0]])]});}
            var Q333;
            {var subQ0=sQuery(id+"F0.wireOp",EDGE,"E43");var subQ1=sQuery(id+"F0.wireOp",EDGE,"E9");var subQ2=makeQuery(id+"F0.imprint","INTERSECT",VERTEX,{"derivedFrom":[subQ1,subQ0]});Q333=makeQuery(id+"F0.imprint","IMPRINT",FACE,{"disambiguationData":[TD([[makeQuery(id+"F0.imprint","IMPRINT",EDGE,{"disambiguationData":[TD([[subQ2,-1.0]])],"derivedFrom":subQ1}),-1.0]])]});}
            var Q334;
            {var subQ0=sQuery(id+"F0.wireOp",EDGE,"E8");var subQ1=sQuery(id+"F0.wireOp",EDGE,"E4");var subQ2=makeQuery(id+"F0.imprint","INTERSECT",VERTEX,{"derivedFrom":[subQ1,subQ0]});Q334=makeQuery(id+"F0.imprint","IMPRINT",FACE,{"disambiguationData":[TD([[makeQuery(id+"F0.imprint","IMPRINT",EDGE,{"disambiguationData":[TD([[subQ2,-1.0]])],"derivedFrom":subQ1}),1.0]])]});}
            var Q335;
            {var subQ0=sQuery(id+"F0.wireOp",EDGE,"E8");var subQ1=sQuery(id+"F0.wireOp",EDGE,"E2");var subQ2=makeQuery(id+"F0.imprint","INTERSECT",VERTEX,{"derivedFrom":[subQ1,subQ0]});Q335=makeQuery(id+"F0.imprint","IMPRINT",FACE,{"disambiguationData":[TD([[makeQuery(id+"F0.imprint","IMPRINT",EDGE,{"disambiguationData":[TD([[subQ2,-1.0]])],"derivedFrom":subQ1}),1.0]])]});}
            var Q336;
            {var subQ0=sQuery(id+"F0.wireOp",EDGE,"E53");var subQ1=sQuery(id+"F0.wireOp",EDGE,"E47");var subQ2=makeQuery(id+"F0.imprint","INTERSECT",VERTEX,{"derivedFrom":[subQ1,subQ0]});Q336=makeQuery(id+"F0.imprint","IMPRINT",FACE,{"disambiguationData":[TD([[makeQuery(id+"F0.imprint","IMPRINT",EDGE,{"disambiguationData":[TD([[subQ2,-1.0]])],"derivedFrom":subQ1}),-1.0]])]});}
            var Q337;
            {var subQ0=sQuery(id+"F0.wireOp",EDGE,"E38");var subQ1=sQuery(id+"F0.wireOp",EDGE,"E31");var subQ2=makeQuery(id+"F0.imprint","INTERSECT",VERTEX,{"derivedFrom":[subQ1,subQ0]});Q337=makeQuery(id+"F0.imprint","IMPRINT",FACE,{"disambiguationData":[TD([[makeQuery(id+"F0.imprint","IMPRINT",EDGE,{"disambiguationData":[TD([[subQ2,-1.0]])],"derivedFrom":subQ1}),-1.0]])]});}
            var Q338;
            {var subQ3=sQuery(id+"F0.wireOp",EDGE,"E39");var subQ5=sQuery(id+"F0.wireOp",EDGE,"E2");var subQ6=makeQuery(id+"F0.imprint","INTERSECT",VERTEX,{"derivedFrom":[subQ5,subQ3]});Q338=makeQuery(id+"F0.imprint","IMPRINT",FACE,{"disambiguationData":[TD([[makeQuery(id+"F0.imprint","IMPRINT",EDGE,{"disambiguationData":[TD([[subQ6,-1.0]])],"derivedFrom":subQ5}),1.0]])]});}
            var Q339;
            {var subQ5=sQuery(id+"F0.wireOp",EDGE,"E2");var subQ7=sQuery(id+"F0.wireOp",EDGE,"E20");var subQ8=makeQuery(id+"F0.imprint","INTERSECT",VERTEX,{"derivedFrom":[subQ5,subQ7]});Q339=makeQuery(id+"F0.imprint","IMPRINT",FACE,{"disambiguationData":[TD([[makeQuery(id+"F0.imprint","IMPRINT",EDGE,{"disambiguationData":[TD([[subQ8,-1.0]])],"derivedFrom":subQ5}),-1.0]])]});}
            var Q340;
            {var subQ0=sQuery(id+"F0.wireOp",EDGE,"E24");var subQ1=sQuery(id+"F0.wireOp",EDGE,"E19");var subQ2=makeQuery(id+"F0.imprint","INTERSECT",VERTEX,{"derivedFrom":[subQ1,subQ0]});Q340=makeQuery(id+"F0.imprint","IMPRINT",FACE,{"disambiguationData":[TD([[makeQuery(id+"F0.imprint","IMPRINT",EDGE,{"disambiguationData":[TD([[subQ2,-1.0]])],"derivedFrom":subQ1}),-1.0]])]});}
            var Q341;
            {var subQ0=sQuery(id+"F0.wireOp",EDGE,"E15");var subQ1=sQuery(id+"F0.wireOp",EDGE,"E2");var subQ2=makeQuery(id+"F0.imprint","INTERSECT",VERTEX,{"derivedFrom":[subQ1,subQ0]});Q341=makeQuery(id+"F0.imprint","IMPRINT",FACE,{"disambiguationData":[TD([[makeQuery(id+"F0.imprint","IMPRINT",EDGE,{"disambiguationData":[TD([[subQ2,-1.0]])],"derivedFrom":subQ1}),-1.0]])]});}
            var Q342;
            {var subQ0=sQuery(id+"F0.wireOp",EDGE,"E53");var subQ1=sQuery(id+"F0.wireOp",EDGE,"E29");var subQ2=makeQuery(id+"F0.imprint","INTERSECT",VERTEX,{"derivedFrom":[subQ1,subQ0]});Q342=makeQuery(id+"F0.imprint","IMPRINT",FACE,{"disambiguationData":[TD([[makeQuery(id+"F0.imprint","IMPRINT",EDGE,{"disambiguationData":[TD([[subQ2,-1.0]])],"derivedFrom":subQ1}),-1.0]])]});}
            var Q343;
            {var subQ0=sQuery(id+"F0.wireOp",EDGE,"E10");var subQ1=sQuery(id+"F0.wireOp",EDGE,"E4");var subQ2=makeQuery(id+"F0.imprint","INTERSECT",VERTEX,{"derivedFrom":[subQ1,subQ0]});Q343=makeQuery(id+"F0.imprint","IMPRINT",FACE,{"disambiguationData":[TD([[makeQuery(id+"F0.imprint","IMPRINT",EDGE,{"disambiguationData":[TD([[subQ2,-1.0]])],"derivedFrom":subQ1}),1.0]])]});}
            var Q344;
            {var subQ0=sQuery(id+"F0.wireOp",EDGE,"E18");var subQ1=sQuery(id+"F0.wireOp",EDGE,"E4");var subQ2=makeQuery(id+"F0.imprint","INTERSECT",VERTEX,{"derivedFrom":[subQ1,subQ0]});Q344=makeQuery(id+"F0.imprint","IMPRINT",FACE,{"disambiguationData":[TD([[makeQuery(id+"F0.imprint","IMPRINT",EDGE,{"disambiguationData":[TD([[subQ2,-1.0]])],"derivedFrom":subQ1}),-1.0]])]});}
            var Q345;
            {var subQ0=sQuery(id+"F0.wireOp",EDGE,"E6");var subQ1=sQuery(id+"F0.wireOp",EDGE,"E2");var subQ2=makeQuery(id+"F0.imprint","INTERSECT",VERTEX,{"derivedFrom":[subQ1,subQ0]});Q345=makeQuery(id+"F0.imprint","IMPRINT",FACE,{"disambiguationData":[TD([[makeQuery(id+"F0.imprint","IMPRINT",EDGE,{"disambiguationData":[TD([[subQ2,-1.0]])],"derivedFrom":subQ1}),1.0]])]});}
            var Q346;
            {var subQ0=sQuery(id+"F0.wireOp",EDGE,"E22");var subQ1=sQuery(id+"F0.wireOp",EDGE,"E19");var subQ2=makeQuery(id+"F0.imprint","INTERSECT",VERTEX,{"derivedFrom":[subQ1,subQ0]});Q346=makeQuery(id+"F0.imprint","IMPRINT",FACE,{"disambiguationData":[TD([[makeQuery(id+"F0.imprint","IMPRINT",EDGE,{"disambiguationData":[TD([[subQ2,-1.0]])],"derivedFrom":subQ1}),-1.0]])]});}
            var Q347;
            {var subQ0=sQuery(id+"F0.wireOp",EDGE,"E39");var subQ1=sQuery(id+"F0.wireOp",EDGE,"E3");var subQ2=makeQuery(id+"F0.imprint","INTERSECT",VERTEX,{"derivedFrom":[subQ1,subQ0]});Q347=makeQuery(id+"F0.imprint","IMPRINT",FACE,{"disambiguationData":[TD([[makeQuery(id+"F0.imprint","IMPRINT",EDGE,{"disambiguationData":[TD([[subQ2,-1.0]])],"derivedFrom":subQ1}),1.0]])]});}
            var Q348;
            {var subQ0=sQuery(id+"F0.wireOp",EDGE,"E35");var subQ1=sQuery(id+"F0.wireOp",EDGE,"E9");var subQ2=makeQuery(id+"F0.imprint","INTERSECT",VERTEX,{"derivedFrom":[subQ1,subQ0]});Q348=makeQuery(id+"F0.imprint","IMPRINT",FACE,{"disambiguationData":[TD([[makeQuery(id+"F0.imprint","IMPRINT",EDGE,{"disambiguationData":[TD([[subQ2,-1.0]])],"derivedFrom":subQ1}),-1.0]])]});}
            var Q349;
            {var subQ0=sQuery(id+"F0.wireOp",EDGE,"E20");var subQ1=sQuery(id+"F0.wireOp",EDGE,"E19");var subQ2=makeQuery(id+"F0.imprint","INTERSECT",VERTEX,{"derivedFrom":[subQ1,subQ0]});Q349=makeQuery(id+"F0.imprint","IMPRINT",FACE,{"disambiguationData":[TD([[makeQuery(id+"F0.imprint","IMPRINT",EDGE,{"disambiguationData":[TD([[subQ2,-1.0]])],"derivedFrom":subQ1}),-1.0]])]});}
            var Q350;
            {var subQ0=sQuery(id+"F0.wireOp",EDGE,"E40");var subQ1=sQuery(id+"F0.wireOp",EDGE,"E2");var subQ2=makeQuery(id+"F0.imprint","INTERSECT",VERTEX,{"derivedFrom":[subQ1,subQ0]});Q350=makeQuery(id+"F0.imprint","IMPRINT",FACE,{"disambiguationData":[TD([[makeQuery(id+"F0.imprint","IMPRINT",EDGE,{"disambiguationData":[TD([[subQ2,-1.0]])],"derivedFrom":subQ1}),1.0]])]});}
            var Q351;
            {var subQ3=sQuery(id+"F0.wireOp",EDGE,"E34");var subQ7=sQuery(id+"F0.wireOp",EDGE,"E11");var subQ8=makeQuery(id+"F0.imprint","INTERSECT",VERTEX,{"derivedFrom":[subQ7,subQ3]});Q351=makeQuery(id+"F0.imprint","IMPRINT",FACE,{"disambiguationData":[TD([[makeQuery(id+"F0.imprint","IMPRINT",EDGE,{"disambiguationData":[TD([[subQ8,-1.0]])],"derivedFrom":subQ7}),1.0]])]});}
            var Q352;
            {var subQ0=sQuery(id+"F0.wireOp",EDGE,"E37");var subQ1=sQuery(id+"F0.wireOp",EDGE,"E9");var subQ2=makeQuery(id+"F0.imprint","INTERSECT",VERTEX,{"derivedFrom":[subQ1,subQ0]});Q352=makeQuery(id+"F0.imprint","IMPRINT",FACE,{"disambiguationData":[TD([[makeQuery(id+"F0.imprint","IMPRINT",EDGE,{"disambiguationData":[TD([[subQ2,-1.0]])],"derivedFrom":subQ1}),-1.0]])]});}
            var Q353;
            {var subQ0=sQuery(id+"F0.wireOp",EDGE,"E15");var subQ1=sQuery(id+"F0.wireOp",EDGE,"E2");var subQ2=makeQuery(id+"F0.imprint","INTERSECT",VERTEX,{"derivedFrom":[subQ1,subQ0]});Q353=makeQuery(id+"F0.imprint","IMPRINT",FACE,{"disambiguationData":[TD([[makeQuery(id+"F0.imprint","IMPRINT",EDGE,{"disambiguationData":[TD([[subQ2,-1.0]])],"derivedFrom":subQ1}),1.0]])]});}
            var Q354;
            {var subQ0=sQuery(id+"F0.wireOp",EDGE,"E37");var subQ1=sQuery(id+"F0.wireOp",EDGE,"E31");var subQ2=makeQuery(id+"F0.imprint","INTERSECT",VERTEX,{"derivedFrom":[subQ1,subQ0]});Q354=makeQuery(id+"F0.imprint","IMPRINT",FACE,{"disambiguationData":[TD([[makeQuery(id+"F0.imprint","IMPRINT",EDGE,{"disambiguationData":[TD([[subQ2,-1.0]])],"derivedFrom":subQ1}),-1.0]])]});}
            var Q355;
            {var subQ0=sQuery(id+"F0.wireOp",EDGE,"E37");var subQ1=sQuery(id+"F0.wireOp",EDGE,"E4");var subQ2=makeQuery(id+"F0.imprint","INTERSECT",VERTEX,{"derivedFrom":[subQ1,subQ0]});Q355=makeQuery(id+"F0.imprint","IMPRINT",FACE,{"disambiguationData":[TD([[makeQuery(id+"F0.imprint","IMPRINT",EDGE,{"disambiguationData":[TD([[subQ2,-1.0]])],"derivedFrom":subQ1}),1.0]])]});}
            var Q356;
            {var subQ0=sQuery(id+"F0.wireOp",EDGE,"E17");var subQ1=sQuery(id+"F0.wireOp",EDGE,"E9");var subQ2=makeQuery(id+"F0.imprint","INTERSECT",VERTEX,{"derivedFrom":[subQ1,subQ0]});Q356=makeQuery(id+"F0.imprint","IMPRINT",FACE,{"disambiguationData":[TD([[makeQuery(id+"F0.imprint","IMPRINT",EDGE,{"disambiguationData":[TD([[subQ2,-1.0]])],"derivedFrom":subQ1}),-1.0]])]});}
            var Q357;
            {var subQ0=sQuery(id+"F0.wireOp",EDGE,"E24");var subQ1=sQuery(id+"F0.wireOp",EDGE,"E23");var subQ2=makeQuery(id+"F0.imprint","INTERSECT",VERTEX,{"derivedFrom":[subQ1,subQ0]});Q357=makeQuery(id+"F0.imprint","IMPRINT",FACE,{"disambiguationData":[TD([[makeQuery(id+"F0.imprint","IMPRINT",EDGE,{"disambiguationData":[TD([[subQ2,-1.0]])],"derivedFrom":subQ1}),-1.0]])]});}
            var Q358;
            {var subQ0=sQuery(id+"F0.wireOp",EDGE,"E39");var subQ1=sQuery(id+"F0.wireOp",EDGE,"E33");var subQ2=makeQuery(id+"F0.imprint","INTERSECT",VERTEX,{"derivedFrom":[subQ1,subQ0]});Q358=makeQuery(id+"F0.imprint","IMPRINT",FACE,{"disambiguationData":[TD([[makeQuery(id+"F0.imprint","IMPRINT",EDGE,{"disambiguationData":[TD([[subQ2,-1.0]])],"derivedFrom":subQ1}),-1.0]])]});}
            var Q359;
            {var subQ1=sQuery(id+"F0.wireOp",EDGE,"E13");var subQ5=sQuery(id+"F0.wireOp",EDGE,"E4");var subQ6=makeQuery(id+"F0.imprint","INTERSECT",VERTEX,{"derivedFrom":[subQ5,subQ1]});Q359=makeQuery(id+"F0.imprint","IMPRINT",FACE,{"disambiguationData":[TD([[makeQuery(id+"F0.imprint","IMPRINT",EDGE,{"disambiguationData":[TD([[subQ6,-1.0]])],"derivedFrom":subQ5}),-1.0]])]});}
            var Q360;
            {var subQ0=sQuery(id+"F0.wireOp",EDGE,"E40");var subQ1=sQuery(id+"F0.wireOp",EDGE,"E14");var subQ2=makeQuery(id+"F0.imprint","INTERSECT",VERTEX,{"derivedFrom":[subQ1,subQ0]});Q360=makeQuery(id+"F0.imprint","IMPRINT",FACE,{"disambiguationData":[TD([[makeQuery(id+"F0.imprint","IMPRINT",EDGE,{"disambiguationData":[TD([[subQ2,-1.0]])],"derivedFrom":subQ1}),1.0]])]});}
            var Q361;
            {var subQ0=sQuery(id+"F0.wireOp",EDGE,"E34");var subQ1=sQuery(id+"F0.wireOp",EDGE,"E33");var subQ2=makeQuery(id+"F0.imprint","INTERSECT",VERTEX,{"derivedFrom":[subQ1,subQ0]});Q361=makeQuery(id+"F0.imprint","IMPRINT",FACE,{"disambiguationData":[TD([[makeQuery(id+"F0.imprint","IMPRINT",EDGE,{"disambiguationData":[TD([[subQ2,-1.0]])],"derivedFrom":subQ1}),-1.0]])]});}
            var Q362;
            {var subQ0=sQuery(id+"F0.wireOp",EDGE,"E12");var subQ1=sQuery(id+"F0.wireOp",EDGE,"E5");var subQ2=makeQuery(id+"F0.imprint","INTERSECT",VERTEX,{"derivedFrom":[subQ1,subQ0]});Q362=makeQuery(id+"F0.imprint","IMPRINT",FACE,{"disambiguationData":[TD([[makeQuery(id+"F0.imprint","IMPRINT",EDGE,{"disambiguationData":[TD([[subQ2,-1.0]])],"derivedFrom":subQ1}),1.0]])]});}
            var Q363;
            {var subQ0=sQuery(id+"F0.wireOp",EDGE,"E21");var subQ1=sQuery(id+"F0.wireOp",EDGE,"E1");var subQ2=makeQuery(id+"F0.imprint","INTERSECT",VERTEX,{"derivedFrom":[subQ1,subQ0]});Q363=makeQuery(id+"F0.imprint","IMPRINT",FACE,{"disambiguationData":[TD([[makeQuery(id+"F0.imprint","IMPRINT",EDGE,{"disambiguationData":[TD([[subQ2,-1.0]])],"derivedFrom":subQ1}),-1.0]])]});}
            var Q364;
            {var subQ0=sQuery(id+"F0.wireOp",EDGE,"E56");var subQ1=sQuery(id+"F0.wireOp",EDGE,"E29");var subQ2=makeQuery(id+"F0.imprint","INTERSECT",VERTEX,{"derivedFrom":[subQ1,subQ0]});Q364=makeQuery(id+"F0.imprint","IMPRINT",FACE,{"disambiguationData":[TD([[makeQuery(id+"F0.imprint","IMPRINT",EDGE,{"disambiguationData":[TD([[subQ2,-1.0]])],"derivedFrom":subQ1}),1.0]])]});}
            var Q365;
            {var subQ0=sQuery(id+"F0.wireOp",EDGE,"E15");var subQ1=sQuery(id+"F0.wireOp",EDGE,"E9");var subQ2=makeQuery(id+"F0.imprint","INTERSECT",VERTEX,{"derivedFrom":[subQ1,subQ0]});Q365=makeQuery(id+"F0.imprint","IMPRINT",FACE,{"disambiguationData":[TD([[makeQuery(id+"F0.imprint","IMPRINT",EDGE,{"disambiguationData":[TD([[subQ2,-1.0]])],"derivedFrom":subQ1}),-1.0]])]});}
            var Q366;
            {var subQ0=sQuery(id+"F0.wireOp",EDGE,"E37");var subQ1=sQuery(id+"F0.wireOp",EDGE,"E13");var subQ2=makeQuery(id+"F0.imprint","INTERSECT",VERTEX,{"derivedFrom":[subQ1,subQ0]});Q366=makeQuery(id+"F0.imprint","IMPRINT",FACE,{"disambiguationData":[TD([[makeQuery(id+"F0.imprint","IMPRINT",EDGE,{"disambiguationData":[TD([[subQ2,-1.0]])],"derivedFrom":subQ1}),-1.0]])]});}
            var Q367;
            {var subQ0=sQuery(id+"F0.wireOp",EDGE,"E35");var subQ1=sQuery(id+"F0.wireOp",EDGE,"E33");var subQ2=makeQuery(id+"F0.imprint","INTERSECT",VERTEX,{"derivedFrom":[subQ1,subQ0]});Q367=makeQuery(id+"F0.imprint","IMPRINT",FACE,{"disambiguationData":[TD([[makeQuery(id+"F0.imprint","IMPRINT",EDGE,{"disambiguationData":[TD([[subQ2,-1.0]])],"derivedFrom":subQ1}),-1.0]])]});}
            var Q368;
            {var subQ0=sQuery(id+"F0.wireOp",EDGE,"E50");var subQ1=sQuery(id+"F0.wireOp",EDGE,"E31");var subQ2=makeQuery(id+"F0.imprint","INTERSECT",VERTEX,{"derivedFrom":[subQ1,subQ0]});Q368=makeQuery(id+"F0.imprint","IMPRINT",FACE,{"disambiguationData":[TD([[makeQuery(id+"F0.imprint","IMPRINT",EDGE,{"disambiguationData":[TD([[subQ2,-1.0]])],"derivedFrom":subQ1}),-1.0]])]});}
            var Q369;
            {var subQ0=sQuery(id+"F0.wireOp",EDGE,"E54");var subQ1=sQuery(id+"F0.wireOp",EDGE,"E29");var subQ2=makeQuery(id+"F0.imprint","INTERSECT",VERTEX,{"derivedFrom":[subQ1,subQ0]});Q369=makeQuery(id+"F0.imprint","IMPRINT",FACE,{"disambiguationData":[TD([[makeQuery(id+"F0.imprint","IMPRINT",EDGE,{"disambiguationData":[TD([[subQ2,-1.0]])],"derivedFrom":subQ1}),-1.0]])]});}
            var Q370;
            {var subQ1=sQuery(id+"F0.wireOp",EDGE,"E7");var subQ9=sQuery(id+"F0.wireOp",EDGE,"E13");var subQ10=makeQuery(id+"F0.imprint","INTERSECT",VERTEX,{"derivedFrom":[subQ1,subQ9]});Q370=makeQuery(id+"F0.imprint","IMPRINT",FACE,{"disambiguationData":[TD([[makeQuery(id+"F0.imprint","IMPRINT",EDGE,{"disambiguationData":[TD([[subQ10,-1.0]])],"derivedFrom":subQ1}),-1.0]])]});}
            var Q371;
            {var subQ0=sQuery(id+"F0.wireOp",EDGE,"E39");var subQ1=sQuery(id+"F0.wireOp",EDGE,"E9");var subQ2=makeQuery(id+"F0.imprint","INTERSECT",VERTEX,{"derivedFrom":[subQ1,subQ0]});Q371=makeQuery(id+"F0.imprint","IMPRINT",FACE,{"disambiguationData":[TD([[makeQuery(id+"F0.imprint","IMPRINT",EDGE,{"disambiguationData":[TD([[subQ2,-1.0]])],"derivedFrom":subQ1}),1.0]])]});}
            var Q372;
            {var subQ0=sQuery(id+"F0.wireOp",EDGE,"E14");var subQ1=sQuery(id+"F0.wireOp",EDGE,"E2");var subQ2=makeQuery(id+"F0.imprint","INTERSECT",VERTEX,{"derivedFrom":[subQ1,subQ0]});Q372=makeQuery(id+"F0.imprint","IMPRINT",FACE,{"disambiguationData":[TD([[makeQuery(id+"F0.imprint","IMPRINT",EDGE,{"disambiguationData":[TD([[subQ2,-1.0]])],"derivedFrom":subQ1}),1.0]])]});}
            var Q373;
            {var subQ0=sQuery(id+"F0.wireOp",EDGE,"E34");var subQ1=sQuery(id+"F0.wireOp",EDGE,"E12");var subQ2=makeQuery(id+"F0.imprint","INTERSECT",VERTEX,{"derivedFrom":[subQ1,subQ0]});Q373=makeQuery(id+"F0.imprint","IMPRINT",FACE,{"disambiguationData":[TD([[makeQuery(id+"F0.imprint","IMPRINT",EDGE,{"disambiguationData":[TD([[subQ2,-1.0]])],"derivedFrom":subQ1}),-1.0]])]});}
            var Q374;
            {var subQ7=sQuery(id+"F0.wireOp",EDGE,"E7");var subQ9=sQuery(id+"F0.wireOp",EDGE,"E35");var subQ10=makeQuery(id+"F0.imprint","INTERSECT",VERTEX,{"derivedFrom":[subQ7,subQ9]});Q374=makeQuery(id+"F0.imprint","IMPRINT",FACE,{"disambiguationData":[TD([[makeQuery(id+"F0.imprint","IMPRINT",EDGE,{"disambiguationData":[TD([[subQ10,-1.0]])],"derivedFrom":subQ7}),1.0]])]});}
            var Q375;
            {var subQ3=sQuery(id+"F0.wireOp",EDGE,"E37");var subQ7=sQuery(id+"F0.wireOp",EDGE,"E33");var subQ8=makeQuery(id+"F0.imprint","INTERSECT",VERTEX,{"derivedFrom":[subQ7,subQ3]});Q375=makeQuery(id+"F0.imprint","IMPRINT",FACE,{"disambiguationData":[TD([[makeQuery(id+"F0.imprint","IMPRINT",EDGE,{"disambiguationData":[TD([[subQ8,-1.0]])],"derivedFrom":subQ7}),-1.0]])]});}
            var Q376;
            {var subQ0=sQuery(id+"F0.wireOp",EDGE,"E42");var subQ1=sQuery(id+"F0.wireOp",EDGE,"E11");var subQ2=makeQuery(id+"F0.imprint","INTERSECT",VERTEX,{"derivedFrom":[subQ1,subQ0]});Q376=makeQuery(id+"F0.imprint","IMPRINT",FACE,{"disambiguationData":[TD([[makeQuery(id+"F0.imprint","IMPRINT",EDGE,{"disambiguationData":[TD([[subQ2,-1.0]])],"derivedFrom":subQ1}),1.0]])]});}
            var Q377;
            {var subQ0=sQuery(id+"F0.wireOp",EDGE,"E52");var subQ1=sQuery(id+"F0.wireOp",EDGE,"E31");var subQ2=makeQuery(id+"F0.imprint","INTERSECT",VERTEX,{"derivedFrom":[subQ1,subQ0]});Q377=makeQuery(id+"F0.imprint","IMPRINT",FACE,{"disambiguationData":[TD([[makeQuery(id+"F0.imprint","IMPRINT",EDGE,{"disambiguationData":[TD([[subQ2,-1.0]])],"derivedFrom":subQ1}),-1.0]])]});}
            var Q378;
            {var subQ0=sQuery(id+"F0.wireOp",EDGE,"E6");var subQ1=sQuery(id+"F0.wireOp",EDGE,"E2");var subQ2=makeQuery(id+"F0.imprint","INTERSECT",VERTEX,{"derivedFrom":[subQ1,subQ0]});Q378=makeQuery(id+"F0.imprint","IMPRINT",FACE,{"disambiguationData":[TD([[makeQuery(id+"F0.imprint","IMPRINT",EDGE,{"disambiguationData":[TD([[subQ2,-1.0]])],"derivedFrom":subQ1}),-1.0]])]});}
            var Q379;
            {var subQ0=sQuery(id+"F0.wireOp",EDGE,"E36");var subQ1=sQuery(id+"F0.wireOp",EDGE,"E13");var subQ2=makeQuery(id+"F0.imprint","INTERSECT",VERTEX,{"derivedFrom":[subQ1,subQ0]});Q379=makeQuery(id+"F0.imprint","IMPRINT",FACE,{"disambiguationData":[TD([[makeQuery(id+"F0.imprint","IMPRINT",EDGE,{"disambiguationData":[TD([[subQ2,-1.0]])],"derivedFrom":subQ1}),-1.0]])]});}
            var Q380;
            {var subQ0=sQuery(id+"F0.wireOp",EDGE,"E50");var subQ1=sQuery(id+"F0.wireOp",EDGE,"E30");var subQ2=makeQuery(id+"F0.imprint","INTERSECT",VERTEX,{"derivedFrom":[subQ1,subQ0]});Q380=makeQuery(id+"F0.imprint","IMPRINT",FACE,{"disambiguationData":[TD([[makeQuery(id+"F0.imprint","IMPRINT",EDGE,{"disambiguationData":[TD([[subQ2,-1.0]])],"derivedFrom":subQ1}),-1.0]])]});}
            var Q381;
            {var subQ0=sQuery(id+"F0.wireOp",EDGE,"E35");var subQ1=sQuery(id+"F0.wireOp",EDGE,"E34");var subQ2=makeQuery(id+"F0.imprint","INTERSECT",VERTEX,{"derivedFrom":[subQ1,subQ0]});Q381=makeQuery(id+"F0.imprint","IMPRINT",FACE,{"disambiguationData":[TD([[makeQuery(id+"F0.imprint","IMPRINT",EDGE,{"disambiguationData":[TD([[subQ2,-1.0]])],"derivedFrom":subQ1}),-1.0]])]});}
            var Q382;
            {var subQ0=sQuery(id+"F0.wireOp",EDGE,"E16");var subQ1=sQuery(id+"F0.wireOp",EDGE,"E2");var subQ2=makeQuery(id+"F0.imprint","INTERSECT",VERTEX,{"derivedFrom":[subQ1,subQ0]});Q382=makeQuery(id+"F0.imprint","IMPRINT",FACE,{"disambiguationData":[TD([[makeQuery(id+"F0.imprint","IMPRINT",EDGE,{"disambiguationData":[TD([[subQ2,-1.0]])],"derivedFrom":subQ1}),-1.0]])]});}
            var Q383;
            {var subQ0=sQuery(id+"F0.wireOp",EDGE,"E41");var subQ1=sQuery(id+"F0.wireOp",EDGE,"E4");var subQ2=makeQuery(id+"F0.imprint","INTERSECT",VERTEX,{"derivedFrom":[subQ1,subQ0]});Q383=makeQuery(id+"F0.imprint","IMPRINT",FACE,{"disambiguationData":[TD([[makeQuery(id+"F0.imprint","IMPRINT",EDGE,{"disambiguationData":[TD([[subQ2,-1.0]])],"derivedFrom":subQ1}),1.0]])]});}
            var Q384;
            {var subQ0=sQuery(id+"F0.wireOp",EDGE,"E5");var subQ1=sQuery(id+"F0.wireOp",EDGE,"E3");var subQ2=makeQuery(id+"F0.imprint","INTERSECT",VERTEX,{"derivedFrom":[subQ1,subQ0]});Q384=makeQuery(id+"F0.imprint","IMPRINT",FACE,{"disambiguationData":[TD([[makeQuery(id+"F0.imprint","IMPRINT",EDGE,{"disambiguationData":[TD([[subQ2,-1.0]])],"derivedFrom":subQ1}),1.0]])]});}
            var Q385;
            {var subQ1=sQuery(id+"F0.wireOp",EDGE,"E7");var subQ7=sQuery(id+"F0.wireOp",EDGE,"E39");var subQ9=makeQuery(id+"F0.imprint","INTERSECT",VERTEX,{"derivedFrom":[subQ1,subQ7]});Q385=makeQuery(id+"F0.imprint","IMPRINT",FACE,{"disambiguationData":[TD([[makeQuery(id+"F0.imprint","IMPRINT",EDGE,{"disambiguationData":[TD([[subQ9,-1.0]])],"derivedFrom":subQ1}),1.0]])]});}
            var Q386;
            {var subQ0=sQuery(id+"F0.wireOp",EDGE,"E35");var subQ1=sQuery(id+"F0.wireOp",EDGE,"E32");var subQ2=makeQuery(id+"F0.imprint","INTERSECT",VERTEX,{"derivedFrom":[subQ1,subQ0]});Q386=makeQuery(id+"F0.imprint","IMPRINT",FACE,{"disambiguationData":[TD([[makeQuery(id+"F0.imprint","IMPRINT",EDGE,{"disambiguationData":[TD([[subQ2,-1.0]])],"derivedFrom":subQ1}),-1.0]])]});}
            var Q387;
            {var subQ0=sQuery(id+"F0.wireOp",EDGE,"E9");var subQ1=sQuery(id+"F0.wireOp",EDGE,"E5");var subQ2=makeQuery(id+"F0.imprint","INTERSECT",VERTEX,{"derivedFrom":[subQ1,subQ0]});Q387=makeQuery(id+"F0.imprint","IMPRINT",FACE,{"disambiguationData":[TD([[makeQuery(id+"F0.imprint","IMPRINT",EDGE,{"disambiguationData":[TD([[subQ2,-1.0]])],"derivedFrom":subQ1}),1.0]])]});}
            var Q388;
            {var subQ0=sQuery(id+"F0.wireOp",EDGE,"E35");var subQ1=sQuery(id+"F0.wireOp",EDGE,"E8");var subQ2=makeQuery(id+"F0.imprint","INTERSECT",VERTEX,{"derivedFrom":[subQ1,subQ0]});Q388=makeQuery(id+"F0.imprint","IMPRINT",FACE,{"disambiguationData":[TD([[makeQuery(id+"F0.imprint","IMPRINT",EDGE,{"disambiguationData":[TD([[subQ2,-1.0]])],"derivedFrom":subQ1}),-1.0]])]});}
            var Q389;
            {var subQ0=sQuery(id+"F0.wireOp",EDGE,"E14");var subQ1=sQuery(id+"F0.wireOp",EDGE,"E3");var subQ2=makeQuery(id+"F0.imprint","INTERSECT",VERTEX,{"derivedFrom":[subQ1,subQ0]});Q389=makeQuery(id+"F0.imprint","IMPRINT",FACE,{"disambiguationData":[TD([[makeQuery(id+"F0.imprint","IMPRINT",EDGE,{"disambiguationData":[TD([[subQ2,-1.0]])],"derivedFrom":subQ1}),1.0]])]});}
            var Q390;
            {var subQ0=sQuery(id+"F0.wireOp",EDGE,"E39");var subQ1=sQuery(id+"F0.wireOp",EDGE,"E8");var subQ2=makeQuery(id+"F0.imprint","INTERSECT",VERTEX,{"derivedFrom":[subQ1,subQ0]});Q390=makeQuery(id+"F0.imprint","IMPRINT",FACE,{"disambiguationData":[TD([[makeQuery(id+"F0.imprint","IMPRINT",EDGE,{"disambiguationData":[TD([[subQ2,-1.0]])],"derivedFrom":subQ1}),-1.0]])]});}
            var Q391;
            {var subQ3=sQuery(id+"F0.wireOp",EDGE,"E48");var subQ6=sQuery(id+"F0.wireOp",EDGE,"E28");var subQ10=makeQuery(id+"F0.imprint","INTERSECT",VERTEX,{"derivedFrom":[subQ6,subQ3]});Q391=makeQuery(id+"F0.imprint","IMPRINT",FACE,{"disambiguationData":[TD([[makeQuery(id+"F0.imprint","IMPRINT",EDGE,{"disambiguationData":[TD([[subQ10,-1.0]])],"derivedFrom":subQ6}),-1.0]])]});}
            var Q392;
            {var subQ0=sQuery(id+"F0.wireOp",EDGE,"E17");var subQ1=sQuery(id+"F0.wireOp",EDGE,"E4");var subQ2=makeQuery(id+"F0.imprint","INTERSECT",VERTEX,{"derivedFrom":[subQ1,subQ0]});Q392=makeQuery(id+"F0.imprint","IMPRINT",FACE,{"disambiguationData":[TD([[makeQuery(id+"F0.imprint","IMPRINT",EDGE,{"disambiguationData":[TD([[subQ2,-1.0]])],"derivedFrom":subQ1}),1.0]])]});}
            var Q393;
            {var subQ0=sQuery(id+"F0.wireOp",EDGE,"E21");var subQ1=sQuery(id+"F0.wireOp",EDGE,"E2");var subQ2=makeQuery(id+"F0.imprint","INTERSECT",VERTEX,{"derivedFrom":[subQ1,subQ0]});Q393=makeQuery(id+"F0.imprint","IMPRINT",FACE,{"disambiguationData":[TD([[makeQuery(id+"F0.imprint","IMPRINT",EDGE,{"disambiguationData":[TD([[subQ2,-1.0]])],"derivedFrom":subQ1}),-1.0]])]});}
            var Q394;
            {var subQ0=sQuery(id+"F0.wireOp",EDGE,"E53");var subQ1=sQuery(id+"F0.wireOp",EDGE,"E30");var subQ2=makeQuery(id+"F0.imprint","INTERSECT",VERTEX,{"derivedFrom":[subQ1,subQ0]});Q394=makeQuery(id+"F0.imprint","IMPRINT",FACE,{"disambiguationData":[TD([[makeQuery(id+"F0.imprint","IMPRINT",EDGE,{"disambiguationData":[TD([[subQ2,-1.0]])],"derivedFrom":subQ1}),1.0]])]});}
            var Q395;
            {var subQ1=sQuery(id+"F0.wireOp",EDGE,"E10");var subQ7=sQuery(id+"F0.wireOp",EDGE,"E17");var subQ9=makeQuery(id+"F0.imprint","INTERSECT",VERTEX,{"derivedFrom":[subQ1,subQ7]});Q395=makeQuery(id+"F0.imprint","IMPRINT",FACE,{"disambiguationData":[TD([[makeQuery(id+"F0.imprint","IMPRINT",EDGE,{"disambiguationData":[TD([[subQ9,-1.0]])],"derivedFrom":subQ1}),-1.0]])]});}
            var Q396;
            {var subQ0=sQuery(id+"F0.wireOp",EDGE,"E37");var subQ1=sQuery(id+"F0.wireOp",EDGE,"E10");var subQ2=makeQuery(id+"F0.imprint","INTERSECT",VERTEX,{"derivedFrom":[subQ1,subQ0]});Q396=makeQuery(id+"F0.imprint","IMPRINT",FACE,{"disambiguationData":[TD([[makeQuery(id+"F0.imprint","IMPRINT",EDGE,{"disambiguationData":[TD([[subQ2,-1.0]])],"derivedFrom":subQ1}),-1.0]])]});}
            var Q397;
            {var subQ0=sQuery(id+"F0.wireOp",EDGE,"E6");var subQ1=sQuery(id+"F0.wireOp",EDGE,"E4");var subQ2=makeQuery(id+"F0.imprint","INTERSECT",VERTEX,{"derivedFrom":[subQ1,subQ0]});Q397=makeQuery(id+"F0.imprint","IMPRINT",FACE,{"disambiguationData":[TD([[makeQuery(id+"F0.imprint","IMPRINT",EDGE,{"disambiguationData":[TD([[subQ2,-1.0]])],"derivedFrom":subQ1}),1.0]])]});}
            var Q398;
            {var subQ0=sQuery(id+"F0.wireOp",EDGE,"E38");var subQ1=sQuery(id+"F0.wireOp",EDGE,"E4");var subQ2=makeQuery(id+"F0.imprint","INTERSECT",VERTEX,{"derivedFrom":[subQ1,subQ0]});Q398=makeQuery(id+"F0.imprint","IMPRINT",FACE,{"disambiguationData":[TD([[makeQuery(id+"F0.imprint","IMPRINT",EDGE,{"disambiguationData":[TD([[subQ2,-1.0]])],"derivedFrom":subQ1}),-1.0]])]});}
            var Q399;
            {var subQ0=sQuery(id+"F0.wireOp",EDGE,"E39");var subQ1=sQuery(id+"F0.wireOp",EDGE,"E4");var subQ2=makeQuery(id+"F0.imprint","INTERSECT",VERTEX,{"derivedFrom":[subQ1,subQ0]});Q399=makeQuery(id+"F0.imprint","IMPRINT",FACE,{"disambiguationData":[TD([[makeQuery(id+"F0.imprint","IMPRINT",EDGE,{"disambiguationData":[TD([[subQ2,-1.0]])],"derivedFrom":subQ1}),1.0]])]});}
            var Q400;
            {var subQ0=sQuery(id+"F0.wireOp",EDGE,"E42");var subQ1=sQuery(id+"F0.wireOp",EDGE,"E39");var subQ2=makeQuery(id+"F0.imprint","INTERSECT",VERTEX,{"derivedFrom":[subQ1,subQ0]});Q400=makeQuery(id+"F0.imprint","IMPRINT",FACE,{"disambiguationData":[TD([[makeQuery(id+"F0.imprint","IMPRINT",EDGE,{"disambiguationData":[TD([[subQ2,-1.0]])],"derivedFrom":subQ1}),1.0]])]});}
            var Q401;
            {var subQ0=sQuery(id+"F0.wireOp",EDGE,"E10");var subQ1=sQuery(id+"F0.wireOp",EDGE,"E6");var subQ2=makeQuery(id+"F0.imprint","INTERSECT",VERTEX,{"derivedFrom":[subQ1,subQ0]});Q401=makeQuery(id+"F0.imprint","IMPRINT",FACE,{"disambiguationData":[TD([[makeQuery(id+"F0.imprint","IMPRINT",EDGE,{"disambiguationData":[TD([[subQ2,-1.0]])],"derivedFrom":subQ1}),1.0]])]});}
            var Q402;
            {var subQ0=sQuery(id+"F0.wireOp",EDGE,"E48");var subQ1=sQuery(id+"F0.wireOp",EDGE,"E30");var subQ2=makeQuery(id+"F0.imprint","INTERSECT",VERTEX,{"derivedFrom":[subQ1,subQ0]});Q402=makeQuery(id+"F0.imprint","IMPRINT",FACE,{"disambiguationData":[TD([[makeQuery(id+"F0.imprint","IMPRINT",EDGE,{"disambiguationData":[TD([[subQ2,-1.0]])],"derivedFrom":subQ1}),1.0]])]});}
            var Q403;
            {var subQ0=sQuery(id+"F0.wireOp",EDGE,"E7");var subQ1=sQuery(id+"F0.wireOp",EDGE,"E5");var subQ2=makeQuery(id+"F0.imprint","INTERSECT",VERTEX,{"derivedFrom":[subQ1,subQ0]});Q403=makeQuery(id+"F0.imprint","IMPRINT",FACE,{"disambiguationData":[TD([[makeQuery(id+"F0.imprint","IMPRINT",EDGE,{"disambiguationData":[TD([[subQ2,-1.0]])],"derivedFrom":subQ1}),1.0]])]});}
            var Q404;
            {var subQ0=sQuery(id+"F0.wireOp",EDGE,"E20");var subQ1=sQuery(id+"F0.wireOp",EDGE,"E5");var subQ2=makeQuery(id+"F0.imprint","INTERSECT",VERTEX,{"derivedFrom":[subQ1,subQ0]});Q404=makeQuery(id+"F0.imprint","IMPRINT",FACE,{"disambiguationData":[TD([[makeQuery(id+"F0.imprint","IMPRINT",EDGE,{"disambiguationData":[TD([[subQ2,-1.0]])],"derivedFrom":subQ1}),1.0]])]});}
            var Q405;
            {var subQ0=sQuery(id+"F0.wireOp",EDGE,"E34");var subQ1=sQuery(id+"F0.wireOp",EDGE,"E32");var subQ2=makeQuery(id+"F0.imprint","INTERSECT",VERTEX,{"derivedFrom":[subQ1,subQ0]});Q405=makeQuery(id+"F0.imprint","IMPRINT",FACE,{"disambiguationData":[TD([[makeQuery(id+"F0.imprint","IMPRINT",EDGE,{"disambiguationData":[TD([[subQ2,-1.0]])],"derivedFrom":subQ1}),-1.0]])]});}
            var Q406;
            {var subQ0=sQuery(id+"F0.wireOp",EDGE,"E33");var subQ1=sQuery(id+"F0.wireOp",EDGE,"E29");var subQ2=makeQuery(id+"F0.imprint","INTERSECT",VERTEX,{"derivedFrom":[subQ1,subQ0]});Q406=makeQuery(id+"F0.imprint","IMPRINT",FACE,{"disambiguationData":[TD([[makeQuery(id+"F0.imprint","IMPRINT",EDGE,{"disambiguationData":[TD([[subQ2,-1.0]])],"derivedFrom":subQ1}),-1.0]])]});}
            var Q407;
            {var subQ0=sQuery(id+"F0.wireOp",EDGE,"E48");var subQ1=sQuery(id+"F0.wireOp",EDGE,"E30");var subQ2=makeQuery(id+"F0.imprint","INTERSECT",VERTEX,{"derivedFrom":[subQ1,subQ0]});Q407=makeQuery(id+"F0.imprint","IMPRINT",FACE,{"disambiguationData":[TD([[makeQuery(id+"F0.imprint","IMPRINT",EDGE,{"disambiguationData":[TD([[subQ2,-1.0]])],"derivedFrom":subQ1}),-1.0]])]});}
            var Q408;
            {var subQ0=sQuery(id+"F0.wireOp",EDGE,"E13");var subQ1=sQuery(id+"F0.wireOp",EDGE,"E8");var subQ2=makeQuery(id+"F0.imprint","INTERSECT",VERTEX,{"derivedFrom":[subQ1,subQ0]});Q408=makeQuery(id+"F0.imprint","IMPRINT",FACE,{"disambiguationData":[TD([[makeQuery(id+"F0.imprint","IMPRINT",EDGE,{"disambiguationData":[TD([[subQ2,-1.0]])],"derivedFrom":subQ1}),1.0]])]});}
            var Q409;
            {var subQ0=sQuery(id+"F0.wireOp",EDGE,"E54");var subQ1=sQuery(id+"F0.wireOp",EDGE,"E32");var subQ2=makeQuery(id+"F0.imprint","INTERSECT",VERTEX,{"derivedFrom":[subQ1,subQ0]});Q409=makeQuery(id+"F0.imprint","IMPRINT",FACE,{"disambiguationData":[TD([[makeQuery(id+"F0.imprint","IMPRINT",EDGE,{"disambiguationData":[TD([[subQ2,-1.0]])],"derivedFrom":subQ1}),-1.0]])]});}
            var Q410;
            {var subQ0=sQuery(id+"F0.wireOp",EDGE,"E31");var subQ1=sQuery(id+"F0.wireOp",EDGE,"E30");var subQ2=makeQuery(id+"F0.imprint","INTERSECT",VERTEX,{"derivedFrom":[subQ1,subQ0]});Q410=makeQuery(id+"F0.imprint","IMPRINT",FACE,{"disambiguationData":[TD([[makeQuery(id+"F0.imprint","IMPRINT",EDGE,{"disambiguationData":[TD([[subQ2,-1.0]])],"derivedFrom":subQ1}),-1.0]])]});}
            var Q411;
            {var subQ3=sQuery(id+"F0.wireOp",EDGE,"E56");var subQ8=sQuery(id+"F0.wireOp",EDGE,"E30");var subQ11=makeQuery(id+"F0.imprint","INTERSECT",VERTEX,{"derivedFrom":[subQ8,subQ3]});Q411=makeQuery(id+"F0.imprint","IMPRINT",FACE,{"disambiguationData":[TD([[makeQuery(id+"F0.imprint","IMPRINT",EDGE,{"disambiguationData":[TD([[subQ11,-1.0]])],"derivedFrom":subQ8}),-1.0]])]});}
            var Q412;
            {var subQ0=sQuery(id+"F0.wireOp",EDGE,"E16");var subQ1=sQuery(id+"F0.wireOp",EDGE,"E3");var subQ2=makeQuery(id+"F0.imprint","INTERSECT",VERTEX,{"derivedFrom":[subQ1,subQ0]});Q412=makeQuery(id+"F0.imprint","IMPRINT",FACE,{"disambiguationData":[TD([[makeQuery(id+"F0.imprint","IMPRINT",EDGE,{"disambiguationData":[TD([[subQ2,-1.0]])],"derivedFrom":subQ1}),1.0]])]});}
            var Q413;
            {var subQ0=sQuery(id+"F0.wireOp",EDGE,"E48");var subQ1=sQuery(id+"F0.wireOp",EDGE,"E23");var subQ2=makeQuery(id+"F0.imprint","INTERSECT",VERTEX,{"derivedFrom":[subQ1,subQ0]});Q413=makeQuery(id+"F0.imprint","IMPRINT",FACE,{"disambiguationData":[TD([[makeQuery(id+"F0.imprint","IMPRINT",EDGE,{"disambiguationData":[TD([[subQ2,-1.0]])],"derivedFrom":subQ1}),-1.0]])]});}
            var Q414;
            {var subQ0=sQuery(id+"F0.wireOp",EDGE,"E51");var subQ1=sQuery(id+"F0.wireOp",EDGE,"E49");var subQ2=makeQuery(id+"F0.imprint","INTERSECT",VERTEX,{"derivedFrom":[subQ1,subQ0]});Q414=makeQuery(id+"F0.imprint","IMPRINT",FACE,{"disambiguationData":[TD([[makeQuery(id+"F0.imprint","IMPRINT",EDGE,{"disambiguationData":[TD([[subQ2,-1.0]])],"derivedFrom":subQ1}),-1.0]])]});}
            var Q415;
            {var subQ0=sQuery(id+"F0.wireOp",EDGE,"E7");var subQ1=sQuery(id+"F0.wireOp",EDGE,"E4");var subQ2=makeQuery(id+"F0.imprint","INTERSECT",VERTEX,{"derivedFrom":[subQ1,subQ0]});Q415=makeQuery(id+"F0.imprint","IMPRINT",FACE,{"disambiguationData":[TD([[makeQuery(id+"F0.imprint","IMPRINT",EDGE,{"disambiguationData":[TD([[subQ2,-1.0]])],"derivedFrom":subQ1}),1.0]])]});}
            var Q416;
            {var subQ0=sQuery(id+"F0.wireOp",EDGE,"E53");var subQ1=sQuery(id+"F0.wireOp",EDGE,"E35");var subQ2=makeQuery(id+"F0.imprint","INTERSECT",VERTEX,{"derivedFrom":[subQ1,subQ0]});Q416=makeQuery(id+"F0.imprint","IMPRINT",FACE,{"disambiguationData":[TD([[makeQuery(id+"F0.imprint","IMPRINT",EDGE,{"disambiguationData":[TD([[subQ2,-1.0]])],"derivedFrom":subQ1}),-1.0]])]});}
            var Q417;
            {var subQ0=sQuery(id+"F0.wireOp",EDGE,"E19");var subQ1=sQuery(id+"F0.wireOp",EDGE,"E3");var subQ2=makeQuery(id+"F0.imprint","INTERSECT",VERTEX,{"derivedFrom":[subQ1,subQ0]});Q417=makeQuery(id+"F0.imprint","IMPRINT",FACE,{"disambiguationData":[TD([[makeQuery(id+"F0.imprint","IMPRINT",EDGE,{"disambiguationData":[TD([[subQ2,-1.0]])],"derivedFrom":subQ1}),-1.0]])]});}
            var Q418;
            {var subQ0=sQuery(id+"F0.wireOp",EDGE,"E33");var subQ1=sQuery(id+"F0.wireOp",EDGE,"E31");var subQ2=makeQuery(id+"F0.imprint","INTERSECT",VERTEX,{"derivedFrom":[subQ1,subQ0]});Q418=makeQuery(id+"F0.imprint","IMPRINT",FACE,{"disambiguationData":[TD([[makeQuery(id+"F0.imprint","IMPRINT",EDGE,{"disambiguationData":[TD([[subQ2,-1.0]])],"derivedFrom":subQ1}),-1.0]])]});}
            var Q419;
            {var subQ0=sQuery(id+"F0.wireOp",EDGE,"E9");var subQ1=sQuery(id+"F0.wireOp",EDGE,"E7");var subQ2=makeQuery(id+"F0.imprint","INTERSECT",VERTEX,{"derivedFrom":[subQ1,subQ0]});Q419=makeQuery(id+"F0.imprint","IMPRINT",FACE,{"disambiguationData":[TD([[makeQuery(id+"F0.imprint","IMPRINT",EDGE,{"disambiguationData":[TD([[subQ2,-1.0]])],"derivedFrom":subQ1}),1.0]])]});}
            var Q420;
            {var subQ0=sQuery(id+"F0.wireOp",EDGE,"E55");var subQ1=sQuery(id+"F0.wireOp",EDGE,"E34");var subQ2=makeQuery(id+"F0.imprint","INTERSECT",VERTEX,{"derivedFrom":[subQ1,subQ0]});Q420=makeQuery(id+"F0.imprint","IMPRINT",FACE,{"disambiguationData":[TD([[makeQuery(id+"F0.imprint","IMPRINT",EDGE,{"disambiguationData":[TD([[subQ2,-1.0]])],"derivedFrom":subQ1}),1.0]])]});}
            var Q421;
            {var subQ0=sQuery(id+"F0.wireOp",EDGE,"E42");var subQ1=sQuery(id+"F0.wireOp",EDGE,"E7");var subQ2=makeQuery(id+"F0.imprint","INTERSECT",VERTEX,{"derivedFrom":[subQ1,subQ0]});Q421=makeQuery(id+"F0.imprint","IMPRINT",FACE,{"disambiguationData":[TD([[makeQuery(id+"F0.imprint","IMPRINT",EDGE,{"disambiguationData":[TD([[subQ2,-1.0]])],"derivedFrom":subQ1}),1.0]])]});}
            var Q422;
            {var subQ0=sQuery(id+"F0.wireOp",EDGE,"E48");var subQ1=sQuery(id+"F0.wireOp",EDGE,"E23");var subQ2=makeQuery(id+"F0.imprint","INTERSECT",VERTEX,{"derivedFrom":[subQ1,subQ0]});Q422=makeQuery(id+"F0.imprint","IMPRINT",FACE,{"disambiguationData":[TD([[makeQuery(id+"F0.imprint","IMPRINT",EDGE,{"disambiguationData":[TD([[subQ2,-1.0]])],"derivedFrom":subQ1}),1.0]])]});}
            var Q423;
            {var subQ0=sQuery(id+"F0.wireOp",EDGE,"E37");var subQ1=sQuery(id+"F0.wireOp",EDGE,"E7");var subQ2=makeQuery(id+"F0.imprint","INTERSECT",VERTEX,{"derivedFrom":[subQ1,subQ0]});Q423=makeQuery(id+"F0.imprint","IMPRINT",FACE,{"disambiguationData":[TD([[makeQuery(id+"F0.imprint","IMPRINT",EDGE,{"disambiguationData":[TD([[subQ2,-1.0]])],"derivedFrom":subQ1}),1.0]])]});}
            var Q424;
            {var subQ0=sQuery(id+"F0.wireOp",EDGE,"E40");var subQ1=sQuery(id+"F0.wireOp",EDGE,"E5");var subQ2=makeQuery(id+"F0.imprint","INTERSECT",VERTEX,{"derivedFrom":[subQ1,subQ0]});Q424=makeQuery(id+"F0.imprint","IMPRINT",FACE,{"disambiguationData":[TD([[makeQuery(id+"F0.imprint","IMPRINT",EDGE,{"disambiguationData":[TD([[subQ2,-1.0]])],"derivedFrom":subQ1}),1.0]])]});}
            var Q425;
            {var subQ0=sQuery(id+"F0.wireOp",EDGE,"E16");var subQ1=sQuery(id+"F0.wireOp",EDGE,"E7");var subQ2=makeQuery(id+"F0.imprint","INTERSECT",VERTEX,{"derivedFrom":[subQ1,subQ0]});Q425=makeQuery(id+"F0.imprint","IMPRINT",FACE,{"disambiguationData":[TD([[makeQuery(id+"F0.imprint","IMPRINT",EDGE,{"disambiguationData":[TD([[subQ2,-1.0]])],"derivedFrom":subQ1}),-1.0]])]});}
            var Q426;
            {var subQ0=sQuery(id+"F0.wireOp",EDGE,"E37");var subQ1=sQuery(id+"F0.wireOp",EDGE,"E34");var subQ2=makeQuery(id+"F0.imprint","INTERSECT",VERTEX,{"derivedFrom":[subQ1,subQ0]});Q426=makeQuery(id+"F0.imprint","IMPRINT",FACE,{"disambiguationData":[TD([[makeQuery(id+"F0.imprint","IMPRINT",EDGE,{"disambiguationData":[TD([[subQ2,-1.0]])],"derivedFrom":subQ1}),1.0]])]});}
            var Q427;
            {var subQ1=sQuery(id+"F0.wireOp",EDGE,"E30");var subQ5=sQuery(id+"F0.wireOp",EDGE,"E49");var subQ9=makeQuery(id+"F0.imprint","INTERSECT",VERTEX,{"derivedFrom":[subQ1,subQ5]});Q427=makeQuery(id+"F0.imprint","IMPRINT",FACE,{"disambiguationData":[TD([[makeQuery(id+"F0.imprint","IMPRINT",EDGE,{"disambiguationData":[TD([[subQ9,-1.0]])],"derivedFrom":subQ1}),-1.0]])]});}
            var Q428;
            {var subQ1=sQuery(id+"F0.wireOp",EDGE,"E30");var subQ5=sQuery(id+"F0.wireOp",EDGE,"E33");var subQ6=makeQuery(id+"F0.imprint","INTERSECT",VERTEX,{"derivedFrom":[subQ1,subQ5]});Q428=makeQuery(id+"F0.imprint","IMPRINT",FACE,{"disambiguationData":[TD([[makeQuery(id+"F0.imprint","IMPRINT",EDGE,{"disambiguationData":[TD([[subQ6,-1.0]])],"derivedFrom":subQ1}),1.0]])]});}
            var Q429;
            {var subQ0=sQuery(id+"F0.wireOp",EDGE,"E7");var subQ1=sQuery(id+"F0.wireOp",EDGE,"E5");var subQ2=makeQuery(id+"F0.imprint","INTERSECT",VERTEX,{"derivedFrom":[subQ1,subQ0]});Q429=makeQuery(id+"F0.imprint","IMPRINT",FACE,{"disambiguationData":[TD([[makeQuery(id+"F0.imprint","IMPRINT",EDGE,{"disambiguationData":[TD([[subQ2,-1.0]])],"derivedFrom":subQ1}),-1.0]])]});}
            var Q430;
            {var subQ0=sQuery(id+"F0.wireOp",EDGE,"E36");var subQ1=sQuery(id+"F0.wireOp",EDGE,"E5");var subQ2=makeQuery(id+"F0.imprint","INTERSECT",VERTEX,{"derivedFrom":[subQ1,subQ0]});Q430=makeQuery(id+"F0.imprint","IMPRINT",FACE,{"disambiguationData":[TD([[makeQuery(id+"F0.imprint","IMPRINT",EDGE,{"disambiguationData":[TD([[subQ2,-1.0]])],"derivedFrom":subQ1}),-1.0]])]});}
            var Q431;
            {var subQ7=sQuery(id+"F0.wireOp",EDGE,"E33");var subQ9=sQuery(id+"F0.wireOp",EDGE,"E9");var subQ10=makeQuery(id+"F0.imprint","INTERSECT",VERTEX,{"derivedFrom":[subQ9,subQ7]});Q431=makeQuery(id+"F0.imprint","IMPRINT",FACE,{"disambiguationData":[TD([[makeQuery(id+"F0.imprint","IMPRINT",EDGE,{"disambiguationData":[TD([[subQ10,-1.0]])],"derivedFrom":subQ9}),1.0]])]});}
            var Q432;
            {var subQ0=sQuery(id+"F0.wireOp",EDGE,"E19");var subQ1=sQuery(id+"F0.wireOp",EDGE,"E6");var subQ2=makeQuery(id+"F0.imprint","INTERSECT",VERTEX,{"derivedFrom":[subQ1,subQ0]});Q432=makeQuery(id+"F0.imprint","IMPRINT",FACE,{"disambiguationData":[TD([[makeQuery(id+"F0.imprint","IMPRINT",EDGE,{"disambiguationData":[TD([[subQ2,-1.0]])],"derivedFrom":subQ1}),1.0]])]});}
            var Q433;
            {var subQ0=sQuery(id+"F0.wireOp",EDGE,"E36");var subQ1=sQuery(id+"F0.wireOp",EDGE,"E9");var subQ2=makeQuery(id+"F0.imprint","INTERSECT",VERTEX,{"derivedFrom":[subQ1,subQ0]});Q433=makeQuery(id+"F0.imprint","IMPRINT",FACE,{"disambiguationData":[TD([[makeQuery(id+"F0.imprint","IMPRINT",EDGE,{"disambiguationData":[TD([[subQ2,-1.0]])],"derivedFrom":subQ1}),1.0]])]});}
            var Q434;
            {var subQ0=sQuery(id+"F0.wireOp",EDGE,"E12");var subQ1=sQuery(id+"F0.wireOp",EDGE,"E9");var subQ2=makeQuery(id+"F0.imprint","INTERSECT",VERTEX,{"derivedFrom":[subQ1,subQ0]});Q434=makeQuery(id+"F0.imprint","IMPRINT",FACE,{"disambiguationData":[TD([[makeQuery(id+"F0.imprint","IMPRINT",EDGE,{"disambiguationData":[TD([[subQ2,-1.0]])],"derivedFrom":subQ1}),1.0]])]});}
            var Q435;
            {var subQ0=sQuery(id+"F0.wireOp",EDGE,"E34");var subQ1=sQuery(id+"F0.wireOp",EDGE,"E8");var subQ2=makeQuery(id+"F0.imprint","INTERSECT",VERTEX,{"derivedFrom":[subQ1,subQ0]});Q435=makeQuery(id+"F0.imprint","IMPRINT",FACE,{"disambiguationData":[TD([[makeQuery(id+"F0.imprint","IMPRINT",EDGE,{"disambiguationData":[TD([[subQ2,-1.0]])],"derivedFrom":subQ1}),-1.0]])]});}
            var Q436;
            {var subQ0=sQuery(id+"F0.wireOp",EDGE,"E6");var subQ1=sQuery(id+"F0.wireOp",EDGE,"E1");var subQ2=makeQuery(id+"F0.imprint","INTERSECT",VERTEX,{"derivedFrom":[subQ1,subQ0]});Q436=makeQuery(id+"F0.imprint","IMPRINT",FACE,{"disambiguationData":[TD([[makeQuery(id+"F0.imprint","IMPRINT",EDGE,{"disambiguationData":[TD([[subQ2,-1.0]])],"derivedFrom":subQ1}),1.0]])]});}
            var Q437;
            {var subQ0=sQuery(id+"F0.wireOp",EDGE,"E13");var subQ1=sQuery(id+"F0.wireOp",EDGE,"E7");var subQ2=makeQuery(id+"F0.imprint","INTERSECT",VERTEX,{"derivedFrom":[subQ1,subQ0]});Q437=makeQuery(id+"F0.imprint","IMPRINT",FACE,{"disambiguationData":[TD([[makeQuery(id+"F0.imprint","IMPRINT",EDGE,{"disambiguationData":[TD([[subQ2,-1.0]])],"derivedFrom":subQ1}),1.0]])]});}
            var Q438;
            {var subQ0=sQuery(id+"F0.wireOp",EDGE,"E33");var subQ1=sQuery(id+"F0.wireOp",EDGE,"E32");var subQ2=makeQuery(id+"F0.imprint","INTERSECT",VERTEX,{"derivedFrom":[subQ1,subQ0]});Q438=makeQuery(id+"F0.imprint","IMPRINT",FACE,{"disambiguationData":[TD([[makeQuery(id+"F0.imprint","IMPRINT",EDGE,{"disambiguationData":[TD([[subQ2,-1.0]])],"derivedFrom":subQ1}),-1.0]])]});}
            var Q439;
            {var subQ5=sQuery(id+"F0.wireOp",EDGE,"E35");var subQ7=sQuery(id+"F0.wireOp",EDGE,"E8");var subQ8=makeQuery(id+"F0.imprint","INTERSECT",VERTEX,{"derivedFrom":[subQ7,subQ5]});Q439=makeQuery(id+"F0.imprint","IMPRINT",FACE,{"disambiguationData":[TD([[makeQuery(id+"F0.imprint","IMPRINT",EDGE,{"disambiguationData":[TD([[subQ8,-1.0]])],"derivedFrom":subQ7}),1.0]])]});}
            var Q440;
            {var subQ0=sQuery(id+"F0.wireOp",EDGE,"E19");var subQ1=sQuery(id+"F0.wireOp",EDGE,"E3");var subQ2=makeQuery(id+"F0.imprint","INTERSECT",VERTEX,{"derivedFrom":[subQ1,subQ0]});Q440=makeQuery(id+"F0.imprint","IMPRINT",FACE,{"disambiguationData":[TD([[makeQuery(id+"F0.imprint","IMPRINT",EDGE,{"disambiguationData":[TD([[subQ2,-1.0]])],"derivedFrom":subQ1}),1.0]])]});}
            var Q441;
            {var subQ0=sQuery(id+"F0.wireOp",EDGE,"E50");var subQ1=sQuery(id+"F0.wireOp",EDGE,"E48");var subQ2=makeQuery(id+"F0.imprint","INTERSECT",VERTEX,{"derivedFrom":[subQ1,subQ0]});Q441=makeQuery(id+"F0.imprint","IMPRINT",FACE,{"disambiguationData":[TD([[makeQuery(id+"F0.imprint","IMPRINT",EDGE,{"disambiguationData":[TD([[subQ2,-1.0]])],"derivedFrom":subQ1}),-1.0]])]});}
            var Q442;
            {var subQ0=sQuery(id+"F0.wireOp",EDGE,"E17");var subQ1=sQuery(id+"F0.wireOp",EDGE,"E8");var subQ2=makeQuery(id+"F0.imprint","INTERSECT",VERTEX,{"derivedFrom":[subQ1,subQ0]});Q442=makeQuery(id+"F0.imprint","IMPRINT",FACE,{"disambiguationData":[TD([[makeQuery(id+"F0.imprint","IMPRINT",EDGE,{"disambiguationData":[TD([[subQ2,-1.0]])],"derivedFrom":subQ1}),-1.0]])]});}
            var Q443;
            {var subQ1=sQuery(id+"F0.wireOp",EDGE,"E8");var subQ11=sQuery(id+"F0.wireOp",EDGE,"E34");var subQ12=makeQuery(id+"F0.imprint","INTERSECT",VERTEX,{"derivedFrom":[subQ1,subQ11]});Q443=makeQuery(id+"F0.imprint","IMPRINT",FACE,{"disambiguationData":[TD([[makeQuery(id+"F0.imprint","IMPRINT",EDGE,{"disambiguationData":[TD([[subQ12,-1.0]])],"derivedFrom":subQ1}),1.0]])]});}
            var Q444;
            {var subQ3=sQuery(id+"F0.wireOp",EDGE,"E40");var subQ6=sQuery(id+"F0.wireOp",EDGE,"E8");var subQ9=makeQuery(id+"F0.imprint","INTERSECT",VERTEX,{"derivedFrom":[subQ6,subQ3]});Q444=makeQuery(id+"F0.imprint","IMPRINT",FACE,{"disambiguationData":[TD([[makeQuery(id+"F0.imprint","IMPRINT",EDGE,{"disambiguationData":[TD([[subQ9,-1.0]])],"derivedFrom":subQ6}),1.0]])]});}
            var Q445;
            {var subQ0=sQuery(id+"F0.wireOp",EDGE,"E23");var subQ1=sQuery(id+"F0.wireOp",EDGE,"E21");var subQ2=makeQuery(id+"F0.imprint","INTERSECT",VERTEX,{"derivedFrom":[subQ1,subQ0]});Q445=makeQuery(id+"F0.imprint","IMPRINT",FACE,{"disambiguationData":[TD([[makeQuery(id+"F0.imprint","IMPRINT",EDGE,{"disambiguationData":[TD([[subQ2,-1.0]])],"derivedFrom":subQ1}),-1.0]])]});}
            var Q446;
            {var subQ0=sQuery(id+"F0.wireOp",EDGE,"E19");var subQ1=sQuery(id+"F0.wireOp",EDGE,"E1");var subQ2=makeQuery(id+"F0.imprint","INTERSECT",VERTEX,{"derivedFrom":[subQ1,subQ0]});Q446=makeQuery(id+"F0.imprint","IMPRINT",FACE,{"disambiguationData":[TD([[makeQuery(id+"F0.imprint","IMPRINT",EDGE,{"disambiguationData":[TD([[subQ2,-1.0]])],"derivedFrom":subQ1}),-1.0]])]});}
            var Q447;
            {var subQ0=sQuery(id+"F0.wireOp",EDGE,"E32");var subQ1=sQuery(id+"F0.wireOp",EDGE,"E10");var subQ2=makeQuery(id+"F0.imprint","INTERSECT",VERTEX,{"derivedFrom":[subQ1,subQ0]});Q447=makeQuery(id+"F0.imprint","IMPRINT",FACE,{"disambiguationData":[TD([[makeQuery(id+"F0.imprint","IMPRINT",EDGE,{"disambiguationData":[TD([[subQ2,-1.0]])],"derivedFrom":subQ1}),-1.0]])]});}
            var Q448;
            {var subQ0=sQuery(id+"F0.wireOp",EDGE,"E38");var subQ1=sQuery(id+"F0.wireOp",EDGE,"E35");var subQ2=makeQuery(id+"F0.imprint","INTERSECT",VERTEX,{"derivedFrom":[subQ1,subQ0]});Q448=makeQuery(id+"F0.imprint","IMPRINT",FACE,{"disambiguationData":[TD([[makeQuery(id+"F0.imprint","IMPRINT",EDGE,{"disambiguationData":[TD([[subQ2,-1.0]])],"derivedFrom":subQ1}),-1.0]])]});}
            var Q449;
            {var subQ5=sQuery(id+"F0.wireOp",EDGE,"E40");var subQ8=sQuery(id+"F0.wireOp",EDGE,"E7");var subQ11=makeQuery(id+"F0.imprint","INTERSECT",VERTEX,{"derivedFrom":[subQ8,subQ5]});Q449=makeQuery(id+"F0.imprint","IMPRINT",FACE,{"disambiguationData":[TD([[makeQuery(id+"F0.imprint","IMPRINT",EDGE,{"disambiguationData":[TD([[subQ11,-1.0]])],"derivedFrom":subQ8}),1.0]])]});}
            var Q450;
            {var subQ0=sQuery(id+"F0.wireOp",EDGE,"E15");var subQ1=sQuery(id+"F0.wireOp",EDGE,"E12");var subQ2=makeQuery(id+"F0.imprint","INTERSECT",VERTEX,{"derivedFrom":[subQ1,subQ0]});Q450=makeQuery(id+"F0.imprint","IMPRINT",FACE,{"disambiguationData":[TD([[makeQuery(id+"F0.imprint","IMPRINT",EDGE,{"disambiguationData":[TD([[subQ2,-1.0]])],"derivedFrom":subQ1}),-1.0]])]});}
            var Q451;
            {var subQ0=sQuery(id+"F0.wireOp",EDGE,"E8");var subQ1=sQuery(id+"F0.wireOp",EDGE,"E5");var subQ2=makeQuery(id+"F0.imprint","INTERSECT",VERTEX,{"derivedFrom":[subQ1,subQ0]});Q451=makeQuery(id+"F0.imprint","IMPRINT",FACE,{"disambiguationData":[TD([[makeQuery(id+"F0.imprint","IMPRINT",EDGE,{"disambiguationData":[TD([[subQ2,-1.0]])],"derivedFrom":subQ1}),1.0]])]});}
            var Q452;
            {var subQ0=sQuery(id+"F0.wireOp",EDGE,"E37");var subQ1=sQuery(id+"F0.wireOp",EDGE,"E5");var subQ2=makeQuery(id+"F0.imprint","INTERSECT",VERTEX,{"derivedFrom":[subQ1,subQ0]});Q452=makeQuery(id+"F0.imprint","IMPRINT",FACE,{"disambiguationData":[TD([[makeQuery(id+"F0.imprint","IMPRINT",EDGE,{"disambiguationData":[TD([[subQ2,-1.0]])],"derivedFrom":subQ1}),1.0]])]});}
            var Q453;
            {var subQ0=sQuery(id+"F0.wireOp",EDGE,"E56");var subQ1=sQuery(id+"F0.wireOp",EDGE,"E31");var subQ2=makeQuery(id+"F0.imprint","INTERSECT",VERTEX,{"derivedFrom":[subQ1,subQ0]});Q453=makeQuery(id+"F0.imprint","IMPRINT",FACE,{"disambiguationData":[TD([[makeQuery(id+"F0.imprint","IMPRINT",EDGE,{"disambiguationData":[TD([[subQ2,-1.0]])],"derivedFrom":subQ1}),1.0]])]});}
            var Q454;
            {var subQ0=sQuery(id+"F0.wireOp",EDGE,"E41");var subQ1=sQuery(id+"F0.wireOp",EDGE,"E3");var subQ2=makeQuery(id+"F0.imprint","INTERSECT",VERTEX,{"derivedFrom":[subQ1,subQ0]});Q454=makeQuery(id+"F0.imprint","IMPRINT",FACE,{"disambiguationData":[TD([[makeQuery(id+"F0.imprint","IMPRINT",EDGE,{"disambiguationData":[TD([[subQ2,-1.0]])],"derivedFrom":subQ1}),-1.0]])]});}
            var Q455;
            {var subQ5=sQuery(id+"F0.wireOp",EDGE,"E1");var subQ7=sQuery(id+"F0.wireOp",EDGE,"E18");var subQ9=makeQuery(id+"F0.imprint","INTERSECT",VERTEX,{"derivedFrom":[subQ5,subQ7]});Q455=makeQuery(id+"F0.imprint","IMPRINT",FACE,{"disambiguationData":[TD([[makeQuery(id+"F0.imprint","IMPRINT",EDGE,{"disambiguationData":[TD([[subQ9,-1.0]])],"derivedFrom":subQ5}),-1.0]])]});}
            var Q456;
            {var subQ0=sQuery(id+"F0.wireOp",EDGE,"E54");var subQ1=sQuery(id+"F0.wireOp",EDGE,"E31");var subQ2=makeQuery(id+"F0.imprint","INTERSECT",VERTEX,{"derivedFrom":[subQ1,subQ0]});Q456=makeQuery(id+"F0.imprint","IMPRINT",FACE,{"disambiguationData":[TD([[makeQuery(id+"F0.imprint","IMPRINT",EDGE,{"disambiguationData":[TD([[subQ2,-1.0]])],"derivedFrom":subQ1}),-1.0]])]});}
            var Q457;
            {var subQ0=sQuery(id+"F0.wireOp",EDGE,"E43");var subQ1=sQuery(id+"F0.wireOp",EDGE,"E9");var subQ2=makeQuery(id+"F0.imprint","INTERSECT",VERTEX,{"derivedFrom":[subQ1,subQ0]});Q457=makeQuery(id+"F0.imprint","IMPRINT",FACE,{"disambiguationData":[TD([[makeQuery(id+"F0.imprint","IMPRINT",EDGE,{"disambiguationData":[TD([[subQ2,-1.0]])],"derivedFrom":subQ1}),1.0]])]});}
            var Q458;
            {var subQ0=sQuery(id+"F0.wireOp",EDGE,"E16");var subQ1=sQuery(id+"F0.wireOp",EDGE,"E13");var subQ2=makeQuery(id+"F0.imprint","INTERSECT",VERTEX,{"derivedFrom":[subQ1,subQ0]});Q458=makeQuery(id+"F0.imprint","IMPRINT",FACE,{"disambiguationData":[TD([[makeQuery(id+"F0.imprint","IMPRINT",EDGE,{"disambiguationData":[TD([[subQ2,-1.0]])],"derivedFrom":subQ1}),1.0]])]});}
            var Q459;
            {var subQ0=sQuery(id+"F0.wireOp",EDGE,"E13");var subQ1=sQuery(id+"F0.wireOp",EDGE,"E5");var subQ2=makeQuery(id+"F0.imprint","INTERSECT",VERTEX,{"derivedFrom":[subQ1,subQ0]});Q459=makeQuery(id+"F0.imprint","IMPRINT",FACE,{"disambiguationData":[TD([[makeQuery(id+"F0.imprint","IMPRINT",EDGE,{"disambiguationData":[TD([[subQ2,-1.0]])],"derivedFrom":subQ1}),1.0]])]});}
            var Q460;
            {var subQ0=sQuery(id+"F0.wireOp",EDGE,"E52");var subQ1=sQuery(id+"F0.wireOp",EDGE,"E29");var subQ2=makeQuery(id+"F0.imprint","INTERSECT",VERTEX,{"derivedFrom":[subQ1,subQ0]});Q460=makeQuery(id+"F0.imprint","IMPRINT",FACE,{"disambiguationData":[TD([[makeQuery(id+"F0.imprint","IMPRINT",EDGE,{"disambiguationData":[TD([[subQ2,-1.0]])],"derivedFrom":subQ1}),1.0]])]});}
            var Q461;
            {var subQ0=sQuery(id+"F0.wireOp",EDGE,"E50");var subQ1=sQuery(id+"F0.wireOp",EDGE,"E31");var subQ2=makeQuery(id+"F0.imprint","INTERSECT",VERTEX,{"derivedFrom":[subQ1,subQ0]});Q461=makeQuery(id+"F0.imprint","IMPRINT",FACE,{"disambiguationData":[TD([[makeQuery(id+"F0.imprint","IMPRINT",EDGE,{"disambiguationData":[TD([[subQ2,-1.0]])],"derivedFrom":subQ1}),1.0]])]});}
            var Q462;
            {var subQ0=sQuery(id+"F0.wireOp",EDGE,"E56");var subQ1=sQuery(id+"F0.wireOp",EDGE,"E34");var subQ2=makeQuery(id+"F0.imprint","INTERSECT",VERTEX,{"derivedFrom":[subQ1,subQ0]});Q462=makeQuery(id+"F0.imprint","IMPRINT",FACE,{"disambiguationData":[TD([[makeQuery(id+"F0.imprint","IMPRINT",EDGE,{"disambiguationData":[TD([[subQ2,-1.0]])],"derivedFrom":subQ1}),1.0]])]});}
            var Q463;
            {var subQ0=sQuery(id+"F0.wireOp",EDGE,"E17");var subQ1=sQuery(id+"F0.wireOp",EDGE,"E2");var subQ2=makeQuery(id+"F0.imprint","INTERSECT",VERTEX,{"derivedFrom":[subQ1,subQ0]});Q463=makeQuery(id+"F0.imprint","IMPRINT",FACE,{"disambiguationData":[TD([[makeQuery(id+"F0.imprint","IMPRINT",EDGE,{"disambiguationData":[TD([[subQ2,-1.0]])],"derivedFrom":subQ1}),-1.0]])]});}
            var Q464;
            {var subQ0=sQuery(id+"F0.wireOp",EDGE,"E39");var subQ1=sQuery(id+"F0.wireOp",EDGE,"E6");var subQ2=makeQuery(id+"F0.imprint","INTERSECT",VERTEX,{"derivedFrom":[subQ1,subQ0]});Q464=makeQuery(id+"F0.imprint","IMPRINT",FACE,{"disambiguationData":[TD([[makeQuery(id+"F0.imprint","IMPRINT",EDGE,{"disambiguationData":[TD([[subQ2,-1.0]])],"derivedFrom":subQ1}),-1.0]])]});}
            var Q465;
            {var subQ0=sQuery(id+"F0.wireOp",EDGE,"E51");var subQ1=sQuery(id+"F0.wireOp",EDGE,"E31");var subQ2=makeQuery(id+"F0.imprint","INTERSECT",VERTEX,{"derivedFrom":[subQ1,subQ0]});Q465=makeQuery(id+"F0.imprint","IMPRINT",FACE,{"disambiguationData":[TD([[makeQuery(id+"F0.imprint","IMPRINT",EDGE,{"disambiguationData":[TD([[subQ2,-1.0]])],"derivedFrom":subQ1}),-1.0]])]});}
            var Q466;
            {var subQ0=sQuery(id+"F0.wireOp",EDGE,"E58");var subQ1=sQuery(id+"F0.wireOp",EDGE,"E29");var subQ2=makeQuery(id+"F0.imprint","INTERSECT",VERTEX,{"derivedFrom":[subQ1,subQ0]});Q466=makeQuery(id+"F0.imprint","IMPRINT",FACE,{"disambiguationData":[TD([[makeQuery(id+"F0.imprint","IMPRINT",EDGE,{"disambiguationData":[TD([[subQ2,-1.0]])],"derivedFrom":subQ1}),-1.0]])]});}
            var Q467;
            {var subQ0=sQuery(id+"F0.wireOp",EDGE,"E58");var subQ1=sQuery(id+"F0.wireOp",EDGE,"E29");var subQ2=makeQuery(id+"F0.imprint","INTERSECT",VERTEX,{"derivedFrom":[subQ1,subQ0]});Q467=makeQuery(id+"F0.imprint","IMPRINT",FACE,{"disambiguationData":[TD([[makeQuery(id+"F0.imprint","IMPRINT",EDGE,{"disambiguationData":[TD([[subQ2,-1.0]])],"derivedFrom":subQ1}),1.0]])]});}
            var Q468;
            {var subQ0=sQuery(id+"F0.wireOp",EDGE,"E58");var subQ1=sQuery(id+"F0.wireOp",EDGE,"E28");var subQ2=makeQuery(id+"F0.imprint","INTERSECT",VERTEX,{"derivedFrom":[subQ1,subQ0]});Q468=makeQuery(id+"F0.imprint","IMPRINT",FACE,{"disambiguationData":[TD([[makeQuery(id+"F0.imprint","IMPRINT",EDGE,{"disambiguationData":[TD([[subQ2,-1.0]])],"derivedFrom":subQ1}),1.0]])]});}
            var Q469;
            {var subQ0=sQuery(id+"F0.wireOp",EDGE,"E51");var subQ1=sQuery(id+"F0.wireOp",EDGE,"E30");var subQ2=makeQuery(id+"F0.imprint","INTERSECT",VERTEX,{"derivedFrom":[subQ1,subQ0]});Q469=makeQuery(id+"F0.imprint","IMPRINT",FACE,{"disambiguationData":[TD([[makeQuery(id+"F0.imprint","IMPRINT",EDGE,{"disambiguationData":[TD([[subQ2,-1.0]])],"derivedFrom":subQ1}),1.0]])]});}
            var Q470;
            {var subQ5=sQuery(id+"F0.wireOp",EDGE,"E34");var subQ7=sQuery(id+"F0.wireOp",EDGE,"E37");var subQ8=makeQuery(id+"F0.imprint","INTERSECT",VERTEX,{"derivedFrom":[subQ5,subQ7]});Q470=makeQuery(id+"F0.imprint","IMPRINT",FACE,{"disambiguationData":[TD([[makeQuery(id+"F0.imprint","IMPRINT",EDGE,{"disambiguationData":[TD([[subQ8,-1.0]])],"derivedFrom":subQ5}),-1.0]])]});}
            var Q471;
            {var subQ0=sQuery(id+"F0.wireOp",EDGE,"E40");var subQ1=sQuery(id+"F0.wireOp",EDGE,"E12");var subQ2=makeQuery(id+"F0.imprint","INTERSECT",VERTEX,{"derivedFrom":[subQ1,subQ0]});Q471=makeQuery(id+"F0.imprint","IMPRINT",FACE,{"disambiguationData":[TD([[makeQuery(id+"F0.imprint","IMPRINT",EDGE,{"disambiguationData":[TD([[subQ2,-1.0]])],"derivedFrom":subQ1}),1.0]])]});}
            var Q472;
            {var subQ0=sQuery(id+"F0.wireOp",EDGE,"E9");var subQ1=sQuery(id+"F0.wireOp",EDGE,"E6");var subQ2=makeQuery(id+"F0.imprint","INTERSECT",VERTEX,{"derivedFrom":[subQ1,subQ0]});Q472=makeQuery(id+"F0.imprint","IMPRINT",FACE,{"disambiguationData":[TD([[makeQuery(id+"F0.imprint","IMPRINT",EDGE,{"disambiguationData":[TD([[subQ2,-1.0]])],"derivedFrom":subQ1}),1.0]])]});}
            var Q473;
            {var subQ0=sQuery(id+"F0.wireOp",EDGE,"E49");var subQ1=sQuery(id+"F0.wireOp",EDGE,"E28");var subQ2=makeQuery(id+"F0.imprint","INTERSECT",VERTEX,{"derivedFrom":[subQ1,subQ0]});Q473=makeQuery(id+"F0.imprint","IMPRINT",FACE,{"disambiguationData":[TD([[makeQuery(id+"F0.imprint","IMPRINT",EDGE,{"disambiguationData":[TD([[subQ2,-1.0]])],"derivedFrom":subQ1}),-1.0]])]});}
            var Q474;
            {var subQ0=sQuery(id+"F0.wireOp",EDGE,"E35");var subQ1=sQuery(id+"F0.wireOp",EDGE,"E14");var subQ2=makeQuery(id+"F0.imprint","INTERSECT",VERTEX,{"derivedFrom":[subQ1,subQ0]});Q474=makeQuery(id+"F0.imprint","IMPRINT",FACE,{"disambiguationData":[TD([[makeQuery(id+"F0.imprint","IMPRINT",EDGE,{"disambiguationData":[TD([[subQ2,-1.0]])],"derivedFrom":subQ1}),-1.0]])]});}
            var Q475;
            {var subQ0=sQuery(id+"F0.wireOp",EDGE,"E13");var subQ1=sQuery(id+"F0.wireOp",EDGE,"E6");var subQ2=makeQuery(id+"F0.imprint","INTERSECT",VERTEX,{"derivedFrom":[subQ1,subQ0]});Q475=makeQuery(id+"F0.imprint","IMPRINT",FACE,{"disambiguationData":[TD([[makeQuery(id+"F0.imprint","IMPRINT",EDGE,{"disambiguationData":[TD([[subQ2,-1.0]])],"derivedFrom":subQ1}),1.0]])]});}
            var Q476;
            {var subQ0=sQuery(id+"F0.wireOp",EDGE,"E40");var subQ1=sQuery(id+"F0.wireOp",EDGE,"E34");var subQ2=makeQuery(id+"F0.imprint","INTERSECT",VERTEX,{"derivedFrom":[subQ1,subQ0]});Q476=makeQuery(id+"F0.imprint","IMPRINT",FACE,{"disambiguationData":[TD([[makeQuery(id+"F0.imprint","IMPRINT",EDGE,{"disambiguationData":[TD([[subQ2,-1.0]])],"derivedFrom":subQ1}),-1.0]])]});}
            var Q477;
            {var subQ0=sQuery(id+"F0.wireOp",EDGE,"E43");var subQ1=sQuery(id+"F0.wireOp",EDGE,"E7");var subQ2=makeQuery(id+"F0.imprint","INTERSECT",VERTEX,{"derivedFrom":[subQ1,subQ0]});Q477=makeQuery(id+"F0.imprint","IMPRINT",FACE,{"disambiguationData":[TD([[makeQuery(id+"F0.imprint","IMPRINT",EDGE,{"disambiguationData":[TD([[subQ2,-1.0]])],"derivedFrom":subQ1}),-1.0]])]});}
            var Q478;
            {var subQ1=sQuery(id+"F0.wireOp",EDGE,"E9");var subQ7=sQuery(id+"F0.wireOp",EDGE,"E42");var subQ9=makeQuery(id+"F0.imprint","INTERSECT",VERTEX,{"derivedFrom":[subQ1,subQ7]});Q478=makeQuery(id+"F0.imprint","IMPRINT",FACE,{"disambiguationData":[TD([[makeQuery(id+"F0.imprint","IMPRINT",EDGE,{"disambiguationData":[TD([[subQ9,-1.0]])],"derivedFrom":subQ1}),1.0]])]});}
            var Q479;
            {var subQ0=sQuery(id+"F0.wireOp",EDGE,"E32");var subQ1=sQuery(id+"F0.wireOp",EDGE,"E31");var subQ2=makeQuery(id+"F0.imprint","INTERSECT",VERTEX,{"derivedFrom":[subQ1,subQ0]});Q479=makeQuery(id+"F0.imprint","IMPRINT",FACE,{"disambiguationData":[TD([[makeQuery(id+"F0.imprint","IMPRINT",EDGE,{"disambiguationData":[TD([[subQ2,-1.0]])],"derivedFrom":subQ1}),-1.0]])]});}
            var Q480;
            {var subQ0=sQuery(id+"F0.wireOp",EDGE,"E35");var subQ1=sQuery(id+"F0.wireOp",EDGE,"E11");var subQ2=makeQuery(id+"F0.imprint","INTERSECT",VERTEX,{"derivedFrom":[subQ1,subQ0]});Q480=makeQuery(id+"F0.imprint","IMPRINT",FACE,{"disambiguationData":[TD([[makeQuery(id+"F0.imprint","IMPRINT",EDGE,{"disambiguationData":[TD([[subQ2,-1.0]])],"derivedFrom":subQ1}),1.0]])]});}
            var Q481;
            {var subQ5=sQuery(id+"F0.wireOp",EDGE,"E10");var subQ7=sQuery(id+"F0.wireOp",EDGE,"E33");var subQ9=makeQuery(id+"F0.imprint","INTERSECT",VERTEX,{"derivedFrom":[subQ5,subQ7]});Q481=makeQuery(id+"F0.imprint","IMPRINT",FACE,{"disambiguationData":[TD([[makeQuery(id+"F0.imprint","IMPRINT",EDGE,{"disambiguationData":[TD([[subQ9,-1.0]])],"derivedFrom":subQ5}),1.0]])]});}
            var Q482;
            {var subQ0=sQuery(id+"F0.wireOp",EDGE,"E39");var subQ1=sQuery(id+"F0.wireOp",EDGE,"E3");var subQ2=makeQuery(id+"F0.imprint","INTERSECT",VERTEX,{"derivedFrom":[subQ1,subQ0]});Q482=makeQuery(id+"F0.imprint","IMPRINT",FACE,{"disambiguationData":[TD([[makeQuery(id+"F0.imprint","IMPRINT",EDGE,{"disambiguationData":[TD([[subQ2,-1.0]])],"derivedFrom":subQ1}),-1.0]])]});}
            var Q483;
            {var subQ5=sQuery(id+"F0.wireOp",EDGE,"E1");var subQ7=sQuery(id+"F0.wireOp",EDGE,"E22");var subQ9=makeQuery(id+"F0.imprint","INTERSECT",VERTEX,{"derivedFrom":[subQ5,subQ7]});Q483=makeQuery(id+"F0.imprint","IMPRINT",FACE,{"disambiguationData":[TD([[makeQuery(id+"F0.imprint","IMPRINT",EDGE,{"disambiguationData":[TD([[subQ9,-1.0]])],"derivedFrom":subQ5}),1.0]])]});}
            var Q484;
            {var subQ0=sQuery(id+"F0.wireOp",EDGE,"E20");var subQ1=sQuery(id+"F0.wireOp",EDGE,"E7");var subQ2=makeQuery(id+"F0.imprint","INTERSECT",VERTEX,{"derivedFrom":[subQ1,subQ0]});Q484=makeQuery(id+"F0.imprint","IMPRINT",FACE,{"disambiguationData":[TD([[makeQuery(id+"F0.imprint","IMPRINT",EDGE,{"disambiguationData":[TD([[subQ2,-1.0]])],"derivedFrom":subQ1}),1.0]])]});}
            var Q485;
            {var subQ0=sQuery(id+"F0.wireOp",EDGE,"E33");var subQ1=sQuery(id+"F0.wireOp",EDGE,"E13");var subQ2=makeQuery(id+"F0.imprint","INTERSECT",VERTEX,{"derivedFrom":[subQ1,subQ0]});Q485=makeQuery(id+"F0.imprint","IMPRINT",FACE,{"disambiguationData":[TD([[makeQuery(id+"F0.imprint","IMPRINT",EDGE,{"disambiguationData":[TD([[subQ2,-1.0]])],"derivedFrom":subQ1}),-1.0]])]});}
            var Q486;
            {var subQ0=sQuery(id+"F0.wireOp",EDGE,"E14");var subQ1=sQuery(id+"F0.wireOp",EDGE,"E5");var subQ2=makeQuery(id+"F0.imprint","INTERSECT",VERTEX,{"derivedFrom":[subQ1,subQ0]});Q486=makeQuery(id+"F0.imprint","IMPRINT",FACE,{"disambiguationData":[TD([[makeQuery(id+"F0.imprint","IMPRINT",EDGE,{"disambiguationData":[TD([[subQ2,-1.0]])],"derivedFrom":subQ1}),1.0]])]});}
            var Q487;
            {var subQ0=sQuery(id+"F0.wireOp",EDGE,"E42");var subQ1=sQuery(id+"F0.wireOp",EDGE,"E3");var subQ2=makeQuery(id+"F0.imprint","INTERSECT",VERTEX,{"derivedFrom":[subQ1,subQ0]});Q487=makeQuery(id+"F0.imprint","IMPRINT",FACE,{"disambiguationData":[TD([[makeQuery(id+"F0.imprint","IMPRINT",EDGE,{"disambiguationData":[TD([[subQ2,-1.0]])],"derivedFrom":subQ1}),-1.0]])]});}
            var Q488;
            {var subQ0=sQuery(id+"F0.wireOp",EDGE,"E9");var subQ1=sQuery(id+"F0.wireOp",EDGE,"E8");var subQ2=makeQuery(id+"F0.imprint","INTERSECT",VERTEX,{"derivedFrom":[subQ1,subQ0]});Q488=makeQuery(id+"F0.imprint","IMPRINT",FACE,{"disambiguationData":[TD([[makeQuery(id+"F0.imprint","IMPRINT",EDGE,{"disambiguationData":[TD([[subQ2,-1.0]])],"derivedFrom":subQ1}),1.0]])]});}
            var Q489;
            {var subQ0=sQuery(id+"F0.wireOp",EDGE,"E38");var subQ1=sQuery(id+"F0.wireOp",EDGE,"E6");var subQ2=makeQuery(id+"F0.imprint","INTERSECT",VERTEX,{"derivedFrom":[subQ1,subQ0]});Q489=makeQuery(id+"F0.imprint","IMPRINT",FACE,{"disambiguationData":[TD([[makeQuery(id+"F0.imprint","IMPRINT",EDGE,{"disambiguationData":[TD([[subQ2,-1.0]])],"derivedFrom":subQ1}),1.0]])]});}
            var Q490;
            {var subQ0=sQuery(id+"F0.wireOp",EDGE,"E35");var subQ1=sQuery(id+"F0.wireOp",EDGE,"E10");var subQ2=makeQuery(id+"F0.imprint","INTERSECT",VERTEX,{"derivedFrom":[subQ1,subQ0]});Q490=makeQuery(id+"F0.imprint","IMPRINT",FACE,{"disambiguationData":[TD([[makeQuery(id+"F0.imprint","IMPRINT",EDGE,{"disambiguationData":[TD([[subQ2,-1.0]])],"derivedFrom":subQ1}),1.0]])]});}
            var Q491;
            {var subQ0=sQuery(id+"F0.wireOp",EDGE,"E55");var subQ1=sQuery(id+"F0.wireOp",EDGE,"E30");var subQ2=makeQuery(id+"F0.imprint","INTERSECT",VERTEX,{"derivedFrom":[subQ1,subQ0]});Q491=makeQuery(id+"F0.imprint","IMPRINT",FACE,{"disambiguationData":[TD([[makeQuery(id+"F0.imprint","IMPRINT",EDGE,{"disambiguationData":[TD([[subQ2,-1.0]])],"derivedFrom":subQ1}),-1.0]])]});}
            var Q492;
            {var subQ1=sQuery(id+"F0.wireOp",EDGE,"E29");var subQ8=sQuery(id+"F0.wireOp",EDGE,"E49");var subQ10=makeQuery(id+"F0.imprint","INTERSECT",VERTEX,{"derivedFrom":[subQ1,subQ8]});Q492=makeQuery(id+"F0.imprint","IMPRINT",FACE,{"disambiguationData":[TD([[makeQuery(id+"F0.imprint","IMPRINT",EDGE,{"disambiguationData":[TD([[subQ10,-1.0]])],"derivedFrom":subQ1}),-1.0]])]});}
            var Q493;
            {var subQ1=sQuery(id+"F0.wireOp",EDGE,"E8");var subQ5=sQuery(id+"F0.wireOp",EDGE,"E33");var subQ6=makeQuery(id+"F0.imprint","INTERSECT",VERTEX,{"derivedFrom":[subQ1,subQ5]});Q493=makeQuery(id+"F0.imprint","IMPRINT",FACE,{"disambiguationData":[TD([[makeQuery(id+"F0.imprint","IMPRINT",EDGE,{"disambiguationData":[TD([[subQ6,-1.0]])],"derivedFrom":subQ1}),1.0]])]});}
            var Q494;
            {var subQ0=sQuery(id+"F0.wireOp",EDGE,"E53");var subQ1=sQuery(id+"F0.wireOp",EDGE,"E31");var subQ2=makeQuery(id+"F0.imprint","INTERSECT",VERTEX,{"derivedFrom":[subQ1,subQ0]});Q494=makeQuery(id+"F0.imprint","IMPRINT",FACE,{"disambiguationData":[TD([[makeQuery(id+"F0.imprint","IMPRINT",EDGE,{"disambiguationData":[TD([[subQ2,-1.0]])],"derivedFrom":subQ1}),-1.0]])]});}
            var Q495;
            {var subQ0=sQuery(id+"F0.wireOp",EDGE,"E38");var subQ1=sQuery(id+"F0.wireOp",EDGE,"E7");var subQ2=makeQuery(id+"F0.imprint","INTERSECT",VERTEX,{"derivedFrom":[subQ1,subQ0]});Q495=makeQuery(id+"F0.imprint","IMPRINT",FACE,{"disambiguationData":[TD([[makeQuery(id+"F0.imprint","IMPRINT",EDGE,{"disambiguationData":[TD([[subQ2,-1.0]])],"derivedFrom":subQ1}),1.0]])]});}
            var Q496;
            {var subQ0=sQuery(id+"F0.wireOp",EDGE,"E51");var subQ1=sQuery(id+"F0.wireOp",EDGE,"E29");var subQ2=makeQuery(id+"F0.imprint","INTERSECT",VERTEX,{"derivedFrom":[subQ1,subQ0]});Q496=makeQuery(id+"F0.imprint","IMPRINT",FACE,{"disambiguationData":[TD([[makeQuery(id+"F0.imprint","IMPRINT",EDGE,{"disambiguationData":[TD([[subQ2,-1.0]])],"derivedFrom":subQ1}),1.0]])]});}
            var Q497;
            {var subQ0=sQuery(id+"F0.wireOp",EDGE,"E50");var subQ1=sQuery(id+"F0.wireOp",EDGE,"E30");var subQ2=makeQuery(id+"F0.imprint","INTERSECT",VERTEX,{"derivedFrom":[subQ1,subQ0]});Q497=makeQuery(id+"F0.imprint","IMPRINT",FACE,{"disambiguationData":[TD([[makeQuery(id+"F0.imprint","IMPRINT",EDGE,{"disambiguationData":[TD([[subQ2,-1.0]])],"derivedFrom":subQ1}),1.0]])]});}
            var Q498;
            {var subQ0=sQuery(id+"F0.wireOp",EDGE,"E41");var subQ1=sQuery(id+"F0.wireOp",EDGE,"E8");var subQ2=makeQuery(id+"F0.imprint","INTERSECT",VERTEX,{"derivedFrom":[subQ1,subQ0]});Q498=makeQuery(id+"F0.imprint","IMPRINT",FACE,{"disambiguationData":[TD([[makeQuery(id+"F0.imprint","IMPRINT",EDGE,{"disambiguationData":[TD([[subQ2,-1.0]])],"derivedFrom":subQ1}),-1.0]])]});}
            var Q499;
            {var subQ0=sQuery(id+"F0.wireOp",EDGE,"E4");var subQ1=sQuery(id+"F0.wireOp",EDGE,"E3");var subQ2=makeQuery(id+"F0.imprint","INTERSECT",VERTEX,{"derivedFrom":[subQ1,subQ0]});Q499=makeQuery(id+"F0.imprint","IMPRINT",FACE,{"disambiguationData":[TD([[makeQuery(id+"F0.imprint","IMPRINT",EDGE,{"disambiguationData":[TD([[subQ2,-1.0]])],"derivedFrom":subQ1}),1.0]])]});}
            var Q500;
            {var subQ1=sQuery(id+"F0.wireOp",EDGE,"E30");var subQ7=sQuery(id+"F0.wireOp",EDGE,"E53");var subQ9=makeQuery(id+"F0.imprint","INTERSECT",VERTEX,{"derivedFrom":[subQ1,subQ7]});Q500=makeQuery(id+"F0.imprint","IMPRINT",FACE,{"disambiguationData":[TD([[makeQuery(id+"F0.imprint","IMPRINT",EDGE,{"disambiguationData":[TD([[subQ9,-1.0]])],"derivedFrom":subQ1}),-1.0]])]});}
            var Q501;
            {var subQ0=sQuery(id+"F0.wireOp",EDGE,"E10");var subQ1=sQuery(id+"F0.wireOp",EDGE,"E5");var subQ2=makeQuery(id+"F0.imprint","INTERSECT",VERTEX,{"derivedFrom":[subQ1,subQ0]});Q501=makeQuery(id+"F0.imprint","IMPRINT",FACE,{"disambiguationData":[TD([[makeQuery(id+"F0.imprint","IMPRINT",EDGE,{"disambiguationData":[TD([[subQ2,-1.0]])],"derivedFrom":subQ1}),1.0]])]});}
            var Q502;
            {var subQ0=sQuery(id+"F0.wireOp",EDGE,"E37");var subQ1=sQuery(id+"F0.wireOp",EDGE,"E14");var subQ2=makeQuery(id+"F0.imprint","INTERSECT",VERTEX,{"derivedFrom":[subQ1,subQ0]});Q502=makeQuery(id+"F0.imprint","IMPRINT",FACE,{"disambiguationData":[TD([[makeQuery(id+"F0.imprint","IMPRINT",EDGE,{"disambiguationData":[TD([[subQ2,-1.0]])],"derivedFrom":subQ1}),-1.0]])]});}
            var Q503;
            {var subQ0=sQuery(id+"F0.wireOp",EDGE,"E38");var subQ1=sQuery(id+"F0.wireOp",EDGE,"E34");var subQ2=makeQuery(id+"F0.imprint","INTERSECT",VERTEX,{"derivedFrom":[subQ1,subQ0]});Q503=makeQuery(id+"F0.imprint","IMPRINT",FACE,{"disambiguationData":[TD([[makeQuery(id+"F0.imprint","IMPRINT",EDGE,{"disambiguationData":[TD([[subQ2,-1.0]])],"derivedFrom":subQ1}),-1.0]])]});}
            var Q504;
            {var subQ0=sQuery(id+"F0.wireOp",EDGE,"E17");var subQ1=sQuery(id+"F0.wireOp",EDGE,"E8");var subQ2=makeQuery(id+"F0.imprint","INTERSECT",VERTEX,{"derivedFrom":[subQ1,subQ0]});Q504=makeQuery(id+"F0.imprint","IMPRINT",FACE,{"disambiguationData":[TD([[makeQuery(id+"F0.imprint","IMPRINT",EDGE,{"disambiguationData":[TD([[subQ2,-1.0]])],"derivedFrom":subQ1}),1.0]])]});}
            var Q505;
            {var subQ0=sQuery(id+"F0.wireOp",EDGE,"E31");var subQ1=sQuery(id+"F0.wireOp",EDGE,"E29");var subQ2=makeQuery(id+"F0.imprint","INTERSECT",VERTEX,{"derivedFrom":[subQ1,subQ0]});Q505=makeQuery(id+"F0.imprint","IMPRINT",FACE,{"disambiguationData":[TD([[makeQuery(id+"F0.imprint","IMPRINT",EDGE,{"disambiguationData":[TD([[subQ2,-1.0]])],"derivedFrom":subQ1}),-1.0]])]});}
            var Q506;
            {var subQ0=sQuery(id+"F0.wireOp",EDGE,"E35");var subQ1=sQuery(id+"F0.wireOp",EDGE,"E9");var subQ2=makeQuery(id+"F0.imprint","INTERSECT",VERTEX,{"derivedFrom":[subQ1,subQ0]});Q506=makeQuery(id+"F0.imprint","IMPRINT",FACE,{"disambiguationData":[TD([[makeQuery(id+"F0.imprint","IMPRINT",EDGE,{"disambiguationData":[TD([[subQ2,-1.0]])],"derivedFrom":subQ1}),1.0]])]});}
            var Q507;
            {var subQ0=sQuery(id+"F0.wireOp",EDGE,"E36");var subQ1=sQuery(id+"F0.wireOp",EDGE,"E33");var subQ2=makeQuery(id+"F0.imprint","INTERSECT",VERTEX,{"derivedFrom":[subQ1,subQ0]});Q507=makeQuery(id+"F0.imprint","IMPRINT",FACE,{"disambiguationData":[TD([[makeQuery(id+"F0.imprint","IMPRINT",EDGE,{"disambiguationData":[TD([[subQ2,-1.0]])],"derivedFrom":subQ1}),-1.0]])]});}
            var Q508;
            {var subQ1=sQuery(id+"F0.wireOp",EDGE,"E28");var subQ10=sQuery(id+"F0.wireOp",EDGE,"E58");var subQ12=makeQuery(id+"F0.imprint","INTERSECT",VERTEX,{"derivedFrom":[subQ1,subQ10]});Q508=makeQuery(id+"F0.imprint","IMPRINT",FACE,{"disambiguationData":[TD([[makeQuery(id+"F0.imprint","IMPRINT",EDGE,{"disambiguationData":[TD([[subQ12,-1.0]])],"derivedFrom":subQ1}),-1.0]])]});}
            var Q509;
            {var subQ0=sQuery(id+"F0.wireOp",EDGE,"E6");var subQ1=sQuery(id+"F0.wireOp",EDGE,"E5");var subQ2=makeQuery(id+"F0.imprint","INTERSECT",VERTEX,{"derivedFrom":[subQ1,subQ0]});Q509=makeQuery(id+"F0.imprint","IMPRINT",FACE,{"disambiguationData":[TD([[makeQuery(id+"F0.imprint","IMPRINT",EDGE,{"disambiguationData":[TD([[subQ2,-1.0]])],"derivedFrom":subQ1}),1.0]])]});}
            var Q510;
            {var subQ0=sQuery(id+"F0.wireOp",EDGE,"E39");var subQ1=sQuery(id+"F0.wireOp",EDGE,"E34");var subQ2=makeQuery(id+"F0.imprint","INTERSECT",VERTEX,{"derivedFrom":[subQ1,subQ0]});Q510=makeQuery(id+"F0.imprint","IMPRINT",FACE,{"disambiguationData":[TD([[makeQuery(id+"F0.imprint","IMPRINT",EDGE,{"disambiguationData":[TD([[subQ2,-1.0]])],"derivedFrom":subQ1}),-1.0]])]});}
            var Q511;
            {var subQ1=sQuery(id+"F0.wireOp",EDGE,"E5");var subQ5=sQuery(id+"F0.wireOp",EDGE,"E11");var subQ6=makeQuery(id+"F0.imprint","INTERSECT",VERTEX,{"derivedFrom":[subQ1,subQ5]});Q511=makeQuery(id+"F0.imprint","IMPRINT",FACE,{"disambiguationData":[TD([[makeQuery(id+"F0.imprint","IMPRINT",EDGE,{"disambiguationData":[TD([[subQ6,-1.0]])],"derivedFrom":subQ1}),1.0]])]});}
            var Q512;
            {var subQ0=sQuery(id+"F0.wireOp",EDGE,"E12");var subQ1=sQuery(id+"F0.wireOp",EDGE,"E7");var subQ2=makeQuery(id+"F0.imprint","INTERSECT",VERTEX,{"derivedFrom":[subQ1,subQ0]});Q512=makeQuery(id+"F0.imprint","IMPRINT",FACE,{"disambiguationData":[TD([[makeQuery(id+"F0.imprint","IMPRINT",EDGE,{"disambiguationData":[TD([[subQ2,-1.0]])],"derivedFrom":subQ1}),1.0]])]});}
            var Q513;
            {var subQ0=sQuery(id+"F0.wireOp",EDGE,"E18");var subQ1=sQuery(id+"F0.wireOp",EDGE,"E1");var subQ2=makeQuery(id+"F0.imprint","INTERSECT",VERTEX,{"derivedFrom":[subQ1,subQ0]});Q513=makeQuery(id+"F0.imprint","IMPRINT",FACE,{"disambiguationData":[TD([[makeQuery(id+"F0.imprint","IMPRINT",EDGE,{"disambiguationData":[TD([[subQ2,-1.0]])],"derivedFrom":subQ1}),1.0]])]});}
            var Q514;
            {var subQ0=sQuery(id+"F0.wireOp",EDGE,"E41");var subQ1=sQuery(id+"F0.wireOp",EDGE,"E7");var subQ2=makeQuery(id+"F0.imprint","INTERSECT",VERTEX,{"derivedFrom":[subQ1,subQ0]});Q514=makeQuery(id+"F0.imprint","IMPRINT",FACE,{"disambiguationData":[TD([[makeQuery(id+"F0.imprint","IMPRINT",EDGE,{"disambiguationData":[TD([[subQ2,-1.0]])],"derivedFrom":subQ1}),1.0]])]});}
            var Q515;
            {var subQ0=sQuery(id+"F0.wireOp",EDGE,"E50");var subQ1=sQuery(id+"F0.wireOp",EDGE,"E28");var subQ2=makeQuery(id+"F0.imprint","INTERSECT",VERTEX,{"derivedFrom":[subQ1,subQ0]});Q515=makeQuery(id+"F0.imprint","IMPRINT",FACE,{"disambiguationData":[TD([[makeQuery(id+"F0.imprint","IMPRINT",EDGE,{"disambiguationData":[TD([[subQ2,-1.0]])],"derivedFrom":subQ1}),-1.0]])]});}
            var Q516;
            {var subQ0=sQuery(id+"F0.wireOp",EDGE,"E34");var subQ1=sQuery(id+"F0.wireOp",EDGE,"E28");var subQ2=makeQuery(id+"F0.imprint","INTERSECT",VERTEX,{"derivedFrom":[subQ1,subQ0]});Q516=makeQuery(id+"F0.imprint","IMPRINT",FACE,{"disambiguationData":[TD([[makeQuery(id+"F0.imprint","IMPRINT",EDGE,{"disambiguationData":[TD([[subQ2,-1.0]])],"derivedFrom":subQ1}),-1.0]])]});}
            var Q517;
            {var subQ0=sQuery(id+"F0.wireOp",EDGE,"E51");var subQ1=sQuery(id+"F0.wireOp",EDGE,"E32");var subQ2=makeQuery(id+"F0.imprint","INTERSECT",VERTEX,{"derivedFrom":[subQ1,subQ0]});Q517=makeQuery(id+"F0.imprint","IMPRINT",FACE,{"disambiguationData":[TD([[makeQuery(id+"F0.imprint","IMPRINT",EDGE,{"disambiguationData":[TD([[subQ2,-1.0]])],"derivedFrom":subQ1}),-1.0]])]});}
            var Q518;
            {var subQ0=sQuery(id+"F0.wireOp",EDGE,"E52");var subQ1=sQuery(id+"F0.wireOp",EDGE,"E30");var subQ2=makeQuery(id+"F0.imprint","INTERSECT",VERTEX,{"derivedFrom":[subQ1,subQ0]});Q518=makeQuery(id+"F0.imprint","IMPRINT",FACE,{"disambiguationData":[TD([[makeQuery(id+"F0.imprint","IMPRINT",EDGE,{"disambiguationData":[TD([[subQ2,-1.0]])],"derivedFrom":subQ1}),-1.0]])]});}
            var Q519;
            {var subQ0=sQuery(id+"F0.wireOp",EDGE,"E38");var subQ1=sQuery(id+"F0.wireOp",EDGE,"E5");var subQ2=makeQuery(id+"F0.imprint","INTERSECT",VERTEX,{"derivedFrom":[subQ1,subQ0]});Q519=makeQuery(id+"F0.imprint","IMPRINT",FACE,{"disambiguationData":[TD([[makeQuery(id+"F0.imprint","IMPRINT",EDGE,{"disambiguationData":[TD([[subQ2,-1.0]])],"derivedFrom":subQ1}),1.0]])]});}
            var Q520;
            {var subQ0=sQuery(id+"F0.wireOp",EDGE,"E51");var subQ1=sQuery(id+"F0.wireOp",EDGE,"E35");var subQ2=makeQuery(id+"F0.imprint","INTERSECT",VERTEX,{"derivedFrom":[subQ1,subQ0]});Q520=makeQuery(id+"F0.imprint","IMPRINT",FACE,{"disambiguationData":[TD([[makeQuery(id+"F0.imprint","IMPRINT",EDGE,{"disambiguationData":[TD([[subQ2,-1.0]])],"derivedFrom":subQ1}),-1.0]])]});}
            var Q521;
            {var subQ1=sQuery(id+"F0.wireOp",EDGE,"E3");var subQ5=sQuery(id+"F0.wireOp",EDGE,"E17");var subQ9=makeQuery(id+"F0.imprint","INTERSECT",VERTEX,{"derivedFrom":[subQ1,subQ5]});Q521=makeQuery(id+"F0.imprint","IMPRINT",FACE,{"disambiguationData":[TD([[makeQuery(id+"F0.imprint","IMPRINT",EDGE,{"disambiguationData":[TD([[subQ9,-1.0]])],"derivedFrom":subQ1}),1.0]])]});}
            var Q522;
            {var subQ5=sQuery(id+"F0.wireOp",EDGE,"E57");var subQ7=sQuery(id+"F0.wireOp",EDGE,"E29");var subQ9=makeQuery(id+"F0.imprint","INTERSECT",VERTEX,{"derivedFrom":[subQ7,subQ5]});Q522=makeQuery(id+"F0.imprint","IMPRINT",FACE,{"disambiguationData":[TD([[makeQuery(id+"F0.imprint","IMPRINT",EDGE,{"disambiguationData":[TD([[subQ9,-1.0]])],"derivedFrom":subQ7}),-1.0]])]});}
            var Q523;
            {var subQ0=sQuery(id+"F0.wireOp",EDGE,"E43");var subQ1=sQuery(id+"F0.wireOp",EDGE,"E14");var subQ2=makeQuery(id+"F0.imprint","INTERSECT",VERTEX,{"derivedFrom":[subQ1,subQ0]});Q523=makeQuery(id+"F0.imprint","IMPRINT",FACE,{"disambiguationData":[TD([[makeQuery(id+"F0.imprint","IMPRINT",EDGE,{"disambiguationData":[TD([[subQ2,-1.0]])],"derivedFrom":subQ1}),1.0]])]});}
            var Q524;
            {var subQ0=sQuery(id+"F0.wireOp",EDGE,"E22");var subQ1=sQuery(id+"F0.wireOp",EDGE,"E4");var subQ2=makeQuery(id+"F0.imprint","INTERSECT",VERTEX,{"derivedFrom":[subQ1,subQ0]});Q524=makeQuery(id+"F0.imprint","IMPRINT",FACE,{"disambiguationData":[TD([[makeQuery(id+"F0.imprint","IMPRINT",EDGE,{"disambiguationData":[TD([[subQ2,-1.0]])],"derivedFrom":subQ1}),1.0]])]});}
            var Q525;
            {var subQ0=sQuery(id+"F0.wireOp",EDGE,"E11");var subQ1=sQuery(id+"F0.wireOp",EDGE,"E7");var subQ2=makeQuery(id+"F0.imprint","INTERSECT",VERTEX,{"derivedFrom":[subQ1,subQ0]});Q525=makeQuery(id+"F0.imprint","IMPRINT",FACE,{"disambiguationData":[TD([[makeQuery(id+"F0.imprint","IMPRINT",EDGE,{"disambiguationData":[TD([[subQ2,-1.0]])],"derivedFrom":subQ1}),1.0]])]});}
            var Q526;
            {var subQ0=sQuery(id+"F0.wireOp",EDGE,"E47");var subQ1=sQuery(id+"F0.wireOp",EDGE,"E29");var subQ2=makeQuery(id+"F0.imprint","INTERSECT",VERTEX,{"derivedFrom":[subQ1,subQ0]});Q526=makeQuery(id+"F0.imprint","IMPRINT",FACE,{"disambiguationData":[TD([[makeQuery(id+"F0.imprint","IMPRINT",EDGE,{"disambiguationData":[TD([[subQ2,-1.0]])],"derivedFrom":subQ1}),1.0]])]});}
            var Q527;
            {var subQ0=sQuery(id+"F0.wireOp",EDGE,"E43");var subQ1=sQuery(id+"F0.wireOp",EDGE,"E6");var subQ2=makeQuery(id+"F0.imprint","INTERSECT",VERTEX,{"derivedFrom":[subQ1,subQ0]});Q527=makeQuery(id+"F0.imprint","IMPRINT",FACE,{"disambiguationData":[TD([[makeQuery(id+"F0.imprint","IMPRINT",EDGE,{"disambiguationData":[TD([[subQ2,-1.0]])],"derivedFrom":subQ1}),1.0]])]});}
            var Q528;
            {var subQ0=sQuery(id+"F0.wireOp",EDGE,"E18");var subQ1=sQuery(id+"F0.wireOp",EDGE,"E6");var subQ2=makeQuery(id+"F0.imprint","INTERSECT",VERTEX,{"derivedFrom":[subQ1,subQ0]});Q528=makeQuery(id+"F0.imprint","IMPRINT",FACE,{"disambiguationData":[TD([[makeQuery(id+"F0.imprint","IMPRINT",EDGE,{"disambiguationData":[TD([[subQ2,-1.0]])],"derivedFrom":subQ1}),1.0]])]});}
            var Q529;
            {var subQ0=sQuery(id+"F0.wireOp",EDGE,"E19");var subQ1=sQuery(id+"F0.wireOp",EDGE,"E4");var subQ2=makeQuery(id+"F0.imprint","INTERSECT",VERTEX,{"derivedFrom":[subQ1,subQ0]});Q529=makeQuery(id+"F0.imprint","IMPRINT",FACE,{"disambiguationData":[TD([[makeQuery(id+"F0.imprint","IMPRINT",EDGE,{"disambiguationData":[TD([[subQ2,-1.0]])],"derivedFrom":subQ1}),1.0]])]});}
            var Q530;
            {var subQ0=sQuery(id+"F0.wireOp",EDGE,"E41");var subQ1=sQuery(id+"F0.wireOp",EDGE,"E12");var subQ2=makeQuery(id+"F0.imprint","INTERSECT",VERTEX,{"derivedFrom":[subQ1,subQ0]});Q530=makeQuery(id+"F0.imprint","IMPRINT",FACE,{"disambiguationData":[TD([[makeQuery(id+"F0.imprint","IMPRINT",EDGE,{"disambiguationData":[TD([[subQ2,-1.0]])],"derivedFrom":subQ1}),1.0]])]});}
            var Q531;
            {var subQ0=sQuery(id+"F0.wireOp",EDGE,"E49");var subQ1=sQuery(id+"F0.wireOp",EDGE,"E30");var subQ2=makeQuery(id+"F0.imprint","INTERSECT",VERTEX,{"derivedFrom":[subQ1,subQ0]});Q531=makeQuery(id+"F0.imprint","IMPRINT",FACE,{"disambiguationData":[TD([[makeQuery(id+"F0.imprint","IMPRINT",EDGE,{"disambiguationData":[TD([[subQ2,-1.0]])],"derivedFrom":subQ1}),1.0]])]});}
            var Q532;
            {var subQ0=sQuery(id+"F0.wireOp",EDGE,"E10");var subQ1=sQuery(id+"F0.wireOp",EDGE,"E8");var subQ2=makeQuery(id+"F0.imprint","INTERSECT",VERTEX,{"derivedFrom":[subQ1,subQ0]});Q532=makeQuery(id+"F0.imprint","IMPRINT",FACE,{"disambiguationData":[TD([[makeQuery(id+"F0.imprint","IMPRINT",EDGE,{"disambiguationData":[TD([[subQ2,-1.0]])],"derivedFrom":subQ1}),1.0]])]});}
            var Q533;
            {var subQ0=sQuery(id+"F0.wireOp",EDGE,"E38");var subQ1=sQuery(id+"F0.wireOp",EDGE,"E6");var subQ2=makeQuery(id+"F0.imprint","INTERSECT",VERTEX,{"derivedFrom":[subQ1,subQ0]});Q533=makeQuery(id+"F0.imprint","IMPRINT",FACE,{"disambiguationData":[TD([[makeQuery(id+"F0.imprint","IMPRINT",EDGE,{"disambiguationData":[TD([[subQ2,-1.0]])],"derivedFrom":subQ1}),-1.0]])]});}
            var Q534;
            {var subQ0=sQuery(id+"F0.wireOp",EDGE,"E35");var subQ1=sQuery(id+"F0.wireOp",EDGE,"E28");var subQ2=makeQuery(id+"F0.imprint","INTERSECT",VERTEX,{"derivedFrom":[subQ1,subQ0]});Q534=makeQuery(id+"F0.imprint","IMPRINT",FACE,{"disambiguationData":[TD([[makeQuery(id+"F0.imprint","IMPRINT",EDGE,{"disambiguationData":[TD([[subQ2,-1.0]])],"derivedFrom":subQ1}),-1.0]])]});}
            var Q535;
            {var subQ1=sQuery(id+"F0.wireOp",EDGE,"E7");var subQ7=sQuery(id+"F0.wireOp",EDGE,"E10");var subQ8=makeQuery(id+"F0.imprint","INTERSECT",VERTEX,{"derivedFrom":[subQ1,subQ7]});Q535=makeQuery(id+"F0.imprint","IMPRINT",FACE,{"disambiguationData":[TD([[makeQuery(id+"F0.imprint","IMPRINT",EDGE,{"disambiguationData":[TD([[subQ8,-1.0]])],"derivedFrom":subQ1}),1.0]])]});}
            var Q536;
            {var subQ0=sQuery(id+"F0.wireOp",EDGE,"E36");var subQ1=sQuery(id+"F0.wireOp",EDGE,"E35");var subQ2=makeQuery(id+"F0.imprint","INTERSECT",VERTEX,{"derivedFrom":[subQ1,subQ0]});Q536=makeQuery(id+"F0.imprint","IMPRINT",FACE,{"disambiguationData":[TD([[makeQuery(id+"F0.imprint","IMPRINT",EDGE,{"disambiguationData":[TD([[subQ2,-1.0]])],"derivedFrom":subQ1}),-1.0]])]});}
            var Q537;
            {var subQ0=sQuery(id+"F0.wireOp",EDGE,"E43");var subQ1=sQuery(id+"F0.wireOp",EDGE,"E8");var subQ2=makeQuery(id+"F0.imprint","INTERSECT",VERTEX,{"derivedFrom":[subQ1,subQ0]});Q537=makeQuery(id+"F0.imprint","IMPRINT",FACE,{"disambiguationData":[TD([[makeQuery(id+"F0.imprint","IMPRINT",EDGE,{"disambiguationData":[TD([[subQ2,-1.0]])],"derivedFrom":subQ1}),1.0]])]});}
            var Q538;
            {var subQ0=sQuery(id+"F0.wireOp",EDGE,"E17");var subQ1=sQuery(id+"F0.wireOp",EDGE,"E3");var subQ2=makeQuery(id+"F0.imprint","INTERSECT",VERTEX,{"derivedFrom":[subQ1,subQ0]});Q538=makeQuery(id+"F0.imprint","IMPRINT",FACE,{"disambiguationData":[TD([[makeQuery(id+"F0.imprint","IMPRINT",EDGE,{"disambiguationData":[TD([[subQ2,-1.0]])],"derivedFrom":subQ1}),-1.0]])]});}
            var Q539;
            {var subQ0=sQuery(id+"F0.wireOp",EDGE,"E16");var subQ1=sQuery(id+"F0.wireOp",EDGE,"E1");var subQ2=makeQuery(id+"F0.imprint","INTERSECT",VERTEX,{"derivedFrom":[subQ1,subQ0]});Q539=makeQuery(id+"F0.imprint","IMPRINT",FACE,{"disambiguationData":[TD([[makeQuery(id+"F0.imprint","IMPRINT",EDGE,{"disambiguationData":[TD([[subQ2,-1.0]])],"derivedFrom":subQ1}),1.0]])]});}
            var Q540;
            {var subQ0=sQuery(id+"F0.wireOp",EDGE,"E33");var subQ1=sQuery(id+"F0.wireOp",EDGE,"E28");var subQ2=makeQuery(id+"F0.imprint","INTERSECT",VERTEX,{"derivedFrom":[subQ1,subQ0]});Q540=makeQuery(id+"F0.imprint","IMPRINT",FACE,{"disambiguationData":[TD([[makeQuery(id+"F0.imprint","IMPRINT",EDGE,{"disambiguationData":[TD([[subQ2,-1.0]])],"derivedFrom":subQ1}),-1.0]])]});}
            var Q541;
            {var subQ0=sQuery(id+"F0.wireOp",EDGE,"E41");var subQ1=sQuery(id+"F0.wireOp",EDGE,"E2");var subQ2=makeQuery(id+"F0.imprint","INTERSECT",VERTEX,{"derivedFrom":[subQ1,subQ0]});Q541=makeQuery(id+"F0.imprint","IMPRINT",FACE,{"disambiguationData":[TD([[makeQuery(id+"F0.imprint","IMPRINT",EDGE,{"disambiguationData":[TD([[subQ2,-1.0]])],"derivedFrom":subQ1}),-1.0]])]});}
            var Q542;
            {var subQ0=sQuery(id+"F0.wireOp",EDGE,"E49");var subQ1=sQuery(id+"F0.wireOp",EDGE,"E29");var subQ2=makeQuery(id+"F0.imprint","INTERSECT",VERTEX,{"derivedFrom":[subQ1,subQ0]});Q542=makeQuery(id+"F0.imprint","IMPRINT",FACE,{"disambiguationData":[TD([[makeQuery(id+"F0.imprint","IMPRINT",EDGE,{"disambiguationData":[TD([[subQ2,-1.0]])],"derivedFrom":subQ1}),1.0]])]});}
            var Q543;
            {var subQ0=sQuery(id+"F0.wireOp",EDGE,"E37");var subQ1=sQuery(id+"F0.wireOp",EDGE,"E8");var subQ2=makeQuery(id+"F0.imprint","INTERSECT",VERTEX,{"derivedFrom":[subQ1,subQ0]});Q543=makeQuery(id+"F0.imprint","IMPRINT",FACE,{"disambiguationData":[TD([[makeQuery(id+"F0.imprint","IMPRINT",EDGE,{"disambiguationData":[TD([[subQ2,-1.0]])],"derivedFrom":subQ1}),1.0]])]});}
            var Q544;
            {var subQ0=sQuery(id+"F0.wireOp",EDGE,"E53");var subQ1=sQuery(id+"F0.wireOp",EDGE,"E31");var subQ2=makeQuery(id+"F0.imprint","INTERSECT",VERTEX,{"derivedFrom":[subQ1,subQ0]});Q544=makeQuery(id+"F0.imprint","IMPRINT",FACE,{"disambiguationData":[TD([[makeQuery(id+"F0.imprint","IMPRINT",EDGE,{"disambiguationData":[TD([[subQ2,-1.0]])],"derivedFrom":subQ1}),1.0]])]});}
            var Q545;
            {var subQ0=sQuery(id+"F0.wireOp",EDGE,"E48");var subQ1=sQuery(id+"F0.wireOp",EDGE,"E29");var subQ2=makeQuery(id+"F0.imprint","INTERSECT",VERTEX,{"derivedFrom":[subQ1,subQ0]});Q545=makeQuery(id+"F0.imprint","IMPRINT",FACE,{"disambiguationData":[TD([[makeQuery(id+"F0.imprint","IMPRINT",EDGE,{"disambiguationData":[TD([[subQ2,-1.0]])],"derivedFrom":subQ1}),-1.0]])]});}
            var Q546;
            {var subQ0=sQuery(id+"F0.wireOp",EDGE,"E54");var subQ1=sQuery(id+"F0.wireOp",EDGE,"E31");var subQ2=makeQuery(id+"F0.imprint","INTERSECT",VERTEX,{"derivedFrom":[subQ1,subQ0]});Q546=makeQuery(id+"F0.imprint","IMPRINT",FACE,{"disambiguationData":[TD([[makeQuery(id+"F0.imprint","IMPRINT",EDGE,{"disambiguationData":[TD([[subQ2,-1.0]])],"derivedFrom":subQ1}),1.0]])]});}
            var Q547;
            {var subQ0=sQuery(id+"F0.wireOp",EDGE,"E51");var subQ1=sQuery(id+"F0.wireOp",EDGE,"E31");var subQ2=makeQuery(id+"F0.imprint","INTERSECT",VERTEX,{"derivedFrom":[subQ1,subQ0]});Q547=makeQuery(id+"F0.imprint","IMPRINT",FACE,{"disambiguationData":[TD([[makeQuery(id+"F0.imprint","IMPRINT",EDGE,{"disambiguationData":[TD([[subQ2,-1.0]])],"derivedFrom":subQ1}),1.0]])]});}
            var Q548;
            {var subQ1=sQuery(id+"F0.wireOp",EDGE,"E28");var subQ8=sQuery(id+"F0.wireOp",EDGE,"E47");var subQ11=makeQuery(id+"F0.imprint","INTERSECT",VERTEX,{"derivedFrom":[subQ1,subQ8]});Q548=makeQuery(id+"F0.imprint","IMPRINT",FACE,{"disambiguationData":[TD([[makeQuery(id+"F0.imprint","IMPRINT",EDGE,{"disambiguationData":[TD([[subQ11,-1.0]])],"derivedFrom":subQ1}),-1.0]])]});}
            var Q549;
            {var subQ0=sQuery(id+"F0.wireOp",EDGE,"E56");var subQ1=sQuery(id+"F0.wireOp",EDGE,"E35");var subQ2=makeQuery(id+"F0.imprint","INTERSECT",VERTEX,{"derivedFrom":[subQ1,subQ0]});Q549=makeQuery(id+"F0.imprint","IMPRINT",FACE,{"disambiguationData":[TD([[makeQuery(id+"F0.imprint","IMPRINT",EDGE,{"disambiguationData":[TD([[subQ2,-1.0]])],"derivedFrom":subQ1}),1.0]])]});}
            var Q550;
            {var subQ0=sQuery(id+"F0.wireOp",EDGE,"E12");var subQ1=sQuery(id+"F0.wireOp",EDGE,"E6");var subQ2=makeQuery(id+"F0.imprint","INTERSECT",VERTEX,{"derivedFrom":[subQ1,subQ0]});Q550=makeQuery(id+"F0.imprint","IMPRINT",FACE,{"disambiguationData":[TD([[makeQuery(id+"F0.imprint","IMPRINT",EDGE,{"disambiguationData":[TD([[subQ2,-1.0]])],"derivedFrom":subQ1}),1.0]])]});}
            var Q551;
            {var subQ0=sQuery(id+"F0.wireOp",EDGE,"E48");var subQ1=sQuery(id+"F0.wireOp",EDGE,"E29");var subQ2=makeQuery(id+"F0.imprint","INTERSECT",VERTEX,{"derivedFrom":[subQ1,subQ0]});Q551=makeQuery(id+"F0.imprint","IMPRINT",FACE,{"disambiguationData":[TD([[makeQuery(id+"F0.imprint","IMPRINT",EDGE,{"disambiguationData":[TD([[subQ2,-1.0]])],"derivedFrom":subQ1}),1.0]])]});}
            var Q552;
            {var subQ0=sQuery(id+"F0.wireOp",EDGE,"E12");var subQ1=sQuery(id+"F0.wireOp",EDGE,"E8");var subQ2=makeQuery(id+"F0.imprint","INTERSECT",VERTEX,{"derivedFrom":[subQ1,subQ0]});Q552=makeQuery(id+"F0.imprint","IMPRINT",FACE,{"disambiguationData":[TD([[makeQuery(id+"F0.imprint","IMPRINT",EDGE,{"disambiguationData":[TD([[subQ2,-1.0]])],"derivedFrom":subQ1}),1.0]])]});}
            var Q553;
            {var subQ0=sQuery(id+"F0.wireOp",EDGE,"E42");var subQ1=sQuery(id+"F0.wireOp",EDGE,"E2");var subQ2=makeQuery(id+"F0.imprint","INTERSECT",VERTEX,{"derivedFrom":[subQ1,subQ0]});Q553=makeQuery(id+"F0.imprint","IMPRINT",FACE,{"disambiguationData":[TD([[makeQuery(id+"F0.imprint","IMPRINT",EDGE,{"disambiguationData":[TD([[subQ2,-1.0]])],"derivedFrom":subQ1}),-1.0]])]});}
            var Q554;
            {var subQ0=sQuery(id+"F0.wireOp",EDGE,"E56");var subQ1=sQuery(id+"F0.wireOp",EDGE,"E30");var subQ2=makeQuery(id+"F0.imprint","INTERSECT",VERTEX,{"derivedFrom":[subQ1,subQ0]});Q554=makeQuery(id+"F0.imprint","IMPRINT",FACE,{"disambiguationData":[TD([[makeQuery(id+"F0.imprint","IMPRINT",EDGE,{"disambiguationData":[TD([[subQ2,-1.0]])],"derivedFrom":subQ1}),1.0]])]});}
            var Q555;
            {var subQ0=sQuery(id+"F0.wireOp",EDGE,"E36");var subQ1=sQuery(id+"F0.wireOp",EDGE,"E34");var subQ2=makeQuery(id+"F0.imprint","INTERSECT",VERTEX,{"derivedFrom":[subQ1,subQ0]});Q555=makeQuery(id+"F0.imprint","IMPRINT",FACE,{"disambiguationData":[TD([[makeQuery(id+"F0.imprint","IMPRINT",EDGE,{"disambiguationData":[TD([[subQ2,-1.0]])],"derivedFrom":subQ1}),-1.0]])]});}
            var Q556;
            {var subQ0=sQuery(id+"F0.wireOp",EDGE,"E57");var subQ1=sQuery(id+"F0.wireOp",EDGE,"E31");var subQ2=makeQuery(id+"F0.imprint","INTERSECT",VERTEX,{"derivedFrom":[subQ1,subQ0]});Q556=makeQuery(id+"F0.imprint","IMPRINT",FACE,{"disambiguationData":[TD([[makeQuery(id+"F0.imprint","IMPRINT",EDGE,{"disambiguationData":[TD([[subQ2,-1.0]])],"derivedFrom":subQ1}),1.0]])]});}
            var Q557;
            {var subQ0=sQuery(id+"F0.wireOp",EDGE,"E10");var subQ1=sQuery(id+"F0.wireOp",EDGE,"E9");var subQ2=makeQuery(id+"F0.imprint","INTERSECT",VERTEX,{"derivedFrom":[subQ1,subQ0]});Q557=makeQuery(id+"F0.imprint","IMPRINT",FACE,{"disambiguationData":[TD([[makeQuery(id+"F0.imprint","IMPRINT",EDGE,{"disambiguationData":[TD([[subQ2,-1.0]])],"derivedFrom":subQ1}),1.0]])]});}
            var Q558;
            {var subQ0=sQuery(id+"F0.wireOp",EDGE,"E38");var subQ1=sQuery(id+"F0.wireOp",EDGE,"E3");var subQ2=makeQuery(id+"F0.imprint","INTERSECT",VERTEX,{"derivedFrom":[subQ1,subQ0]});Q558=makeQuery(id+"F0.imprint","IMPRINT",FACE,{"disambiguationData":[TD([[makeQuery(id+"F0.imprint","IMPRINT",EDGE,{"disambiguationData":[TD([[subQ2,-1.0]])],"derivedFrom":subQ1}),-1.0]])]});}
            var Q559;
            {var subQ0=sQuery(id+"F0.wireOp",EDGE,"E41");var subQ1=sQuery(id+"F0.wireOp",EDGE,"E5");var subQ2=makeQuery(id+"F0.imprint","INTERSECT",VERTEX,{"derivedFrom":[subQ1,subQ0]});Q559=makeQuery(id+"F0.imprint","IMPRINT",FACE,{"disambiguationData":[TD([[makeQuery(id+"F0.imprint","IMPRINT",EDGE,{"disambiguationData":[TD([[subQ2,-1.0]])],"derivedFrom":subQ1}),-1.0]])]});}
            var Q560;
            {var subQ0=sQuery(id+"F0.wireOp",EDGE,"E16");var subQ1=sQuery(id+"F0.wireOp",EDGE,"E3");var subQ2=makeQuery(id+"F0.imprint","INTERSECT",VERTEX,{"derivedFrom":[subQ1,subQ0]});Q560=makeQuery(id+"F0.imprint","IMPRINT",FACE,{"disambiguationData":[TD([[makeQuery(id+"F0.imprint","IMPRINT",EDGE,{"disambiguationData":[TD([[subQ2,-1.0]])],"derivedFrom":subQ1}),-1.0]])]});}
            var Q561;
            {var subQ0=sQuery(id+"F0.wireOp",EDGE,"E11");var subQ1=sQuery(id+"F0.wireOp",EDGE,"E9");var subQ2=makeQuery(id+"F0.imprint","INTERSECT",VERTEX,{"derivedFrom":[subQ1,subQ0]});Q561=makeQuery(id+"F0.imprint","IMPRINT",FACE,{"disambiguationData":[TD([[makeQuery(id+"F0.imprint","IMPRINT",EDGE,{"disambiguationData":[TD([[subQ2,-1.0]])],"derivedFrom":subQ1}),1.0]])]});}
            var Q562;
            {var subQ0=sQuery(id+"F0.wireOp",EDGE,"E57");var subQ1=sQuery(id+"F0.wireOp",EDGE,"E30");var subQ2=makeQuery(id+"F0.imprint","INTERSECT",VERTEX,{"derivedFrom":[subQ1,subQ0]});Q562=makeQuery(id+"F0.imprint","IMPRINT",FACE,{"disambiguationData":[TD([[makeQuery(id+"F0.imprint","IMPRINT",EDGE,{"disambiguationData":[TD([[subQ2,-1.0]])],"derivedFrom":subQ1}),1.0]])]});}
            var Q563;
            {var subQ0=sQuery(id+"F0.wireOp",EDGE,"E54");var subQ1=sQuery(id+"F0.wireOp",EDGE,"E29");var subQ2=makeQuery(id+"F0.imprint","INTERSECT",VERTEX,{"derivedFrom":[subQ1,subQ0]});Q563=makeQuery(id+"F0.imprint","IMPRINT",FACE,{"disambiguationData":[TD([[makeQuery(id+"F0.imprint","IMPRINT",EDGE,{"disambiguationData":[TD([[subQ2,-1.0]])],"derivedFrom":subQ1}),1.0]])]});}
            var Q564;
            {var subQ0=sQuery(id+"F0.wireOp",EDGE,"E40");var subQ1=sQuery(id+"F0.wireOp",EDGE,"E4");var subQ2=makeQuery(id+"F0.imprint","INTERSECT",VERTEX,{"derivedFrom":[subQ1,subQ0]});Q564=makeQuery(id+"F0.imprint","IMPRINT",FACE,{"disambiguationData":[TD([[makeQuery(id+"F0.imprint","IMPRINT",EDGE,{"disambiguationData":[TD([[subQ2,-1.0]])],"derivedFrom":subQ1}),1.0]])]});}
            var Q565;
            {var subQ0=sQuery(id+"F0.wireOp",EDGE,"E40");var subQ1=sQuery(id+"F0.wireOp",EDGE,"E6");var subQ2=makeQuery(id+"F0.imprint","INTERSECT",VERTEX,{"derivedFrom":[subQ1,subQ0]});Q565=makeQuery(id+"F0.imprint","IMPRINT",FACE,{"disambiguationData":[TD([[makeQuery(id+"F0.imprint","IMPRINT",EDGE,{"disambiguationData":[TD([[subQ2,-1.0]])],"derivedFrom":subQ1}),1.0]])]});}
            var Q566;
            {var subQ0=sQuery(id+"F0.wireOp",EDGE,"E12");var subQ1=sQuery(id+"F0.wireOp",EDGE,"E10");var subQ2=makeQuery(id+"F0.imprint","INTERSECT",VERTEX,{"derivedFrom":[subQ1,subQ0]});Q566=makeQuery(id+"F0.imprint","IMPRINT",FACE,{"disambiguationData":[TD([[makeQuery(id+"F0.imprint","IMPRINT",EDGE,{"disambiguationData":[TD([[subQ2,-1.0]])],"derivedFrom":subQ1}),1.0]])]});}
            var Q567;
            {var subQ0=sQuery(id+"F0.wireOp",EDGE,"E37");var subQ1=sQuery(id+"F0.wireOp",EDGE,"E7");var subQ2=makeQuery(id+"F0.imprint","INTERSECT",VERTEX,{"derivedFrom":[subQ1,subQ0]});Q567=makeQuery(id+"F0.imprint","IMPRINT",FACE,{"disambiguationData":[TD([[makeQuery(id+"F0.imprint","IMPRINT",EDGE,{"disambiguationData":[TD([[subQ2,-1.0]])],"derivedFrom":subQ1}),-1.0]])]});}
            var Q568;
            {var subQ0=sQuery(id+"F0.wireOp",EDGE,"E36");var subQ1=sQuery(id+"F0.wireOp",EDGE,"E5");var subQ2=makeQuery(id+"F0.imprint","INTERSECT",VERTEX,{"derivedFrom":[subQ1,subQ0]});Q568=makeQuery(id+"F0.imprint","IMPRINT",FACE,{"disambiguationData":[TD([[makeQuery(id+"F0.imprint","IMPRINT",EDGE,{"disambiguationData":[TD([[subQ2,-1.0]])],"derivedFrom":subQ1}),1.0]])]});}
            var Q569;
            {var subQ0=sQuery(id+"F0.wireOp",EDGE,"E57");var subQ1=sQuery(id+"F0.wireOp",EDGE,"E29");var subQ2=makeQuery(id+"F0.imprint","INTERSECT",VERTEX,{"derivedFrom":[subQ1,subQ0]});Q569=makeQuery(id+"F0.imprint","IMPRINT",FACE,{"disambiguationData":[TD([[makeQuery(id+"F0.imprint","IMPRINT",EDGE,{"disambiguationData":[TD([[subQ2,-1.0]])],"derivedFrom":subQ1}),1.0]])]});}
            var Q570;
            {var subQ5=sQuery(id+"F0.wireOp",EDGE,"E8");var subQ7=sQuery(id+"F0.wireOp",EDGE,"E39");var subQ8=makeQuery(id+"F0.imprint","INTERSECT",VERTEX,{"derivedFrom":[subQ5,subQ7]});Q570=makeQuery(id+"F0.imprint","IMPRINT",FACE,{"disambiguationData":[TD([[makeQuery(id+"F0.imprint","IMPRINT",EDGE,{"disambiguationData":[TD([[subQ8,-1.0]])],"derivedFrom":subQ5}),1.0]])]});}
            var Q571;
            {var subQ0=sQuery(id+"F0.wireOp",EDGE,"E32");var subQ1=sQuery(id+"F0.wireOp",EDGE,"E29");var subQ2=makeQuery(id+"F0.imprint","INTERSECT",VERTEX,{"derivedFrom":[subQ1,subQ0]});Q571=makeQuery(id+"F0.imprint","IMPRINT",FACE,{"disambiguationData":[TD([[makeQuery(id+"F0.imprint","IMPRINT",EDGE,{"disambiguationData":[TD([[subQ2,-1.0]])],"derivedFrom":subQ1}),-1.0]])]});}
            var Q572;
            {var subQ0=sQuery(id+"F0.wireOp",EDGE,"E32");var subQ1=sQuery(id+"F0.wireOp",EDGE,"E28");var subQ2=makeQuery(id+"F0.imprint","INTERSECT",VERTEX,{"derivedFrom":[subQ1,subQ0]});Q572=makeQuery(id+"F0.imprint","IMPRINT",FACE,{"disambiguationData":[TD([[makeQuery(id+"F0.imprint","IMPRINT",EDGE,{"disambiguationData":[TD([[subQ2,-1.0]])],"derivedFrom":subQ1}),-1.0]])]});}
            var Q573;
            {var subQ0=sQuery(id+"F0.wireOp",EDGE,"E57");var subQ1=sQuery(id+"F0.wireOp",EDGE,"E35");var subQ2=makeQuery(id+"F0.imprint","INTERSECT",VERTEX,{"derivedFrom":[subQ1,subQ0]});Q573=makeQuery(id+"F0.imprint","IMPRINT",FACE,{"disambiguationData":[TD([[makeQuery(id+"F0.imprint","IMPRINT",EDGE,{"disambiguationData":[TD([[subQ2,-1.0]])],"derivedFrom":subQ1}),1.0]])]});}
            var Q574;
            {var subQ5=sQuery(id+"F0.wireOp",EDGE,"E8");var subQ7=sQuery(id+"F0.wireOp",EDGE,"E41");var subQ9=makeQuery(id+"F0.imprint","INTERSECT",VERTEX,{"derivedFrom":[subQ5,subQ7]});Q574=makeQuery(id+"F0.imprint","IMPRINT",FACE,{"disambiguationData":[TD([[makeQuery(id+"F0.imprint","IMPRINT",EDGE,{"disambiguationData":[TD([[subQ9,-1.0]])],"derivedFrom":subQ5}),1.0]])]});}
            var Q575;
            {var subQ0=sQuery(id+"F0.wireOp",EDGE,"E41");var subQ1=sQuery(id+"F0.wireOp",EDGE,"E11");var subQ2=makeQuery(id+"F0.imprint","INTERSECT",VERTEX,{"derivedFrom":[subQ1,subQ0]});Q575=makeQuery(id+"F0.imprint","IMPRINT",FACE,{"disambiguationData":[TD([[makeQuery(id+"F0.imprint","IMPRINT",EDGE,{"disambiguationData":[TD([[subQ2,-1.0]])],"derivedFrom":subQ1}),1.0]])]});}
            var Q576;
            {var subQ0=sQuery(id+"F0.wireOp",EDGE,"E35");var subQ1=sQuery(id+"F0.wireOp",EDGE,"E29");var subQ2=makeQuery(id+"F0.imprint","INTERSECT",VERTEX,{"derivedFrom":[subQ1,subQ0]});Q576=makeQuery(id+"F0.imprint","IMPRINT",FACE,{"disambiguationData":[TD([[makeQuery(id+"F0.imprint","IMPRINT",EDGE,{"disambiguationData":[TD([[subQ2,-1.0]])],"derivedFrom":subQ1}),-1.0]])]});}
            var Q577;
            {var subQ0=sQuery(id+"F0.wireOp",EDGE,"E50");var subQ1=sQuery(id+"F0.wireOp",EDGE,"E34");var subQ2=makeQuery(id+"F0.imprint","INTERSECT",VERTEX,{"derivedFrom":[subQ1,subQ0]});Q577=makeQuery(id+"F0.imprint","IMPRINT",FACE,{"disambiguationData":[TD([[makeQuery(id+"F0.imprint","IMPRINT",EDGE,{"disambiguationData":[TD([[subQ2,-1.0]])],"derivedFrom":subQ1}),-1.0]])]});}
            var Q578;
            {var subQ0=sQuery(id+"F0.wireOp",EDGE,"E42");var subQ1=sQuery(id+"F0.wireOp",EDGE,"E6");var subQ2=makeQuery(id+"F0.imprint","INTERSECT",VERTEX,{"derivedFrom":[subQ1,subQ0]});Q578=makeQuery(id+"F0.imprint","IMPRINT",FACE,{"disambiguationData":[TD([[makeQuery(id+"F0.imprint","IMPRINT",EDGE,{"disambiguationData":[TD([[subQ2,-1.0]])],"derivedFrom":subQ1}),1.0]])]});}
            var Q579;
            {var subQ0=sQuery(id+"F0.wireOp",EDGE,"E42");var subQ1=sQuery(id+"F0.wireOp",EDGE,"E4");var subQ2=makeQuery(id+"F0.imprint","INTERSECT",VERTEX,{"derivedFrom":[subQ1,subQ0]});Q579=makeQuery(id+"F0.imprint","IMPRINT",FACE,{"disambiguationData":[TD([[makeQuery(id+"F0.imprint","IMPRINT",EDGE,{"disambiguationData":[TD([[subQ2,-1.0]])],"derivedFrom":subQ1}),-1.0]])]});}
            var Q580;
            {var subQ0=sQuery(id+"F0.wireOp",EDGE,"E35");var subQ1=sQuery(id+"F0.wireOp",EDGE,"E7");var subQ2=makeQuery(id+"F0.imprint","INTERSECT",VERTEX,{"derivedFrom":[subQ1,subQ0]});Q580=makeQuery(id+"F0.imprint","IMPRINT",FACE,{"disambiguationData":[TD([[makeQuery(id+"F0.imprint","IMPRINT",EDGE,{"disambiguationData":[TD([[subQ2,-1.0]])],"derivedFrom":subQ1}),-1.0]])]});}
            var Q581;
            {var subQ0=sQuery(id+"F0.wireOp",EDGE,"E13");var subQ1=sQuery(id+"F0.wireOp",EDGE,"E9");var subQ2=makeQuery(id+"F0.imprint","INTERSECT",VERTEX,{"derivedFrom":[subQ1,subQ0]});Q581=makeQuery(id+"F0.imprint","IMPRINT",FACE,{"disambiguationData":[TD([[makeQuery(id+"F0.imprint","IMPRINT",EDGE,{"disambiguationData":[TD([[subQ2,-1.0]])],"derivedFrom":subQ1}),1.0]])]});}
            var Q582;
            {var subQ0=sQuery(id+"F0.wireOp",EDGE,"E16");var subQ1=sQuery(id+"F0.wireOp",EDGE,"E1");var subQ2=makeQuery(id+"F0.imprint","INTERSECT",VERTEX,{"derivedFrom":[subQ1,subQ0]});Q582=makeQuery(id+"F0.imprint","IMPRINT",FACE,{"disambiguationData":[TD([[makeQuery(id+"F0.imprint","IMPRINT",EDGE,{"disambiguationData":[TD([[subQ2,-1.0]])],"derivedFrom":subQ1}),-1.0]])]});}
            var Q583;
            {var subQ0=sQuery(id+"F0.wireOp",EDGE,"E34");var subQ1=sQuery(id+"F0.wireOp",EDGE,"E29");var subQ2=makeQuery(id+"F0.imprint","INTERSECT",VERTEX,{"derivedFrom":[subQ1,subQ0]});Q583=makeQuery(id+"F0.imprint","IMPRINT",FACE,{"disambiguationData":[TD([[makeQuery(id+"F0.imprint","IMPRINT",EDGE,{"disambiguationData":[TD([[subQ2,-1.0]])],"derivedFrom":subQ1}),-1.0]])]});}
            var Q584;
            {var subQ0=sQuery(id+"F0.wireOp",EDGE,"E18");var subQ1=sQuery(id+"F0.wireOp",EDGE,"E2");var subQ2=makeQuery(id+"F0.imprint","INTERSECT",VERTEX,{"derivedFrom":[subQ1,subQ0]});Q584=makeQuery(id+"F0.imprint","IMPRINT",FACE,{"disambiguationData":[TD([[makeQuery(id+"F0.imprint","IMPRINT",EDGE,{"disambiguationData":[TD([[subQ2,-1.0]])],"derivedFrom":subQ1}),-1.0]])]});}
            var Q585;
            {var subQ0=sQuery(id+"F0.wireOp",EDGE,"E17");var subQ1=sQuery(id+"F0.wireOp",EDGE,"E11");var subQ2=makeQuery(id+"F0.imprint","INTERSECT",VERTEX,{"derivedFrom":[subQ1,subQ0]});Q585=makeQuery(id+"F0.imprint","IMPRINT",FACE,{"disambiguationData":[TD([[makeQuery(id+"F0.imprint","IMPRINT",EDGE,{"disambiguationData":[TD([[subQ2,-1.0]])],"derivedFrom":subQ1}),1.0]])]});}
            var Q586;
            {var subQ0=sQuery(id+"F0.wireOp",EDGE,"E10");var subQ1=sQuery(id+"F0.wireOp",EDGE,"E9");var subQ2=makeQuery(id+"F0.imprint","INTERSECT",VERTEX,{"derivedFrom":[subQ1,subQ0]});Q586=makeQuery(id+"F0.imprint","IMPRINT",FACE,{"disambiguationData":[TD([[makeQuery(id+"F0.imprint","IMPRINT",EDGE,{"disambiguationData":[TD([[subQ2,-1.0]])],"derivedFrom":subQ1}),-1.0]])]});}
            var Q587;
            {var subQ0=sQuery(id+"F0.wireOp",EDGE,"E55");var subQ1=sQuery(id+"F0.wireOp",EDGE,"E31");var subQ2=makeQuery(id+"F0.imprint","INTERSECT",VERTEX,{"derivedFrom":[subQ1,subQ0]});Q587=makeQuery(id+"F0.imprint","IMPRINT",FACE,{"disambiguationData":[TD([[makeQuery(id+"F0.imprint","IMPRINT",EDGE,{"disambiguationData":[TD([[subQ2,-1.0]])],"derivedFrom":subQ1}),-1.0]])]});}
            var Q588;
            {var subQ0=sQuery(id+"F0.wireOp",EDGE,"E34");var subQ1=sQuery(id+"F0.wireOp",EDGE,"E7");var subQ2=makeQuery(id+"F0.imprint","INTERSECT",VERTEX,{"derivedFrom":[subQ1,subQ0]});Q588=makeQuery(id+"F0.imprint","IMPRINT",FACE,{"disambiguationData":[TD([[makeQuery(id+"F0.imprint","IMPRINT",EDGE,{"disambiguationData":[TD([[subQ2,-1.0]])],"derivedFrom":subQ1}),-1.0]])]});}
            var Q589;
            {var subQ0=sQuery(id+"F0.wireOp",EDGE,"E42");var subQ1=sQuery(id+"F0.wireOp",EDGE,"E8");var subQ2=makeQuery(id+"F0.imprint","INTERSECT",VERTEX,{"derivedFrom":[subQ1,subQ0]});Q589=makeQuery(id+"F0.imprint","IMPRINT",FACE,{"disambiguationData":[TD([[makeQuery(id+"F0.imprint","IMPRINT",EDGE,{"disambiguationData":[TD([[subQ2,-1.0]])],"derivedFrom":subQ1}),1.0]])]});}
            var Q590;
            {var subQ0=sQuery(id+"F0.wireOp",EDGE,"E36");var subQ1=sQuery(id+"F0.wireOp",EDGE,"E8");var subQ2=makeQuery(id+"F0.imprint","INTERSECT",VERTEX,{"derivedFrom":[subQ1,subQ0]});Q590=makeQuery(id+"F0.imprint","IMPRINT",FACE,{"disambiguationData":[TD([[makeQuery(id+"F0.imprint","IMPRINT",EDGE,{"disambiguationData":[TD([[subQ2,-1.0]])],"derivedFrom":subQ1}),-1.0]])]});}
            var Q591;
            {var subQ0=sQuery(id+"F0.wireOp",EDGE,"E8");var subQ1=sQuery(id+"F0.wireOp",EDGE,"E5");var subQ2=makeQuery(id+"F0.imprint","INTERSECT",VERTEX,{"derivedFrom":[subQ1,subQ0]});Q591=makeQuery(id+"F0.imprint","IMPRINT",FACE,{"disambiguationData":[TD([[makeQuery(id+"F0.imprint","IMPRINT",EDGE,{"disambiguationData":[TD([[subQ2,-1.0]])],"derivedFrom":subQ1}),-1.0]])]});}
            var Q592;
            {var subQ0=sQuery(id+"F0.wireOp",EDGE,"E39");var subQ1=sQuery(id+"F0.wireOp",EDGE,"E5");var subQ2=makeQuery(id+"F0.imprint","INTERSECT",VERTEX,{"derivedFrom":[subQ1,subQ0]});Q592=makeQuery(id+"F0.imprint","IMPRINT",FACE,{"disambiguationData":[TD([[makeQuery(id+"F0.imprint","IMPRINT",EDGE,{"disambiguationData":[TD([[subQ2,-1.0]])],"derivedFrom":subQ1}),1.0]])]});}
            var Q593;
            {var subQ0=sQuery(id+"F0.wireOp",EDGE,"E18");var subQ1=sQuery(id+"F0.wireOp",EDGE,"E9");var subQ2=makeQuery(id+"F0.imprint","INTERSECT",VERTEX,{"derivedFrom":[subQ1,subQ0]});Q593=makeQuery(id+"F0.imprint","IMPRINT",FACE,{"disambiguationData":[TD([[makeQuery(id+"F0.imprint","IMPRINT",EDGE,{"disambiguationData":[TD([[subQ2,-1.0]])],"derivedFrom":subQ1}),1.0]])]});}
            var Q594;
            {var subQ0=sQuery(id+"F0.wireOp",EDGE,"E35");var subQ1=sQuery(id+"F0.wireOp",EDGE,"E34");var subQ2=makeQuery(id+"F0.imprint","INTERSECT",VERTEX,{"derivedFrom":[subQ1,subQ0]});Q594=makeQuery(id+"F0.imprint","IMPRINT",FACE,{"disambiguationData":[TD([[makeQuery(id+"F0.imprint","IMPRINT",EDGE,{"disambiguationData":[TD([[subQ2,-1.0]])],"derivedFrom":subQ1}),1.0]])]});}
            var Q595;
            {var subQ0=sQuery(id+"F0.wireOp",EDGE,"E39");var subQ1=sQuery(id+"F0.wireOp",EDGE,"E9");var subQ2=makeQuery(id+"F0.imprint","INTERSECT",VERTEX,{"derivedFrom":[subQ1,subQ0]});Q595=makeQuery(id+"F0.imprint","IMPRINT",FACE,{"disambiguationData":[TD([[makeQuery(id+"F0.imprint","IMPRINT",EDGE,{"disambiguationData":[TD([[subQ2,-1.0]])],"derivedFrom":subQ1}),-1.0]])]});}
            var Q596;
            {var subQ0=sQuery(id+"F0.wireOp",EDGE,"E36");var subQ1=sQuery(id+"F0.wireOp",EDGE,"E10");var subQ2=makeQuery(id+"F0.imprint","INTERSECT",VERTEX,{"derivedFrom":[subQ1,subQ0]});Q596=makeQuery(id+"F0.imprint","IMPRINT",FACE,{"disambiguationData":[TD([[makeQuery(id+"F0.imprint","IMPRINT",EDGE,{"disambiguationData":[TD([[subQ2,-1.0]])],"derivedFrom":subQ1}),-1.0]])]});}
            var Q597;
            {var subQ0=sQuery(id+"F0.wireOp",EDGE,"E40");var subQ1=sQuery(id+"F0.wireOp",EDGE,"E9");var subQ2=makeQuery(id+"F0.imprint","INTERSECT",VERTEX,{"derivedFrom":[subQ1,subQ0]});Q597=makeQuery(id+"F0.imprint","IMPRINT",FACE,{"disambiguationData":[TD([[makeQuery(id+"F0.imprint","IMPRINT",EDGE,{"disambiguationData":[TD([[subQ2,-1.0]])],"derivedFrom":subQ1}),-1.0]])]});}
            var Q598;
            {var subQ0=sQuery(id+"F0.wireOp",EDGE,"E40");var subQ1=sQuery(id+"F0.wireOp",EDGE,"E1");var subQ2=makeQuery(id+"F0.imprint","INTERSECT",VERTEX,{"derivedFrom":[subQ1,subQ0]});Q598=makeQuery(id+"F0.imprint","IMPRINT",FACE,{"disambiguationData":[TD([[makeQuery(id+"F0.imprint","IMPRINT",EDGE,{"disambiguationData":[TD([[subQ2,-1.0]])],"derivedFrom":subQ1}),-1.0]])]});}
            var Q599;
            {var subQ1=sQuery(id+"F0.wireOp",EDGE,"E30");var subQ5=sQuery(id+"F0.wireOp",EDGE,"E52");var subQ6=makeQuery(id+"F0.imprint","INTERSECT",VERTEX,{"derivedFrom":[subQ1,subQ5]});Q599=makeQuery(id+"F0.imprint","IMPRINT",FACE,{"disambiguationData":[TD([[makeQuery(id+"F0.imprint","IMPRINT",EDGE,{"disambiguationData":[TD([[subQ6,-1.0]])],"derivedFrom":subQ1}),1.0]])]});}
            var Q600;
            {var subQ0=sQuery(id+"F0.wireOp",EDGE,"E51");var subQ1=sQuery(id+"F0.wireOp",EDGE,"E30");var subQ2=makeQuery(id+"F0.imprint","INTERSECT",VERTEX,{"derivedFrom":[subQ1,subQ0]});Q600=makeQuery(id+"F0.imprint","IMPRINT",FACE,{"disambiguationData":[TD([[makeQuery(id+"F0.imprint","IMPRINT",EDGE,{"disambiguationData":[TD([[subQ2,-1.0]])],"derivedFrom":subQ1}),-1.0]])]});}
            var Q601;
            {var subQ0=sQuery(id+"F0.wireOp",EDGE,"E55");var subQ1=sQuery(id+"F0.wireOp",EDGE,"E30");var subQ2=makeQuery(id+"F0.imprint","INTERSECT",VERTEX,{"derivedFrom":[subQ1,subQ0]});Q601=makeQuery(id+"F0.imprint","IMPRINT",FACE,{"disambiguationData":[TD([[makeQuery(id+"F0.imprint","IMPRINT",EDGE,{"disambiguationData":[TD([[subQ2,-1.0]])],"derivedFrom":subQ1}),1.0]])]});}
            var Q602;
            {var subQ0=sQuery(id+"F0.wireOp",EDGE,"E42");var subQ1=sQuery(id+"F0.wireOp",EDGE,"E1");var subQ2=makeQuery(id+"F0.imprint","INTERSECT",VERTEX,{"derivedFrom":[subQ1,subQ0]});Q602=makeQuery(id+"F0.imprint","IMPRINT",FACE,{"disambiguationData":[TD([[makeQuery(id+"F0.imprint","IMPRINT",EDGE,{"disambiguationData":[TD([[subQ2,-1.0]])],"derivedFrom":subQ1}),1.0]])]});}
            var Q603;
            {var subQ0=sQuery(id+"F0.wireOp",EDGE,"E55");var subQ1=sQuery(id+"F0.wireOp",EDGE,"E31");var subQ2=makeQuery(id+"F0.imprint","INTERSECT",VERTEX,{"derivedFrom":[subQ1,subQ0]});Q603=makeQuery(id+"F0.imprint","IMPRINT",FACE,{"disambiguationData":[TD([[makeQuery(id+"F0.imprint","IMPRINT",EDGE,{"disambiguationData":[TD([[subQ2,-1.0]])],"derivedFrom":subQ1}),1.0]])]});}
            var Q604;
            {var subQ0=sQuery(id+"F0.wireOp",EDGE,"E49");var subQ1=sQuery(id+"F0.wireOp",EDGE,"E33");var subQ2=makeQuery(id+"F0.imprint","INTERSECT",VERTEX,{"derivedFrom":[subQ1,subQ0]});Q604=makeQuery(id+"F0.imprint","IMPRINT",FACE,{"disambiguationData":[TD([[makeQuery(id+"F0.imprint","IMPRINT",EDGE,{"disambiguationData":[TD([[subQ2,-1.0]])],"derivedFrom":subQ1}),-1.0]])]});}
            var Q605;
            {var subQ0=sQuery(id+"F0.wireOp",EDGE,"E57");var subQ1=sQuery(id+"F0.wireOp",EDGE,"E30");var subQ2=makeQuery(id+"F0.imprint","INTERSECT",VERTEX,{"derivedFrom":[subQ1,subQ0]});Q605=makeQuery(id+"F0.imprint","IMPRINT",FACE,{"disambiguationData":[TD([[makeQuery(id+"F0.imprint","IMPRINT",EDGE,{"disambiguationData":[TD([[subQ2,-1.0]])],"derivedFrom":subQ1}),-1.0]])]});}
            var Q606;
            {var subQ0=sQuery(id+"F0.wireOp",EDGE,"E52");var subQ1=sQuery(id+"F0.wireOp",EDGE,"E31");var subQ2=makeQuery(id+"F0.imprint","INTERSECT",VERTEX,{"derivedFrom":[subQ1,subQ0]});Q606=makeQuery(id+"F0.imprint","IMPRINT",FACE,{"disambiguationData":[TD([[makeQuery(id+"F0.imprint","IMPRINT",EDGE,{"disambiguationData":[TD([[subQ2,-1.0]])],"derivedFrom":subQ1}),1.0]])]});}
            var Q607;
            {var subQ0=sQuery(id+"F0.wireOp",EDGE,"E33");var subQ1=sQuery(id+"F0.wireOp",EDGE,"E30");var subQ2=makeQuery(id+"F0.imprint","INTERSECT",VERTEX,{"derivedFrom":[subQ1,subQ0]});Q607=makeQuery(id+"F0.imprint","IMPRINT",FACE,{"disambiguationData":[TD([[makeQuery(id+"F0.imprint","IMPRINT",EDGE,{"disambiguationData":[TD([[subQ2,-1.0]])],"derivedFrom":subQ1}),-1.0]])]});}
            var Q608;
            {var subQ0=sQuery(id+"F0.wireOp",EDGE,"E32");var subQ1=sQuery(id+"F0.wireOp",EDGE,"E30");var subQ2=makeQuery(id+"F0.imprint","INTERSECT",VERTEX,{"derivedFrom":[subQ1,subQ0]});Q608=makeQuery(id+"F0.imprint","IMPRINT",FACE,{"disambiguationData":[TD([[makeQuery(id+"F0.imprint","IMPRINT",EDGE,{"disambiguationData":[TD([[subQ2,-1.0]])],"derivedFrom":subQ1}),-1.0]])]});}
            var Q609;
            {var subQ0=sQuery(id+"F0.wireOp",EDGE,"E50");var subQ1=sQuery(id+"F0.wireOp",EDGE,"E33");var subQ2=makeQuery(id+"F0.imprint","INTERSECT",VERTEX,{"derivedFrom":[subQ1,subQ0]});Q609=makeQuery(id+"F0.imprint","IMPRINT",FACE,{"disambiguationData":[TD([[makeQuery(id+"F0.imprint","IMPRINT",EDGE,{"disambiguationData":[TD([[subQ2,-1.0]])],"derivedFrom":subQ1}),-1.0]])]});}
            var Q610;
            {var subQ0=sQuery(id+"F0.wireOp",EDGE,"E41");var subQ1=sQuery(id+"F0.wireOp",EDGE,"E10");var subQ2=makeQuery(id+"F0.imprint","INTERSECT",VERTEX,{"derivedFrom":[subQ1,subQ0]});Q610=makeQuery(id+"F0.imprint","IMPRINT",FACE,{"disambiguationData":[TD([[makeQuery(id+"F0.imprint","IMPRINT",EDGE,{"disambiguationData":[TD([[subQ2,-1.0]])],"derivedFrom":subQ1}),1.0]])]});}
            var Q611;
            {var subQ0=sQuery(id+"F0.wireOp",EDGE,"E33");var subQ1=sQuery(id+"F0.wireOp",EDGE,"E8");var subQ2=makeQuery(id+"F0.imprint","INTERSECT",VERTEX,{"derivedFrom":[subQ1,subQ0]});Q611=makeQuery(id+"F0.imprint","IMPRINT",FACE,{"disambiguationData":[TD([[makeQuery(id+"F0.imprint","IMPRINT",EDGE,{"disambiguationData":[TD([[subQ2,-1.0]])],"derivedFrom":subQ1}),-1.0]])]});}
            var Q612;
            {var subQ0=sQuery(id+"F0.wireOp",EDGE,"E38");var subQ1=sQuery(id+"F0.wireOp",EDGE,"E8");var subQ2=makeQuery(id+"F0.imprint","INTERSECT",VERTEX,{"derivedFrom":[subQ1,subQ0]});Q612=makeQuery(id+"F0.imprint","IMPRINT",FACE,{"disambiguationData":[TD([[makeQuery(id+"F0.imprint","IMPRINT",EDGE,{"disambiguationData":[TD([[subQ2,-1.0]])],"derivedFrom":subQ1}),-1.0]])]});}
            var Q613;
            {var subQ0=sQuery(id+"F0.wireOp",EDGE,"E54");var subQ1=sQuery(id+"F0.wireOp",EDGE,"E35");var subQ2=makeQuery(id+"F0.imprint","INTERSECT",VERTEX,{"derivedFrom":[subQ1,subQ0]});Q613=makeQuery(id+"F0.imprint","IMPRINT",FACE,{"disambiguationData":[TD([[makeQuery(id+"F0.imprint","IMPRINT",EDGE,{"disambiguationData":[TD([[subQ2,-1.0]])],"derivedFrom":subQ1}),1.0]])]});}
            var Q614;
            {var subQ0=sQuery(id+"F0.wireOp",EDGE,"E39");var subQ1=sQuery(id+"F0.wireOp",EDGE,"E12");var subQ2=makeQuery(id+"F0.imprint","INTERSECT",VERTEX,{"derivedFrom":[subQ1,subQ0]});Q614=makeQuery(id+"F0.imprint","IMPRINT",FACE,{"disambiguationData":[TD([[makeQuery(id+"F0.imprint","IMPRINT",EDGE,{"disambiguationData":[TD([[subQ2,-1.0]])],"derivedFrom":subQ1}),1.0]])]});}
            var Q615;
            {var subQ0=sQuery(id+"F0.wireOp",EDGE,"E54");var subQ1=sQuery(id+"F0.wireOp",EDGE,"E30");var subQ2=makeQuery(id+"F0.imprint","INTERSECT",VERTEX,{"derivedFrom":[subQ1,subQ0]});Q615=makeQuery(id+"F0.imprint","IMPRINT",FACE,{"disambiguationData":[TD([[makeQuery(id+"F0.imprint","IMPRINT",EDGE,{"disambiguationData":[TD([[subQ2,-1.0]])],"derivedFrom":subQ1}),-1.0]])]});}
            var Q616;
            {var subQ0=sQuery(id+"F0.wireOp",EDGE,"E38");var subQ1=sQuery(id+"F0.wireOp",EDGE,"E8");var subQ2=makeQuery(id+"F0.imprint","INTERSECT",VERTEX,{"derivedFrom":[subQ1,subQ0]});Q616=makeQuery(id+"F0.imprint","IMPRINT",FACE,{"disambiguationData":[TD([[makeQuery(id+"F0.imprint","IMPRINT",EDGE,{"disambiguationData":[TD([[subQ2,-1.0]])],"derivedFrom":subQ1}),1.0]])]});}
            var Q617;
            {var subQ0=sQuery(id+"F0.wireOp",EDGE,"E52");var subQ1=sQuery(id+"F0.wireOp",EDGE,"E34");var subQ2=makeQuery(id+"F0.imprint","INTERSECT",VERTEX,{"derivedFrom":[subQ1,subQ0]});Q617=makeQuery(id+"F0.imprint","IMPRINT",FACE,{"disambiguationData":[TD([[makeQuery(id+"F0.imprint","IMPRINT",EDGE,{"disambiguationData":[TD([[subQ2,-1.0]])],"derivedFrom":subQ1}),-1.0]])]});}
            var Q618;
            {var subQ0=sQuery(id+"F0.wireOp",EDGE,"E42");var subQ1=sQuery(id+"F0.wireOp",EDGE,"E1");var subQ2=makeQuery(id+"F0.imprint","INTERSECT",VERTEX,{"derivedFrom":[subQ1,subQ0]});Q618=makeQuery(id+"F0.imprint","IMPRINT",FACE,{"disambiguationData":[TD([[makeQuery(id+"F0.imprint","IMPRINT",EDGE,{"disambiguationData":[TD([[subQ2,-1.0]])],"derivedFrom":subQ1}),-1.0]])]});}
            var Q619;
            {var subQ0=sQuery(id+"F0.wireOp",EDGE,"E11");var subQ1=sQuery(id+"F0.wireOp",EDGE,"E10");var subQ2=makeQuery(id+"F0.imprint","INTERSECT",VERTEX,{"derivedFrom":[subQ1,subQ0]});Q619=makeQuery(id+"F0.imprint","IMPRINT",FACE,{"disambiguationData":[TD([[makeQuery(id+"F0.imprint","IMPRINT",EDGE,{"disambiguationData":[TD([[subQ2,-1.0]])],"derivedFrom":subQ1}),1.0]])]});}
            var Q620;
            {var subQ0=sQuery(id+"F0.wireOp",EDGE,"E38");var subQ1=sQuery(id+"F0.wireOp",EDGE,"E9");var subQ2=makeQuery(id+"F0.imprint","INTERSECT",VERTEX,{"derivedFrom":[subQ1,subQ0]});Q620=makeQuery(id+"F0.imprint","IMPRINT",FACE,{"disambiguationData":[TD([[makeQuery(id+"F0.imprint","IMPRINT",EDGE,{"disambiguationData":[TD([[subQ2,-1.0]])],"derivedFrom":subQ1}),-1.0]])]});}
            var Q621;
            {var subQ5=sQuery(id+"F0.wireOp",EDGE,"E54");var subQ6=sQuery(id+"F0.wireOp",EDGE,"E30");var subQ7=makeQuery(id+"F0.imprint","INTERSECT",VERTEX,{"derivedFrom":[subQ6,subQ5]});Q621=makeQuery(id+"F0.imprint","IMPRINT",FACE,{"disambiguationData":[TD([[makeQuery(id+"F0.imprint","IMPRINT",EDGE,{"disambiguationData":[TD([[subQ7,-1.0]])],"derivedFrom":subQ6}),1.0]])]});}
            var Q622;
            {var subQ0=sQuery(id+"F0.wireOp",EDGE,"E52");var subQ1=sQuery(id+"F0.wireOp",EDGE,"E46");var subQ2=makeQuery(id+"F0.imprint","INTERSECT",VERTEX,{"derivedFrom":[subQ1,subQ0]});Q622=makeQuery(id+"F0.imprint","IMPRINT",FACE,{"disambiguationData":[TD([[makeQuery(id+"F0.imprint","IMPRINT",EDGE,{"disambiguationData":[TD([[subQ2,-1.0]])],"derivedFrom":subQ1}),-1.0]])]});}
            var Q623;
            {var subQ0=sQuery(id+"F0.wireOp",EDGE,"E25");var subQ1=sQuery(id+"F0.wireOp",EDGE,"E15");var subQ2=makeQuery(id+"F0.imprint","INTERSECT",VERTEX,{"derivedFrom":[subQ1,subQ0]});Q623=makeQuery(id+"F0.imprint","IMPRINT",FACE,{"disambiguationData":[TD([[makeQuery(id+"F0.imprint","IMPRINT",EDGE,{"disambiguationData":[TD([[subQ2,-1.0]])],"derivedFrom":subQ1}),-1.0]])]});}
            var Q624;
            {var subQ3=sQuery(id+"F0.wireOp",EDGE,"E23");var subQ7=sQuery(id+"F0.wireOp",EDGE,"E1");var subQ9=makeQuery(id+"F0.imprint","INTERSECT",VERTEX,{"derivedFrom":[subQ7,subQ3]});Q624=makeQuery(id+"F0.imprint","IMPRINT",FACE,{"disambiguationData":[TD([[makeQuery(id+"F0.imprint","IMPRINT",EDGE,{"disambiguationData":[TD([[subQ9,-1.0]])],"derivedFrom":subQ7}),1.0]])]});}
            var Q625;
            {var subQ1=sQuery(id+"F0.wireOp",EDGE,"E20");var subQ7=sQuery(id+"F0.wireOp",EDGE,"E45");var subQ11=makeQuery(id+"F0.imprint","INTERSECT",VERTEX,{"derivedFrom":[subQ1,subQ7]});Q625=makeQuery(id+"F0.imprint","IMPRINT",FACE,{"disambiguationData":[TD([[makeQuery(id+"F0.imprint","IMPRINT",EDGE,{"disambiguationData":[TD([[subQ11,-1.0]])],"derivedFrom":subQ1}),-1.0]])]});}
            var Q626;
            {var subQ0=sQuery(id+"F0.wireOp",EDGE,"E40");var subQ1=sQuery(id+"F0.wireOp",EDGE,"E30");var subQ2=makeQuery(id+"F0.imprint","INTERSECT",VERTEX,{"derivedFrom":[subQ1,subQ0]});Q626=makeQuery(id+"F0.imprint","IMPRINT",FACE,{"disambiguationData":[TD([[makeQuery(id+"F0.imprint","IMPRINT",EDGE,{"disambiguationData":[TD([[subQ2,-1.0]])],"derivedFrom":subQ1}),-1.0]])]});}
            var Q627;
            {var subQ0=sQuery(id+"F0.wireOp",EDGE,"E40");var subQ1=sQuery(id+"F0.wireOp",EDGE,"E29");var subQ2=makeQuery(id+"F0.imprint","INTERSECT",VERTEX,{"derivedFrom":[subQ1,subQ0]});Q627=makeQuery(id+"F0.imprint","IMPRINT",FACE,{"disambiguationData":[TD([[makeQuery(id+"F0.imprint","IMPRINT",EDGE,{"disambiguationData":[TD([[subQ2,-1.0]])],"derivedFrom":subQ1}),-1.0]])]});}
            var Q628;
            {var subQ0=sQuery(id+"F0.wireOp",EDGE,"E27");var subQ1=sQuery(id+"F0.wireOp",EDGE,"E15");var subQ2=makeQuery(id+"F0.imprint","INTERSECT",VERTEX,{"derivedFrom":[subQ1,subQ0]});Q628=makeQuery(id+"F0.imprint","IMPRINT",FACE,{"disambiguationData":[TD([[makeQuery(id+"F0.imprint","IMPRINT",EDGE,{"disambiguationData":[TD([[subQ2,-1.0]])],"derivedFrom":subQ1}),-1.0]])]});}
            var Q629;
            {var subQ0=sQuery(id+"F0.wireOp",EDGE,"E37");var subQ1=sQuery(id+"F0.wireOp",EDGE,"E30");var subQ2=makeQuery(id+"F0.imprint","INTERSECT",VERTEX,{"derivedFrom":[subQ1,subQ0]});Q629=makeQuery(id+"F0.imprint","IMPRINT",FACE,{"disambiguationData":[TD([[makeQuery(id+"F0.imprint","IMPRINT",EDGE,{"disambiguationData":[TD([[subQ2,-1.0]])],"derivedFrom":subQ1}),-1.0]])]});}
            var Q630;
            {var subQ0=sQuery(id+"F0.wireOp",EDGE,"E55");var subQ1=sQuery(id+"F0.wireOp",EDGE,"E44");var subQ2=makeQuery(id+"F0.imprint","INTERSECT",VERTEX,{"derivedFrom":[subQ1,subQ0]});Q630=makeQuery(id+"F0.imprint","IMPRINT",FACE,{"disambiguationData":[TD([[makeQuery(id+"F0.imprint","IMPRINT",EDGE,{"disambiguationData":[TD([[subQ2,-1.0]])],"derivedFrom":subQ1}),-1.0]])]});}
            var Q631;
            {var subQ0=sQuery(id+"F0.wireOp",EDGE,"E3");var subQ1=sQuery(id+"F0.wireOp",EDGE,"E1");var subQ2=makeQuery(id+"F0.imprint","INTERSECT",VERTEX,{"derivedFrom":[subQ1,subQ0]});Q631=makeQuery(id+"F0.imprint","IMPRINT",FACE,{"disambiguationData":[TD([[makeQuery(id+"F0.imprint","IMPRINT",EDGE,{"disambiguationData":[TD([[subQ2,-1.0]])],"derivedFrom":subQ1}),1.0]])]});}
            var Q632;
            {var subQ3=sQuery(id+"F0.wireOp",EDGE,"E51");var subQ6=sQuery(id+"F0.wireOp",EDGE,"E22");var subQ11=makeQuery(id+"F0.imprint","INTERSECT",VERTEX,{"derivedFrom":[subQ6,subQ3]});Q632=makeQuery(id+"F0.imprint","IMPRINT",FACE,{"disambiguationData":[TD([[makeQuery(id+"F0.imprint","IMPRINT",EDGE,{"disambiguationData":[TD([[subQ11,-1.0]])],"derivedFrom":subQ6}),-1.0]])]});}
            var Q633;
            {var subQ0=sQuery(id+"F0.wireOp",EDGE,"E49");var subQ1=sQuery(id+"F0.wireOp",EDGE,"E22");var subQ2=makeQuery(id+"F0.imprint","INTERSECT",VERTEX,{"derivedFrom":[subQ1,subQ0]});Q633=makeQuery(id+"F0.imprint","IMPRINT",FACE,{"disambiguationData":[TD([[makeQuery(id+"F0.imprint","IMPRINT",EDGE,{"disambiguationData":[TD([[subQ2,-1.0]])],"derivedFrom":subQ1}),-1.0]])]});}
            var Q634;
            {var subQ0=sQuery(id+"F0.wireOp",EDGE,"E39");var subQ1=sQuery(id+"F0.wireOp",EDGE,"E29");var subQ2=makeQuery(id+"F0.imprint","INTERSECT",VERTEX,{"derivedFrom":[subQ1,subQ0]});Q634=makeQuery(id+"F0.imprint","IMPRINT",FACE,{"disambiguationData":[TD([[makeQuery(id+"F0.imprint","IMPRINT",EDGE,{"disambiguationData":[TD([[subQ2,-1.0]])],"derivedFrom":subQ1}),-1.0]])]});}
            var Q635;
            {var subQ0=sQuery(id+"F0.wireOp",EDGE,"E50");var subQ1=sQuery(id+"F0.wireOp",EDGE,"E21");var subQ2=makeQuery(id+"F0.imprint","INTERSECT",VERTEX,{"derivedFrom":[subQ1,subQ0]});Q635=makeQuery(id+"F0.imprint","IMPRINT",FACE,{"disambiguationData":[TD([[makeQuery(id+"F0.imprint","IMPRINT",EDGE,{"disambiguationData":[TD([[subQ2,-1.0]])],"derivedFrom":subQ1}),-1.0]])]});}
            var Q636;
            {var subQ1=sQuery(id+"F0.wireOp",EDGE,"E29");var subQ3=sQuery(id+"F0.wireOp",EDGE,"E45");var subQ4=makeQuery(id+"F0.imprint","INTERSECT",VERTEX,{"derivedFrom":[subQ1,subQ3]});Q636=makeQuery(id+"F0.imprint","IMPRINT",FACE,{"disambiguationData":[TD([[makeQuery(id+"F0.imprint","IMPRINT",EDGE,{"disambiguationData":[TD([[subQ4,1.0]])],"derivedFrom":subQ3}),1.0]])]});}
            var Q637;
            {var subQ5=sQuery(id+"F0.wireOp",EDGE,"E46");var subQ6=sQuery(id+"F0.wireOp",EDGE,"E29");var subQ7=makeQuery(id+"F0.imprint","INTERSECT",VERTEX,{"derivedFrom":[subQ6,subQ5]});Q637=makeQuery(id+"F0.imprint","IMPRINT",FACE,{"disambiguationData":[TD([[makeQuery(id+"F0.imprint","IMPRINT",EDGE,{"disambiguationData":[TD([[subQ7,-1.0]])],"derivedFrom":subQ6}),-1.0]])]});}
            var Q638;
            {var subQ0=sQuery(id+"F0.wireOp",EDGE,"E42");var subQ1=sQuery(id+"F0.wireOp",EDGE,"E30");var subQ2=makeQuery(id+"F0.imprint","INTERSECT",VERTEX,{"derivedFrom":[subQ1,subQ0]});Q638=makeQuery(id+"F0.imprint","IMPRINT",FACE,{"disambiguationData":[TD([[makeQuery(id+"F0.imprint","IMPRINT",EDGE,{"disambiguationData":[TD([[subQ2,-1.0]])],"derivedFrom":subQ1}),-1.0]])]});}
            var Q639;
            {var subQ1=sQuery(id+"F0.wireOp",EDGE,"E28");var subQ5=sQuery(id+"F0.wireOp",EDGE,"E38");var subQ6=makeQuery(id+"F0.imprint","INTERSECT",VERTEX,{"derivedFrom":[subQ1,subQ5]});Q639=makeQuery(id+"F0.imprint","IMPRINT",FACE,{"disambiguationData":[TD([[makeQuery(id+"F0.imprint","IMPRINT",EDGE,{"disambiguationData":[TD([[subQ6,-1.0]])],"derivedFrom":subQ1}),1.0]])]});}
            var Q640;
            {var subQ0=sQuery(id+"F0.wireOp",EDGE,"E39");var subQ1=sQuery(id+"F0.wireOp",EDGE,"E31");var subQ2=makeQuery(id+"F0.imprint","INTERSECT",VERTEX,{"derivedFrom":[subQ1,subQ0]});Q640=makeQuery(id+"F0.imprint","IMPRINT",FACE,{"disambiguationData":[TD([[makeQuery(id+"F0.imprint","IMPRINT",EDGE,{"disambiguationData":[TD([[subQ2,-1.0]])],"derivedFrom":subQ1}),-1.0]])]});}
            var Q641;
            {var subQ0=sQuery(id+"F0.wireOp",EDGE,"E40");var subQ1=sQuery(id+"F0.wireOp",EDGE,"E28");var subQ2=makeQuery(id+"F0.imprint","INTERSECT",VERTEX,{"derivedFrom":[subQ1,subQ0]});Q641=makeQuery(id+"F0.imprint","IMPRINT",FACE,{"disambiguationData":[TD([[makeQuery(id+"F0.imprint","IMPRINT",EDGE,{"disambiguationData":[TD([[subQ2,-1.0]])],"derivedFrom":subQ1}),-1.0]])]});}
            var Q642;
            {var subQ0=sQuery(id+"F0.wireOp",EDGE,"E41");var subQ1=sQuery(id+"F0.wireOp",EDGE,"E28");var subQ2=makeQuery(id+"F0.imprint","INTERSECT",VERTEX,{"derivedFrom":[subQ1,subQ0]});Q642=makeQuery(id+"F0.imprint","IMPRINT",FACE,{"disambiguationData":[TD([[makeQuery(id+"F0.imprint","IMPRINT",EDGE,{"disambiguationData":[TD([[subQ2,-1.0]])],"derivedFrom":subQ1}),-1.0]])]});}
            var Q643;
            {var subQ0=sQuery(id+"F0.wireOp",EDGE,"E25");var subQ1=sQuery(id+"F0.wireOp",EDGE,"E19");var subQ2=makeQuery(id+"F0.imprint","INTERSECT",VERTEX,{"derivedFrom":[subQ1,subQ0]});Q643=makeQuery(id+"F0.imprint","IMPRINT",FACE,{"disambiguationData":[TD([[makeQuery(id+"F0.imprint","IMPRINT",EDGE,{"disambiguationData":[TD([[subQ2,-1.0]])],"derivedFrom":subQ1}),-1.0]])]});}
            var Q644;
            {var subQ0=sQuery(id+"F0.wireOp",EDGE,"E52");var subQ1=sQuery(id+"F0.wireOp",EDGE,"E25");var subQ2=makeQuery(id+"F0.imprint","INTERSECT",VERTEX,{"derivedFrom":[subQ1,subQ0]});Q644=makeQuery(id+"F0.imprint","IMPRINT",FACE,{"disambiguationData":[TD([[makeQuery(id+"F0.imprint","IMPRINT",EDGE,{"disambiguationData":[TD([[subQ2,-1.0]])],"derivedFrom":subQ1}),-1.0]])]});}
            var Q645;
            {var subQ0=sQuery(id+"F0.wireOp",EDGE,"E36");var subQ1=sQuery(id+"F0.wireOp",EDGE,"E29");var subQ2=makeQuery(id+"F0.imprint","INTERSECT",VERTEX,{"derivedFrom":[subQ1,subQ0]});Q645=makeQuery(id+"F0.imprint","IMPRINT",FACE,{"disambiguationData":[TD([[makeQuery(id+"F0.imprint","IMPRINT",EDGE,{"disambiguationData":[TD([[subQ2,-1.0]])],"derivedFrom":subQ1}),-1.0]])]});}
            var Q646;
            {var subQ0=sQuery(id+"F0.wireOp",EDGE,"E50");var subQ1=sQuery(id+"F0.wireOp",EDGE,"E24");var subQ2=makeQuery(id+"F0.imprint","INTERSECT",VERTEX,{"derivedFrom":[subQ1,subQ0]});Q646=makeQuery(id+"F0.imprint","IMPRINT",FACE,{"disambiguationData":[TD([[makeQuery(id+"F0.imprint","IMPRINT",EDGE,{"disambiguationData":[TD([[subQ2,-1.0]])],"derivedFrom":subQ1}),-1.0]])]});}
            var Q647;
            {var subQ0=sQuery(id+"F0.wireOp",EDGE,"E41");var subQ1=sQuery(id+"F0.wireOp",EDGE,"E30");var subQ2=makeQuery(id+"F0.imprint","INTERSECT",VERTEX,{"derivedFrom":[subQ1,subQ0]});Q647=makeQuery(id+"F0.imprint","IMPRINT",FACE,{"disambiguationData":[TD([[makeQuery(id+"F0.imprint","IMPRINT",EDGE,{"disambiguationData":[TD([[subQ2,-1.0]])],"derivedFrom":subQ1}),-1.0]])]});}
            var Q648;
            {var subQ0=sQuery(id+"F0.wireOp",EDGE,"E51");var subQ1=sQuery(id+"F0.wireOp",EDGE,"E24");var subQ2=makeQuery(id+"F0.imprint","INTERSECT",VERTEX,{"derivedFrom":[subQ1,subQ0]});Q648=makeQuery(id+"F0.imprint","IMPRINT",FACE,{"disambiguationData":[TD([[makeQuery(id+"F0.imprint","IMPRINT",EDGE,{"disambiguationData":[TD([[subQ2,-1.0]])],"derivedFrom":subQ1}),-1.0]])]});}
            var Q649;
            {var subQ3=sQuery(id+"F0.wireOp",EDGE,"E49");var subQ9=sQuery(id+"F0.wireOp",EDGE,"E21");var subQ10=makeQuery(id+"F0.imprint","INTERSECT",VERTEX,{"derivedFrom":[subQ9,subQ3]});Q649=makeQuery(id+"F0.imprint","IMPRINT",FACE,{"disambiguationData":[TD([[makeQuery(id+"F0.imprint","IMPRINT",EDGE,{"disambiguationData":[TD([[subQ10,-1.0]])],"derivedFrom":subQ9}),-1.0]])]});}
            var Q650;
            {var subQ1=sQuery(id+"F0.wireOp",EDGE,"E28");var subQ7=sQuery(id+"F0.wireOp",EDGE,"E39");var subQ8=makeQuery(id+"F0.imprint","INTERSECT",VERTEX,{"derivedFrom":[subQ1,subQ7]});Q650=makeQuery(id+"F0.imprint","IMPRINT",FACE,{"disambiguationData":[TD([[makeQuery(id+"F0.imprint","IMPRINT",EDGE,{"disambiguationData":[TD([[subQ8,-1.0]])],"derivedFrom":subQ1}),1.0]])]});}
            var Q651;
            {var subQ0=sQuery(id+"F0.wireOp",EDGE,"E57");var subQ1=sQuery(id+"F0.wireOp",EDGE,"E26");var subQ2=makeQuery(id+"F0.imprint","INTERSECT",VERTEX,{"derivedFrom":[subQ1,subQ0]});Q651=makeQuery(id+"F0.imprint","IMPRINT",FACE,{"disambiguationData":[TD([[makeQuery(id+"F0.imprint","IMPRINT",EDGE,{"disambiguationData":[TD([[subQ2,-1.0]])],"derivedFrom":subQ1}),-1.0]])]});}
            var Q652;
            {var subQ3=sQuery(id+"F0.wireOp",EDGE,"E51");var subQ9=sQuery(id+"F0.wireOp",EDGE,"E23");var subQ11=makeQuery(id+"F0.imprint","INTERSECT",VERTEX,{"derivedFrom":[subQ9,subQ3]});Q652=makeQuery(id+"F0.imprint","IMPRINT",FACE,{"disambiguationData":[TD([[makeQuery(id+"F0.imprint","IMPRINT",EDGE,{"disambiguationData":[TD([[subQ11,-1.0]])],"derivedFrom":subQ9}),-1.0]])]});}
            var Q653;
            {var subQ0=sQuery(id+"F0.wireOp",EDGE,"E53");var subQ1=sQuery(id+"F0.wireOp",EDGE,"E46");var subQ2=makeQuery(id+"F0.imprint","INTERSECT",VERTEX,{"derivedFrom":[subQ1,subQ0]});Q653=makeQuery(id+"F0.imprint","IMPRINT",FACE,{"disambiguationData":[TD([[makeQuery(id+"F0.imprint","IMPRINT",EDGE,{"disambiguationData":[TD([[subQ2,-1.0]])],"derivedFrom":subQ1}),-1.0]])]});}
            var Q654;
            {var subQ0=sQuery(id+"F0.wireOp",EDGE,"E42");var subQ1=sQuery(id+"F0.wireOp",EDGE,"E29");var subQ2=makeQuery(id+"F0.imprint","INTERSECT",VERTEX,{"derivedFrom":[subQ1,subQ0]});Q654=makeQuery(id+"F0.imprint","IMPRINT",FACE,{"disambiguationData":[TD([[makeQuery(id+"F0.imprint","IMPRINT",EDGE,{"disambiguationData":[TD([[subQ2,-1.0]])],"derivedFrom":subQ1}),-1.0]])]});}
            var Q655;
            {var subQ0=sQuery(id+"F0.wireOp",EDGE,"E25");var subQ1=sQuery(id+"F0.wireOp",EDGE,"E16");var subQ2=makeQuery(id+"F0.imprint","INTERSECT",VERTEX,{"derivedFrom":[subQ1,subQ0]});Q655=makeQuery(id+"F0.imprint","IMPRINT",FACE,{"disambiguationData":[TD([[makeQuery(id+"F0.imprint","IMPRINT",EDGE,{"disambiguationData":[TD([[subQ2,-1.0]])],"derivedFrom":subQ1}),-1.0]])]});}
            var Q656;
            {var subQ0=sQuery(id+"F0.wireOp",EDGE,"E39");var subQ1=sQuery(id+"F0.wireOp",EDGE,"E30");var subQ2=makeQuery(id+"F0.imprint","INTERSECT",VERTEX,{"derivedFrom":[subQ1,subQ0]});Q656=makeQuery(id+"F0.imprint","IMPRINT",FACE,{"disambiguationData":[TD([[makeQuery(id+"F0.imprint","IMPRINT",EDGE,{"disambiguationData":[TD([[subQ2,-1.0]])],"derivedFrom":subQ1}),-1.0]])]});}
            var Q657;
            {var subQ5=sQuery(id+"F0.wireOp",EDGE,"E12");var subQ6=sQuery(id+"F0.wireOp",EDGE,"E11");var subQ7=makeQuery(id+"F0.imprint","INTERSECT",VERTEX,{"derivedFrom":[subQ6,subQ5]});Q657=makeQuery(id+"F0.imprint","IMPRINT",FACE,{"disambiguationData":[TD([[makeQuery(id+"F0.imprint","IMPRINT",EDGE,{"disambiguationData":[TD([[subQ7,-1.0]])],"derivedFrom":subQ6}),-1.0]])]});}
            var Q658;
            {var subQ0=sQuery(id+"F0.wireOp",EDGE,"E56");var subQ1=sQuery(id+"F0.wireOp",EDGE,"E26");var subQ2=makeQuery(id+"F0.imprint","INTERSECT",VERTEX,{"derivedFrom":[subQ1,subQ0]});Q658=makeQuery(id+"F0.imprint","IMPRINT",FACE,{"disambiguationData":[TD([[makeQuery(id+"F0.imprint","IMPRINT",EDGE,{"disambiguationData":[TD([[subQ2,-1.0]])],"derivedFrom":subQ1}),-1.0]])]});}
            var Q659;
            {var subQ0=sQuery(id+"F0.wireOp",EDGE,"E54");var subQ1=sQuery(id+"F0.wireOp",EDGE,"E25");var subQ2=makeQuery(id+"F0.imprint","INTERSECT",VERTEX,{"derivedFrom":[subQ1,subQ0]});Q659=makeQuery(id+"F0.imprint","IMPRINT",FACE,{"disambiguationData":[TD([[makeQuery(id+"F0.imprint","IMPRINT",EDGE,{"disambiguationData":[TD([[subQ2,-1.0]])],"derivedFrom":subQ1}),-1.0]])]});}
            var Q660;
            {var subQ0=sQuery(id+"F0.wireOp",EDGE,"E46");var subQ1=sQuery(id+"F0.wireOp",EDGE,"E21");var subQ2=makeQuery(id+"F0.imprint","INTERSECT",VERTEX,{"derivedFrom":[subQ1,subQ0]});Q660=makeQuery(id+"F0.imprint","IMPRINT",FACE,{"disambiguationData":[TD([[makeQuery(id+"F0.imprint","IMPRINT",EDGE,{"disambiguationData":[TD([[subQ2,-1.0]])],"derivedFrom":subQ1}),-1.0]])]});}
            var Q661;
            {var subQ0=sQuery(id+"F0.wireOp",EDGE,"E26");var subQ1=sQuery(id+"F0.wireOp",EDGE,"E16");var subQ2=makeQuery(id+"F0.imprint","INTERSECT",VERTEX,{"derivedFrom":[subQ1,subQ0]});Q661=makeQuery(id+"F0.imprint","IMPRINT",FACE,{"disambiguationData":[TD([[makeQuery(id+"F0.imprint","IMPRINT",EDGE,{"disambiguationData":[TD([[subQ2,-1.0]])],"derivedFrom":subQ1}),-1.0]])]});}
            var Q662;
            {var subQ1=sQuery(id+"F0.wireOp",EDGE,"E19");var subQ5=sQuery(id+"F0.wireOp",EDGE,"E47");var subQ6=makeQuery(id+"F0.imprint","INTERSECT",VERTEX,{"derivedFrom":[subQ1,subQ5]});Q662=makeQuery(id+"F0.imprint","IMPRINT",FACE,{"disambiguationData":[TD([[makeQuery(id+"F0.imprint","IMPRINT",EDGE,{"disambiguationData":[TD([[subQ6,-1.0]])],"derivedFrom":subQ1}),-1.0]])]});}
            var Q663;
            {var subQ0=sQuery(id+"F0.wireOp",EDGE,"E40");var subQ1=sQuery(id+"F0.wireOp",EDGE,"E31");var subQ2=makeQuery(id+"F0.imprint","INTERSECT",VERTEX,{"derivedFrom":[subQ1,subQ0]});Q663=makeQuery(id+"F0.imprint","IMPRINT",FACE,{"disambiguationData":[TD([[makeQuery(id+"F0.imprint","IMPRINT",EDGE,{"disambiguationData":[TD([[subQ2,-1.0]])],"derivedFrom":subQ1}),-1.0]])]});}
            var Q664;
            {var subQ0=sQuery(id+"F0.wireOp",EDGE,"E27");var subQ1=sQuery(id+"F0.wireOp",EDGE,"E16");var subQ2=makeQuery(id+"F0.imprint","INTERSECT",VERTEX,{"derivedFrom":[subQ1,subQ0]});Q664=makeQuery(id+"F0.imprint","IMPRINT",FACE,{"disambiguationData":[TD([[makeQuery(id+"F0.imprint","IMPRINT",EDGE,{"disambiguationData":[TD([[subQ2,-1.0]])],"derivedFrom":subQ1}),-1.0]])]});}
            var Q665;
            {var subQ0=sQuery(id+"F0.wireOp",EDGE,"E51");var subQ1=sQuery(id+"F0.wireOp",EDGE,"E45");var subQ2=makeQuery(id+"F0.imprint","INTERSECT",VERTEX,{"derivedFrom":[subQ1,subQ0]});Q665=makeQuery(id+"F0.imprint","IMPRINT",FACE,{"disambiguationData":[TD([[makeQuery(id+"F0.imprint","IMPRINT",EDGE,{"disambiguationData":[TD([[subQ2,-1.0]])],"derivedFrom":subQ1}),-1.0]])]});}
            var Q666;
            {var subQ0=sQuery(id+"F0.wireOp",EDGE,"E55");var subQ1=sQuery(id+"F0.wireOp",EDGE,"E25");var subQ2=makeQuery(id+"F0.imprint","INTERSECT",VERTEX,{"derivedFrom":[subQ1,subQ0]});Q666=makeQuery(id+"F0.imprint","IMPRINT",FACE,{"disambiguationData":[TD([[makeQuery(id+"F0.imprint","IMPRINT",EDGE,{"disambiguationData":[TD([[subQ2,-1.0]])],"derivedFrom":subQ1}),-1.0]])]});}
            var Q667;
            {var subQ0=sQuery(id+"F0.wireOp",EDGE,"E51");var subQ1=sQuery(id+"F0.wireOp",EDGE,"E46");var subQ2=makeQuery(id+"F0.imprint","INTERSECT",VERTEX,{"derivedFrom":[subQ1,subQ0]});Q667=makeQuery(id+"F0.imprint","IMPRINT",FACE,{"disambiguationData":[TD([[makeQuery(id+"F0.imprint","IMPRINT",EDGE,{"disambiguationData":[TD([[subQ2,-1.0]])],"derivedFrom":subQ1}),-1.0]])]});}
            var Q668;
            {var subQ0=sQuery(id+"F0.wireOp",EDGE,"E49");var subQ1=sQuery(id+"F0.wireOp",EDGE,"E24");var subQ2=makeQuery(id+"F0.imprint","INTERSECT",VERTEX,{"derivedFrom":[subQ1,subQ0]});Q668=makeQuery(id+"F0.imprint","IMPRINT",FACE,{"disambiguationData":[TD([[makeQuery(id+"F0.imprint","IMPRINT",EDGE,{"disambiguationData":[TD([[subQ2,-1.0]])],"derivedFrom":subQ1}),-1.0]])]});}
            var Q669;
            {var subQ0=sQuery(id+"F0.wireOp",EDGE,"E26");var subQ1=sQuery(id+"F0.wireOp",EDGE,"E1");var subQ2=makeQuery(id+"F0.imprint","INTERSECT",VERTEX,{"derivedFrom":[subQ1,subQ0]});Q669=makeQuery(id+"F0.imprint","IMPRINT",FACE,{"disambiguationData":[TD([[makeQuery(id+"F0.imprint","IMPRINT",EDGE,{"disambiguationData":[TD([[subQ2,-1.0]])],"derivedFrom":subQ1}),1.0]])]});}
            var Q670;
            {var subQ0=sQuery(id+"F0.wireOp",EDGE,"E26");var subQ1=sQuery(id+"F0.wireOp",EDGE,"E17");var subQ2=makeQuery(id+"F0.imprint","INTERSECT",VERTEX,{"derivedFrom":[subQ1,subQ0]});Q670=makeQuery(id+"F0.imprint","IMPRINT",FACE,{"disambiguationData":[TD([[makeQuery(id+"F0.imprint","IMPRINT",EDGE,{"disambiguationData":[TD([[subQ2,-1.0]])],"derivedFrom":subQ1}),-1.0]])]});}
            var Q671;
            {var subQ5=sQuery(id+"F0.wireOp",EDGE,"E25");var subQ7=sQuery(id+"F0.wireOp",EDGE,"E1");var subQ9=makeQuery(id+"F0.imprint","INTERSECT",VERTEX,{"derivedFrom":[subQ7,subQ5]});Q671=makeQuery(id+"F0.imprint","IMPRINT",FACE,{"disambiguationData":[TD([[makeQuery(id+"F0.imprint","IMPRINT",EDGE,{"disambiguationData":[TD([[subQ9,-1.0]])],"derivedFrom":subQ7}),1.0]])]});}
            var Q672;
            {var subQ0=sQuery(id+"F0.wireOp",EDGE,"E45");var subQ1=sQuery(id+"F0.wireOp",EDGE,"E29");var subQ2=makeQuery(id+"F0.imprint","INTERSECT",VERTEX,{"derivedFrom":[subQ1,subQ0]});Q672=makeQuery(id+"F0.imprint","IMPRINT",FACE,{"disambiguationData":[TD([[makeQuery(id+"F0.imprint","IMPRINT",EDGE,{"disambiguationData":[TD([[subQ2,-1.0]])],"derivedFrom":subQ1}),-1.0]])]});}
            var Q673;
            {var subQ0=sQuery(id+"F0.wireOp",EDGE,"E57");var subQ1=sQuery(id+"F0.wireOp",EDGE,"E44");var subQ2=makeQuery(id+"F0.imprint","INTERSECT",VERTEX,{"derivedFrom":[subQ1,subQ0]});Q673=makeQuery(id+"F0.imprint","IMPRINT",FACE,{"disambiguationData":[TD([[makeQuery(id+"F0.imprint","IMPRINT",EDGE,{"disambiguationData":[TD([[subQ2,-1.0]])],"derivedFrom":subQ1}),-1.0]])]});}
            var Q674;
            {var subQ0=sQuery(id+"F0.wireOp",EDGE,"E47");var subQ1=sQuery(id+"F0.wireOp",EDGE,"E24");var subQ2=makeQuery(id+"F0.imprint","INTERSECT",VERTEX,{"derivedFrom":[subQ1,subQ0]});Q674=makeQuery(id+"F0.imprint","IMPRINT",FACE,{"disambiguationData":[TD([[makeQuery(id+"F0.imprint","IMPRINT",EDGE,{"disambiguationData":[TD([[subQ2,-1.0]])],"derivedFrom":subQ1}),-1.0]])]});}
            var Q675;
            {var subQ0=sQuery(id+"F0.wireOp",EDGE,"E42");var subQ1=sQuery(id+"F0.wireOp",EDGE,"E28");var subQ2=makeQuery(id+"F0.imprint","INTERSECT",VERTEX,{"derivedFrom":[subQ1,subQ0]});Q675=makeQuery(id+"F0.imprint","IMPRINT",FACE,{"disambiguationData":[TD([[makeQuery(id+"F0.imprint","IMPRINT",EDGE,{"disambiguationData":[TD([[subQ2,-1.0]])],"derivedFrom":subQ1}),-1.0]])]});}
            var Q676;
            {var subQ0=sQuery(id+"F0.wireOp",EDGE,"E56");var subQ1=sQuery(id+"F0.wireOp",EDGE,"E44");var subQ2=makeQuery(id+"F0.imprint","INTERSECT",VERTEX,{"derivedFrom":[subQ1,subQ0]});Q676=makeQuery(id+"F0.imprint","IMPRINT",FACE,{"disambiguationData":[TD([[makeQuery(id+"F0.imprint","IMPRINT",EDGE,{"disambiguationData":[TD([[subQ2,-1.0]])],"derivedFrom":subQ1}),-1.0]])]});}
            var Q677;
            {var subQ1=sQuery(id+"F0.wireOp",EDGE,"E9");var subQ8=sQuery(id+"F0.wireOp",EDGE,"E32");var subQ11=makeQuery(id+"F0.imprint","INTERSECT",VERTEX,{"derivedFrom":[subQ1,subQ8]});Q677=makeQuery(id+"F0.imprint","IMPRINT",FACE,{"disambiguationData":[TD([[makeQuery(id+"F0.imprint","IMPRINT",EDGE,{"disambiguationData":[TD([[subQ11,-1.0]])],"derivedFrom":subQ1}),1.0]])]});}
            var Q678;
            {var subQ0=sQuery(id+"F0.wireOp",EDGE,"E27");var subQ1=sQuery(id+"F0.wireOp",EDGE,"E1");var subQ2=makeQuery(id+"F0.imprint","INTERSECT",VERTEX,{"derivedFrom":[subQ1,subQ0]});Q678=makeQuery(id+"F0.imprint","IMPRINT",FACE,{"disambiguationData":[TD([[makeQuery(id+"F0.imprint","IMPRINT",EDGE,{"disambiguationData":[TD([[subQ2,-1.0]])],"derivedFrom":subQ1}),1.0]])]});}
            var Q679;
            {var subQ0=sQuery(id+"F0.wireOp",EDGE,"E23");var subQ1=sQuery(id+"F0.wireOp",EDGE,"E15");var subQ2=makeQuery(id+"F0.imprint","INTERSECT",VERTEX,{"derivedFrom":[subQ1,subQ0]});Q679=makeQuery(id+"F0.imprint","IMPRINT",FACE,{"disambiguationData":[TD([[makeQuery(id+"F0.imprint","IMPRINT",EDGE,{"disambiguationData":[TD([[subQ2,-1.0]])],"derivedFrom":subQ1}),-1.0]])]});}
            var Q680;
            {var subQ1=sQuery(id+"F0.wireOp",EDGE,"E20");var subQ5=sQuery(id+"F0.wireOp",EDGE,"E25");var subQ6=makeQuery(id+"F0.imprint","INTERSECT",VERTEX,{"derivedFrom":[subQ1,subQ5]});Q680=makeQuery(id+"F0.imprint","IMPRINT",FACE,{"disambiguationData":[TD([[makeQuery(id+"F0.imprint","IMPRINT",EDGE,{"disambiguationData":[TD([[subQ6,-1.0]])],"derivedFrom":subQ1}),-1.0]])]});}
            var Q681;
            {var subQ0=sQuery(id+"F0.wireOp",EDGE,"E26");var subQ1=sQuery(id+"F0.wireOp",EDGE,"E15");var subQ2=makeQuery(id+"F0.imprint","INTERSECT",VERTEX,{"derivedFrom":[subQ1,subQ0]});Q681=makeQuery(id+"F0.imprint","IMPRINT",FACE,{"disambiguationData":[TD([[makeQuery(id+"F0.imprint","IMPRINT",EDGE,{"disambiguationData":[TD([[subQ2,-1.0]])],"derivedFrom":subQ1}),-1.0]])]});}
            var Q682;
            {var subQ1=sQuery(id+"F0.wireOp",EDGE,"E18");var subQ5=sQuery(id+"F0.wireOp",EDGE,"E26");var subQ6=makeQuery(id+"F0.imprint","INTERSECT",VERTEX,{"derivedFrom":[subQ1,subQ5]});Q682=makeQuery(id+"F0.imprint","IMPRINT",FACE,{"disambiguationData":[TD([[makeQuery(id+"F0.imprint","IMPRINT",EDGE,{"disambiguationData":[TD([[subQ6,-1.0]])],"derivedFrom":subQ1}),-1.0]])]});}
            var Q683;
            {var subQ0=sQuery(id+"F0.wireOp",EDGE,"E38");var subQ1=sQuery(id+"F0.wireOp",EDGE,"E28");var subQ2=makeQuery(id+"F0.imprint","INTERSECT",VERTEX,{"derivedFrom":[subQ1,subQ0]});Q683=makeQuery(id+"F0.imprint","IMPRINT",FACE,{"disambiguationData":[TD([[makeQuery(id+"F0.imprint","IMPRINT",EDGE,{"disambiguationData":[TD([[subQ2,-1.0]])],"derivedFrom":subQ1}),-1.0]])]});}
            var Q684;
            {var subQ0=sQuery(id+"F0.wireOp",EDGE,"E39");var subQ1=sQuery(id+"F0.wireOp",EDGE,"E28");var subQ2=makeQuery(id+"F0.imprint","INTERSECT",VERTEX,{"derivedFrom":[subQ1,subQ0]});Q684=makeQuery(id+"F0.imprint","IMPRINT",FACE,{"disambiguationData":[TD([[makeQuery(id+"F0.imprint","IMPRINT",EDGE,{"disambiguationData":[TD([[subQ2,-1.0]])],"derivedFrom":subQ1}),-1.0]])]});}
            var Q685;
            {var subQ1=sQuery(id+"F0.wireOp",EDGE,"E17");var subQ5=sQuery(id+"F0.wireOp",EDGE,"E27");var subQ9=makeQuery(id+"F0.imprint","INTERSECT",VERTEX,{"derivedFrom":[subQ1,subQ5]});Q685=makeQuery(id+"F0.imprint","IMPRINT",FACE,{"disambiguationData":[TD([[makeQuery(id+"F0.imprint","IMPRINT",EDGE,{"disambiguationData":[TD([[subQ9,-1.0]])],"derivedFrom":subQ1}),-1.0]])]});}
            var Q686;
            {var subQ0=sQuery(id+"F0.wireOp",EDGE,"E37");var subQ1=sQuery(id+"F0.wireOp",EDGE,"E28");var subQ2=makeQuery(id+"F0.imprint","INTERSECT",VERTEX,{"derivedFrom":[subQ1,subQ0]});Q686=makeQuery(id+"F0.imprint","IMPRINT",FACE,{"disambiguationData":[TD([[makeQuery(id+"F0.imprint","IMPRINT",EDGE,{"disambiguationData":[TD([[subQ2,-1.0]])],"derivedFrom":subQ1}),-1.0]])]});}
            var Q687;
            {var subQ0=sQuery(id+"F0.wireOp",EDGE,"E38");var subQ1=sQuery(id+"F0.wireOp",EDGE,"E30");var subQ2=makeQuery(id+"F0.imprint","INTERSECT",VERTEX,{"derivedFrom":[subQ1,subQ0]});Q687=makeQuery(id+"F0.imprint","IMPRINT",FACE,{"disambiguationData":[TD([[makeQuery(id+"F0.imprint","IMPRINT",EDGE,{"disambiguationData":[TD([[subQ2,-1.0]])],"derivedFrom":subQ1}),-1.0]])]});}
            var Q688;
            {var subQ0=sQuery(id+"F0.wireOp",EDGE,"E50");var subQ1=sQuery(id+"F0.wireOp",EDGE,"E22");var subQ2=makeQuery(id+"F0.imprint","INTERSECT",VERTEX,{"derivedFrom":[subQ1,subQ0]});Q688=makeQuery(id+"F0.imprint","IMPRINT",FACE,{"disambiguationData":[TD([[makeQuery(id+"F0.imprint","IMPRINT",EDGE,{"disambiguationData":[TD([[subQ2,-1.0]])],"derivedFrom":subQ1}),-1.0]])]});}
            var Q689;
            {var subQ0=sQuery(id+"F0.wireOp",EDGE,"E53");var subQ7=sQuery(id+"F0.wireOp",EDGE,"E25");var subQ9=makeQuery(id+"F0.imprint","INTERSECT",VERTEX,{"derivedFrom":[subQ7,subQ0]});Q689=makeQuery(id+"F0.imprint","IMPRINT",FACE,{"disambiguationData":[TD([[makeQuery(id+"F0.imprint","IMPRINT",EDGE,{"disambiguationData":[TD([[subQ9,-1.0]])],"derivedFrom":subQ7}),-1.0]])]});}
            var Q690;
            {var subQ0=sQuery(id+"F0.wireOp",EDGE,"E54");var subQ1=sQuery(id+"F0.wireOp",EDGE,"E46");var subQ2=makeQuery(id+"F0.imprint","INTERSECT",VERTEX,{"derivedFrom":[subQ1,subQ0]});Q690=makeQuery(id+"F0.imprint","IMPRINT",FACE,{"disambiguationData":[TD([[makeQuery(id+"F0.imprint","IMPRINT",EDGE,{"disambiguationData":[TD([[subQ2,-1.0]])],"derivedFrom":subQ1}),-1.0]])]});}
            var Q691;
            {var subQ5=sQuery(id+"F0.wireOp",EDGE,"E43");var subQ7=sQuery(id+"F0.wireOp",EDGE,"E10");var subQ9=makeQuery(id+"F0.imprint","INTERSECT",VERTEX,{"derivedFrom":[subQ7,subQ5]});Q691=makeQuery(id+"F0.imprint","IMPRINT",FACE,{"disambiguationData":[TD([[makeQuery(id+"F0.imprint","IMPRINT",EDGE,{"disambiguationData":[TD([[subQ9,-1.0]])],"derivedFrom":subQ7}),1.0]])]});}
            var Q692;
            {var subQ0=sQuery(id+"F0.wireOp",EDGE,"E30");var subQ1=sQuery(id+"F0.wireOp",EDGE,"E12");var subQ2=makeQuery(id+"F0.imprint","INTERSECT",VERTEX,{"derivedFrom":[subQ1,subQ0]});Q692=makeQuery(id+"F0.imprint","IMPRINT",FACE,{"disambiguationData":[TD([[makeQuery(id+"F0.imprint","IMPRINT",EDGE,{"disambiguationData":[TD([[subQ2,-1.0]])],"derivedFrom":subQ1}),1.0]])]});}
            var Q693;
            {var subQ0=sQuery(id+"F0.wireOp",EDGE,"E41");var subQ1=sQuery(id+"F0.wireOp",EDGE,"E29");var subQ2=makeQuery(id+"F0.imprint","INTERSECT",VERTEX,{"derivedFrom":[subQ1,subQ0]});Q693=makeQuery(id+"F0.imprint","IMPRINT",FACE,{"disambiguationData":[TD([[makeQuery(id+"F0.imprint","IMPRINT",EDGE,{"disambiguationData":[TD([[subQ2,-1.0]])],"derivedFrom":subQ1}),-1.0]])]});}
            var Q694;
            {var subQ1=sQuery(id+"F0.wireOp",EDGE,"E19");var subQ5=sQuery(id+"F0.wireOp",EDGE,"E26");var subQ6=makeQuery(id+"F0.imprint","INTERSECT",VERTEX,{"derivedFrom":[subQ1,subQ5]});Q694=makeQuery(id+"F0.imprint","IMPRINT",FACE,{"disambiguationData":[TD([[makeQuery(id+"F0.imprint","IMPRINT",EDGE,{"disambiguationData":[TD([[subQ6,-1.0]])],"derivedFrom":subQ1}),-1.0]])]});}
            var Q695;
            {var subQ0=sQuery(id+"F0.wireOp",EDGE,"E32");var subQ1=sQuery(id+"F0.wireOp",EDGE,"E11");var subQ2=makeQuery(id+"F0.imprint","INTERSECT",VERTEX,{"derivedFrom":[subQ1,subQ0]});Q695=makeQuery(id+"F0.imprint","IMPRINT",FACE,{"disambiguationData":[TD([[makeQuery(id+"F0.imprint","IMPRINT",EDGE,{"disambiguationData":[TD([[subQ2,-1.0]])],"derivedFrom":subQ1}),1.0]])]});}
            var Q696;
            {var subQ0=sQuery(id+"F0.wireOp",EDGE,"E37");var subQ1=sQuery(id+"F0.wireOp",EDGE,"E29");var subQ2=makeQuery(id+"F0.imprint","INTERSECT",VERTEX,{"derivedFrom":[subQ1,subQ0]});Q696=makeQuery(id+"F0.imprint","IMPRINT",FACE,{"disambiguationData":[TD([[makeQuery(id+"F0.imprint","IMPRINT",EDGE,{"disambiguationData":[TD([[subQ2,-1.0]])],"derivedFrom":subQ1}),-1.0]])]});}
            var Q697;
            {var subQ0=sQuery(id+"F0.wireOp",EDGE,"E56");var subQ1=sQuery(id+"F0.wireOp",EDGE,"E45");var subQ2=makeQuery(id+"F0.imprint","INTERSECT",VERTEX,{"derivedFrom":[subQ1,subQ0]});Q697=makeQuery(id+"F0.imprint","IMPRINT",FACE,{"disambiguationData":[TD([[makeQuery(id+"F0.imprint","IMPRINT",EDGE,{"disambiguationData":[TD([[subQ2,-1.0]])],"derivedFrom":subQ1}),-1.0]])]});}
            var Q698;
            {var subQ0=sQuery(id+"F0.wireOp",EDGE,"E55");var subQ1=sQuery(id+"F0.wireOp",EDGE,"E46");var subQ2=makeQuery(id+"F0.imprint","INTERSECT",VERTEX,{"derivedFrom":[subQ1,subQ0]});Q698=makeQuery(id+"F0.imprint","IMPRINT",FACE,{"disambiguationData":[TD([[makeQuery(id+"F0.imprint","IMPRINT",EDGE,{"disambiguationData":[TD([[subQ2,-1.0]])],"derivedFrom":subQ1}),-1.0]])]});}
            var Q699;
            {var subQ1=sQuery(id+"F0.wireOp",EDGE,"E22");var subQ5=sQuery(id+"F0.wireOp",EDGE,"E48");var subQ6=makeQuery(id+"F0.imprint","INTERSECT",VERTEX,{"derivedFrom":[subQ1,subQ5]});Q699=makeQuery(id+"F0.imprint","IMPRINT",FACE,{"disambiguationData":[TD([[makeQuery(id+"F0.imprint","IMPRINT",EDGE,{"disambiguationData":[TD([[subQ6,-1.0]])],"derivedFrom":subQ1}),-1.0]])]});}
            var Q700;
            {var subQ0=sQuery(id+"F0.wireOp",EDGE,"E45");var subQ1=sQuery(id+"F0.wireOp",EDGE,"E20");var subQ2=makeQuery(id+"F0.imprint","INTERSECT",VERTEX,{"derivedFrom":[subQ1,subQ0]});Q700=makeQuery(id+"F0.imprint","IMPRINT",FACE,{"disambiguationData":[TD([[makeQuery(id+"F0.imprint","IMPRINT",EDGE,{"disambiguationData":[TD([[subQ2,-1.0]])],"derivedFrom":subQ1}),1.0]])]});}
            var Q701;
            {var subQ5=sQuery(id+"F0.wireOp",EDGE,"E24");var subQ7=sQuery(id+"F0.wireOp",EDGE,"E2");var subQ9=makeQuery(id+"F0.imprint","INTERSECT",VERTEX,{"derivedFrom":[subQ7,subQ5]});Q701=makeQuery(id+"F0.imprint","IMPRINT",FACE,{"disambiguationData":[TD([[makeQuery(id+"F0.imprint","IMPRINT",EDGE,{"disambiguationData":[TD([[subQ9,-1.0]])],"derivedFrom":subQ7}),1.0]])]});}
            var Q702;
            {var subQ3=sQuery(id+"F0.wireOp",EDGE,"E52");var subQ6=sQuery(id+"F0.wireOp",EDGE,"E23");var subQ11=makeQuery(id+"F0.imprint","INTERSECT",VERTEX,{"derivedFrom":[subQ6,subQ3]});Q702=makeQuery(id+"F0.imprint","IMPRINT",FACE,{"disambiguationData":[TD([[makeQuery(id+"F0.imprint","IMPRINT",EDGE,{"disambiguationData":[TD([[subQ11,-1.0]])],"derivedFrom":subQ6}),-1.0]])]});}
            var Q703;
            {var subQ0=sQuery(id+"F0.wireOp",EDGE,"E38");var subQ1=sQuery(id+"F0.wireOp",EDGE,"E29");var subQ2=makeQuery(id+"F0.imprint","INTERSECT",VERTEX,{"derivedFrom":[subQ1,subQ0]});Q703=makeQuery(id+"F0.imprint","IMPRINT",FACE,{"disambiguationData":[TD([[makeQuery(id+"F0.imprint","IMPRINT",EDGE,{"disambiguationData":[TD([[subQ2,-1.0]])],"derivedFrom":subQ1}),-1.0]])]});}
            var Q704;
            {var subQ0=sQuery(id+"F0.wireOp",EDGE,"E23");var subQ1=sQuery(id+"F0.wireOp",EDGE,"E3");var subQ2=makeQuery(id+"F0.imprint","INTERSECT",VERTEX,{"derivedFrom":[subQ1,subQ0]});Q704=makeQuery(id+"F0.imprint","IMPRINT",FACE,{"disambiguationData":[TD([[makeQuery(id+"F0.imprint","IMPRINT",EDGE,{"disambiguationData":[TD([[subQ2,-1.0]])],"derivedFrom":subQ1}),1.0]])]});}
            var Q705;
            {var subQ5=sQuery(id+"F0.wireOp",EDGE,"E31");var subQ6=sQuery(id+"F0.wireOp",EDGE,"E11");var subQ7=makeQuery(id+"F0.imprint","INTERSECT",VERTEX,{"derivedFrom":[subQ6,subQ5]});Q705=makeQuery(id+"F0.imprint","IMPRINT",FACE,{"disambiguationData":[TD([[makeQuery(id+"F0.imprint","IMPRINT",EDGE,{"disambiguationData":[TD([[subQ7,-1.0]])],"derivedFrom":subQ6}),1.0]])]});}
            var Q706;
            {var subQ0=sQuery(id+"F0.wireOp",EDGE,"E52");var subQ1=sQuery(id+"F0.wireOp",EDGE,"E45");var subQ2=makeQuery(id+"F0.imprint","INTERSECT",VERTEX,{"derivedFrom":[subQ1,subQ0]});Q706=makeQuery(id+"F0.imprint","IMPRINT",FACE,{"disambiguationData":[TD([[makeQuery(id+"F0.imprint","IMPRINT",EDGE,{"disambiguationData":[TD([[subQ2,-1.0]])],"derivedFrom":subQ1}),-1.0]])]});}
            var Q707;
            {var subQ0=sQuery(id+"F0.wireOp",EDGE,"E50");var subQ1=sQuery(id+"F0.wireOp",EDGE,"E46");var subQ2=makeQuery(id+"F0.imprint","INTERSECT",VERTEX,{"derivedFrom":[subQ1,subQ0]});Q707=makeQuery(id+"F0.imprint","IMPRINT",FACE,{"disambiguationData":[TD([[makeQuery(id+"F0.imprint","IMPRINT",EDGE,{"disambiguationData":[TD([[subQ2,-1.0]])],"derivedFrom":subQ1}),-1.0]])]});}
            var Q708;
            {var subQ0=sQuery(id+"F0.wireOp",EDGE,"E56");var subQ1=sQuery(id+"F0.wireOp",EDGE,"E46");var subQ2=makeQuery(id+"F0.imprint","INTERSECT",VERTEX,{"derivedFrom":[subQ1,subQ0]});Q708=makeQuery(id+"F0.imprint","IMPRINT",FACE,{"disambiguationData":[TD([[makeQuery(id+"F0.imprint","IMPRINT",EDGE,{"disambiguationData":[TD([[subQ2,-1.0]])],"derivedFrom":subQ1}),-1.0]])]});}
            var Q709;
            {var subQ1=sQuery(id+"F0.wireOp",EDGE,"E28");var subQ7=sQuery(id+"F0.wireOp",EDGE,"E55");var subQ9=makeQuery(id+"F0.imprint","INTERSECT",VERTEX,{"derivedFrom":[subQ1,subQ7]});Q709=makeQuery(id+"F0.imprint","IMPRINT",FACE,{"disambiguationData":[TD([[makeQuery(id+"F0.imprint","IMPRINT",EDGE,{"disambiguationData":[TD([[subQ9,-1.0]])],"derivedFrom":subQ1}),-1.0]])]});}
            var Q710;
            {var subQ0=sQuery(id+"F0.wireOp",EDGE,"E54");var subQ1=sQuery(id+"F0.wireOp",EDGE,"E45");var subQ2=makeQuery(id+"F0.imprint","INTERSECT",VERTEX,{"derivedFrom":[subQ1,subQ0]});Q710=makeQuery(id+"F0.imprint","IMPRINT",FACE,{"disambiguationData":[TD([[makeQuery(id+"F0.imprint","IMPRINT",EDGE,{"disambiguationData":[TD([[subQ2,-1.0]])],"derivedFrom":subQ1}),-1.0]])]});}
            var Q711;
            {var subQ0=sQuery(id+"F0.wireOp",EDGE,"E57");var subQ1=sQuery(id+"F0.wireOp",EDGE,"E46");var subQ2=makeQuery(id+"F0.imprint","INTERSECT",VERTEX,{"derivedFrom":[subQ1,subQ0]});Q711=makeQuery(id+"F0.imprint","IMPRINT",FACE,{"disambiguationData":[TD([[makeQuery(id+"F0.imprint","IMPRINT",EDGE,{"disambiguationData":[TD([[subQ2,-1.0]])],"derivedFrom":subQ1}),-1.0]])]});}
            var Q712;
            {var subQ0=sQuery(id+"F0.wireOp",EDGE,"E57");var subQ1=sQuery(id+"F0.wireOp",EDGE,"E45");var subQ2=makeQuery(id+"F0.imprint","INTERSECT",VERTEX,{"derivedFrom":[subQ1,subQ0]});Q712=makeQuery(id+"F0.imprint","IMPRINT",FACE,{"disambiguationData":[TD([[makeQuery(id+"F0.imprint","IMPRINT",EDGE,{"disambiguationData":[TD([[subQ2,-1.0]])],"derivedFrom":subQ1}),-1.0]])]});}
            var Q713;
            {var subQ1=sQuery(id+"F0.wireOp",EDGE,"E24");var subQ8=sQuery(id+"F0.wireOp",EDGE,"E53");var subQ10=makeQuery(id+"F0.imprint","INTERSECT",VERTEX,{"derivedFrom":[subQ1,subQ8]});Q713=makeQuery(id+"F0.imprint","IMPRINT",FACE,{"disambiguationData":[TD([[makeQuery(id+"F0.imprint","IMPRINT",EDGE,{"disambiguationData":[TD([[subQ10,-1.0]])],"derivedFrom":subQ1}),-1.0]])]});}
            var Q714;
            {var subQ0=sQuery(id+"F0.wireOp",EDGE,"E55");var subQ1=sQuery(id+"F0.wireOp",EDGE,"E45");var subQ2=makeQuery(id+"F0.imprint","INTERSECT",VERTEX,{"derivedFrom":[subQ1,subQ0]});Q714=makeQuery(id+"F0.imprint","IMPRINT",FACE,{"disambiguationData":[TD([[makeQuery(id+"F0.imprint","IMPRINT",EDGE,{"disambiguationData":[TD([[subQ2,-1.0]])],"derivedFrom":subQ1}),-1.0]])]});}
            var Q715;
            {var subQ0=sQuery(id+"F0.wireOp",EDGE,"E29");var subQ1=sQuery(id+"F0.wireOp",EDGE,"E12");var subQ2=makeQuery(id+"F0.imprint","INTERSECT",VERTEX,{"derivedFrom":[subQ1,subQ0]});Q715=makeQuery(id+"F0.imprint","IMPRINT",FACE,{"disambiguationData":[TD([[makeQuery(id+"F0.imprint","IMPRINT",EDGE,{"disambiguationData":[TD([[subQ2,-1.0]])],"derivedFrom":subQ1}),1.0]])]});}
            var Q716;
            {var subQ0=sQuery(id+"F0.wireOp",EDGE,"E41");var subQ1=sQuery(id+"F0.wireOp",EDGE,"E31");var subQ2=makeQuery(id+"F0.imprint","INTERSECT",VERTEX,{"derivedFrom":[subQ1,subQ0]});Q716=makeQuery(id+"F0.imprint","IMPRINT",FACE,{"disambiguationData":[TD([[makeQuery(id+"F0.imprint","IMPRINT",EDGE,{"disambiguationData":[TD([[subQ2,-1.0]])],"derivedFrom":subQ1}),-1.0]])]});}
            var Q717;
            {var subQ0=sQuery(id+"F0.wireOp",EDGE,"E24");var subQ1=sQuery(id+"F0.wireOp",EDGE,"E15");var subQ2=makeQuery(id+"F0.imprint","INTERSECT",VERTEX,{"derivedFrom":[subQ1,subQ0]});Q717=makeQuery(id+"F0.imprint","IMPRINT",FACE,{"disambiguationData":[TD([[makeQuery(id+"F0.imprint","IMPRINT",EDGE,{"disambiguationData":[TD([[subQ2,-1.0]])],"derivedFrom":subQ1}),-1.0]])]});}
            var Q718;
            {var subQ0=sQuery(id+"F0.wireOp",EDGE,"E54");var subQ1=sQuery(id+"F0.wireOp",EDGE,"E44");var subQ2=makeQuery(id+"F0.imprint","INTERSECT",VERTEX,{"derivedFrom":[subQ1,subQ0]});Q718=makeQuery(id+"F0.imprint","IMPRINT",FACE,{"disambiguationData":[TD([[makeQuery(id+"F0.imprint","IMPRINT",EDGE,{"disambiguationData":[TD([[subQ2,-1.0]])],"derivedFrom":subQ1}),-1.0]])]});}
            var Q719;
            {var subQ0=sQuery(id+"F0.wireOp",EDGE,"E53");var subQ1=sQuery(id+"F0.wireOp",EDGE,"E45");var subQ2=makeQuery(id+"F0.imprint","INTERSECT",VERTEX,{"derivedFrom":[subQ1,subQ0]});Q719=makeQuery(id+"F0.imprint","IMPRINT",FACE,{"disambiguationData":[TD([[makeQuery(id+"F0.imprint","IMPRINT",EDGE,{"disambiguationData":[TD([[subQ2,-1.0]])],"derivedFrom":subQ1}),-1.0]])]});}
            var Q720;
            {var subQ0=sQuery(id+"F0.wireOp",EDGE,"E51");var subQ1=sQuery(id+"F0.wireOp",EDGE,"E28");var subQ2=makeQuery(id+"F0.imprint","INTERSECT",VERTEX,{"derivedFrom":[subQ1,subQ0]});Q720=makeQuery(id+"F0.imprint","IMPRINT",FACE,{"disambiguationData":[TD([[makeQuery(id+"F0.imprint","IMPRINT",EDGE,{"disambiguationData":[TD([[subQ2,-1.0]])],"derivedFrom":subQ1}),-1.0]])]});}
            var Q721;
            {var subQ0=sQuery(id+"F0.wireOp",EDGE,"E58");var subQ1=sQuery(id+"F0.wireOp",EDGE,"E39");var subQ2=makeQuery(id+"F0.imprint","INTERSECT",VERTEX,{"derivedFrom":[subQ1,subQ0]});Q721=makeQuery(id+"F0.imprint","IMPRINT",FACE,{"disambiguationData":[TD([[makeQuery(id+"F0.imprint","IMPRINT",EDGE,{"disambiguationData":[TD([[subQ2,-1.0]])],"derivedFrom":subQ1}),1.0]])]});}
            var Q722;
            {var subQ0=sQuery(id+"F0.wireOp",EDGE,"E50");var subQ1=sQuery(id+"F0.wireOp",EDGE,"E24");var subQ2=makeQuery(id+"F0.imprint","INTERSECT",VERTEX,{"derivedFrom":[subQ1,subQ0]});Q722=makeQuery(id+"F0.imprint","IMPRINT",FACE,{"disambiguationData":[TD([[makeQuery(id+"F0.imprint","IMPRINT",EDGE,{"disambiguationData":[TD([[subQ2,-1.0]])],"derivedFrom":subQ1}),1.0]])]});}
            var Q723;
            {var subQ0=sQuery(id+"F0.wireOp",EDGE,"E45");var subQ1=sQuery(id+"F0.wireOp",EDGE,"E19");var subQ2=makeQuery(id+"F0.imprint","INTERSECT",VERTEX,{"derivedFrom":[subQ1,subQ0]});Q723=makeQuery(id+"F0.imprint","IMPRINT",FACE,{"disambiguationData":[TD([[makeQuery(id+"F0.imprint","IMPRINT",EDGE,{"disambiguationData":[TD([[subQ2,-1.0]])],"derivedFrom":subQ1}),-1.0]])]});}
            var Q724;
            {var subQ0=sQuery(id+"F0.wireOp",EDGE,"E49");var subQ1=sQuery(id+"F0.wireOp",EDGE,"E26");var subQ2=makeQuery(id+"F0.imprint","INTERSECT",VERTEX,{"derivedFrom":[subQ1,subQ0]});Q724=makeQuery(id+"F0.imprint","IMPRINT",FACE,{"disambiguationData":[TD([[makeQuery(id+"F0.imprint","IMPRINT",EDGE,{"disambiguationData":[TD([[subQ2,-1.0]])],"derivedFrom":subQ1}),1.0]])]});}
            var Q725;
            {var subQ0=sQuery(id+"F0.wireOp",EDGE,"E54");var subQ1=sQuery(id+"F0.wireOp",EDGE,"E52");var subQ2=makeQuery(id+"F0.imprint","INTERSECT",VERTEX,{"derivedFrom":[subQ1,subQ0]});Q725=makeQuery(id+"F0.imprint","IMPRINT",FACE,{"disambiguationData":[TD([[makeQuery(id+"F0.imprint","IMPRINT",EDGE,{"disambiguationData":[TD([[subQ2,-1.0]])],"derivedFrom":subQ1}),-1.0]])]});}
            var Q726;
            {var subQ5=sQuery(id+"F0.wireOp",EDGE,"E11");var subQ7=sQuery(id+"F0.wireOp",EDGE,"E30");var subQ8=makeQuery(id+"F0.imprint","INTERSECT",VERTEX,{"derivedFrom":[subQ5,subQ7]});Q726=makeQuery(id+"F0.imprint","IMPRINT",FACE,{"disambiguationData":[TD([[makeQuery(id+"F0.imprint","IMPRINT",EDGE,{"disambiguationData":[TD([[subQ8,-1.0]])],"derivedFrom":subQ5}),1.0]])]});}
            var Q727;
            {var subQ0=sQuery(id+"F0.wireOp",EDGE,"E55");var subQ1=sQuery(id+"F0.wireOp",EDGE,"E29");var subQ2=makeQuery(id+"F0.imprint","INTERSECT",VERTEX,{"derivedFrom":[subQ1,subQ0]});Q727=makeQuery(id+"F0.imprint","IMPRINT",FACE,{"disambiguationData":[TD([[makeQuery(id+"F0.imprint","IMPRINT",EDGE,{"disambiguationData":[TD([[subQ2,-1.0]])],"derivedFrom":subQ1}),1.0]])]});}
            var Q728;
            {var subQ0=sQuery(id+"F0.wireOp",EDGE,"E52");var subQ1=sQuery(id+"F0.wireOp",EDGE,"E23");var subQ2=makeQuery(id+"F0.imprint","INTERSECT",VERTEX,{"derivedFrom":[subQ1,subQ0]});Q728=makeQuery(id+"F0.imprint","IMPRINT",FACE,{"disambiguationData":[TD([[makeQuery(id+"F0.imprint","IMPRINT",EDGE,{"disambiguationData":[TD([[subQ2,-1.0]])],"derivedFrom":subQ1}),1.0]])]});}
            var Q729;
            {var subQ0=sQuery(id+"F0.wireOp",EDGE,"E45");var subQ1=sQuery(id+"F0.wireOp",EDGE,"E22");var subQ2=makeQuery(id+"F0.imprint","INTERSECT",VERTEX,{"derivedFrom":[subQ1,subQ0]});Q729=makeQuery(id+"F0.imprint","IMPRINT",FACE,{"disambiguationData":[TD([[makeQuery(id+"F0.imprint","IMPRINT",EDGE,{"disambiguationData":[TD([[subQ2,-1.0]])],"derivedFrom":subQ1}),1.0]])]});}
            var Q730;
            {var subQ0=sQuery(id+"F0.wireOp",EDGE,"E46");var subQ1=sQuery(id+"F0.wireOp",EDGE,"E23");var subQ2=makeQuery(id+"F0.imprint","INTERSECT",VERTEX,{"derivedFrom":[subQ1,subQ0]});Q730=makeQuery(id+"F0.imprint","IMPRINT",FACE,{"disambiguationData":[TD([[makeQuery(id+"F0.imprint","IMPRINT",EDGE,{"disambiguationData":[TD([[subQ2,-1.0]])],"derivedFrom":subQ1}),-1.0]])]});}
            var Q731;
            {var subQ0=sQuery(id+"F0.wireOp",EDGE,"E4");var subQ1=sQuery(id+"F0.wireOp",EDGE,"E1");var subQ2=makeQuery(id+"F0.imprint","INTERSECT",VERTEX,{"derivedFrom":[subQ1,subQ0]});Q731=makeQuery(id+"F0.imprint","IMPRINT",FACE,{"disambiguationData":[TD([[makeQuery(id+"F0.imprint","IMPRINT",EDGE,{"disambiguationData":[TD([[subQ2,-1.0]])],"derivedFrom":subQ1}),1.0]])]});}
            var Q732;
            {var subQ1=sQuery(id+"F0.wireOp",EDGE,"E10");var subQ5=sQuery(id+"F0.wireOp",EDGE,"E31");var subQ9=makeQuery(id+"F0.imprint","INTERSECT",VERTEX,{"derivedFrom":[subQ1,subQ5]});Q732=makeQuery(id+"F0.imprint","IMPRINT",FACE,{"disambiguationData":[TD([[makeQuery(id+"F0.imprint","IMPRINT",EDGE,{"disambiguationData":[TD([[subQ9,-1.0]])],"derivedFrom":subQ1}),1.0]])]});}
            var Q733;
            {var subQ0=sQuery(id+"F0.wireOp",EDGE,"E46");var subQ1=sQuery(id+"F0.wireOp",EDGE,"E21");var subQ2=makeQuery(id+"F0.imprint","INTERSECT",VERTEX,{"derivedFrom":[subQ1,subQ0]});Q733=makeQuery(id+"F0.imprint","IMPRINT",FACE,{"disambiguationData":[TD([[makeQuery(id+"F0.imprint","IMPRINT",EDGE,{"disambiguationData":[TD([[subQ2,-1.0]])],"derivedFrom":subQ1}),1.0]])]});}
            var Q734;
            {var subQ0=sQuery(id+"F0.wireOp",EDGE,"E23");var subQ1=sQuery(id+"F0.wireOp",EDGE,"E2");var subQ2=makeQuery(id+"F0.imprint","INTERSECT",VERTEX,{"derivedFrom":[subQ1,subQ0]});Q734=makeQuery(id+"F0.imprint","IMPRINT",FACE,{"disambiguationData":[TD([[makeQuery(id+"F0.imprint","IMPRINT",EDGE,{"disambiguationData":[TD([[subQ2,-1.0]])],"derivedFrom":subQ1}),-1.0]])]});}
            var Q735;
            {var subQ0=sQuery(id+"F0.wireOp",EDGE,"E44");var subQ1=sQuery(id+"F0.wireOp",EDGE,"E25");var subQ2=makeQuery(id+"F0.imprint","INTERSECT",VERTEX,{"derivedFrom":[subQ1,subQ0]});Q735=makeQuery(id+"F0.imprint","IMPRINT",FACE,{"disambiguationData":[TD([[makeQuery(id+"F0.imprint","IMPRINT",EDGE,{"disambiguationData":[TD([[subQ2,-1.0]])],"derivedFrom":subQ1}),-1.0]])]});}
            var Q736;
            {var subQ1=sQuery(id+"F0.wireOp",EDGE,"E20");var subQ7=sQuery(id+"F0.wireOp",EDGE,"E48");var subQ9=makeQuery(id+"F0.imprint","INTERSECT",VERTEX,{"derivedFrom":[subQ1,subQ7]});Q736=makeQuery(id+"F0.imprint","IMPRINT",FACE,{"disambiguationData":[TD([[makeQuery(id+"F0.imprint","IMPRINT",EDGE,{"disambiguationData":[TD([[subQ9,-1.0]])],"derivedFrom":subQ1}),-1.0]])]});}
            var Q737;
            {var subQ0=sQuery(id+"F0.wireOp",EDGE,"E47");var subQ1=sQuery(id+"F0.wireOp",EDGE,"E23");var subQ2=makeQuery(id+"F0.imprint","INTERSECT",VERTEX,{"derivedFrom":[subQ1,subQ0]});Q737=makeQuery(id+"F0.imprint","IMPRINT",FACE,{"disambiguationData":[TD([[makeQuery(id+"F0.imprint","IMPRINT",EDGE,{"disambiguationData":[TD([[subQ2,-1.0]])],"derivedFrom":subQ1}),-1.0]])]});}
            var Q738;
            {var subQ0=sQuery(id+"F0.wireOp",EDGE,"E32");var subQ1=sQuery(id+"F0.wireOp",EDGE,"E11");var subQ2=makeQuery(id+"F0.imprint","INTERSECT",VERTEX,{"derivedFrom":[subQ1,subQ0]});Q738=makeQuery(id+"F0.imprint","IMPRINT",FACE,{"disambiguationData":[TD([[makeQuery(id+"F0.imprint","IMPRINT",EDGE,{"disambiguationData":[TD([[subQ2,-1.0]])],"derivedFrom":subQ1}),-1.0]])]});}
            var Q739;
            {var subQ0=sQuery(id+"F0.wireOp",EDGE,"E58");var subQ1=sQuery(id+"F0.wireOp",EDGE,"E36");var subQ2=makeQuery(id+"F0.imprint","INTERSECT",VERTEX,{"derivedFrom":[subQ1,subQ0]});Q739=makeQuery(id+"F0.imprint","IMPRINT",FACE,{"disambiguationData":[TD([[makeQuery(id+"F0.imprint","IMPRINT",EDGE,{"disambiguationData":[TD([[subQ2,-1.0]])],"derivedFrom":subQ1}),1.0]])]});}
            var Q740;
            {var subQ0=sQuery(id+"F0.wireOp",EDGE,"E55");var subQ1=sQuery(id+"F0.wireOp",EDGE,"E25");var subQ2=makeQuery(id+"F0.imprint","INTERSECT",VERTEX,{"derivedFrom":[subQ1,subQ0]});Q740=makeQuery(id+"F0.imprint","IMPRINT",FACE,{"disambiguationData":[TD([[makeQuery(id+"F0.imprint","IMPRINT",EDGE,{"disambiguationData":[TD([[subQ2,-1.0]])],"derivedFrom":subQ1}),1.0]])]});}
            var Q741;
            {var subQ1=sQuery(id+"F0.wireOp",EDGE,"E24");var subQ3=sQuery(id+"F0.wireOp",EDGE,"E26");var subQ4=makeQuery(id+"F0.imprint","INTERSECT",VERTEX,{"derivedFrom":[subQ1,subQ3]});Q741=makeQuery(id+"F0.imprint","IMPRINT",FACE,{"disambiguationData":[TD([[makeQuery(id+"F0.imprint","IMPRINT",EDGE,{"disambiguationData":[TD([[subQ4,-1.0]])],"derivedFrom":subQ3}),1.0]])]});}
            var Q742;
            {var subQ0=sQuery(id+"F0.wireOp",EDGE,"E46");var subQ1=sQuery(id+"F0.wireOp",EDGE,"E19");var subQ2=makeQuery(id+"F0.imprint","INTERSECT",VERTEX,{"derivedFrom":[subQ1,subQ0]});Q742=makeQuery(id+"F0.imprint","IMPRINT",FACE,{"disambiguationData":[TD([[makeQuery(id+"F0.imprint","IMPRINT",EDGE,{"disambiguationData":[TD([[subQ2,-1.0]])],"derivedFrom":subQ1}),-1.0]])]});}
            var Q743;
            {var subQ0=sQuery(id+"F0.wireOp",EDGE,"E24");var subQ1=sQuery(id+"F0.wireOp",EDGE,"E1");var subQ2=makeQuery(id+"F0.imprint","INTERSECT",VERTEX,{"derivedFrom":[subQ1,subQ0]});Q743=makeQuery(id+"F0.imprint","IMPRINT",FACE,{"disambiguationData":[TD([[makeQuery(id+"F0.imprint","IMPRINT",EDGE,{"disambiguationData":[TD([[subQ2,-1.0]])],"derivedFrom":subQ1}),1.0]])]});}
            var Q744;
            {var subQ0=sQuery(id+"F0.wireOp",EDGE,"E44");var subQ1=sQuery(id+"F0.wireOp",EDGE,"E21");var subQ2=makeQuery(id+"F0.imprint","INTERSECT",VERTEX,{"derivedFrom":[subQ1,subQ0]});Q744=makeQuery(id+"F0.imprint","IMPRINT",FACE,{"disambiguationData":[TD([[makeQuery(id+"F0.imprint","IMPRINT",EDGE,{"disambiguationData":[TD([[subQ2,-1.0]])],"derivedFrom":subQ1}),1.0]])]});}
            var Q745;
            {var subQ0=sQuery(id+"F0.wireOp",EDGE,"E44");var subQ1=sQuery(id+"F0.wireOp",EDGE,"E24");var subQ2=makeQuery(id+"F0.imprint","INTERSECT",VERTEX,{"derivedFrom":[subQ1,subQ0]});Q745=makeQuery(id+"F0.imprint","IMPRINT",FACE,{"disambiguationData":[TD([[makeQuery(id+"F0.imprint","IMPRINT",EDGE,{"disambiguationData":[TD([[subQ2,-1.0]])],"derivedFrom":subQ1}),1.0]])]});}
            var Q746;
            {var subQ6=sQuery(id+"F0.wireOp",EDGE,"E2");var subQ9=sQuery(id+"F0.wireOp",EDGE,"E23");var subQ11=makeQuery(id+"F0.imprint","INTERSECT",VERTEX,{"derivedFrom":[subQ6,subQ9]});Q746=makeQuery(id+"F0.imprint","IMPRINT",FACE,{"disambiguationData":[TD([[makeQuery(id+"F0.imprint","IMPRINT",EDGE,{"disambiguationData":[TD([[subQ11,-1.0]])],"derivedFrom":subQ6}),1.0]])]});}
            var Q747;
            {var subQ0=sQuery(id+"F0.wireOp",EDGE,"E46");var subQ1=sQuery(id+"F0.wireOp",EDGE,"E22");var subQ2=makeQuery(id+"F0.imprint","INTERSECT",VERTEX,{"derivedFrom":[subQ1,subQ0]});Q747=makeQuery(id+"F0.imprint","IMPRINT",FACE,{"disambiguationData":[TD([[makeQuery(id+"F0.imprint","IMPRINT",EDGE,{"disambiguationData":[TD([[subQ2,-1.0]])],"derivedFrom":subQ1}),-1.0]])]});}
            var Q748;
            {var subQ0=sQuery(id+"F0.wireOp",EDGE,"E54");var subQ1=sQuery(id+"F0.wireOp",EDGE,"E37");var subQ2=makeQuery(id+"F0.imprint","INTERSECT",VERTEX,{"derivedFrom":[subQ1,subQ0]});Q748=makeQuery(id+"F0.imprint","IMPRINT",FACE,{"disambiguationData":[TD([[makeQuery(id+"F0.imprint","IMPRINT",EDGE,{"disambiguationData":[TD([[subQ2,-1.0]])],"derivedFrom":subQ1}),-1.0]])]});}
            var Q749;
            {var subQ0=sQuery(id+"F0.wireOp",EDGE,"E58");var subQ1=sQuery(id+"F0.wireOp",EDGE,"E37");var subQ2=makeQuery(id+"F0.imprint","INTERSECT",VERTEX,{"derivedFrom":[subQ1,subQ0]});Q749=makeQuery(id+"F0.imprint","IMPRINT",FACE,{"disambiguationData":[TD([[makeQuery(id+"F0.imprint","IMPRINT",EDGE,{"disambiguationData":[TD([[subQ2,-1.0]])],"derivedFrom":subQ1}),1.0]])]});}
            var Q750;
            {var subQ0=sQuery(id+"F0.wireOp",EDGE,"E57");var subQ1=sQuery(id+"F0.wireOp",EDGE,"E28");var subQ2=makeQuery(id+"F0.imprint","INTERSECT",VERTEX,{"derivedFrom":[subQ1,subQ0]});Q750=makeQuery(id+"F0.imprint","IMPRINT",FACE,{"disambiguationData":[TD([[makeQuery(id+"F0.imprint","IMPRINT",EDGE,{"disambiguationData":[TD([[subQ2,-1.0]])],"derivedFrom":subQ1}),1.0]])]});}
            var Q751;
            {var subQ0=sQuery(id+"F0.wireOp",EDGE,"E50");var subQ1=sQuery(id+"F0.wireOp",EDGE,"E21");var subQ2=makeQuery(id+"F0.imprint","INTERSECT",VERTEX,{"derivedFrom":[subQ1,subQ0]});Q751=makeQuery(id+"F0.imprint","IMPRINT",FACE,{"disambiguationData":[TD([[makeQuery(id+"F0.imprint","IMPRINT",EDGE,{"disambiguationData":[TD([[subQ2,-1.0]])],"derivedFrom":subQ1}),1.0]])]});}
            var Q752;
            {var subQ0=sQuery(id+"F0.wireOp",EDGE,"E43");var subQ1=sQuery(id+"F0.wireOp",EDGE,"E11");var subQ2=makeQuery(id+"F0.imprint","INTERSECT",VERTEX,{"derivedFrom":[subQ1,subQ0]});Q752=makeQuery(id+"F0.imprint","IMPRINT",FACE,{"disambiguationData":[TD([[makeQuery(id+"F0.imprint","IMPRINT",EDGE,{"disambiguationData":[TD([[subQ2,-1.0]])],"derivedFrom":subQ1}),1.0]])]});}
            var Q753;
            {var subQ0=sQuery(id+"F0.wireOp",EDGE,"E26");var subQ1=sQuery(id+"F0.wireOp",EDGE,"E20");var subQ2=makeQuery(id+"F0.imprint","INTERSECT",VERTEX,{"derivedFrom":[subQ1,subQ0]});Q753=makeQuery(id+"F0.imprint","IMPRINT",FACE,{"disambiguationData":[TD([[makeQuery(id+"F0.imprint","IMPRINT",EDGE,{"disambiguationData":[TD([[subQ2,-1.0]])],"derivedFrom":subQ1}),-1.0]])]});}
            var Q754;
            {var subQ1=sQuery(id+"F0.wireOp",EDGE,"E19");var subQ7=sQuery(id+"F0.wireOp",EDGE,"E48");var subQ9=makeQuery(id+"F0.imprint","INTERSECT",VERTEX,{"derivedFrom":[subQ1,subQ7]});Q754=makeQuery(id+"F0.imprint","IMPRINT",FACE,{"disambiguationData":[TD([[makeQuery(id+"F0.imprint","IMPRINT",EDGE,{"disambiguationData":[TD([[subQ9,-1.0]])],"derivedFrom":subQ1}),-1.0]])]});}
            var Q755;
            {var subQ0=sQuery(id+"F0.wireOp",EDGE,"E47");var subQ1=sQuery(id+"F0.wireOp",EDGE,"E19");var subQ2=makeQuery(id+"F0.imprint","INTERSECT",VERTEX,{"derivedFrom":[subQ1,subQ0]});Q755=makeQuery(id+"F0.imprint","IMPRINT",FACE,{"disambiguationData":[TD([[makeQuery(id+"F0.imprint","IMPRINT",EDGE,{"disambiguationData":[TD([[subQ2,-1.0]])],"derivedFrom":subQ1}),1.0]])]});}
            var Q756;
            {var subQ0=sQuery(id+"F0.wireOp",EDGE,"E27");var subQ1=sQuery(id+"F0.wireOp",EDGE,"E20");var subQ2=makeQuery(id+"F0.imprint","INTERSECT",VERTEX,{"derivedFrom":[subQ1,subQ0]});Q756=makeQuery(id+"F0.imprint","IMPRINT",FACE,{"disambiguationData":[TD([[makeQuery(id+"F0.imprint","IMPRINT",EDGE,{"disambiguationData":[TD([[subQ2,-1.0]])],"derivedFrom":subQ1}),-1.0]])]});}
            var Q757;
            {var subQ0=sQuery(id+"F0.wireOp",EDGE,"E2");var subQ1=sQuery(id+"F0.wireOp",EDGE,"E1");var subQ2=makeQuery(id+"F0.imprint","INTERSECT",VERTEX,{"derivedFrom":[subQ1,subQ0]});Q757=makeQuery(id+"F0.imprint","IMPRINT",FACE,{"disambiguationData":[TD([[makeQuery(id+"F0.imprint","IMPRINT",EDGE,{"disambiguationData":[TD([[subQ2,-1.0]])],"derivedFrom":subQ1}),1.0]])]});}
            var Q758;
            {var subQ0=sQuery(id+"F0.wireOp",EDGE,"E31");var subQ1=sQuery(id+"F0.wireOp",EDGE,"E11");var subQ2=makeQuery(id+"F0.imprint","INTERSECT",VERTEX,{"derivedFrom":[subQ1,subQ0]});Q758=makeQuery(id+"F0.imprint","IMPRINT",FACE,{"disambiguationData":[TD([[makeQuery(id+"F0.imprint","IMPRINT",EDGE,{"disambiguationData":[TD([[subQ2,-1.0]])],"derivedFrom":subQ1}),-1.0]])]});}
            var Q759;
            {var subQ0=sQuery(id+"F0.wireOp",EDGE,"E57");var subQ1=sQuery(id+"F0.wireOp",EDGE,"E53");var subQ2=makeQuery(id+"F0.imprint","INTERSECT",VERTEX,{"derivedFrom":[subQ1,subQ0]});Q759=makeQuery(id+"F0.imprint","IMPRINT",FACE,{"disambiguationData":[TD([[makeQuery(id+"F0.imprint","IMPRINT",EDGE,{"disambiguationData":[TD([[subQ2,-1.0]])],"derivedFrom":subQ1}),1.0]])]});}
            var Q760;
            {var subQ0=sQuery(id+"F0.wireOp",EDGE,"E25");var subQ1=sQuery(id+"F0.wireOp",EDGE,"E21");var subQ2=makeQuery(id+"F0.imprint","INTERSECT",VERTEX,{"derivedFrom":[subQ1,subQ0]});Q760=makeQuery(id+"F0.imprint","IMPRINT",FACE,{"disambiguationData":[TD([[makeQuery(id+"F0.imprint","IMPRINT",EDGE,{"disambiguationData":[TD([[subQ2,-1.0]])],"derivedFrom":subQ1}),-1.0]])]});}
            var Q761;
            {var subQ0=sQuery(id+"F0.wireOp",EDGE,"E43");var subQ1=sQuery(id+"F0.wireOp",EDGE,"E11");var subQ2=makeQuery(id+"F0.imprint","INTERSECT",VERTEX,{"derivedFrom":[subQ1,subQ0]});Q761=makeQuery(id+"F0.imprint","IMPRINT",FACE,{"disambiguationData":[TD([[makeQuery(id+"F0.imprint","IMPRINT",EDGE,{"disambiguationData":[TD([[subQ2,-1.0]])],"derivedFrom":subQ1}),-1.0]])]});}
            var Q762;
            {var subQ0=sQuery(id+"F0.wireOp",EDGE,"E53");var subQ1=sQuery(id+"F0.wireOp",EDGE,"E28");var subQ2=makeQuery(id+"F0.imprint","INTERSECT",VERTEX,{"derivedFrom":[subQ1,subQ0]});Q762=makeQuery(id+"F0.imprint","IMPRINT",FACE,{"disambiguationData":[TD([[makeQuery(id+"F0.imprint","IMPRINT",EDGE,{"disambiguationData":[TD([[subQ2,-1.0]])],"derivedFrom":subQ1}),-1.0]])]});}
            var Q763;
            {var subQ0=sQuery(id+"F0.wireOp",EDGE,"E47");var subQ1=sQuery(id+"F0.wireOp",EDGE,"E20");var subQ2=makeQuery(id+"F0.imprint","INTERSECT",VERTEX,{"derivedFrom":[subQ1,subQ0]});Q763=makeQuery(id+"F0.imprint","IMPRINT",FACE,{"disambiguationData":[TD([[makeQuery(id+"F0.imprint","IMPRINT",EDGE,{"disambiguationData":[TD([[subQ2,-1.0]])],"derivedFrom":subQ1}),-1.0]])]});}
            var Q764;
            {var subQ0=sQuery(id+"F0.wireOp",EDGE,"E44");var subQ1=sQuery(id+"F0.wireOp",EDGE,"E22");var subQ2=makeQuery(id+"F0.imprint","INTERSECT",VERTEX,{"derivedFrom":[subQ1,subQ0]});Q764=makeQuery(id+"F0.imprint","IMPRINT",FACE,{"disambiguationData":[TD([[makeQuery(id+"F0.imprint","IMPRINT",EDGE,{"disambiguationData":[TD([[subQ2,-1.0]])],"derivedFrom":subQ1}),-1.0]])]});}
            var Q765;
            {var subQ0=sQuery(id+"F0.wireOp",EDGE,"E26");var subQ1=sQuery(id+"F0.wireOp",EDGE,"E23");var subQ2=makeQuery(id+"F0.imprint","INTERSECT",VERTEX,{"derivedFrom":[subQ1,subQ0]});Q765=makeQuery(id+"F0.imprint","IMPRINT",FACE,{"disambiguationData":[TD([[makeQuery(id+"F0.imprint","IMPRINT",EDGE,{"disambiguationData":[TD([[subQ2,-1.0]])],"derivedFrom":subQ1}),-1.0]])]});}
            var Q766;
            {var subQ1=sQuery(id+"F0.wireOp",EDGE,"E27");var subQ7=sQuery(id+"F0.wireOp",EDGE,"E19");var subQ8=makeQuery(id+"F0.imprint","INTERSECT",VERTEX,{"derivedFrom":[subQ7,subQ1]});Q766=makeQuery(id+"F0.imprint","IMPRINT",FACE,{"disambiguationData":[TD([[makeQuery(id+"F0.imprint","IMPRINT",EDGE,{"disambiguationData":[TD([[subQ8,-1.0]])],"derivedFrom":subQ7}),1.0]])]});}
            var Q767;
            {var subQ1=sQuery(id+"F0.wireOp",EDGE,"E24");var subQ3=sQuery(id+"F0.wireOp",EDGE,"E26");var subQ4=makeQuery(id+"F0.imprint","INTERSECT",VERTEX,{"derivedFrom":[subQ1,subQ3]});Q767=makeQuery(id+"F0.imprint","IMPRINT",FACE,{"disambiguationData":[TD([[makeQuery(id+"F0.imprint","IMPRINT",EDGE,{"disambiguationData":[TD([[subQ4,1.0]])],"derivedFrom":subQ3}),1.0]])]});}
            var Q768;
            {var subQ0=sQuery(id+"F0.wireOp",EDGE,"E49");var subQ1=sQuery(id+"F0.wireOp",EDGE,"E24");var subQ2=makeQuery(id+"F0.imprint","INTERSECT",VERTEX,{"derivedFrom":[subQ1,subQ0]});Q768=makeQuery(id+"F0.imprint","IMPRINT",FACE,{"disambiguationData":[TD([[makeQuery(id+"F0.imprint","IMPRINT",EDGE,{"disambiguationData":[TD([[subQ2,-1.0]])],"derivedFrom":subQ1}),1.0]])]});}
            var Q769;
            {var subQ1=sQuery(id+"F0.wireOp",EDGE,"E21");var subQ5=sQuery(id+"F0.wireOp",EDGE,"E44");var subQ6=makeQuery(id+"F0.imprint","INTERSECT",VERTEX,{"derivedFrom":[subQ1,subQ5]});Q769=makeQuery(id+"F0.imprint","IMPRINT",FACE,{"disambiguationData":[TD([[makeQuery(id+"F0.imprint","IMPRINT",EDGE,{"disambiguationData":[TD([[subQ6,-1.0]])],"derivedFrom":subQ1}),-1.0]])]});}
            var Q770;
            {var subQ0=sQuery(id+"F0.wireOp",EDGE,"E47");var subQ1=sQuery(id+"F0.wireOp",EDGE,"E22");var subQ2=makeQuery(id+"F0.imprint","INTERSECT",VERTEX,{"derivedFrom":[subQ1,subQ0]});Q770=makeQuery(id+"F0.imprint","IMPRINT",FACE,{"disambiguationData":[TD([[makeQuery(id+"F0.imprint","IMPRINT",EDGE,{"disambiguationData":[TD([[subQ2,-1.0]])],"derivedFrom":subQ1}),-1.0]])]});}
            var Q771;
            {var subQ1=sQuery(id+"F0.wireOp",EDGE,"E37");var subQ7=sQuery(id+"F0.wireOp",EDGE,"E53");var subQ9=makeQuery(id+"F0.imprint","INTERSECT",VERTEX,{"derivedFrom":[subQ1,subQ7]});Q771=makeQuery(id+"F0.imprint","IMPRINT",FACE,{"disambiguationData":[TD([[makeQuery(id+"F0.imprint","IMPRINT",EDGE,{"disambiguationData":[TD([[subQ9,-1.0]])],"derivedFrom":subQ1}),1.0]])]});}
            var Q772;
            {var subQ0=sQuery(id+"F0.wireOp",EDGE,"E45");var subQ1=sQuery(id+"F0.wireOp",EDGE,"E18");var subQ2=makeQuery(id+"F0.imprint","INTERSECT",VERTEX,{"derivedFrom":[subQ1,subQ0]});Q772=makeQuery(id+"F0.imprint","IMPRINT",FACE,{"disambiguationData":[TD([[makeQuery(id+"F0.imprint","IMPRINT",EDGE,{"disambiguationData":[TD([[subQ2,-1.0]])],"derivedFrom":subQ1}),-1.0]])]});}
            var Q773;
            {var subQ0=sQuery(id+"F0.wireOp",EDGE,"E45");var subQ1=sQuery(id+"F0.wireOp",EDGE,"E22");var subQ2=makeQuery(id+"F0.imprint","INTERSECT",VERTEX,{"derivedFrom":[subQ1,subQ0]});Q773=makeQuery(id+"F0.imprint","IMPRINT",FACE,{"disambiguationData":[TD([[makeQuery(id+"F0.imprint","IMPRINT",EDGE,{"disambiguationData":[TD([[subQ2,-1.0]])],"derivedFrom":subQ1}),-1.0]])]});}
            var Q774;
            {var subQ0=sQuery(id+"F0.wireOp",EDGE,"E3");var subQ1=sQuery(id+"F0.wireOp",EDGE,"E2");var subQ2=makeQuery(id+"F0.imprint","INTERSECT",VERTEX,{"derivedFrom":[subQ1,subQ0]});Q774=makeQuery(id+"F0.imprint","IMPRINT",FACE,{"disambiguationData":[TD([[makeQuery(id+"F0.imprint","IMPRINT",EDGE,{"disambiguationData":[TD([[subQ2,-1.0]])],"derivedFrom":subQ1}),1.0]])]});}
            var Q775;
            {var subQ0=sQuery(id+"F0.wireOp",EDGE,"E55");var subQ1=sQuery(id+"F0.wireOp",EDGE,"E28");var subQ2=makeQuery(id+"F0.imprint","INTERSECT",VERTEX,{"derivedFrom":[subQ1,subQ0]});Q775=makeQuery(id+"F0.imprint","IMPRINT",FACE,{"disambiguationData":[TD([[makeQuery(id+"F0.imprint","IMPRINT",EDGE,{"disambiguationData":[TD([[subQ2,-1.0]])],"derivedFrom":subQ1}),1.0]])]});}
            var Q776;
            {var subQ0=sQuery(id+"F0.wireOp",EDGE,"E45");var subQ1=sQuery(id+"F0.wireOp",EDGE,"E19");var subQ2=makeQuery(id+"F0.imprint","INTERSECT",VERTEX,{"derivedFrom":[subQ1,subQ0]});Q776=makeQuery(id+"F0.imprint","IMPRINT",FACE,{"disambiguationData":[TD([[makeQuery(id+"F0.imprint","IMPRINT",EDGE,{"disambiguationData":[TD([[subQ2,-1.0]])],"derivedFrom":subQ1}),1.0]])]});}
            var Q777;
            {var subQ0=sQuery(id+"F0.wireOp",EDGE,"E51");var subQ1=sQuery(id+"F0.wireOp",EDGE,"E22");var subQ2=makeQuery(id+"F0.imprint","INTERSECT",VERTEX,{"derivedFrom":[subQ1,subQ0]});Q777=makeQuery(id+"F0.imprint","IMPRINT",FACE,{"disambiguationData":[TD([[makeQuery(id+"F0.imprint","IMPRINT",EDGE,{"disambiguationData":[TD([[subQ2,-1.0]])],"derivedFrom":subQ1}),1.0]])]});}
            var Q778;
            {var subQ0=sQuery(id+"F0.wireOp",EDGE,"E45");var subQ1=sQuery(id+"F0.wireOp",EDGE,"E27");var subQ2=makeQuery(id+"F0.imprint","INTERSECT",VERTEX,{"derivedFrom":[subQ1,subQ0]});Q778=makeQuery(id+"F0.imprint","IMPRINT",FACE,{"disambiguationData":[TD([[makeQuery(id+"F0.imprint","IMPRINT",EDGE,{"disambiguationData":[TD([[subQ2,-1.0]])],"derivedFrom":subQ1}),-1.0]])]});}
            var Q779;
            {var subQ0=sQuery(id+"F0.wireOp",EDGE,"E44");var subQ1=sQuery(id+"F0.wireOp",EDGE,"E24");var subQ2=makeQuery(id+"F0.imprint","INTERSECT",VERTEX,{"derivedFrom":[subQ1,subQ0]});Q779=makeQuery(id+"F0.imprint","IMPRINT",FACE,{"disambiguationData":[TD([[makeQuery(id+"F0.imprint","IMPRINT",EDGE,{"disambiguationData":[TD([[subQ2,-1.0]])],"derivedFrom":subQ1}),-1.0]])]});}
            var Q780;
            {var subQ0=sQuery(id+"F0.wireOp",EDGE,"E47");var subQ1=sQuery(id+"F0.wireOp",EDGE,"E20");var subQ2=makeQuery(id+"F0.imprint","INTERSECT",VERTEX,{"derivedFrom":[subQ1,subQ0]});Q780=makeQuery(id+"F0.imprint","IMPRINT",FACE,{"disambiguationData":[TD([[makeQuery(id+"F0.imprint","IMPRINT",EDGE,{"disambiguationData":[TD([[subQ2,-1.0]])],"derivedFrom":subQ1}),1.0]])]});}
            var Q781;
            {var subQ0=sQuery(id+"F0.wireOp",EDGE,"E13");var subQ1=sQuery(id+"F0.wireOp",EDGE,"E10");var subQ2=makeQuery(id+"F0.imprint","INTERSECT",VERTEX,{"derivedFrom":[subQ1,subQ0]});Q781=makeQuery(id+"F0.imprint","IMPRINT",FACE,{"disambiguationData":[TD([[makeQuery(id+"F0.imprint","IMPRINT",EDGE,{"disambiguationData":[TD([[subQ2,-1.0]])],"derivedFrom":subQ1}),1.0]])]});}
            var Q782;
            {var subQ0=sQuery(id+"F0.wireOp",EDGE,"E46");var subQ1=sQuery(id+"F0.wireOp",EDGE,"E24");var subQ2=makeQuery(id+"F0.imprint","INTERSECT",VERTEX,{"derivedFrom":[subQ1,subQ0]});Q782=makeQuery(id+"F0.imprint","IMPRINT",FACE,{"disambiguationData":[TD([[makeQuery(id+"F0.imprint","IMPRINT",EDGE,{"disambiguationData":[TD([[subQ2,-1.0]])],"derivedFrom":subQ1}),-1.0]])]});}
            var Q783;
            {var subQ1=sQuery(id+"F0.wireOp",EDGE,"E25");var subQ3=sQuery(id+"F0.wireOp",EDGE,"E26");var subQ4=makeQuery(id+"F0.imprint","INTERSECT",VERTEX,{"derivedFrom":[subQ1,subQ3]});Q783=makeQuery(id+"F0.imprint","IMPRINT",FACE,{"disambiguationData":[TD([[makeQuery(id+"F0.imprint","IMPRINT",EDGE,{"disambiguationData":[TD([[subQ4,-1.0]])],"derivedFrom":subQ3}),1.0]])]});}
            var Q784;
            {var subQ0=sQuery(id+"F0.wireOp",EDGE,"E48");var subQ1=sQuery(id+"F0.wireOp",EDGE,"E19");var subQ2=makeQuery(id+"F0.imprint","INTERSECT",VERTEX,{"derivedFrom":[subQ1,subQ0]});Q784=makeQuery(id+"F0.imprint","IMPRINT",FACE,{"disambiguationData":[TD([[makeQuery(id+"F0.imprint","IMPRINT",EDGE,{"disambiguationData":[TD([[subQ2,-1.0]])],"derivedFrom":subQ1}),1.0]])]});}
            var Q785;
            {var subQ0=sQuery(id+"F0.wireOp",EDGE,"E57");var subQ1=sQuery(id+"F0.wireOp",EDGE,"E38");var subQ2=makeQuery(id+"F0.imprint","INTERSECT",VERTEX,{"derivedFrom":[subQ1,subQ0]});Q785=makeQuery(id+"F0.imprint","IMPRINT",FACE,{"disambiguationData":[TD([[makeQuery(id+"F0.imprint","IMPRINT",EDGE,{"disambiguationData":[TD([[subQ2,-1.0]])],"derivedFrom":subQ1}),1.0]])]});}
            var Q786;
            {var subQ0=sQuery(id+"F0.wireOp",EDGE,"E44");var subQ1=sQuery(id+"F0.wireOp",EDGE,"E23");var subQ2=makeQuery(id+"F0.imprint","INTERSECT",VERTEX,{"derivedFrom":[subQ1,subQ0]});Q786=makeQuery(id+"F0.imprint","IMPRINT",FACE,{"disambiguationData":[TD([[makeQuery(id+"F0.imprint","IMPRINT",EDGE,{"disambiguationData":[TD([[subQ2,-1.0]])],"derivedFrom":subQ1}),-1.0]])]});}
            var Q787;
            {var subQ0=sQuery(id+"F0.wireOp",EDGE,"E52");var subQ1=sQuery(id+"F0.wireOp",EDGE,"E24");var subQ2=makeQuery(id+"F0.imprint","INTERSECT",VERTEX,{"derivedFrom":[subQ1,subQ0]});Q787=makeQuery(id+"F0.imprint","IMPRINT",FACE,{"disambiguationData":[TD([[makeQuery(id+"F0.imprint","IMPRINT",EDGE,{"disambiguationData":[TD([[subQ2,-1.0]])],"derivedFrom":subQ1}),-1.0]])]});}
            var Q788;
            {var subQ0=sQuery(id+"F0.wireOp",EDGE,"E25");var subQ1=sQuery(id+"F0.wireOp",EDGE,"E22");var subQ2=makeQuery(id+"F0.imprint","INTERSECT",VERTEX,{"derivedFrom":[subQ1,subQ0]});Q788=makeQuery(id+"F0.imprint","IMPRINT",FACE,{"disambiguationData":[TD([[makeQuery(id+"F0.imprint","IMPRINT",EDGE,{"disambiguationData":[TD([[subQ2,-1.0]])],"derivedFrom":subQ1}),-1.0]])]});}
            var Q789;
            {var subQ0=sQuery(id+"F0.wireOp",EDGE,"E53");var subQ1=sQuery(id+"F0.wireOp",EDGE,"E37");var subQ2=makeQuery(id+"F0.imprint","INTERSECT",VERTEX,{"derivedFrom":[subQ1,subQ0]});Q789=makeQuery(id+"F0.imprint","IMPRINT",FACE,{"disambiguationData":[TD([[makeQuery(id+"F0.imprint","IMPRINT",EDGE,{"disambiguationData":[TD([[subQ2,-1.0]])],"derivedFrom":subQ1}),-1.0]])]});}
            var Q790;
            {var subQ0=sQuery(id+"F0.wireOp",EDGE,"E43");var subQ1=sQuery(id+"F0.wireOp",EDGE,"E10");var subQ2=makeQuery(id+"F0.imprint","INTERSECT",VERTEX,{"derivedFrom":[subQ1,subQ0]});Q790=makeQuery(id+"F0.imprint","IMPRINT",FACE,{"disambiguationData":[TD([[makeQuery(id+"F0.imprint","IMPRINT",EDGE,{"disambiguationData":[TD([[subQ2,-1.0]])],"derivedFrom":subQ1}),-1.0]])]});}
            var Q791;
            {var subQ0=sQuery(id+"F0.wireOp",EDGE,"E48");var subQ1=sQuery(id+"F0.wireOp",EDGE,"E21");var subQ2=makeQuery(id+"F0.imprint","INTERSECT",VERTEX,{"derivedFrom":[subQ1,subQ0]});Q791=makeQuery(id+"F0.imprint","IMPRINT",FACE,{"disambiguationData":[TD([[makeQuery(id+"F0.imprint","IMPRINT",EDGE,{"disambiguationData":[TD([[subQ2,-1.0]])],"derivedFrom":subQ1}),-1.0]])]});}
            var Q792;
            {var subQ0=sQuery(id+"F0.wireOp",EDGE,"E52");var subQ1=sQuery(id+"F0.wireOp",EDGE,"E28");var subQ2=makeQuery(id+"F0.imprint","INTERSECT",VERTEX,{"derivedFrom":[subQ1,subQ0]});Q792=makeQuery(id+"F0.imprint","IMPRINT",FACE,{"disambiguationData":[TD([[makeQuery(id+"F0.imprint","IMPRINT",EDGE,{"disambiguationData":[TD([[subQ2,-1.0]])],"derivedFrom":subQ1}),1.0]])]});}
            var Q793;
            {var subQ0=sQuery(id+"F0.wireOp",EDGE,"E12");var subQ1=sQuery(id+"F0.wireOp",EDGE,"E11");var subQ2=makeQuery(id+"F0.imprint","INTERSECT",VERTEX,{"derivedFrom":[subQ1,subQ0]});Q793=makeQuery(id+"F0.imprint","IMPRINT",FACE,{"disambiguationData":[TD([[makeQuery(id+"F0.imprint","IMPRINT",EDGE,{"disambiguationData":[TD([[subQ2,-1.0]])],"derivedFrom":subQ1}),1.0]])]});}
            var Q794;
            {var subQ0=sQuery(id+"F0.wireOp",EDGE,"E48");var subQ1=sQuery(id+"F0.wireOp",EDGE,"E21");var subQ2=makeQuery(id+"F0.imprint","INTERSECT",VERTEX,{"derivedFrom":[subQ1,subQ0]});Q794=makeQuery(id+"F0.imprint","IMPRINT",FACE,{"disambiguationData":[TD([[makeQuery(id+"F0.imprint","IMPRINT",EDGE,{"disambiguationData":[TD([[subQ2,-1.0]])],"derivedFrom":subQ1}),1.0]])]});}
            var Q795;
            {var subQ0=sQuery(id+"F0.wireOp",EDGE,"E45");var subQ1=sQuery(id+"F0.wireOp",EDGE,"E23");var subQ2=makeQuery(id+"F0.imprint","INTERSECT",VERTEX,{"derivedFrom":[subQ1,subQ0]});Q795=makeQuery(id+"F0.imprint","IMPRINT",FACE,{"disambiguationData":[TD([[makeQuery(id+"F0.imprint","IMPRINT",EDGE,{"disambiguationData":[TD([[subQ2,-1.0]])],"derivedFrom":subQ1}),-1.0]])]});}
            var Q796;
            {var subQ0=sQuery(id+"F0.wireOp",EDGE,"E50");var subQ1=sQuery(id+"F0.wireOp",EDGE,"E23");var subQ2=makeQuery(id+"F0.imprint","INTERSECT",VERTEX,{"derivedFrom":[subQ1,subQ0]});Q796=makeQuery(id+"F0.imprint","IMPRINT",FACE,{"disambiguationData":[TD([[makeQuery(id+"F0.imprint","IMPRINT",EDGE,{"disambiguationData":[TD([[subQ2,-1.0]])],"derivedFrom":subQ1}),1.0]])]});}
            var Q797;
            {var subQ0=sQuery(id+"F0.wireOp",EDGE,"E46");var subQ1=sQuery(id+"F0.wireOp",EDGE,"E18");var subQ2=makeQuery(id+"F0.imprint","INTERSECT",VERTEX,{"derivedFrom":[subQ1,subQ0]});Q797=makeQuery(id+"F0.imprint","IMPRINT",FACE,{"disambiguationData":[TD([[makeQuery(id+"F0.imprint","IMPRINT",EDGE,{"disambiguationData":[TD([[subQ2,-1.0]])],"derivedFrom":subQ1}),-1.0]])]});}
            var Q798;
            {var subQ0=sQuery(id+"F0.wireOp",EDGE,"E53");var subQ1=sQuery(id+"F0.wireOp",EDGE,"E24");var subQ2=makeQuery(id+"F0.imprint","INTERSECT",VERTEX,{"derivedFrom":[subQ1,subQ0]});Q798=makeQuery(id+"F0.imprint","IMPRINT",FACE,{"disambiguationData":[TD([[makeQuery(id+"F0.imprint","IMPRINT",EDGE,{"disambiguationData":[TD([[subQ2,-1.0]])],"derivedFrom":subQ1}),1.0]])]});}
            var Q799;
            {var subQ0=sQuery(id+"F0.wireOp",EDGE,"E46");var subQ1=sQuery(id+"F0.wireOp",EDGE,"E19");var subQ2=makeQuery(id+"F0.imprint","INTERSECT",VERTEX,{"derivedFrom":[subQ1,subQ0]});Q799=makeQuery(id+"F0.imprint","IMPRINT",FACE,{"disambiguationData":[TD([[makeQuery(id+"F0.imprint","IMPRINT",EDGE,{"disambiguationData":[TD([[subQ2,-1.0]])],"derivedFrom":subQ1}),1.0]])]});}
            var Q800;
            {var subQ0=sQuery(id+"F0.wireOp",EDGE,"E49");var subQ1=sQuery(id+"F0.wireOp",EDGE,"E21");var subQ2=makeQuery(id+"F0.imprint","INTERSECT",VERTEX,{"derivedFrom":[subQ1,subQ0]});Q800=makeQuery(id+"F0.imprint","IMPRINT",FACE,{"disambiguationData":[TD([[makeQuery(id+"F0.imprint","IMPRINT",EDGE,{"disambiguationData":[TD([[subQ2,-1.0]])],"derivedFrom":subQ1}),1.0]])]});}
            var Q801;
            {var subQ0=sQuery(id+"F0.wireOp",EDGE,"E25");var subQ1=sQuery(id+"F0.wireOp",EDGE,"E1");var subQ2=makeQuery(id+"F0.imprint","INTERSECT",VERTEX,{"derivedFrom":[subQ1,subQ0]});Q801=makeQuery(id+"F0.imprint","IMPRINT",FACE,{"disambiguationData":[TD([[makeQuery(id+"F0.imprint","IMPRINT",EDGE,{"disambiguationData":[TD([[subQ2,-1.0]])],"derivedFrom":subQ1}),-1.0]])]});}
            var Q802;
            {var subQ0=sQuery(id+"F0.wireOp",EDGE,"E47");var subQ1=sQuery(id+"F0.wireOp",EDGE,"E23");var subQ2=makeQuery(id+"F0.imprint","INTERSECT",VERTEX,{"derivedFrom":[subQ1,subQ0]});Q802=makeQuery(id+"F0.imprint","IMPRINT",FACE,{"disambiguationData":[TD([[makeQuery(id+"F0.imprint","IMPRINT",EDGE,{"disambiguationData":[TD([[subQ2,-1.0]])],"derivedFrom":subQ1}),1.0]])]});}
            var Q803;
            {var subQ0=sQuery(id+"F0.wireOp",EDGE,"E45");var subQ1=sQuery(id+"F0.wireOp",EDGE,"E21");var subQ2=makeQuery(id+"F0.imprint","INTERSECT",VERTEX,{"derivedFrom":[subQ1,subQ0]});Q803=makeQuery(id+"F0.imprint","IMPRINT",FACE,{"disambiguationData":[TD([[makeQuery(id+"F0.imprint","IMPRINT",EDGE,{"disambiguationData":[TD([[subQ2,-1.0]])],"derivedFrom":subQ1}),-1.0]])]});}
            var Q804;
            {var subQ0=sQuery(id+"F0.wireOp",EDGE,"E25");var subQ1=sQuery(id+"F0.wireOp",EDGE,"E24");var subQ2=makeQuery(id+"F0.imprint","INTERSECT",VERTEX,{"derivedFrom":[subQ1,subQ0]});Q804=makeQuery(id+"F0.imprint","IMPRINT",FACE,{"disambiguationData":[TD([[makeQuery(id+"F0.imprint","IMPRINT",EDGE,{"disambiguationData":[TD([[subQ2,-1.0]])],"derivedFrom":subQ1}),-1.0]])]});}
            var Q805;
            {var subQ0=sQuery(id+"F0.wireOp",EDGE,"E51");var subQ1=sQuery(id+"F0.wireOp",EDGE,"E23");var subQ2=makeQuery(id+"F0.imprint","INTERSECT",VERTEX,{"derivedFrom":[subQ1,subQ0]});Q805=makeQuery(id+"F0.imprint","IMPRINT",FACE,{"disambiguationData":[TD([[makeQuery(id+"F0.imprint","IMPRINT",EDGE,{"disambiguationData":[TD([[subQ2,-1.0]])],"derivedFrom":subQ1}),1.0]])]});}
            var Q806;
            {var subQ3=sQuery(id+"F0.wireOp",EDGE,"E45");var subQ5=sQuery(id+"F0.wireOp",EDGE,"E23");var subQ6=makeQuery(id+"F0.imprint","INTERSECT",VERTEX,{"derivedFrom":[subQ5,subQ3]});Q806=makeQuery(id+"F0.imprint","IMPRINT",FACE,{"disambiguationData":[TD([[makeQuery(id+"F0.imprint","IMPRINT",EDGE,{"disambiguationData":[TD([[subQ6,-1.0]])],"derivedFrom":subQ5}),1.0]])]});}
            var Q807;
            {var subQ0=sQuery(id+"F0.wireOp",EDGE,"E31");var subQ1=sQuery(id+"F0.wireOp",EDGE,"E10");var subQ2=makeQuery(id+"F0.imprint","INTERSECT",VERTEX,{"derivedFrom":[subQ1,subQ0]});Q807=makeQuery(id+"F0.imprint","IMPRINT",FACE,{"disambiguationData":[TD([[makeQuery(id+"F0.imprint","IMPRINT",EDGE,{"disambiguationData":[TD([[subQ2,-1.0]])],"derivedFrom":subQ1}),-1.0]])]});}
            var Q808;
            {var subQ0=sQuery(id+"F0.wireOp",EDGE,"E30");var subQ1=sQuery(id+"F0.wireOp",EDGE,"E11");var subQ2=makeQuery(id+"F0.imprint","INTERSECT",VERTEX,{"derivedFrom":[subQ1,subQ0]});Q808=makeQuery(id+"F0.imprint","IMPRINT",FACE,{"disambiguationData":[TD([[makeQuery(id+"F0.imprint","IMPRINT",EDGE,{"disambiguationData":[TD([[subQ2,-1.0]])],"derivedFrom":subQ1}),-1.0]])]});}
            var Q809;
            {var subQ0=sQuery(id+"F0.wireOp",EDGE,"E57");var subQ1=sQuery(id+"F0.wireOp",EDGE,"E40");var subQ2=makeQuery(id+"F0.imprint","INTERSECT",VERTEX,{"derivedFrom":[subQ1,subQ0]});Q809=makeQuery(id+"F0.imprint","IMPRINT",FACE,{"disambiguationData":[TD([[makeQuery(id+"F0.imprint","IMPRINT",EDGE,{"disambiguationData":[TD([[subQ2,-1.0]])],"derivedFrom":subQ1}),-1.0]])]});}
            var Q810;
            {var subQ0=sQuery(id+"F0.wireOp",EDGE,"E54");var subQ1=sQuery(id+"F0.wireOp",EDGE,"E26");var subQ2=makeQuery(id+"F0.imprint","INTERSECT",VERTEX,{"derivedFrom":[subQ1,subQ0]});Q810=makeQuery(id+"F0.imprint","IMPRINT",FACE,{"disambiguationData":[TD([[makeQuery(id+"F0.imprint","IMPRINT",EDGE,{"disambiguationData":[TD([[subQ2,-1.0]])],"derivedFrom":subQ1}),1.0]])]});}
            var Q811;
            {var subQ0=sQuery(id+"F0.wireOp",EDGE,"E37");var subQ1=sQuery(id+"F0.wireOp",EDGE,"E28");var subQ2=makeQuery(id+"F0.imprint","INTERSECT",VERTEX,{"derivedFrom":[subQ1,subQ0]});Q811=makeQuery(id+"F0.imprint","IMPRINT",FACE,{"disambiguationData":[TD([[makeQuery(id+"F0.imprint","IMPRINT",EDGE,{"disambiguationData":[TD([[subQ2,-1.0]])],"derivedFrom":subQ1}),1.0]])]});}
            var Q812;
            {var subQ0=sQuery(id+"F0.wireOp",EDGE,"E52");var subQ1=sQuery(id+"F0.wireOp",EDGE,"E26");var subQ2=makeQuery(id+"F0.imprint","INTERSECT",VERTEX,{"derivedFrom":[subQ1,subQ0]});Q812=makeQuery(id+"F0.imprint","IMPRINT",FACE,{"disambiguationData":[TD([[makeQuery(id+"F0.imprint","IMPRINT",EDGE,{"disambiguationData":[TD([[subQ2,-1.0]])],"derivedFrom":subQ1}),1.0]])]});}
            var Q813;
            {var subQ0=sQuery(id+"F0.wireOp",EDGE,"E49");var subQ1=sQuery(id+"F0.wireOp",EDGE,"E27");var subQ2=makeQuery(id+"F0.imprint","INTERSECT",VERTEX,{"derivedFrom":[subQ1,subQ0]});Q813=makeQuery(id+"F0.imprint","IMPRINT",FACE,{"disambiguationData":[TD([[makeQuery(id+"F0.imprint","IMPRINT",EDGE,{"disambiguationData":[TD([[subQ2,-1.0]])],"derivedFrom":subQ1}),-1.0]])]});}
            var Q814;
            {var subQ0=sQuery(id+"F0.wireOp",EDGE,"E51");var subQ1=sQuery(id+"F0.wireOp",EDGE,"E24");var subQ2=makeQuery(id+"F0.imprint","INTERSECT",VERTEX,{"derivedFrom":[subQ1,subQ0]});Q814=makeQuery(id+"F0.imprint","IMPRINT",FACE,{"disambiguationData":[TD([[makeQuery(id+"F0.imprint","IMPRINT",EDGE,{"disambiguationData":[TD([[subQ2,-1.0]])],"derivedFrom":subQ1}),1.0]])]});}
            var Q815;
            {var subQ0=sQuery(id+"F0.wireOp",EDGE,"E48");var subQ1=sQuery(id+"F0.wireOp",EDGE,"E20");var subQ2=makeQuery(id+"F0.imprint","INTERSECT",VERTEX,{"derivedFrom":[subQ1,subQ0]});Q815=makeQuery(id+"F0.imprint","IMPRINT",FACE,{"disambiguationData":[TD([[makeQuery(id+"F0.imprint","IMPRINT",EDGE,{"disambiguationData":[TD([[subQ2,-1.0]])],"derivedFrom":subQ1}),1.0]])]});}
            var Q816;
            {var subQ0=sQuery(id+"F0.wireOp",EDGE,"E53");var subQ1=sQuery(id+"F0.wireOp",EDGE,"E29");var subQ2=makeQuery(id+"F0.imprint","INTERSECT",VERTEX,{"derivedFrom":[subQ1,subQ0]});Q816=makeQuery(id+"F0.imprint","IMPRINT",FACE,{"disambiguationData":[TD([[makeQuery(id+"F0.imprint","IMPRINT",EDGE,{"disambiguationData":[TD([[subQ2,-1.0]])],"derivedFrom":subQ1}),1.0]])]});}
            var Q817;
            {var subQ0=sQuery(id+"F0.wireOp",EDGE,"E46");var subQ1=sQuery(id+"F0.wireOp",EDGE,"E17");var subQ2=makeQuery(id+"F0.imprint","INTERSECT",VERTEX,{"derivedFrom":[subQ1,subQ0]});Q817=makeQuery(id+"F0.imprint","IMPRINT",FACE,{"disambiguationData":[TD([[makeQuery(id+"F0.imprint","IMPRINT",EDGE,{"disambiguationData":[TD([[subQ2,-1.0]])],"derivedFrom":subQ1}),1.0]])]});}
            var Q818;
            {var subQ0=sQuery(id+"F0.wireOp",EDGE,"E46");var subQ1=sQuery(id+"F0.wireOp",EDGE,"E24");var subQ2=makeQuery(id+"F0.imprint","INTERSECT",VERTEX,{"derivedFrom":[subQ1,subQ0]});Q818=makeQuery(id+"F0.imprint","IMPRINT",FACE,{"disambiguationData":[TD([[makeQuery(id+"F0.imprint","IMPRINT",EDGE,{"disambiguationData":[TD([[subQ2,-1.0]])],"derivedFrom":subQ1}),1.0]])]});}
            var Q819;
            {var subQ0=sQuery(id+"F0.wireOp",EDGE,"E45");var subQ1=sQuery(id+"F0.wireOp",EDGE,"E17");var subQ2=makeQuery(id+"F0.imprint","INTERSECT",VERTEX,{"derivedFrom":[subQ1,subQ0]});Q819=makeQuery(id+"F0.imprint","IMPRINT",FACE,{"disambiguationData":[TD([[makeQuery(id+"F0.imprint","IMPRINT",EDGE,{"disambiguationData":[TD([[subQ2,-1.0]])],"derivedFrom":subQ1}),-1.0]])]});}
            var Q820;
            {var subQ1=sQuery(id+"F0.wireOp",EDGE,"E25");var subQ3=sQuery(id+"F0.wireOp",EDGE,"E26");var subQ4=makeQuery(id+"F0.imprint","INTERSECT",VERTEX,{"derivedFrom":[subQ1,subQ3]});Q820=makeQuery(id+"F0.imprint","IMPRINT",FACE,{"disambiguationData":[TD([[makeQuery(id+"F0.imprint","IMPRINT",EDGE,{"disambiguationData":[TD([[subQ4,1.0]])],"derivedFrom":subQ3}),1.0]])]});}
            var Q821;
            {var subQ0=sQuery(id+"F0.wireOp",EDGE,"E13");var subQ1=sQuery(id+"F0.wireOp",EDGE,"E11");var subQ2=makeQuery(id+"F0.imprint","INTERSECT",VERTEX,{"derivedFrom":[subQ1,subQ0]});Q821=makeQuery(id+"F0.imprint","IMPRINT",FACE,{"disambiguationData":[TD([[makeQuery(id+"F0.imprint","IMPRINT",EDGE,{"disambiguationData":[TD([[subQ2,-1.0]])],"derivedFrom":subQ1}),-1.0]])]});}
            var Q822;
            {var subQ0=sQuery(id+"F0.wireOp",EDGE,"E49");var subQ1=sQuery(id+"F0.wireOp",EDGE,"E23");var subQ2=makeQuery(id+"F0.imprint","INTERSECT",VERTEX,{"derivedFrom":[subQ1,subQ0]});Q822=makeQuery(id+"F0.imprint","IMPRINT",FACE,{"disambiguationData":[TD([[makeQuery(id+"F0.imprint","IMPRINT",EDGE,{"disambiguationData":[TD([[subQ2,-1.0]])],"derivedFrom":subQ1}),-1.0]])]});}
            var Q823;
            {var subQ0=sQuery(id+"F0.wireOp",EDGE,"E46");var subQ1=sQuery(id+"F0.wireOp",EDGE,"E29");var subQ2=makeQuery(id+"F0.imprint","INTERSECT",VERTEX,{"derivedFrom":[subQ1,subQ0]});Q823=makeQuery(id+"F0.imprint","IMPRINT",FACE,{"disambiguationData":[TD([[makeQuery(id+"F0.imprint","IMPRINT",EDGE,{"disambiguationData":[TD([[subQ2,-1.0]])],"derivedFrom":subQ1}),1.0]])]});}
            var Q824;
            {var subQ1=sQuery(id+"F0.wireOp",EDGE,"E35");var subQ10=sQuery(id+"F0.wireOp",EDGE,"E29");var subQ11=makeQuery(id+"F0.imprint","INTERSECT",VERTEX,{"derivedFrom":[subQ10,subQ1]});Q824=makeQuery(id+"F0.imprint","IMPRINT",FACE,{"disambiguationData":[TD([[makeQuery(id+"F0.imprint","IMPRINT",EDGE,{"disambiguationData":[TD([[subQ11,-1.0]])],"derivedFrom":subQ10}),1.0]])]});}
            var Q825;
            {var subQ11=sQuery(id+"F0.wireOp",EDGE,"E36");var subQ12=sQuery(id+"F0.wireOp",EDGE,"E28");var subQ13=makeQuery(id+"F0.imprint","INTERSECT",VERTEX,{"derivedFrom":[subQ12,subQ11]});Q825=makeQuery(id+"F0.imprint","IMPRINT",FACE,{"disambiguationData":[TD([[makeQuery(id+"F0.imprint","IMPRINT",EDGE,{"disambiguationData":[TD([[subQ13,-1.0]])],"derivedFrom":subQ12}),1.0]])]});}
            var Q826;
            {var subQ0=sQuery(id+"F0.wireOp",EDGE,"E54");var subQ1=sQuery(id+"F0.wireOp",EDGE,"E25");var subQ2=makeQuery(id+"F0.imprint","INTERSECT",VERTEX,{"derivedFrom":[subQ1,subQ0]});Q826=makeQuery(id+"F0.imprint","IMPRINT",FACE,{"disambiguationData":[TD([[makeQuery(id+"F0.imprint","IMPRINT",EDGE,{"disambiguationData":[TD([[subQ2,-1.0]])],"derivedFrom":subQ1}),1.0]])]});}
            var Q827;
            {var subQ0=sQuery(id+"F0.wireOp",EDGE,"E26");var subQ1=sQuery(id+"F0.wireOp",EDGE,"E23");var subQ2=makeQuery(id+"F0.imprint","INTERSECT",VERTEX,{"derivedFrom":[subQ1,subQ0]});Q827=makeQuery(id+"F0.imprint","IMPRINT",FACE,{"disambiguationData":[TD([[makeQuery(id+"F0.imprint","IMPRINT",EDGE,{"disambiguationData":[TD([[subQ2,-1.0]])],"derivedFrom":subQ1}),1.0]])]});}
            var Q828;
            {var subQ1=sQuery(id+"F0.wireOp",EDGE,"E28");var subQ8=sQuery(id+"F0.wireOp",EDGE,"E46");var subQ11=makeQuery(id+"F0.imprint","INTERSECT",VERTEX,{"derivedFrom":[subQ1,subQ8]});Q828=makeQuery(id+"F0.imprint","IMPRINT",FACE,{"disambiguationData":[TD([[makeQuery(id+"F0.imprint","IMPRINT",EDGE,{"disambiguationData":[TD([[subQ11,-1.0]])],"derivedFrom":subQ1}),-1.0]])]});}
            var Q829;
            {var subQ0=sQuery(id+"F0.wireOp",EDGE,"E25");var subQ1=sQuery(id+"F0.wireOp",EDGE,"E23");var subQ2=makeQuery(id+"F0.imprint","INTERSECT",VERTEX,{"derivedFrom":[subQ1,subQ0]});Q829=makeQuery(id+"F0.imprint","IMPRINT",FACE,{"disambiguationData":[TD([[makeQuery(id+"F0.imprint","IMPRINT",EDGE,{"disambiguationData":[TD([[subQ2,-1.0]])],"derivedFrom":subQ1}),-1.0]])]});}
            var Q830;
            {var subQ1=sQuery(id+"F0.wireOp",EDGE,"E38");var subQ5=sQuery(id+"F0.wireOp",EDGE,"E56");var subQ6=makeQuery(id+"F0.imprint","INTERSECT",VERTEX,{"derivedFrom":[subQ1,subQ5]});Q830=makeQuery(id+"F0.imprint","IMPRINT",FACE,{"disambiguationData":[TD([[makeQuery(id+"F0.imprint","IMPRINT",EDGE,{"disambiguationData":[TD([[subQ6,-1.0]])],"derivedFrom":subQ1}),1.0]])]});}
            var Q831;
            {var subQ0=sQuery(id+"F0.wireOp",EDGE,"E52");var subQ1=sQuery(id+"F0.wireOp",EDGE,"E24");var subQ2=makeQuery(id+"F0.imprint","INTERSECT",VERTEX,{"derivedFrom":[subQ1,subQ0]});Q831=makeQuery(id+"F0.imprint","IMPRINT",FACE,{"disambiguationData":[TD([[makeQuery(id+"F0.imprint","IMPRINT",EDGE,{"disambiguationData":[TD([[subQ2,-1.0]])],"derivedFrom":subQ1}),1.0]])]});}
            var Q832;
            {var subQ0=sQuery(id+"F0.wireOp",EDGE,"E57");var subQ1=sQuery(id+"F0.wireOp",EDGE,"E37");var subQ2=makeQuery(id+"F0.imprint","INTERSECT",VERTEX,{"derivedFrom":[subQ1,subQ0]});Q832=makeQuery(id+"F0.imprint","IMPRINT",FACE,{"disambiguationData":[TD([[makeQuery(id+"F0.imprint","IMPRINT",EDGE,{"disambiguationData":[TD([[subQ2,-1.0]])],"derivedFrom":subQ1}),1.0]])]});}
            var Q833;
            {var subQ0=sQuery(id+"F0.wireOp",EDGE,"E56");var subQ1=sQuery(id+"F0.wireOp",EDGE,"E37");var subQ2=makeQuery(id+"F0.imprint","INTERSECT",VERTEX,{"derivedFrom":[subQ1,subQ0]});Q833=makeQuery(id+"F0.imprint","IMPRINT",FACE,{"disambiguationData":[TD([[makeQuery(id+"F0.imprint","IMPRINT",EDGE,{"disambiguationData":[TD([[subQ2,-1.0]])],"derivedFrom":subQ1}),1.0]])]});}
            var Q834;
            {var subQ0=sQuery(id+"F0.wireOp",EDGE,"E50");var subQ1=sQuery(id+"F0.wireOp",EDGE,"E23");var subQ2=makeQuery(id+"F0.imprint","INTERSECT",VERTEX,{"derivedFrom":[subQ1,subQ0]});Q834=makeQuery(id+"F0.imprint","IMPRINT",FACE,{"disambiguationData":[TD([[makeQuery(id+"F0.imprint","IMPRINT",EDGE,{"disambiguationData":[TD([[subQ2,-1.0]])],"derivedFrom":subQ1}),-1.0]])]});}
            var Q835;
            {var subQ0=sQuery(id+"F0.wireOp",EDGE,"E44");var subQ1=sQuery(id+"F0.wireOp",EDGE,"E20");var subQ2=makeQuery(id+"F0.imprint","INTERSECT",VERTEX,{"derivedFrom":[subQ1,subQ0]});Q835=makeQuery(id+"F0.imprint","IMPRINT",FACE,{"disambiguationData":[TD([[makeQuery(id+"F0.imprint","IMPRINT",EDGE,{"disambiguationData":[TD([[subQ2,-1.0]])],"derivedFrom":subQ1}),-1.0]])]});}
            var Q836;
            {var subQ0=sQuery(id+"F0.wireOp",EDGE,"E30");var subQ1=sQuery(id+"F0.wireOp",EDGE,"E28");var subQ2=makeQuery(id+"F0.imprint","INTERSECT",VERTEX,{"derivedFrom":[subQ1,subQ0]});Q836=makeQuery(id+"F0.imprint","IMPRINT",FACE,{"disambiguationData":[TD([[makeQuery(id+"F0.imprint","IMPRINT",EDGE,{"disambiguationData":[TD([[subQ2,-1.0]])],"derivedFrom":subQ1}),-1.0]])]});}
            var Q837;
            {var subQ0=sQuery(id+"F0.wireOp",EDGE,"E51");var subQ1=sQuery(id+"F0.wireOp",EDGE,"E28");var subQ2=makeQuery(id+"F0.imprint","INTERSECT",VERTEX,{"derivedFrom":[subQ1,subQ0]});Q837=makeQuery(id+"F0.imprint","IMPRINT",FACE,{"disambiguationData":[TD([[makeQuery(id+"F0.imprint","IMPRINT",EDGE,{"disambiguationData":[TD([[subQ2,-1.0]])],"derivedFrom":subQ1}),1.0]])]});}
            var Q838;
            {var subQ0=sQuery(id+"F0.wireOp",EDGE,"E45");var subQ1=sQuery(id+"F0.wireOp",EDGE,"E24");var subQ2=makeQuery(id+"F0.imprint","INTERSECT",VERTEX,{"derivedFrom":[subQ1,subQ0]});Q838=makeQuery(id+"F0.imprint","IMPRINT",FACE,{"disambiguationData":[TD([[makeQuery(id+"F0.imprint","IMPRINT",EDGE,{"disambiguationData":[TD([[subQ2,-1.0]])],"derivedFrom":subQ1}),-1.0]])]});}
            var Q839;
            {var subQ0=sQuery(id+"F0.wireOp",EDGE,"E27");var subQ1=sQuery(id+"F0.wireOp",EDGE,"E18");var subQ2=makeQuery(id+"F0.imprint","INTERSECT",VERTEX,{"derivedFrom":[subQ1,subQ0]});Q839=makeQuery(id+"F0.imprint","IMPRINT",FACE,{"disambiguationData":[TD([[makeQuery(id+"F0.imprint","IMPRINT",EDGE,{"disambiguationData":[TD([[subQ2,-1.0]])],"derivedFrom":subQ1}),-1.0]])]});}
            var Q840;
            {var subQ0=sQuery(id+"F0.wireOp",EDGE,"E52");var subQ1=sQuery(id+"F0.wireOp",EDGE,"E36");var subQ2=makeQuery(id+"F0.imprint","INTERSECT",VERTEX,{"derivedFrom":[subQ1,subQ0]});Q840=makeQuery(id+"F0.imprint","IMPRINT",FACE,{"disambiguationData":[TD([[makeQuery(id+"F0.imprint","IMPRINT",EDGE,{"disambiguationData":[TD([[subQ2,-1.0]])],"derivedFrom":subQ1}),1.0]])]});}
            var Q841;
            {var subQ0=sQuery(id+"F0.wireOp",EDGE,"E52");var subQ1=sQuery(id+"F0.wireOp",EDGE,"E28");var subQ2=makeQuery(id+"F0.imprint","INTERSECT",VERTEX,{"derivedFrom":[subQ1,subQ0]});Q841=makeQuery(id+"F0.imprint","IMPRINT",FACE,{"disambiguationData":[TD([[makeQuery(id+"F0.imprint","IMPRINT",EDGE,{"disambiguationData":[TD([[subQ2,-1.0]])],"derivedFrom":subQ1}),-1.0]])]});}
            var Q842;
            {var subQ0=sQuery(id+"F0.wireOp",EDGE,"E45");var subQ1=sQuery(id+"F0.wireOp",EDGE,"E16");var subQ2=makeQuery(id+"F0.imprint","INTERSECT",VERTEX,{"derivedFrom":[subQ1,subQ0]});Q842=makeQuery(id+"F0.imprint","IMPRINT",FACE,{"disambiguationData":[TD([[makeQuery(id+"F0.imprint","IMPRINT",EDGE,{"disambiguationData":[TD([[subQ2,-1.0]])],"derivedFrom":subQ1}),1.0]])]});}
            var Q843;
            {var subQ0=sQuery(id+"F0.wireOp",EDGE,"E56");var subQ1=sQuery(id+"F0.wireOp",EDGE,"E28");var subQ2=makeQuery(id+"F0.imprint","INTERSECT",VERTEX,{"derivedFrom":[subQ1,subQ0]});Q843=makeQuery(id+"F0.imprint","IMPRINT",FACE,{"disambiguationData":[TD([[makeQuery(id+"F0.imprint","IMPRINT",EDGE,{"disambiguationData":[TD([[subQ2,-1.0]])],"derivedFrom":subQ1}),-1.0]])]});}
            var Q844;
            {var subQ0=sQuery(id+"F0.wireOp",EDGE,"E49");var subQ1=sQuery(id+"F0.wireOp",EDGE,"E22");var subQ2=makeQuery(id+"F0.imprint","INTERSECT",VERTEX,{"derivedFrom":[subQ1,subQ0]});Q844=makeQuery(id+"F0.imprint","IMPRINT",FACE,{"disambiguationData":[TD([[makeQuery(id+"F0.imprint","IMPRINT",EDGE,{"disambiguationData":[TD([[subQ2,-1.0]])],"derivedFrom":subQ1}),1.0]])]});}
            var Q845;
            {var subQ0=sQuery(id+"F0.wireOp",EDGE,"E56");var subQ1=sQuery(id+"F0.wireOp",EDGE,"E28");var subQ2=makeQuery(id+"F0.imprint","INTERSECT",VERTEX,{"derivedFrom":[subQ1,subQ0]});Q845=makeQuery(id+"F0.imprint","IMPRINT",FACE,{"disambiguationData":[TD([[makeQuery(id+"F0.imprint","IMPRINT",EDGE,{"disambiguationData":[TD([[subQ2,-1.0]])],"derivedFrom":subQ1}),1.0]])]});}
            var Q846;
            {var subQ0=sQuery(id+"F0.wireOp",EDGE,"E58");var subQ1=sQuery(id+"F0.wireOp",EDGE,"E39");var subQ2=makeQuery(id+"F0.imprint","INTERSECT",VERTEX,{"derivedFrom":[subQ1,subQ0]});Q846=makeQuery(id+"F0.imprint","IMPRINT",FACE,{"disambiguationData":[TD([[makeQuery(id+"F0.imprint","IMPRINT",EDGE,{"disambiguationData":[TD([[subQ2,-1.0]])],"derivedFrom":subQ1}),-1.0]])]});}
            var Q847;
            {var subQ3=sQuery(id+"F0.wireOp",EDGE,"E46");var subQ5=sQuery(id+"F0.wireOp",EDGE,"E17");var subQ6=makeQuery(id+"F0.imprint","INTERSECT",VERTEX,{"derivedFrom":[subQ5,subQ3]});Q847=makeQuery(id+"F0.imprint","IMPRINT",FACE,{"disambiguationData":[TD([[makeQuery(id+"F0.imprint","IMPRINT",EDGE,{"disambiguationData":[TD([[subQ6,-1.0]])],"derivedFrom":subQ5}),-1.0]])]});}
            var Q848;
            {var subQ0=sQuery(id+"F0.wireOp",EDGE,"E26");var subQ1=sQuery(id+"F0.wireOp",EDGE,"E22");var subQ2=makeQuery(id+"F0.imprint","INTERSECT",VERTEX,{"derivedFrom":[subQ1,subQ0]});Q848=makeQuery(id+"F0.imprint","IMPRINT",FACE,{"disambiguationData":[TD([[makeQuery(id+"F0.imprint","IMPRINT",EDGE,{"disambiguationData":[TD([[subQ2,-1.0]])],"derivedFrom":subQ1}),-1.0]])]});}
            var Q849;
            {var subQ0=sQuery(id+"F0.wireOp",EDGE,"E44");var subQ1=sQuery(id+"F0.wireOp",EDGE,"E27");var subQ2=makeQuery(id+"F0.imprint","INTERSECT",VERTEX,{"derivedFrom":[subQ1,subQ0]});Q849=makeQuery(id+"F0.imprint","IMPRINT",FACE,{"disambiguationData":[TD([[makeQuery(id+"F0.imprint","IMPRINT",EDGE,{"disambiguationData":[TD([[subQ2,-1.0]])],"derivedFrom":subQ1}),-1.0]])]});}
            var Q850;
            {var subQ0=sQuery(id+"F0.wireOp",EDGE,"E24");var subQ1=sQuery(id+"F0.wireOp",EDGE,"E1");var subQ2=makeQuery(id+"F0.imprint","INTERSECT",VERTEX,{"derivedFrom":[subQ1,subQ0]});Q850=makeQuery(id+"F0.imprint","IMPRINT",FACE,{"disambiguationData":[TD([[makeQuery(id+"F0.imprint","IMPRINT",EDGE,{"disambiguationData":[TD([[subQ2,-1.0]])],"derivedFrom":subQ1}),-1.0]])]});}
            var Q851;
            {var subQ5=sQuery(id+"F0.wireOp",EDGE,"E47");var subQ6=sQuery(id+"F0.wireOp",EDGE,"E21");var subQ7=makeQuery(id+"F0.imprint","INTERSECT",VERTEX,{"derivedFrom":[subQ6,subQ5]});Q851=makeQuery(id+"F0.imprint","IMPRINT",FACE,{"disambiguationData":[TD([[makeQuery(id+"F0.imprint","IMPRINT",EDGE,{"disambiguationData":[TD([[subQ7,-1.0]])],"derivedFrom":subQ6}),1.0]])]});}
            var Q852;
            {var subQ0=sQuery(id+"F0.wireOp",EDGE,"E26");var subQ1=sQuery(id+"F0.wireOp",EDGE,"E21");var subQ2=makeQuery(id+"F0.imprint","INTERSECT",VERTEX,{"derivedFrom":[subQ1,subQ0]});Q852=makeQuery(id+"F0.imprint","IMPRINT",FACE,{"disambiguationData":[TD([[makeQuery(id+"F0.imprint","IMPRINT",EDGE,{"disambiguationData":[TD([[subQ2,-1.0]])],"derivedFrom":subQ1}),-1.0]])]});}
            var Q853;
            {var subQ0=sQuery(id+"F0.wireOp",EDGE,"E13");var subQ1=sQuery(id+"F0.wireOp",EDGE,"E11");var subQ2=makeQuery(id+"F0.imprint","INTERSECT",VERTEX,{"derivedFrom":[subQ1,subQ0]});Q853=makeQuery(id+"F0.imprint","IMPRINT",FACE,{"disambiguationData":[TD([[makeQuery(id+"F0.imprint","IMPRINT",EDGE,{"disambiguationData":[TD([[subQ2,-1.0]])],"derivedFrom":subQ1}),1.0]])]});}
            var Q854;
            {var subQ0=sQuery(id+"F0.wireOp",EDGE,"E45");var subQ1=sQuery(id+"F0.wireOp",EDGE,"E16");var subQ2=makeQuery(id+"F0.imprint","INTERSECT",VERTEX,{"derivedFrom":[subQ1,subQ0]});Q854=makeQuery(id+"F0.imprint","IMPRINT",FACE,{"disambiguationData":[TD([[makeQuery(id+"F0.imprint","IMPRINT",EDGE,{"disambiguationData":[TD([[subQ2,-1.0]])],"derivedFrom":subQ1}),-1.0]])]});}
            var Q855;
            {var subQ0=sQuery(id+"F0.wireOp",EDGE,"E14");var subQ1=sQuery(id+"F0.wireOp",EDGE,"E13");var subQ2=makeQuery(id+"F0.imprint","INTERSECT",VERTEX,{"derivedFrom":[subQ1,subQ0]});Q855=makeQuery(id+"F0.imprint","IMPRINT",FACE,{"disambiguationData":[TD([[makeQuery(id+"F0.imprint","IMPRINT",EDGE,{"disambiguationData":[TD([[subQ2,-1.0]])],"derivedFrom":subQ1}),1.0]])]});}
            var Q856;
            {var subQ0=sQuery(id+"F0.wireOp",EDGE,"E46");var subQ1=sQuery(id+"F0.wireOp",EDGE,"E20");var subQ2=makeQuery(id+"F0.imprint","INTERSECT",VERTEX,{"derivedFrom":[subQ1,subQ0]});Q856=makeQuery(id+"F0.imprint","IMPRINT",FACE,{"disambiguationData":[TD([[makeQuery(id+"F0.imprint","IMPRINT",EDGE,{"disambiguationData":[TD([[subQ2,-1.0]])],"derivedFrom":subQ1}),-1.0]])]});}
            var Q857;
            {var subQ0=sQuery(id+"F0.wireOp",EDGE,"E53");var subQ1=sQuery(id+"F0.wireOp",EDGE,"E25");var subQ2=makeQuery(id+"F0.imprint","INTERSECT",VERTEX,{"derivedFrom":[subQ1,subQ0]});Q857=makeQuery(id+"F0.imprint","IMPRINT",FACE,{"disambiguationData":[TD([[makeQuery(id+"F0.imprint","IMPRINT",EDGE,{"disambiguationData":[TD([[subQ2,-1.0]])],"derivedFrom":subQ1}),1.0]])]});}
            var Q858;
            {var subQ0=sQuery(id+"F0.wireOp",EDGE,"E47");var subQ1=sQuery(id+"F0.wireOp",EDGE,"E21");var subQ2=makeQuery(id+"F0.imprint","INTERSECT",VERTEX,{"derivedFrom":[subQ1,subQ0]});Q858=makeQuery(id+"F0.imprint","IMPRINT",FACE,{"disambiguationData":[TD([[makeQuery(id+"F0.imprint","IMPRINT",EDGE,{"disambiguationData":[TD([[subQ2,-1.0]])],"derivedFrom":subQ1}),-1.0]])]});}
            var Q859;
            {var subQ0=sQuery(id+"F0.wireOp",EDGE,"E36");var subQ1=sQuery(id+"F0.wireOp",EDGE,"E28");var subQ2=makeQuery(id+"F0.imprint","INTERSECT",VERTEX,{"derivedFrom":[subQ1,subQ0]});Q859=makeQuery(id+"F0.imprint","IMPRINT",FACE,{"disambiguationData":[TD([[makeQuery(id+"F0.imprint","IMPRINT",EDGE,{"disambiguationData":[TD([[subQ2,-1.0]])],"derivedFrom":subQ1}),-1.0]])]});}
            var Q860;
            {var subQ0=sQuery(id+"F0.wireOp",EDGE,"E44");var subQ1=sQuery(id+"F0.wireOp",EDGE,"E18");var subQ2=makeQuery(id+"F0.imprint","INTERSECT",VERTEX,{"derivedFrom":[subQ1,subQ0]});Q860=makeQuery(id+"F0.imprint","IMPRINT",FACE,{"disambiguationData":[TD([[makeQuery(id+"F0.imprint","IMPRINT",EDGE,{"disambiguationData":[TD([[subQ2,-1.0]])],"derivedFrom":subQ1}),-1.0]])]});}
            var Q861;
            {var subQ0=sQuery(id+"F0.wireOp",EDGE,"E49");var subQ1=sQuery(id+"F0.wireOp",EDGE,"E25");var subQ2=makeQuery(id+"F0.imprint","INTERSECT",VERTEX,{"derivedFrom":[subQ1,subQ0]});Q861=makeQuery(id+"F0.imprint","IMPRINT",FACE,{"disambiguationData":[TD([[makeQuery(id+"F0.imprint","IMPRINT",EDGE,{"disambiguationData":[TD([[subQ2,-1.0]])],"derivedFrom":subQ1}),1.0]])]});}
            var Q862;
            {var subQ0=sQuery(id+"F0.wireOp",EDGE,"E48");var subQ1=sQuery(id+"F0.wireOp",EDGE,"E25");var subQ2=makeQuery(id+"F0.imprint","INTERSECT",VERTEX,{"derivedFrom":[subQ1,subQ0]});Q862=makeQuery(id+"F0.imprint","IMPRINT",FACE,{"disambiguationData":[TD([[makeQuery(id+"F0.imprint","IMPRINT",EDGE,{"disambiguationData":[TD([[subQ2,-1.0]])],"derivedFrom":subQ1}),1.0]])]});}
            var Q863;
            {var subQ0=sQuery(id+"F0.wireOp",EDGE,"E27");var subQ1=sQuery(id+"F0.wireOp",EDGE,"E19");var subQ2=makeQuery(id+"F0.imprint","INTERSECT",VERTEX,{"derivedFrom":[subQ1,subQ0]});Q863=makeQuery(id+"F0.imprint","IMPRINT",FACE,{"disambiguationData":[TD([[makeQuery(id+"F0.imprint","IMPRINT",EDGE,{"disambiguationData":[TD([[subQ2,-1.0]])],"derivedFrom":subQ1}),-1.0]])]});}
            var Q864;
            {var subQ0=sQuery(id+"F0.wireOp",EDGE,"E58");var subQ1=sQuery(id+"F0.wireOp",EDGE,"E38");var subQ2=makeQuery(id+"F0.imprint","INTERSECT",VERTEX,{"derivedFrom":[subQ1,subQ0]});Q864=makeQuery(id+"F0.imprint","IMPRINT",FACE,{"disambiguationData":[TD([[makeQuery(id+"F0.imprint","IMPRINT",EDGE,{"disambiguationData":[TD([[subQ2,-1.0]])],"derivedFrom":subQ1}),1.0]])]});}
            var Q865;
            {var subQ1=sQuery(id+"F0.wireOp",EDGE,"E28");var subQ3=sQuery(id+"F0.wireOp",EDGE,"E45");var subQ4=makeQuery(id+"F0.imprint","INTERSECT",VERTEX,{"derivedFrom":[subQ1,subQ3]});Q865=makeQuery(id+"F0.imprint","IMPRINT",FACE,{"disambiguationData":[TD([[makeQuery(id+"F0.imprint","IMPRINT",EDGE,{"disambiguationData":[TD([[subQ4,1.0]])],"derivedFrom":subQ3}),1.0]])]});}
            var Q866;
            {var subQ0=sQuery(id+"F0.wireOp",EDGE,"E56");var subQ1=sQuery(id+"F0.wireOp",EDGE,"E37");var subQ2=makeQuery(id+"F0.imprint","INTERSECT",VERTEX,{"derivedFrom":[subQ1,subQ0]});Q866=makeQuery(id+"F0.imprint","IMPRINT",FACE,{"disambiguationData":[TD([[makeQuery(id+"F0.imprint","IMPRINT",EDGE,{"disambiguationData":[TD([[subQ2,-1.0]])],"derivedFrom":subQ1}),-1.0]])]});}
            var Q867;
            {var subQ0=sQuery(id+"F0.wireOp",EDGE,"E46");var subQ1=sQuery(id+"F0.wireOp",EDGE,"E26");var subQ2=makeQuery(id+"F0.imprint","INTERSECT",VERTEX,{"derivedFrom":[subQ1,subQ0]});Q867=makeQuery(id+"F0.imprint","IMPRINT",FACE,{"disambiguationData":[TD([[makeQuery(id+"F0.imprint","IMPRINT",EDGE,{"disambiguationData":[TD([[subQ2,-1.0]])],"derivedFrom":subQ1}),-1.0]])]});}
            var Q868;
            {var subQ0=sQuery(id+"F0.wireOp",EDGE,"E46");var subQ1=sQuery(id+"F0.wireOp",EDGE,"E18");var subQ2=makeQuery(id+"F0.imprint","INTERSECT",VERTEX,{"derivedFrom":[subQ1,subQ0]});Q868=makeQuery(id+"F0.imprint","IMPRINT",FACE,{"disambiguationData":[TD([[makeQuery(id+"F0.imprint","IMPRINT",EDGE,{"disambiguationData":[TD([[subQ2,-1.0]])],"derivedFrom":subQ1}),1.0]])]});}
            var Q869;
            {var subQ0=sQuery(id+"F0.wireOp",EDGE,"E45");var subQ1=sQuery(id+"F0.wireOp",EDGE,"E28");var subQ2=makeQuery(id+"F0.imprint","INTERSECT",VERTEX,{"derivedFrom":[subQ1,subQ0]});Q869=makeQuery(id+"F0.imprint","IMPRINT",FACE,{"disambiguationData":[TD([[makeQuery(id+"F0.imprint","IMPRINT",EDGE,{"disambiguationData":[TD([[subQ2,-1.0]])],"derivedFrom":subQ1}),-1.0]])]});}
            var Q870;
            {var subQ1=sQuery(id+"F0.wireOp",EDGE,"E28");var subQ5=sQuery(id+"F0.wireOp",EDGE,"E53");var subQ6=makeQuery(id+"F0.imprint","INTERSECT",VERTEX,{"derivedFrom":[subQ1,subQ5]});Q870=makeQuery(id+"F0.imprint","IMPRINT",FACE,{"disambiguationData":[TD([[makeQuery(id+"F0.imprint","IMPRINT",EDGE,{"disambiguationData":[TD([[subQ6,-1.0]])],"derivedFrom":subQ1}),1.0]])]});}
            var Q871;
            {var subQ0=sQuery(id+"F0.wireOp",EDGE,"E54");var subQ1=sQuery(id+"F0.wireOp",EDGE,"E28");var subQ2=makeQuery(id+"F0.imprint","INTERSECT",VERTEX,{"derivedFrom":[subQ1,subQ0]});Q871=makeQuery(id+"F0.imprint","IMPRINT",FACE,{"disambiguationData":[TD([[makeQuery(id+"F0.imprint","IMPRINT",EDGE,{"disambiguationData":[TD([[subQ2,-1.0]])],"derivedFrom":subQ1}),-1.0]])]});}
            var Q872;
            {var subQ0=sQuery(id+"F0.wireOp",EDGE,"E57");var subQ1=sQuery(id+"F0.wireOp",EDGE,"E28");var subQ2=makeQuery(id+"F0.imprint","INTERSECT",VERTEX,{"derivedFrom":[subQ1,subQ0]});Q872=makeQuery(id+"F0.imprint","IMPRINT",FACE,{"disambiguationData":[TD([[makeQuery(id+"F0.imprint","IMPRINT",EDGE,{"disambiguationData":[TD([[subQ2,-1.0]])],"derivedFrom":subQ1}),-1.0]])]});}
            var Q873;
            {var subQ0=sQuery(id+"F0.wireOp",EDGE,"E57");var subQ1=sQuery(id+"F0.wireOp",EDGE,"E26");var subQ2=makeQuery(id+"F0.imprint","INTERSECT",VERTEX,{"derivedFrom":[subQ1,subQ0]});Q873=makeQuery(id+"F0.imprint","IMPRINT",FACE,{"disambiguationData":[TD([[makeQuery(id+"F0.imprint","IMPRINT",EDGE,{"disambiguationData":[TD([[subQ2,-1.0]])],"derivedFrom":subQ1}),1.0]])]});}
            var Q874;
            {var subQ0=sQuery(id+"F0.wireOp",EDGE,"E54");var subQ1=sQuery(id+"F0.wireOp",EDGE,"E28");var subQ2=makeQuery(id+"F0.imprint","INTERSECT",VERTEX,{"derivedFrom":[subQ1,subQ0]});Q874=makeQuery(id+"F0.imprint","IMPRINT",FACE,{"disambiguationData":[TD([[makeQuery(id+"F0.imprint","IMPRINT",EDGE,{"disambiguationData":[TD([[subQ2,-1.0]])],"derivedFrom":subQ1}),1.0]])]});}
            var Q875;
            {var subQ0=sQuery(id+"F0.wireOp",EDGE,"E45");var subQ1=sQuery(id+"F0.wireOp",EDGE,"E24");var subQ2=makeQuery(id+"F0.imprint","INTERSECT",VERTEX,{"derivedFrom":[subQ1,subQ0]});Q875=makeQuery(id+"F0.imprint","IMPRINT",FACE,{"disambiguationData":[TD([[makeQuery(id+"F0.imprint","IMPRINT",EDGE,{"disambiguationData":[TD([[subQ2,-1.0]])],"derivedFrom":subQ1}),1.0]])]});}
            var Q876;
            {var subQ0=sQuery(id+"F0.wireOp",EDGE,"E29");var subQ1=sQuery(id+"F0.wireOp",EDGE,"E12");var subQ2=makeQuery(id+"F0.imprint","INTERSECT",VERTEX,{"derivedFrom":[subQ1,subQ0]});Q876=makeQuery(id+"F0.imprint","IMPRINT",FACE,{"disambiguationData":[TD([[makeQuery(id+"F0.imprint","IMPRINT",EDGE,{"disambiguationData":[TD([[subQ2,-1.0]])],"derivedFrom":subQ1}),-1.0]])]});}
            var Q877;
            {var subQ0=sQuery(id+"F0.wireOp",EDGE,"E56");var subQ1=sQuery(id+"F0.wireOp",EDGE,"E52");var subQ2=makeQuery(id+"F0.imprint","INTERSECT",VERTEX,{"derivedFrom":[subQ1,subQ0]});Q877=makeQuery(id+"F0.imprint","IMPRINT",FACE,{"disambiguationData":[TD([[makeQuery(id+"F0.imprint","IMPRINT",EDGE,{"disambiguationData":[TD([[subQ2,-1.0]])],"derivedFrom":subQ1}),-1.0]])]});}
            var Q878;
            {var subQ0=sQuery(id+"F0.wireOp",EDGE,"E56");var subQ1=sQuery(id+"F0.wireOp",EDGE,"E26");var subQ2=makeQuery(id+"F0.imprint","INTERSECT",VERTEX,{"derivedFrom":[subQ1,subQ0]});Q878=makeQuery(id+"F0.imprint","IMPRINT",FACE,{"disambiguationData":[TD([[makeQuery(id+"F0.imprint","IMPRINT",EDGE,{"disambiguationData":[TD([[subQ2,-1.0]])],"derivedFrom":subQ1}),1.0]])]});}
            var Q879;
            {var subQ0=sQuery(id+"F0.wireOp",EDGE,"E57");var subQ1=sQuery(id+"F0.wireOp",EDGE,"E36");var subQ2=makeQuery(id+"F0.imprint","INTERSECT",VERTEX,{"derivedFrom":[subQ1,subQ0]});Q879=makeQuery(id+"F0.imprint","IMPRINT",FACE,{"disambiguationData":[TD([[makeQuery(id+"F0.imprint","IMPRINT",EDGE,{"disambiguationData":[TD([[subQ2,-1.0]])],"derivedFrom":subQ1}),-1.0]])]});}
            extrude(context, id + "F1", {"entities" : qUnion([Q0, Q1, Q2, Q3, Q4, Q5, Q6, Q7, Q8, Q9, Q10, Q11, Q12, Q13, Q14, Q15, Q16, Q17, Q18, Q19, Q20, Q21, Q22, Q23, Q24, Q25, Q26, Q27, Q28, Q29, Q30, Q31, Q32, Q33, Q34, Q35, Q36, Q37, Q38, Q39, Q40, Q41, Q42, Q43, Q44, Q45, Q46, Q47, Q48, Q49, Q50, Q51, Q52, Q53, Q54, Q55, Q56, Q57, Q58, Q59, Q60, Q61, Q62, Q63, Q64, Q65, Q66, Q67, Q68, Q69, Q70, Q71, Q72, Q73, Q74, Q75, Q76, Q77, Q78, Q79, Q80, Q81, Q82, Q83, Q84, Q85, Q86, Q87, Q88, Q89, Q90, Q91, Q92, Q93, Q94, Q95, Q96, Q97, Q98, Q99, Q100, Q101, Q102, Q103, Q104, Q105, Q106, Q107, Q108, Q109, Q110, Q111, Q112, Q113, Q114, Q115, Q116, Q117, Q118, Q119, Q120, Q121, Q122, Q123, Q124, Q125, Q126, Q127, Q128, Q129, Q130, Q131, Q132, Q133, Q134, Q135, Q136, Q137, Q138, Q139, Q140, Q141, Q142, Q143, Q144, Q145, Q146, Q147, Q148, Q149, Q150, Q151, Q152, Q153, Q154, Q155, Q156, Q157, Q158, Q159, Q160, Q161, Q162, Q163, Q164, Q165, Q166, Q167, Q168, Q169, Q170, Q171, Q172, Q173, Q174, Q175, Q176, Q177, Q178, Q179, Q180, Q181, Q182, Q183, Q184, Q185, Q186, Q187, Q188, Q189, Q190, Q191, Q192, Q193, Q194, Q195, Q196, Q197, Q198, Q199, Q200, Q201, Q202, Q203, Q204, Q205, Q206, Q207, Q208, Q209, Q210, Q211, Q212, Q213, Q214, Q215, Q216, Q217, Q218, Q219, Q220, Q221, Q222, Q223, Q224, Q225, Q226, Q227, Q228, Q229, Q230, Q231, Q232, Q233, Q234, Q235, Q236, Q237, Q238, Q239, Q240, Q241, Q242, Q243, Q244, Q245, Q246, Q247, Q248, Q249, Q250, Q251, Q252, Q253, Q254, Q255, Q256, Q257, Q258, Q259, Q260, Q261, Q262, Q263, Q264, Q265, Q266, Q267, Q268, Q269, Q270, Q271, Q272, Q273, Q274, Q275, Q276, Q277, Q278, Q279, Q280, Q281, Q282, Q283, Q284, Q285, Q286, Q287, Q288, Q289, Q290, Q291, Q292, Q293, Q294, Q295, Q296, Q297, Q298, Q299, Q300, Q301, Q302, Q303, Q304, Q305, Q306, Q307, Q308, Q309, Q310, Q311, Q312, Q313, Q314, Q315, Q316, Q317, Q318, Q319, Q320, Q321, Q322, Q323, Q324, Q325, Q326, Q327, Q328, Q329, Q330, Q331, Q332, Q333, Q334, Q335, Q336, Q337, Q338, Q339, Q340, Q341, Q342, Q343, Q344, Q345, Q346, Q347, Q348, Q349, Q350, Q351, Q352, Q353, Q354, Q355, Q356, Q357, Q358, Q359, Q360, Q361, Q362, Q363, Q364, Q365, Q366, Q367, Q368, Q369, Q370, Q371, Q372, Q373, Q374, Q375, Q376, Q377, Q378, Q379, Q380, Q381, Q382, Q383, Q384, Q385, Q386, Q387, Q388, Q389, Q390, Q391, Q392, Q393, Q394, Q395, Q396, Q397, Q398, Q399, Q400, Q401, Q402, Q403, Q404, Q405, Q406, Q407, Q408, Q409, Q410, Q411, Q412, Q413, Q414, Q415, Q416, Q417, Q418, Q419, Q420, Q421, Q422, Q423, Q424, Q425, Q426, Q427, Q428, Q429, Q430, Q431, Q432, Q433, Q434, Q435, Q436, Q437, Q438, Q439, Q440, Q441, Q442, Q443, Q444, Q445, Q446, Q447, Q448, Q449, Q450, Q451, Q452, Q453, Q454, Q455, Q456, Q457, Q458, Q459, Q460, Q461, Q462, Q463, Q464, Q465, Q466, Q467, Q468, Q469, Q470, Q471, Q472, Q473, Q474, Q475, Q476, Q477, Q478, Q479, Q480, Q481, Q482, Q483, Q484, Q485, Q486, Q487, Q488, Q489, Q490, Q491, Q492, Q493, Q494, Q495, Q496, Q497, Q498, Q499, Q500, Q501, Q502, Q503, Q504, Q505, Q506, Q507, Q508, Q509, Q510, Q511, Q512, Q513, Q514, Q515, Q516, Q517, Q518, Q519, Q520, Q521, Q522, Q523, Q524, Q525, Q526, Q527, Q528, Q529, Q530, Q531, Q532, Q533, Q534, Q535, Q536, Q537, Q538, Q539, Q540, Q541, Q542, Q543, Q544, Q545, Q546, Q547, Q548, Q549, Q550, Q551, Q552, Q553, Q554, Q555, Q556, Q557, Q558, Q559, Q560, Q561, Q562, Q563, Q564, Q565, Q566, Q567, Q568, Q569, Q570, Q571, Q572, Q573, Q574, Q575, Q576, Q577, Q578, Q579, Q580, Q581, Q582, Q583, Q584, Q585, Q586, Q587, Q588, Q589, Q590, Q591, Q592, Q593, Q594, Q595, Q596, Q597, Q598, Q599, Q600, Q601, Q602, Q603, Q604, Q605, Q606, Q607, Q608, Q609, Q610, Q611, Q612, Q613, Q614, Q615, Q616, Q617, Q618, Q619, Q620, Q621, Q622, Q623, Q624, Q625, Q626, Q627, Q628, Q629, Q630, Q631, Q632, Q633, Q634, Q635, Q636, Q637, Q638, Q639, Q640, Q641, Q642, Q643, Q644, Q645, Q646, Q647, Q648, Q649, Q650, Q651, Q652, Q653, Q654, Q655, Q656, Q657, Q658, Q659, Q660, Q661, Q662, Q663, Q664, Q665, Q666, Q667, Q668, Q669, Q670, Q671, Q672, Q673, Q674, Q675, Q676, Q677, Q678, Q679, Q680, Q681, Q682, Q683, Q684, Q685, Q686, Q687, Q688, Q689, Q690, Q691, Q692, Q693, Q694, Q695, Q696, Q697, Q698, Q699, Q700, Q701, Q702, Q703, Q704, Q705, Q706, Q707, Q708, Q709, Q710, Q711, Q712, Q713, Q714, Q715, Q716, Q717, Q718, Q719, Q720, Q721, Q722, Q723, Q724, Q725, Q726, Q727, Q728, Q729, Q730, Q731, Q732, Q733, Q734, Q735, Q736, Q737, Q738, Q739, Q740, Q741, Q742, Q743, Q744, Q745, Q746, Q747, Q748, Q749, Q750, Q751, Q752, Q753, Q754, Q755, Q756, Q757, Q758, Q759, Q760, Q761, Q762, Q763, Q764, Q765, Q766, Q767, Q768, Q769, Q770, Q771, Q772, Q773, Q774, Q775, Q776, Q777, Q778, Q779, Q780, Q781, Q782, Q783, Q784, Q785, Q786, Q787, Q788, Q789, Q790, Q791, Q792, Q793, Q794, Q795, Q796, Q797, Q798, Q799, Q800, Q801, Q802, Q803, Q804, Q805, Q806, Q807, Q808, Q809, Q810, Q811, Q812, Q813, Q814, Q815, Q816, Q817, Q818, Q819, Q820, Q821, Q822, Q823, Q824, Q825, Q826, Q827, Q828, Q829, Q830, Q831, Q832, Q833, Q834, Q835, Q836, Q837, Q838, Q839, Q840, Q841, Q842, Q843, Q844, Q845, Q846, Q847, Q848, Q849, Q850, Q851, Q852, Q853, Q854, Q855, Q856, Q857, Q858, Q859, Q860, Q861, Q862, Q863, Q864, Q865, Q866, Q867, Q868, Q869, Q870, Q871, Q872, Q873, Q874, Q875, Q876, Q877, Q878, Q879]), "endBound" : BoundingType.SYMMETRIC, "depth" : 25.4 * mm, "offsetDistance" : 25.4 * mm});
        }
        {
            var Q0;
            Q0=makeQuery(id+"F1.opExtrude","CAP_FACE",FACE,{"disambiguationData":[OSD([sQuery(id+"F0.wireOp",EDGE,"E0.bottom"),sQuery(id+"F0.wireOp",EDGE,"E0.top"),sQuery(id+"F0.wireOp",EDGE,"E0.left"),sQuery(id+"F0.wireOp",EDGE,"E0.right"),sQuery(id+"F0.wireOp",EDGE,"E59")])],"isStart":false});
            var sketch = newSketch(context, id + "F2", { "sketchPlane" : qUnion([Q0])});
            skLineSegment(sketch, "E60", {"start": v(63.5, 38.1) * mm, "end": v(58.63, -38.1) * mm});
            skLineSegment(sketch, "E61", {"start": v(63.5, 31.74) * mm, "end": v(48.94, -38.1) * mm});
            skLineSegment(sketch, "E62", {"start": v(63.5, 25.72) * mm, "end": v(38.21, -38.1) * mm});
            skLineSegment(sketch, "E63", {"start": v(63.5, 15.73) * mm, "end": v(32.2, -38.1) * mm});
            skLineSegment(sketch, "E64", {"start": v(63.5, 7.21) * mm, "end": v(23.53, -38.1) * mm});
            skLineSegment(sketch, "E65", {"start": v(63.5, 1.2) * mm, "end": v(14.27, -38.1) * mm});
            skLineSegment(sketch, "E66", {"start": v(63.5, -6.6) * mm, "end": v(0, -38.1) * mm});
            skLineSegment(sketch, "E67", {"start": v(63.5, -14.23) * mm, "end": v(-15.4, -38.1) * mm});
            skLineSegment(sketch, "E68", {"start": v(63.5, -21.87) * mm, "end": v(-27.88, -38.1) * mm});
            skLineSegment(sketch, "E69", {"start": v(63.5, -27.3) * mm, "end": v(-42.72, -38.1) * mm});
            skLineSegment(sketch, "E70", {"start": v(63.5, -32.15) * mm, "end": v(-63.5, -38.1) * mm});
            skLineSegment(sketch, "E71", {"start": v(-63.5, -38.1) * mm, "end": v(-55.56, 38.1) * mm});
            skLineSegment(sketch, "E72", {"start": v(-63.5, -26.74) * mm, "end": v(-45.96, 38.1) * mm});
            skLineSegment(sketch, "E73", {"start": v(-63.5, -17.07) * mm, "end": v(-36.73, 38.1) * mm});
            skLineSegment(sketch, "E74", {"start": v(-63.5, -7.86) * mm, "end": v(-31.9, 38.1) * mm});
            skLineSegment(sketch, "E75", {"start": v(-63.5, 0) * mm, "end": v(-18.61, 38.1) * mm});
            skLineSegment(sketch, "E76", {"start": v(-63.5, 7.38) * mm, "end": v(0, 38.1) * mm});
            skLineSegment(sketch, "E77", {"start": v(-63.5, 13.66) * mm, "end": v(14.3, 38.1) * mm});
            skLineSegment(sketch, "E78", {"start": v(-63.5, 20.94) * mm, "end": v(28.02, 38.1) * mm});
            skLineSegment(sketch, "E79", {"start": v(-63.5, 27.73) * mm, "end": v(43.76, 38.1) * mm});
            skLineSegment(sketch, "E80", {"start": v(-63.5, 33.08) * mm, "end": v(63.5, 38.1) * mm});
            skSolve(sketch);
        }
        {
            var Q0;
            Q0 = qSketchRegion(id + "F2", true);
            extrude(context, id + "F3", {"entities" : qUnion([Q0]), "operationType" : NewBodyOperationType.ADD, "depth" : 2.54 * mm, "offsetDistance" : 25.4 * mm});
        }
    });
